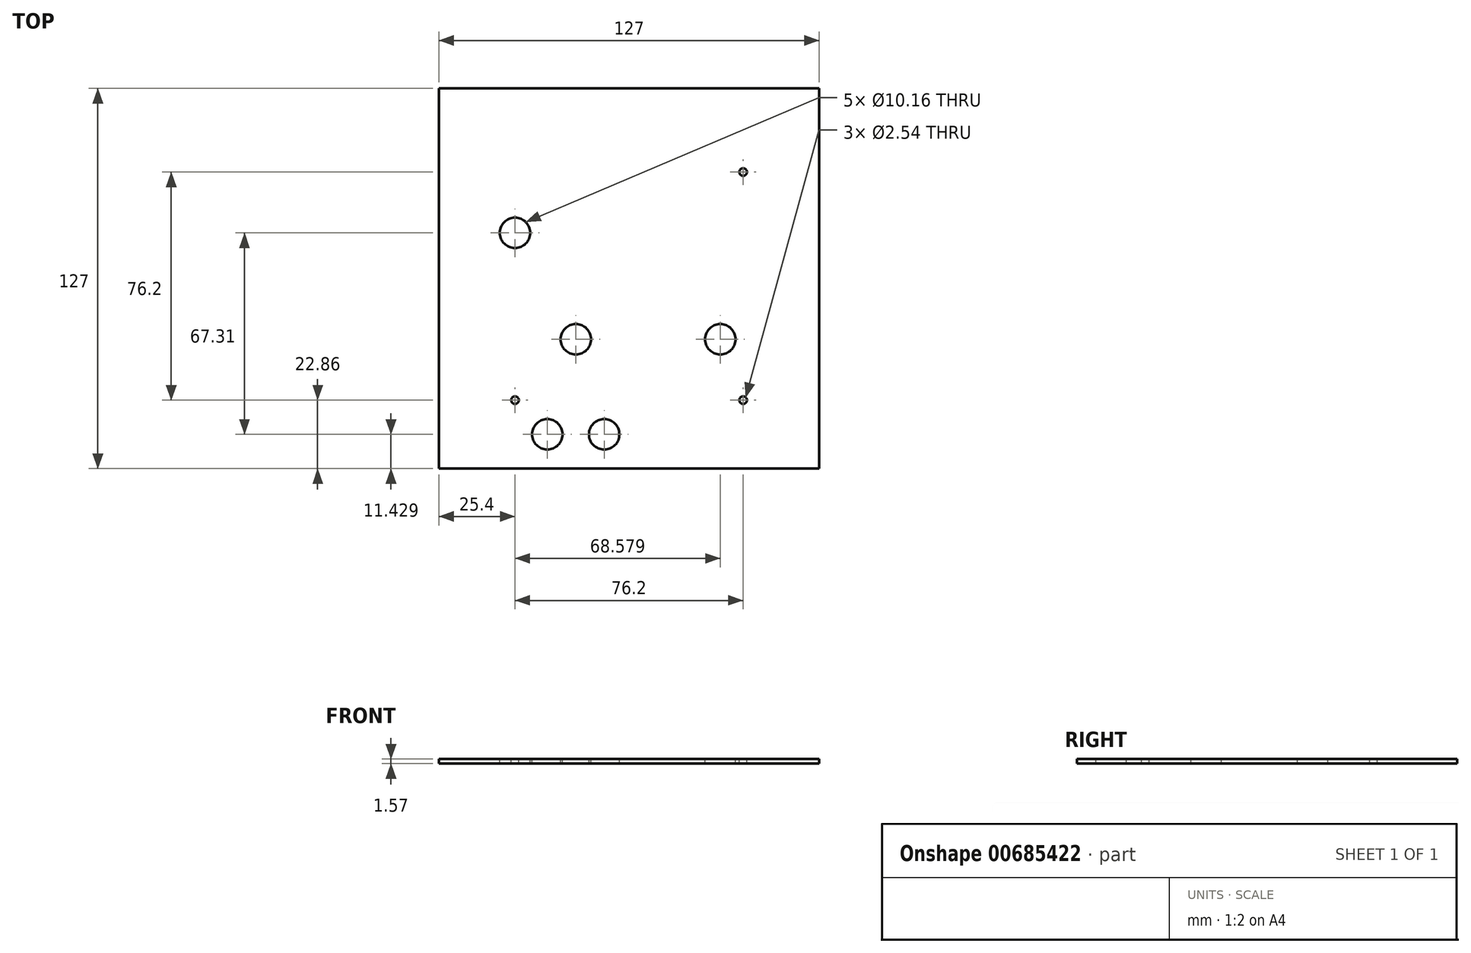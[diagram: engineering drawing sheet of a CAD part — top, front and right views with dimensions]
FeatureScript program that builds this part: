
annotation { "Feature Type Name" : "Feature", "Feature Type Description" : "" }
export const myFeature = defineFeature(function(context is Context, id is Id, definition is map)
    precondition{}
    {
        {
            var Q0;
            Q0=qCreatedBy(makeId("Top.planeOp"),FACE);
            var sketch = newSketch(context, id + "F0", { "sketchPlane" : qUnion([Q0])});
            skLineSegment(sketch, "E0", {"start": v(-9.04, 13.82) * mm, "end": v(-9.04, 13.7) * mm});
            skLineSegment(sketch, "E1", {"start": v(-9.04, 13.7) * mm, "end": v(-9.28, 13.35) * mm});
            skLineSegment(sketch, "E2", {"start": v(-9.28, 13.35) * mm, "end": v(-9.32, 13.32) * mm});
            skLineSegment(sketch, "E3", {"start": v(-9.32, 13.32) * mm, "end": v(-9.37, 13.3) * mm});
            skLineSegment(sketch, "E4", {"start": v(-9.37, 13.3) * mm, "end": v(-9.85, 13.3) * mm});
            skLineSegment(sketch, "E5", {"start": v(-9.85, 13.3) * mm, "end": v(-9.9, 13.32) * mm});
            skLineSegment(sketch, "E6", {"start": v(-9.9, 13.32) * mm, "end": v(-9.94, 13.35) * mm});
            skLineSegment(sketch, "E7", {"start": v(-9.94, 13.35) * mm, "end": v(-10.18, 13.7) * mm});
            skLineSegment(sketch, "E8", {"start": v(-10.18, 13.7) * mm, "end": v(-10.18, 13.82) * mm});
            skLineSegment(sketch, "E9", {"start": v(-10.18, 13.82) * mm, "end": v(-10.18, 13.94) * mm});
            skLineSegment(sketch, "E10", {"start": v(-10.18, 13.94) * mm, "end": v(-9.94, 14.3) * mm});
            skLineSegment(sketch, "E11", {"start": v(-9.94, 14.3) * mm, "end": v(-9.9, 14.31) * mm});
            skLineSegment(sketch, "E12", {"start": v(-9.9, 14.31) * mm, "end": v(-9.85, 14.34) * mm});
            skLineSegment(sketch, "E13", {"start": v(-9.85, 14.34) * mm, "end": v(-9.37, 14.34) * mm});
            skLineSegment(sketch, "E14", {"start": v(-9.37, 14.34) * mm, "end": v(-9.32, 14.31) * mm});
            skLineSegment(sketch, "E15", {"start": v(-9.32, 14.31) * mm, "end": v(-9.28, 14.3) * mm});
            skLineSegment(sketch, "E16", {"start": v(-9.28, 14.3) * mm, "end": v(-9.04, 13.94) * mm});
            skLineSegment(sketch, "E17", {"start": v(-9.04, 13.94) * mm, "end": v(-9.04, 13.82) * mm});
            skLineSegment(sketch, "E18", {"start": v(-52.06, -1.27) * mm, "end": v(-52.06, -1.46) * mm});
            skLineSegment(sketch, "E19", {"start": v(-52.06, -1.46) * mm, "end": v(-52.26, -2.02) * mm});
            skLineSegment(sketch, "E20", {"start": v(-52.26, -2.02) * mm, "end": v(-52.7, -2.5) * mm});
            skLineSegment(sketch, "E21", {"start": v(-52.7, -2.5) * mm, "end": v(-52.8, -2.57) * mm});
            skLineSegment(sketch, "E22", {"start": v(-52.8, -2.57) * mm, "end": v(-52.93, -2.63) * mm});
            skLineSegment(sketch, "E23", {"start": v(-52.93, -2.63) * mm, "end": v(-53.56, -2.77) * mm});
            skLineSegment(sketch, "E24", {"start": v(-53.56, -2.77) * mm, "end": v(-54.2, -2.63) * mm});
            skLineSegment(sketch, "E25", {"start": v(-54.2, -2.63) * mm, "end": v(-54.3, -2.57) * mm});
            skLineSegment(sketch, "E26", {"start": v(-54.3, -2.57) * mm, "end": v(-54.43, -2.5) * mm});
            skLineSegment(sketch, "E27", {"start": v(-54.43, -2.5) * mm, "end": v(-54.86, -2.02) * mm});
            skLineSegment(sketch, "E28", {"start": v(-54.86, -2.02) * mm, "end": v(-55.06, -1.46) * mm});
            skLineSegment(sketch, "E29", {"start": v(-55.06, -1.46) * mm, "end": v(-55.06, -1.27) * mm});
            skLineSegment(sketch, "E30", {"start": v(-55.06, -1.27) * mm, "end": v(-55.06, -1.08) * mm});
            skLineSegment(sketch, "E31", {"start": v(-55.06, -1.08) * mm, "end": v(-54.86, -0.52) * mm});
            skLineSegment(sketch, "E32", {"start": v(-54.86, -0.52) * mm, "end": v(-54.43, -0.04) * mm});
            skLineSegment(sketch, "E33", {"start": v(-54.43, -0.04) * mm, "end": v(-54.3, 0.03) * mm});
            skLineSegment(sketch, "E34", {"start": v(-54.3, 0.03) * mm, "end": v(-54.2, 0.1) * mm});
            skLineSegment(sketch, "E35", {"start": v(-54.2, 0.1) * mm, "end": v(-53.56, 0.23) * mm});
            skLineSegment(sketch, "E36", {"start": v(-53.56, 0.23) * mm, "end": v(-52.93, 0.1) * mm});
            skLineSegment(sketch, "E37", {"start": v(-52.93, 0.1) * mm, "end": v(-52.8, 0.03) * mm});
            skLineSegment(sketch, "E38", {"start": v(-52.8, 0.03) * mm, "end": v(-52.7, -0.04) * mm});
            skLineSegment(sketch, "E39", {"start": v(-52.7, -0.04) * mm, "end": v(-52.26, -0.52) * mm});
            skLineSegment(sketch, "E40", {"start": v(-52.26, -0.52) * mm, "end": v(-52.06, -1.08) * mm});
            skLineSegment(sketch, "E41", {"start": v(-52.06, -1.08) * mm, "end": v(-52.06, -1.27) * mm});
            skLineSegment(sketch, "E42", {"start": v(-52.06, -9.17) * mm, "end": v(-52.06, -9.36) * mm});
            skLineSegment(sketch, "E43", {"start": v(-52.06, -9.36) * mm, "end": v(-52.26, -9.92) * mm});
            skLineSegment(sketch, "E44", {"start": v(-52.26, -9.92) * mm, "end": v(-52.7, -10.4) * mm});
            skLineSegment(sketch, "E45", {"start": v(-52.7, -10.4) * mm, "end": v(-52.8, -10.47) * mm});
            skLineSegment(sketch, "E46", {"start": v(-52.8, -10.47) * mm, "end": v(-52.93, -10.54) * mm});
            skLineSegment(sketch, "E47", {"start": v(-52.93, -10.54) * mm, "end": v(-53.56, -10.67) * mm});
            skLineSegment(sketch, "E48", {"start": v(-53.56, -10.67) * mm, "end": v(-54.2, -10.54) * mm});
            skLineSegment(sketch, "E49", {"start": v(-54.2, -10.54) * mm, "end": v(-54.3, -10.47) * mm});
            skLineSegment(sketch, "E50", {"start": v(-54.3, -10.47) * mm, "end": v(-54.43, -10.4) * mm});
            skLineSegment(sketch, "E51", {"start": v(-54.43, -10.4) * mm, "end": v(-54.86, -9.92) * mm});
            skLineSegment(sketch, "E52", {"start": v(-54.86, -9.92) * mm, "end": v(-55.06, -9.36) * mm});
            skLineSegment(sketch, "E53", {"start": v(-55.06, -9.36) * mm, "end": v(-55.06, -9.17) * mm});
            skLineSegment(sketch, "E54", {"start": v(-55.06, -9.17) * mm, "end": v(-55.06, -8.98) * mm});
            skLineSegment(sketch, "E55", {"start": v(-55.06, -8.98) * mm, "end": v(-54.86, -8.42) * mm});
            skLineSegment(sketch, "E56", {"start": v(-54.86, -8.42) * mm, "end": v(-54.43, -7.94) * mm});
            skLineSegment(sketch, "E57", {"start": v(-54.43, -7.94) * mm, "end": v(-54.3, -7.87) * mm});
            skLineSegment(sketch, "E58", {"start": v(-54.3, -7.87) * mm, "end": v(-54.2, -7.8) * mm});
            skLineSegment(sketch, "E59", {"start": v(-54.2, -7.8) * mm, "end": v(-53.56, -7.67) * mm});
            skLineSegment(sketch, "E60", {"start": v(-53.56, -7.67) * mm, "end": v(-52.93, -7.8) * mm});
            skLineSegment(sketch, "E61", {"start": v(-52.93, -7.8) * mm, "end": v(-52.8, -7.87) * mm});
            skLineSegment(sketch, "E62", {"start": v(-52.8, -7.87) * mm, "end": v(-52.7, -7.94) * mm});
            skLineSegment(sketch, "E63", {"start": v(-52.7, -7.94) * mm, "end": v(-52.26, -8.42) * mm});
            skLineSegment(sketch, "E64", {"start": v(-52.26, -8.42) * mm, "end": v(-52.06, -8.98) * mm});
            skLineSegment(sketch, "E65", {"start": v(-52.06, -8.98) * mm, "end": v(-52.06, -9.17) * mm});
            skLineSegment(sketch, "E66", {"start": v(-38.7, 57.1) * mm, "end": v(-38.7, 56.77) * mm});
            skLineSegment(sketch, "E67", {"start": v(-38.7, 56.77) * mm, "end": v(-38.87, 55.78) * mm});
            skLineSegment(sketch, "E68", {"start": v(-38.87, 55.78) * mm, "end": v(-39.38, 54.56) * mm});
            skLineSegment(sketch, "E69", {"start": v(-39.38, 54.56) * mm, "end": v(-40.18, 53.52) * mm});
            skLineSegment(sketch, "E70", {"start": v(-40.18, 53.52) * mm, "end": v(-40.95, 52.87) * mm});
            skLineSegment(sketch, "E71", {"start": v(-40.95, 52.87) * mm, "end": v(-41.24, 52.7) * mm});
            skLineSegment(sketch, "E72", {"start": v(-41.24, 52.7) * mm, "end": v(-41.52, 52.53) * mm});
            skLineSegment(sketch, "E73", {"start": v(-41.52, 52.53) * mm, "end": v(-42.47, 52.2) * mm});
            skLineSegment(sketch, "E74", {"start": v(-42.47, 52.2) * mm, "end": v(-43.78, 52.02) * mm});
            skLineSegment(sketch, "E75", {"start": v(-43.78, 52.02) * mm, "end": v(-45.08, 52.2) * mm});
            skLineSegment(sketch, "E76", {"start": v(-45.08, 52.2) * mm, "end": v(-46.03, 52.53) * mm});
            skLineSegment(sketch, "E77", {"start": v(-46.03, 52.53) * mm, "end": v(-46.32, 52.7) * mm});
            skLineSegment(sketch, "E78", {"start": v(-46.32, 52.7) * mm, "end": v(-46.6, 52.87) * mm});
            skLineSegment(sketch, "E79", {"start": v(-46.6, 52.87) * mm, "end": v(-47.38, 53.52) * mm});
            skLineSegment(sketch, "E80", {"start": v(-47.38, 53.52) * mm, "end": v(-48.18, 54.56) * mm});
            skLineSegment(sketch, "E81", {"start": v(-48.18, 54.56) * mm, "end": v(-48.68, 55.78) * mm});
            skLineSegment(sketch, "E82", {"start": v(-48.68, 55.78) * mm, "end": v(-48.86, 56.77) * mm});
            skLineSegment(sketch, "E83", {"start": v(-48.86, 56.77) * mm, "end": v(-48.86, 57.1) * mm});
            skLineSegment(sketch, "E84", {"start": v(-48.86, 57.1) * mm, "end": v(-48.86, 57.43) * mm});
            skLineSegment(sketch, "E85", {"start": v(-48.86, 57.43) * mm, "end": v(-48.68, 58.43) * mm});
            skLineSegment(sketch, "E86", {"start": v(-48.68, 58.43) * mm, "end": v(-48.18, 59.64) * mm});
            skLineSegment(sketch, "E87", {"start": v(-48.18, 59.64) * mm, "end": v(-47.38, 60.68) * mm});
            skLineSegment(sketch, "E88", {"start": v(-47.38, 60.68) * mm, "end": v(-46.6, 61.33) * mm});
            skLineSegment(sketch, "E89", {"start": v(-46.6, 61.33) * mm, "end": v(-46.32, 61.5) * mm});
            skLineSegment(sketch, "E90", {"start": v(-46.32, 61.5) * mm, "end": v(-46.03, 61.67) * mm});
            skLineSegment(sketch, "E91", {"start": v(-46.03, 61.67) * mm, "end": v(-45.08, 62.01) * mm});
            skLineSegment(sketch, "E92", {"start": v(-45.08, 62.01) * mm, "end": v(-43.78, 62.18) * mm});
            skLineSegment(sketch, "E93", {"start": v(-43.78, 62.18) * mm, "end": v(-42.47, 62.01) * mm});
            skLineSegment(sketch, "E94", {"start": v(-42.47, 62.01) * mm, "end": v(-41.52, 61.67) * mm});
            skLineSegment(sketch, "E95", {"start": v(-41.52, 61.67) * mm, "end": v(-41.24, 61.5) * mm});
            skLineSegment(sketch, "E96", {"start": v(-41.24, 61.5) * mm, "end": v(-40.95, 61.33) * mm});
            skLineSegment(sketch, "E97", {"start": v(-40.95, 61.33) * mm, "end": v(-40.18, 60.68) * mm});
            skLineSegment(sketch, "E98", {"start": v(-40.18, 60.68) * mm, "end": v(-39.38, 59.64) * mm});
            skLineSegment(sketch, "E99", {"start": v(-39.38, 59.64) * mm, "end": v(-38.87, 58.43) * mm});
            skLineSegment(sketch, "E100", {"start": v(-38.87, 58.43) * mm, "end": v(-38.7, 57.43) * mm});
            skLineSegment(sketch, "E101", {"start": v(-38.7, 57.43) * mm, "end": v(-38.7, 57.1) * mm});
            skLineSegment(sketch, "E102", {"start": v(-38.78, 38.1) * mm, "end": v(-38.78, 37.77) * mm});
            skLineSegment(sketch, "E103", {"start": v(-38.78, 37.77) * mm, "end": v(-38.95, 36.8) * mm});
            skLineSegment(sketch, "E104", {"start": v(-38.95, 36.8) * mm, "end": v(-39.45, 35.6) * mm});
            skLineSegment(sketch, "E105", {"start": v(-39.45, 35.6) * mm, "end": v(-40.23, 34.57) * mm});
            skLineSegment(sketch, "E106", {"start": v(-40.23, 34.57) * mm, "end": v(-41, 33.93) * mm});
            skLineSegment(sketch, "E107", {"start": v(-41, 33.93) * mm, "end": v(-41.28, 33.77) * mm});
            skLineSegment(sketch, "E108", {"start": v(-41.28, 33.77) * mm, "end": v(-41.56, 33.6) * mm});
            skLineSegment(sketch, "E109", {"start": v(-41.56, 33.6) * mm, "end": v(-42.5, 33.27) * mm});
            skLineSegment(sketch, "E110", {"start": v(-42.5, 33.27) * mm, "end": v(-43.78, 33.1) * mm});
            skLineSegment(sketch, "E111", {"start": v(-43.78, 33.1) * mm, "end": v(-45.06, 33.27) * mm});
            skLineSegment(sketch, "E112", {"start": v(-45.06, 33.27) * mm, "end": v(-46, 33.6) * mm});
            skLineSegment(sketch, "E113", {"start": v(-46, 33.6) * mm, "end": v(-46.28, 33.77) * mm});
            skLineSegment(sketch, "E114", {"start": v(-46.28, 33.77) * mm, "end": v(-46.56, 33.93) * mm});
            skLineSegment(sketch, "E115", {"start": v(-46.56, 33.93) * mm, "end": v(-47.32, 34.57) * mm});
            skLineSegment(sketch, "E116", {"start": v(-47.32, 34.57) * mm, "end": v(-48.1, 35.6) * mm});
            skLineSegment(sketch, "E117", {"start": v(-48.1, 35.6) * mm, "end": v(-48.6, 36.8) * mm});
            skLineSegment(sketch, "E118", {"start": v(-48.6, 36.8) * mm, "end": v(-48.78, 37.77) * mm});
            skLineSegment(sketch, "E119", {"start": v(-48.78, 37.77) * mm, "end": v(-48.78, 38.1) * mm});
            skLineSegment(sketch, "E120", {"start": v(-48.78, 38.1) * mm, "end": v(-48.78, 38.43) * mm});
            skLineSegment(sketch, "E121", {"start": v(-48.78, 38.43) * mm, "end": v(-48.6, 39.4) * mm});
            skLineSegment(sketch, "E122", {"start": v(-48.6, 39.4) * mm, "end": v(-48.1, 40.6) * mm});
            skLineSegment(sketch, "E123", {"start": v(-48.1, 40.6) * mm, "end": v(-47.32, 41.63) * mm});
            skLineSegment(sketch, "E124", {"start": v(-47.32, 41.63) * mm, "end": v(-46.56, 42.27) * mm});
            skLineSegment(sketch, "E125", {"start": v(-46.56, 42.27) * mm, "end": v(-46.28, 42.43) * mm});
            skLineSegment(sketch, "E126", {"start": v(-46.28, 42.43) * mm, "end": v(-46, 42.6) * mm});
            skLineSegment(sketch, "E127", {"start": v(-46, 42.6) * mm, "end": v(-45.06, 42.93) * mm});
            skLineSegment(sketch, "E128", {"start": v(-45.06, 42.93) * mm, "end": v(-43.78, 43.1) * mm});
            skLineSegment(sketch, "E129", {"start": v(-43.78, 43.1) * mm, "end": v(-42.5, 42.93) * mm});
            skLineSegment(sketch, "E130", {"start": v(-42.5, 42.93) * mm, "end": v(-41.56, 42.6) * mm});
            skLineSegment(sketch, "E131", {"start": v(-41.56, 42.6) * mm, "end": v(-41.28, 42.43) * mm});
            skLineSegment(sketch, "E132", {"start": v(-41.28, 42.43) * mm, "end": v(-41, 42.27) * mm});
            skLineSegment(sketch, "E133", {"start": v(-41, 42.27) * mm, "end": v(-40.23, 41.63) * mm});
            skLineSegment(sketch, "E134", {"start": v(-40.23, 41.63) * mm, "end": v(-39.45, 40.6) * mm});
            skLineSegment(sketch, "E135", {"start": v(-39.45, 40.6) * mm, "end": v(-38.95, 39.4) * mm});
            skLineSegment(sketch, "E136", {"start": v(-38.95, 39.4) * mm, "end": v(-38.78, 38.43) * mm});
            skLineSegment(sketch, "E137", {"start": v(-38.78, 38.43) * mm, "end": v(-38.78, 38.1) * mm});
            skLineSegment(sketch, "E138", {"start": v(50.96, 58.44) * mm, "end": v(49.45, 58.44) * mm});
            skLineSegment(sketch, "E139", {"start": v(46.74, 53.34) * mm, "end": v(46.74, 53.24) * mm});
            skLineSegment(sketch, "E140", {"start": v(46.74, 53.24) * mm, "end": v(46.63, 52.94) * mm});
            skLineSegment(sketch, "E141", {"start": v(46.63, 52.94) * mm, "end": v(46.4, 52.68) * mm});
            skLineSegment(sketch, "E142", {"start": v(46.4, 52.68) * mm, "end": v(46.34, 52.65) * mm});
            skLineSegment(sketch, "E143", {"start": v(46.34, 52.65) * mm, "end": v(46.28, 52.61) * mm});
            skLineSegment(sketch, "E144", {"start": v(46.28, 52.61) * mm, "end": v(45.6, 52.61) * mm});
            skLineSegment(sketch, "E145", {"start": v(45.6, 52.61) * mm, "end": v(45.54, 52.65) * mm});
            skLineSegment(sketch, "E146", {"start": v(45.54, 52.65) * mm, "end": v(45.48, 52.68) * mm});
            skLineSegment(sketch, "E147", {"start": v(45.48, 52.68) * mm, "end": v(45.25, 52.94) * mm});
            skLineSegment(sketch, "E148", {"start": v(45.25, 52.94) * mm, "end": v(45.14, 53.24) * mm});
            skLineSegment(sketch, "E149", {"start": v(45.14, 53.24) * mm, "end": v(45.14, 53.34) * mm});
            skLineSegment(sketch, "E150", {"start": v(45.14, 53.34) * mm, "end": v(45.14, 53.44) * mm});
            skLineSegment(sketch, "E151", {"start": v(45.14, 53.44) * mm, "end": v(45.25, 53.74) * mm});
            skLineSegment(sketch, "E152", {"start": v(45.25, 53.74) * mm, "end": v(45.48, 54) * mm});
            skLineSegment(sketch, "E153", {"start": v(45.48, 54) * mm, "end": v(45.54, 54.03) * mm});
            skLineSegment(sketch, "E154", {"start": v(45.54, 54.03) * mm, "end": v(45.6, 54.07) * mm});
            skLineSegment(sketch, "E155", {"start": v(45.6, 54.07) * mm, "end": v(46.28, 54.07) * mm});
            skLineSegment(sketch, "E156", {"start": v(46.28, 54.07) * mm, "end": v(46.34, 54.03) * mm});
            skLineSegment(sketch, "E157", {"start": v(46.34, 54.03) * mm, "end": v(46.4, 54) * mm});
            skLineSegment(sketch, "E158", {"start": v(46.4, 54) * mm, "end": v(46.63, 53.74) * mm});
            skLineSegment(sketch, "E159", {"start": v(46.63, 53.74) * mm, "end": v(46.74, 53.44) * mm});
            skLineSegment(sketch, "E160", {"start": v(46.74, 53.44) * mm, "end": v(46.74, 53.34) * mm});
            skLineSegment(sketch, "E161", {"start": v(50.96, 48.24) * mm, "end": v(49.45, 48.24) * mm});
            skLineSegment(sketch, "E162", {"start": v(46.74, 55.84) * mm, "end": v(46.74, 55.74) * mm});
            skLineSegment(sketch, "E163", {"start": v(46.74, 55.74) * mm, "end": v(46.63, 55.44) * mm});
            skLineSegment(sketch, "E164", {"start": v(46.63, 55.44) * mm, "end": v(46.4, 55.18) * mm});
            skLineSegment(sketch, "E165", {"start": v(46.4, 55.18) * mm, "end": v(46.34, 55.15) * mm});
            skLineSegment(sketch, "E166", {"start": v(46.34, 55.15) * mm, "end": v(46.28, 55.11) * mm});
            skLineSegment(sketch, "E167", {"start": v(46.28, 55.11) * mm, "end": v(45.6, 55.11) * mm});
            skLineSegment(sketch, "E168", {"start": v(45.6, 55.11) * mm, "end": v(45.54, 55.15) * mm});
            skLineSegment(sketch, "E169", {"start": v(45.54, 55.15) * mm, "end": v(45.48, 55.18) * mm});
            skLineSegment(sketch, "E170", {"start": v(45.48, 55.18) * mm, "end": v(45.25, 55.44) * mm});
            skLineSegment(sketch, "E171", {"start": v(45.25, 55.44) * mm, "end": v(45.14, 55.74) * mm});
            skLineSegment(sketch, "E172", {"start": v(45.14, 55.74) * mm, "end": v(45.14, 55.84) * mm});
            skLineSegment(sketch, "E173", {"start": v(45.14, 55.84) * mm, "end": v(45.14, 55.94) * mm});
            skLineSegment(sketch, "E174", {"start": v(45.14, 55.94) * mm, "end": v(45.25, 56.24) * mm});
            skLineSegment(sketch, "E175", {"start": v(45.25, 56.24) * mm, "end": v(45.48, 56.5) * mm});
            skLineSegment(sketch, "E176", {"start": v(45.48, 56.5) * mm, "end": v(45.54, 56.53) * mm});
            skLineSegment(sketch, "E177", {"start": v(45.54, 56.53) * mm, "end": v(45.6, 56.57) * mm});
            skLineSegment(sketch, "E178", {"start": v(45.6, 56.57) * mm, "end": v(46.28, 56.57) * mm});
            skLineSegment(sketch, "E179", {"start": v(46.28, 56.57) * mm, "end": v(46.34, 56.53) * mm});
            skLineSegment(sketch, "E180", {"start": v(46.34, 56.53) * mm, "end": v(46.4, 56.5) * mm});
            skLineSegment(sketch, "E181", {"start": v(46.4, 56.5) * mm, "end": v(46.63, 56.24) * mm});
            skLineSegment(sketch, "E182", {"start": v(46.63, 56.24) * mm, "end": v(46.74, 55.94) * mm});
            skLineSegment(sketch, "E183", {"start": v(46.74, 55.94) * mm, "end": v(46.74, 55.84) * mm});
            skLineSegment(sketch, "E184", {"start": v(49.7, -59.2) * mm, "end": v(49.7, -59.51) * mm});
            skLineSegment(sketch, "E185", {"start": v(52.24, -59.2) * mm, "end": v(52.24, -59.51) * mm});
            skLineSegment(sketch, "E186", {"start": v(54.77, -59.2) * mm, "end": v(54.77, -59.51) * mm});
            skLineSegment(sketch, "E187", {"start": v(57.31, -59.2) * mm, "end": v(57.31, -59.51) * mm});
            skLineSegment(sketch, "E188", {"start": v(59.85, -59.2) * mm, "end": v(59.85, -59.51) * mm});
            skLineSegment(sketch, "E189", {"start": v(50.96, 40.66) * mm, "end": v(49.45, 40.66) * mm});
            skLineSegment(sketch, "E190", {"start": v(46.74, 35.56) * mm, "end": v(46.74, 35.46) * mm});
            skLineSegment(sketch, "E191", {"start": v(46.74, 35.46) * mm, "end": v(46.63, 35.16) * mm});
            skLineSegment(sketch, "E192", {"start": v(46.63, 35.16) * mm, "end": v(46.4, 34.9) * mm});
            skLineSegment(sketch, "E193", {"start": v(46.4, 34.9) * mm, "end": v(46.34, 34.87) * mm});
            skLineSegment(sketch, "E194", {"start": v(46.34, 34.87) * mm, "end": v(46.28, 34.83) * mm});
            skLineSegment(sketch, "E195", {"start": v(46.28, 34.83) * mm, "end": v(45.6, 34.83) * mm});
            skLineSegment(sketch, "E196", {"start": v(45.6, 34.83) * mm, "end": v(45.54, 34.87) * mm});
            skLineSegment(sketch, "E197", {"start": v(45.54, 34.87) * mm, "end": v(45.48, 34.9) * mm});
            skLineSegment(sketch, "E198", {"start": v(45.48, 34.9) * mm, "end": v(45.25, 35.16) * mm});
            skLineSegment(sketch, "E199", {"start": v(45.25, 35.16) * mm, "end": v(45.14, 35.46) * mm});
            skLineSegment(sketch, "E200", {"start": v(45.14, 35.46) * mm, "end": v(45.14, 35.56) * mm});
            skLineSegment(sketch, "E201", {"start": v(45.14, 35.56) * mm, "end": v(45.14, 35.66) * mm});
            skLineSegment(sketch, "E202", {"start": v(45.14, 35.66) * mm, "end": v(45.25, 35.96) * mm});
            skLineSegment(sketch, "E203", {"start": v(45.25, 35.96) * mm, "end": v(45.48, 36.22) * mm});
            skLineSegment(sketch, "E204", {"start": v(45.48, 36.22) * mm, "end": v(45.54, 36.25) * mm});
            skLineSegment(sketch, "E205", {"start": v(45.54, 36.25) * mm, "end": v(45.6, 36.29) * mm});
            skLineSegment(sketch, "E206", {"start": v(45.6, 36.29) * mm, "end": v(46.28, 36.29) * mm});
            skLineSegment(sketch, "E207", {"start": v(46.28, 36.29) * mm, "end": v(46.34, 36.25) * mm});
            skLineSegment(sketch, "E208", {"start": v(46.34, 36.25) * mm, "end": v(46.4, 36.22) * mm});
            skLineSegment(sketch, "E209", {"start": v(46.4, 36.22) * mm, "end": v(46.63, 35.96) * mm});
            skLineSegment(sketch, "E210", {"start": v(46.63, 35.96) * mm, "end": v(46.74, 35.66) * mm});
            skLineSegment(sketch, "E211", {"start": v(46.74, 35.66) * mm, "end": v(46.74, 35.56) * mm});
            skLineSegment(sketch, "E212", {"start": v(50.96, 30.46) * mm, "end": v(49.45, 30.46) * mm});
            skLineSegment(sketch, "E213", {"start": v(46.74, 38.06) * mm, "end": v(46.74, 37.96) * mm});
            skLineSegment(sketch, "E214", {"start": v(46.74, 37.96) * mm, "end": v(46.63, 37.66) * mm});
            skLineSegment(sketch, "E215", {"start": v(46.63, 37.66) * mm, "end": v(46.4, 37.4) * mm});
            skLineSegment(sketch, "E216", {"start": v(46.4, 37.4) * mm, "end": v(46.34, 37.37) * mm});
            skLineSegment(sketch, "E217", {"start": v(46.34, 37.37) * mm, "end": v(46.28, 37.33) * mm});
            skLineSegment(sketch, "E218", {"start": v(46.28, 37.33) * mm, "end": v(45.6, 37.33) * mm});
            skLineSegment(sketch, "E219", {"start": v(45.6, 37.33) * mm, "end": v(45.54, 37.37) * mm});
            skLineSegment(sketch, "E220", {"start": v(45.54, 37.37) * mm, "end": v(45.48, 37.4) * mm});
            skLineSegment(sketch, "E221", {"start": v(45.48, 37.4) * mm, "end": v(45.25, 37.66) * mm});
            skLineSegment(sketch, "E222", {"start": v(45.25, 37.66) * mm, "end": v(45.14, 37.96) * mm});
            skLineSegment(sketch, "E223", {"start": v(45.14, 37.96) * mm, "end": v(45.14, 38.06) * mm});
            skLineSegment(sketch, "E224", {"start": v(45.14, 38.06) * mm, "end": v(45.14, 38.16) * mm});
            skLineSegment(sketch, "E225", {"start": v(45.14, 38.16) * mm, "end": v(45.25, 38.46) * mm});
            skLineSegment(sketch, "E226", {"start": v(45.25, 38.46) * mm, "end": v(45.48, 38.72) * mm});
            skLineSegment(sketch, "E227", {"start": v(45.48, 38.72) * mm, "end": v(45.54, 38.75) * mm});
            skLineSegment(sketch, "E228", {"start": v(45.54, 38.75) * mm, "end": v(45.6, 38.79) * mm});
            skLineSegment(sketch, "E229", {"start": v(45.6, 38.79) * mm, "end": v(46.28, 38.79) * mm});
            skLineSegment(sketch, "E230", {"start": v(46.28, 38.79) * mm, "end": v(46.34, 38.75) * mm});
            skLineSegment(sketch, "E231", {"start": v(46.34, 38.75) * mm, "end": v(46.4, 38.72) * mm});
            skLineSegment(sketch, "E232", {"start": v(46.4, 38.72) * mm, "end": v(46.63, 38.46) * mm});
            skLineSegment(sketch, "E233", {"start": v(46.63, 38.46) * mm, "end": v(46.74, 38.16) * mm});
            skLineSegment(sketch, "E234", {"start": v(46.74, 38.16) * mm, "end": v(46.74, 38.06) * mm});
            skLineSegment(sketch, "E235", {"start": v(-60.14, 41.76) * mm, "end": v(-60.14, 41.62) * mm});
            skLineSegment(sketch, "E236", {"start": v(-60.14, 41.62) * mm, "end": v(-60.43, 41.21) * mm});
            skLineSegment(sketch, "E237", {"start": v(-60.43, 41.21) * mm, "end": v(-60.48, 41.18) * mm});
            skLineSegment(sketch, "E238", {"start": v(-60.48, 41.18) * mm, "end": v(-60.53, 41.15) * mm});
            skLineSegment(sketch, "E239", {"start": v(-60.53, 41.15) * mm, "end": v(-61.1, 41.15) * mm});
            skLineSegment(sketch, "E240", {"start": v(-61.1, 41.15) * mm, "end": v(-61.16, 41.18) * mm});
            skLineSegment(sketch, "E241", {"start": v(-61.16, 41.18) * mm, "end": v(-61.2, 41.21) * mm});
            skLineSegment(sketch, "E242", {"start": v(-61.2, 41.21) * mm, "end": v(-61.5, 41.63) * mm});
            skLineSegment(sketch, "E243", {"start": v(-61.5, 41.63) * mm, "end": v(-61.5, 41.76) * mm});
            skLineSegment(sketch, "E244", {"start": v(-61.5, 41.76) * mm, "end": v(-61.5, 41.91) * mm});
            skLineSegment(sketch, "E245", {"start": v(-61.5, 41.91) * mm, "end": v(-61.2, 42.32) * mm});
            skLineSegment(sketch, "E246", {"start": v(-61.2, 42.32) * mm, "end": v(-61.16, 42.35) * mm});
            skLineSegment(sketch, "E247", {"start": v(-61.16, 42.35) * mm, "end": v(-61.1, 42.38) * mm});
            skLineSegment(sketch, "E248", {"start": v(-61.1, 42.38) * mm, "end": v(-60.53, 42.38) * mm});
            skLineSegment(sketch, "E249", {"start": v(-60.53, 42.38) * mm, "end": v(-60.48, 42.35) * mm});
            skLineSegment(sketch, "E250", {"start": v(-60.48, 42.35) * mm, "end": v(-60.43, 42.32) * mm});
            skLineSegment(sketch, "E251", {"start": v(-60.43, 42.32) * mm, "end": v(-60.14, 41.9) * mm});
            skLineSegment(sketch, "E252", {"start": v(-60.14, 41.9) * mm, "end": v(-60.14, 41.76) * mm});
            skLineSegment(sketch, "E253", {"start": v(-60.14, 52.8) * mm, "end": v(-60.14, 52.65) * mm});
            skLineSegment(sketch, "E254", {"start": v(-60.14, 52.65) * mm, "end": v(-60.43, 52.25) * mm});
            skLineSegment(sketch, "E255", {"start": v(-60.43, 52.25) * mm, "end": v(-60.48, 52.22) * mm});
            skLineSegment(sketch, "E256", {"start": v(-60.48, 52.22) * mm, "end": v(-60.53, 52.19) * mm});
            skLineSegment(sketch, "E257", {"start": v(-60.53, 52.19) * mm, "end": v(-61.1, 52.19) * mm});
            skLineSegment(sketch, "E258", {"start": v(-61.1, 52.19) * mm, "end": v(-61.16, 52.22) * mm});
            skLineSegment(sketch, "E259", {"start": v(-61.16, 52.22) * mm, "end": v(-61.2, 52.25) * mm});
            skLineSegment(sketch, "E260", {"start": v(-61.2, 52.25) * mm, "end": v(-61.5, 52.66) * mm});
            skLineSegment(sketch, "E261", {"start": v(-61.5, 52.66) * mm, "end": v(-61.5, 52.8) * mm});
            skLineSegment(sketch, "E262", {"start": v(-61.5, 52.8) * mm, "end": v(-61.5, 52.95) * mm});
            skLineSegment(sketch, "E263", {"start": v(-61.5, 52.95) * mm, "end": v(-61.2, 53.35) * mm});
            skLineSegment(sketch, "E264", {"start": v(-61.2, 53.35) * mm, "end": v(-61.16, 53.39) * mm});
            skLineSegment(sketch, "E265", {"start": v(-61.16, 53.39) * mm, "end": v(-61.1, 53.42) * mm});
            skLineSegment(sketch, "E266", {"start": v(-61.1, 53.42) * mm, "end": v(-60.53, 53.42) * mm});
            skLineSegment(sketch, "E267", {"start": v(-60.53, 53.42) * mm, "end": v(-60.48, 53.39) * mm});
            skLineSegment(sketch, "E268", {"start": v(-60.48, 53.39) * mm, "end": v(-60.43, 53.35) * mm});
            skLineSegment(sketch, "E269", {"start": v(-60.43, 53.35) * mm, "end": v(-60.14, 52.94) * mm});
            skLineSegment(sketch, "E270", {"start": v(-60.14, 52.94) * mm, "end": v(-60.14, 52.8) * mm});
            skLineSegment(sketch, "E271", {"start": v(-3.08, -52.07) * mm, "end": v(-3.08, -52.4) * mm});
            skLineSegment(sketch, "E272", {"start": v(-3.08, -52.4) * mm, "end": v(-3.26, -53.4) * mm});
            skLineSegment(sketch, "E273", {"start": v(-3.26, -53.4) * mm, "end": v(-3.77, -54.61) * mm});
            skLineSegment(sketch, "E274", {"start": v(-3.77, -54.61) * mm, "end": v(-4.56, -55.65) * mm});
            skLineSegment(sketch, "E275", {"start": v(-4.56, -55.65) * mm, "end": v(-5.34, -56.3) * mm});
            skLineSegment(sketch, "E276", {"start": v(-5.34, -56.3) * mm, "end": v(-5.62, -56.47) * mm});
            skLineSegment(sketch, "E277", {"start": v(-5.62, -56.47) * mm, "end": v(-5.91, -56.63) * mm});
            skLineSegment(sketch, "E278", {"start": v(-5.91, -56.63) * mm, "end": v(-6.86, -56.98) * mm});
            skLineSegment(sketch, "E279", {"start": v(-6.86, -56.98) * mm, "end": v(-8.16, -57.15) * mm});
            skLineSegment(sketch, "E280", {"start": v(-8.16, -57.15) * mm, "end": v(-9.47, -56.98) * mm});
            skLineSegment(sketch, "E281", {"start": v(-9.47, -56.98) * mm, "end": v(-10.42, -56.63) * mm});
            skLineSegment(sketch, "E282", {"start": v(-10.42, -56.63) * mm, "end": v(-10.7, -56.47) * mm});
            skLineSegment(sketch, "E283", {"start": v(-10.7, -56.47) * mm, "end": v(-11, -56.3) * mm});
            skLineSegment(sketch, "E284", {"start": v(-11, -56.3) * mm, "end": v(-11.76, -55.65) * mm});
            skLineSegment(sketch, "E285", {"start": v(-11.76, -55.65) * mm, "end": v(-12.56, -54.61) * mm});
            skLineSegment(sketch, "E286", {"start": v(-12.56, -54.61) * mm, "end": v(-13.07, -53.4) * mm});
            skLineSegment(sketch, "E287", {"start": v(-13.07, -53.4) * mm, "end": v(-13.24, -52.4) * mm});
            skLineSegment(sketch, "E288", {"start": v(-13.24, -52.4) * mm, "end": v(-13.24, -52.07) * mm});
            skLineSegment(sketch, "E289", {"start": v(-13.24, -52.07) * mm, "end": v(-13.24, -51.74) * mm});
            skLineSegment(sketch, "E290", {"start": v(-13.24, -51.74) * mm, "end": v(-13.07, -50.74) * mm});
            skLineSegment(sketch, "E291", {"start": v(-13.07, -50.74) * mm, "end": v(-12.56, -49.53) * mm});
            skLineSegment(sketch, "E292", {"start": v(-12.56, -49.53) * mm, "end": v(-11.76, -48.48) * mm});
            skLineSegment(sketch, "E293", {"start": v(-11.76, -48.48) * mm, "end": v(-11, -47.84) * mm});
            skLineSegment(sketch, "E294", {"start": v(-11, -47.84) * mm, "end": v(-10.7, -47.67) * mm});
            skLineSegment(sketch, "E295", {"start": v(-10.7, -47.67) * mm, "end": v(-10.42, -47.5) * mm});
            skLineSegment(sketch, "E296", {"start": v(-10.42, -47.5) * mm, "end": v(-9.47, -47.16) * mm});
            skLineSegment(sketch, "E297", {"start": v(-9.47, -47.16) * mm, "end": v(-8.16, -46.99) * mm});
            skLineSegment(sketch, "E298", {"start": v(-8.16, -46.99) * mm, "end": v(-6.86, -47.16) * mm});
            skLineSegment(sketch, "E299", {"start": v(-6.86, -47.16) * mm, "end": v(-5.91, -47.5) * mm});
            skLineSegment(sketch, "E300", {"start": v(-5.91, -47.5) * mm, "end": v(-5.62, -47.67) * mm});
            skLineSegment(sketch, "E301", {"start": v(-5.62, -47.67) * mm, "end": v(-5.34, -47.84) * mm});
            skLineSegment(sketch, "E302", {"start": v(-5.34, -47.84) * mm, "end": v(-4.56, -48.48) * mm});
            skLineSegment(sketch, "E303", {"start": v(-4.56, -48.48) * mm, "end": v(-3.77, -49.53) * mm});
            skLineSegment(sketch, "E304", {"start": v(-3.77, -49.53) * mm, "end": v(-3.26, -50.74) * mm});
            skLineSegment(sketch, "E305", {"start": v(-3.26, -50.74) * mm, "end": v(-3.08, -51.74) * mm});
            skLineSegment(sketch, "E306", {"start": v(-3.08, -51.74) * mm, "end": v(-3.08, -52.07) * mm});
            skLineSegment(sketch, "E307", {"start": v(-22.16, -52.07) * mm, "end": v(-22.16, -52.4) * mm});
            skLineSegment(sketch, "E308", {"start": v(-22.16, -52.4) * mm, "end": v(-22.34, -53.37) * mm});
            skLineSegment(sketch, "E309", {"start": v(-22.34, -53.37) * mm, "end": v(-22.83, -54.57) * mm});
            skLineSegment(sketch, "E310", {"start": v(-22.83, -54.57) * mm, "end": v(-23.62, -55.6) * mm});
            skLineSegment(sketch, "E311", {"start": v(-23.62, -55.6) * mm, "end": v(-24.38, -56.24) * mm});
            skLineSegment(sketch, "E312", {"start": v(-24.38, -56.24) * mm, "end": v(-24.67, -56.4) * mm});
            skLineSegment(sketch, "E313", {"start": v(-24.67, -56.4) * mm, "end": v(-24.95, -56.56) * mm});
            skLineSegment(sketch, "E314", {"start": v(-24.95, -56.56) * mm, "end": v(-25.88, -56.9) * mm});
            skLineSegment(sketch, "E315", {"start": v(-25.88, -56.9) * mm, "end": v(-27.16, -57.07) * mm});
            skLineSegment(sketch, "E316", {"start": v(-27.16, -57.07) * mm, "end": v(-28.45, -56.9) * mm});
            skLineSegment(sketch, "E317", {"start": v(-28.45, -56.9) * mm, "end": v(-29.38, -56.56) * mm});
            skLineSegment(sketch, "E318", {"start": v(-29.38, -56.56) * mm, "end": v(-29.66, -56.4) * mm});
            skLineSegment(sketch, "E319", {"start": v(-29.66, -56.4) * mm, "end": v(-29.95, -56.24) * mm});
            skLineSegment(sketch, "E320", {"start": v(-29.95, -56.24) * mm, "end": v(-30.7, -55.6) * mm});
            skLineSegment(sketch, "E321", {"start": v(-30.7, -55.6) * mm, "end": v(-31.5, -54.57) * mm});
            skLineSegment(sketch, "E322", {"start": v(-31.5, -54.57) * mm, "end": v(-32, -53.37) * mm});
            skLineSegment(sketch, "E323", {"start": v(-32, -53.37) * mm, "end": v(-32.16, -52.4) * mm});
            skLineSegment(sketch, "E324", {"start": v(-32.16, -52.4) * mm, "end": v(-32.16, -52.07) * mm});
            skLineSegment(sketch, "E325", {"start": v(-32.16, -52.07) * mm, "end": v(-32.16, -51.74) * mm});
            skLineSegment(sketch, "E326", {"start": v(-32.16, -51.74) * mm, "end": v(-32, -50.77) * mm});
            skLineSegment(sketch, "E327", {"start": v(-32, -50.77) * mm, "end": v(-31.5, -49.57) * mm});
            skLineSegment(sketch, "E328", {"start": v(-31.5, -49.57) * mm, "end": v(-30.7, -48.54) * mm});
            skLineSegment(sketch, "E329", {"start": v(-30.7, -48.54) * mm, "end": v(-29.95, -47.9) * mm});
            skLineSegment(sketch, "E330", {"start": v(-29.95, -47.9) * mm, "end": v(-29.66, -47.74) * mm});
            skLineSegment(sketch, "E331", {"start": v(-29.66, -47.74) * mm, "end": v(-29.38, -47.58) * mm});
            skLineSegment(sketch, "E332", {"start": v(-29.38, -47.58) * mm, "end": v(-28.45, -47.24) * mm});
            skLineSegment(sketch, "E333", {"start": v(-28.45, -47.24) * mm, "end": v(-27.16, -47.07) * mm});
            skLineSegment(sketch, "E334", {"start": v(-27.16, -47.07) * mm, "end": v(-25.88, -47.24) * mm});
            skLineSegment(sketch, "E335", {"start": v(-25.88, -47.24) * mm, "end": v(-24.95, -47.58) * mm});
            skLineSegment(sketch, "E336", {"start": v(-24.95, -47.58) * mm, "end": v(-24.67, -47.74) * mm});
            skLineSegment(sketch, "E337", {"start": v(-24.67, -47.74) * mm, "end": v(-24.38, -47.9) * mm});
            skLineSegment(sketch, "E338", {"start": v(-24.38, -47.9) * mm, "end": v(-23.62, -48.54) * mm});
            skLineSegment(sketch, "E339", {"start": v(-23.62, -48.54) * mm, "end": v(-22.83, -49.57) * mm});
            skLineSegment(sketch, "E340", {"start": v(-22.83, -49.57) * mm, "end": v(-22.34, -50.77) * mm});
            skLineSegment(sketch, "E341", {"start": v(-22.34, -50.77) * mm, "end": v(-22.16, -51.74) * mm});
            skLineSegment(sketch, "E342", {"start": v(-22.16, -51.74) * mm, "end": v(-22.16, -52.07) * mm});
            skLineSegment(sketch, "E343", {"start": v(50.96, 5.1) * mm, "end": v(49.45, 5.1) * mm});
            skLineSegment(sketch, "E344", {"start": v(46.74, 0) * mm, "end": v(46.74, -0.1) * mm});
            skLineSegment(sketch, "E345", {"start": v(46.74, -0.1) * mm, "end": v(46.63, -0.4) * mm});
            skLineSegment(sketch, "E346", {"start": v(46.63, -0.4) * mm, "end": v(46.4, -0.66) * mm});
            skLineSegment(sketch, "E347", {"start": v(46.4, -0.66) * mm, "end": v(46.34, -0.7) * mm});
            skLineSegment(sketch, "E348", {"start": v(46.34, -0.7) * mm, "end": v(46.28, -0.73) * mm});
            skLineSegment(sketch, "E349", {"start": v(46.28, -0.73) * mm, "end": v(45.6, -0.73) * mm});
            skLineSegment(sketch, "E350", {"start": v(45.6, -0.73) * mm, "end": v(45.54, -0.7) * mm});
            skLineSegment(sketch, "E351", {"start": v(45.54, -0.7) * mm, "end": v(45.48, -0.66) * mm});
            skLineSegment(sketch, "E352", {"start": v(45.48, -0.66) * mm, "end": v(45.25, -0.4) * mm});
            skLineSegment(sketch, "E353", {"start": v(45.25, -0.4) * mm, "end": v(45.14, -0.1) * mm});
            skLineSegment(sketch, "E354", {"start": v(45.14, -0.1) * mm, "end": v(45.14, 0) * mm});
            skLineSegment(sketch, "E355", {"start": v(45.14, 0) * mm, "end": v(45.14, 0.1) * mm});
            skLineSegment(sketch, "E356", {"start": v(45.14, 0.1) * mm, "end": v(45.25, 0.4) * mm});
            skLineSegment(sketch, "E357", {"start": v(45.25, 0.4) * mm, "end": v(45.48, 0.66) * mm});
            skLineSegment(sketch, "E358", {"start": v(45.48, 0.66) * mm, "end": v(45.54, 0.7) * mm});
            skLineSegment(sketch, "E359", {"start": v(45.54, 0.7) * mm, "end": v(45.6, 0.73) * mm});
            skLineSegment(sketch, "E360", {"start": v(45.6, 0.73) * mm, "end": v(46.28, 0.73) * mm});
            skLineSegment(sketch, "E361", {"start": v(46.28, 0.73) * mm, "end": v(46.34, 0.7) * mm});
            skLineSegment(sketch, "E362", {"start": v(46.34, 0.7) * mm, "end": v(46.4, 0.66) * mm});
            skLineSegment(sketch, "E363", {"start": v(46.4, 0.66) * mm, "end": v(46.63, 0.4) * mm});
            skLineSegment(sketch, "E364", {"start": v(46.63, 0.4) * mm, "end": v(46.74, 0.1) * mm});
            skLineSegment(sketch, "E365", {"start": v(46.74, 0.1) * mm, "end": v(46.74, 0) * mm});
            skLineSegment(sketch, "E366", {"start": v(50.96, -5.1) * mm, "end": v(49.45, -5.1) * mm});
            skLineSegment(sketch, "E367", {"start": v(46.74, 2.5) * mm, "end": v(46.74, 2.4) * mm});
            skLineSegment(sketch, "E368", {"start": v(46.74, 2.4) * mm, "end": v(46.63, 2.1) * mm});
            skLineSegment(sketch, "E369", {"start": v(46.63, 2.1) * mm, "end": v(46.4, 1.84) * mm});
            skLineSegment(sketch, "E370", {"start": v(46.4, 1.84) * mm, "end": v(46.34, 1.8) * mm});
            skLineSegment(sketch, "E371", {"start": v(46.34, 1.8) * mm, "end": v(46.28, 1.77) * mm});
            skLineSegment(sketch, "E372", {"start": v(46.28, 1.77) * mm, "end": v(45.6, 1.77) * mm});
            skLineSegment(sketch, "E373", {"start": v(45.6, 1.77) * mm, "end": v(45.54, 1.8) * mm});
            skLineSegment(sketch, "E374", {"start": v(45.54, 1.8) * mm, "end": v(45.48, 1.84) * mm});
            skLineSegment(sketch, "E375", {"start": v(45.48, 1.84) * mm, "end": v(45.25, 2.1) * mm});
            skLineSegment(sketch, "E376", {"start": v(45.25, 2.1) * mm, "end": v(45.14, 2.4) * mm});
            skLineSegment(sketch, "E377", {"start": v(45.14, 2.4) * mm, "end": v(45.14, 2.5) * mm});
            skLineSegment(sketch, "E378", {"start": v(45.14, 2.5) * mm, "end": v(45.14, 2.6) * mm});
            skLineSegment(sketch, "E379", {"start": v(45.14, 2.6) * mm, "end": v(45.25, 2.9) * mm});
            skLineSegment(sketch, "E380", {"start": v(45.25, 2.9) * mm, "end": v(45.48, 3.16) * mm});
            skLineSegment(sketch, "E381", {"start": v(45.48, 3.16) * mm, "end": v(45.54, 3.2) * mm});
            skLineSegment(sketch, "E382", {"start": v(45.54, 3.2) * mm, "end": v(45.6, 3.23) * mm});
            skLineSegment(sketch, "E383", {"start": v(45.6, 3.23) * mm, "end": v(46.28, 3.23) * mm});
            skLineSegment(sketch, "E384", {"start": v(46.28, 3.23) * mm, "end": v(46.34, 3.2) * mm});
            skLineSegment(sketch, "E385", {"start": v(46.34, 3.2) * mm, "end": v(46.4, 3.16) * mm});
            skLineSegment(sketch, "E386", {"start": v(46.4, 3.16) * mm, "end": v(46.63, 2.9) * mm});
            skLineSegment(sketch, "E387", {"start": v(46.63, 2.9) * mm, "end": v(46.74, 2.6) * mm});
            skLineSegment(sketch, "E388", {"start": v(46.74, 2.6) * mm, "end": v(46.74, 2.5) * mm});
            skLineSegment(sketch, "E389", {"start": v(-22.42, 13.9) * mm, "end": v(-22.42, 13.77) * mm});
            skLineSegment(sketch, "E390", {"start": v(-22.42, 13.77) * mm, "end": v(-22.66, 13.43) * mm});
            skLineSegment(sketch, "E391", {"start": v(-22.66, 13.43) * mm, "end": v(-22.7, 13.4) * mm});
            skLineSegment(sketch, "E392", {"start": v(-22.7, 13.4) * mm, "end": v(-22.75, 13.38) * mm});
            skLineSegment(sketch, "E393", {"start": v(-22.75, 13.38) * mm, "end": v(-23.24, 13.38) * mm});
            skLineSegment(sketch, "E394", {"start": v(-23.24, 13.38) * mm, "end": v(-23.28, 13.4) * mm});
            skLineSegment(sketch, "E395", {"start": v(-23.28, 13.4) * mm, "end": v(-23.32, 13.43) * mm});
            skLineSegment(sketch, "E396", {"start": v(-23.32, 13.43) * mm, "end": v(-23.56, 13.78) * mm});
            skLineSegment(sketch, "E397", {"start": v(-23.56, 13.78) * mm, "end": v(-23.56, 13.9) * mm});
            skLineSegment(sketch, "E398", {"start": v(-23.56, 13.9) * mm, "end": v(-23.56, 14.02) * mm});
            skLineSegment(sketch, "E399", {"start": v(-23.56, 14.02) * mm, "end": v(-23.32, 14.37) * mm});
            skLineSegment(sketch, "E400", {"start": v(-23.32, 14.37) * mm, "end": v(-23.28, 14.4) * mm});
            skLineSegment(sketch, "E401", {"start": v(-23.28, 14.4) * mm, "end": v(-23.24, 14.42) * mm});
            skLineSegment(sketch, "E402", {"start": v(-23.24, 14.42) * mm, "end": v(-22.75, 14.42) * mm});
            skLineSegment(sketch, "E403", {"start": v(-22.75, 14.42) * mm, "end": v(-22.7, 14.4) * mm});
            skLineSegment(sketch, "E404", {"start": v(-22.7, 14.4) * mm, "end": v(-22.66, 14.37) * mm});
            skLineSegment(sketch, "E405", {"start": v(-22.66, 14.37) * mm, "end": v(-22.42, 14.01) * mm});
            skLineSegment(sketch, "E406", {"start": v(-22.42, 14.01) * mm, "end": v(-22.42, 13.9) * mm});
            skLineSegment(sketch, "E407", {"start": v(-22.04, 12.44) * mm, "end": v(-22.04, 12.31) * mm});
            skLineSegment(sketch, "E408", {"start": v(-22.04, 12.31) * mm, "end": v(-22.28, 11.97) * mm});
            skLineSegment(sketch, "E409", {"start": v(-22.28, 11.97) * mm, "end": v(-22.33, 11.94) * mm});
            skLineSegment(sketch, "E410", {"start": v(-22.33, 11.94) * mm, "end": v(-22.37, 11.92) * mm});
            skLineSegment(sketch, "E411", {"start": v(-22.37, 11.92) * mm, "end": v(-22.86, 11.92) * mm});
            skLineSegment(sketch, "E412", {"start": v(-22.86, 11.92) * mm, "end": v(-22.9, 11.94) * mm});
            skLineSegment(sketch, "E413", {"start": v(-22.9, 11.94) * mm, "end": v(-22.94, 11.97) * mm});
            skLineSegment(sketch, "E414", {"start": v(-22.94, 11.97) * mm, "end": v(-23.18, 12.32) * mm});
            skLineSegment(sketch, "E415", {"start": v(-23.18, 12.32) * mm, "end": v(-23.18, 12.44) * mm});
            skLineSegment(sketch, "E416", {"start": v(-23.18, 12.44) * mm, "end": v(-23.18, 12.56) * mm});
            skLineSegment(sketch, "E417", {"start": v(-23.18, 12.56) * mm, "end": v(-22.94, 12.9) * mm});
            skLineSegment(sketch, "E418", {"start": v(-22.94, 12.9) * mm, "end": v(-22.9, 12.93) * mm});
            skLineSegment(sketch, "E419", {"start": v(-22.9, 12.93) * mm, "end": v(-22.86, 12.96) * mm});
            skLineSegment(sketch, "E420", {"start": v(-22.86, 12.96) * mm, "end": v(-22.37, 12.96) * mm});
            skLineSegment(sketch, "E421", {"start": v(-22.37, 12.96) * mm, "end": v(-22.33, 12.93) * mm});
            skLineSegment(sketch, "E422", {"start": v(-22.33, 12.93) * mm, "end": v(-22.28, 12.9) * mm});
            skLineSegment(sketch, "E423", {"start": v(-22.28, 12.9) * mm, "end": v(-22.04, 12.55) * mm});
            skLineSegment(sketch, "E424", {"start": v(-22.04, 12.55) * mm, "end": v(-22.04, 12.44) * mm});
            skLineSegment(sketch, "E425", {"start": v(5.26, 12.63) * mm, "end": v(5.26, 12.5) * mm});
            skLineSegment(sketch, "E426", {"start": v(5.26, 12.5) * mm, "end": v(5.02, 12.16) * mm});
            skLineSegment(sketch, "E427", {"start": v(5.02, 12.16) * mm, "end": v(4.98, 12.13) * mm});
            skLineSegment(sketch, "E428", {"start": v(4.98, 12.13) * mm, "end": v(4.93, 12.1) * mm});
            skLineSegment(sketch, "E429", {"start": v(4.93, 12.1) * mm, "end": v(4.45, 12.1) * mm});
            skLineSegment(sketch, "E430", {"start": v(4.45, 12.1) * mm, "end": v(4.4, 12.13) * mm});
            skLineSegment(sketch, "E431", {"start": v(4.4, 12.13) * mm, "end": v(4.36, 12.16) * mm});
            skLineSegment(sketch, "E432", {"start": v(4.36, 12.16) * mm, "end": v(4.12, 12.5) * mm});
            skLineSegment(sketch, "E433", {"start": v(4.12, 12.5) * mm, "end": v(4.12, 12.63) * mm});
            skLineSegment(sketch, "E434", {"start": v(4.12, 12.63) * mm, "end": v(4.12, 12.75) * mm});
            skLineSegment(sketch, "E435", {"start": v(4.12, 12.75) * mm, "end": v(4.36, 13.1) * mm});
            skLineSegment(sketch, "E436", {"start": v(4.36, 13.1) * mm, "end": v(4.4, 13.12) * mm});
            skLineSegment(sketch, "E437", {"start": v(4.4, 13.12) * mm, "end": v(4.45, 13.15) * mm});
            skLineSegment(sketch, "E438", {"start": v(4.45, 13.15) * mm, "end": v(4.93, 13.15) * mm});
            skLineSegment(sketch, "E439", {"start": v(4.93, 13.15) * mm, "end": v(4.98, 13.12) * mm});
            skLineSegment(sketch, "E440", {"start": v(4.98, 13.12) * mm, "end": v(5.02, 13.1) * mm});
            skLineSegment(sketch, "E441", {"start": v(5.02, 13.1) * mm, "end": v(5.26, 12.74) * mm});
            skLineSegment(sketch, "E442", {"start": v(5.26, 12.74) * mm, "end": v(5.26, 12.63) * mm});
            skLineSegment(sketch, "E443", {"start": v(0.87, 17.98) * mm, "end": v(0.87, 17.86) * mm});
            skLineSegment(sketch, "E444", {"start": v(0.87, 17.86) * mm, "end": v(0.63, 17.52) * mm});
            skLineSegment(sketch, "E445", {"start": v(0.63, 17.52) * mm, "end": v(0.58, 17.49) * mm});
            skLineSegment(sketch, "E446", {"start": v(0.58, 17.49) * mm, "end": v(0.54, 17.47) * mm});
            skLineSegment(sketch, "E447", {"start": v(0.54, 17.47) * mm, "end": v(0.06, 17.47) * mm});
            skLineSegment(sketch, "E448", {"start": v(0.06, 17.47) * mm, "end": v(0.01, 17.49) * mm});
            skLineSegment(sketch, "E449", {"start": v(0.01, 17.49) * mm, "end": v(-0.03, 17.52) * mm});
            skLineSegment(sketch, "E450", {"start": v(-0.03, 17.52) * mm, "end": v(-0.27, 17.87) * mm});
            skLineSegment(sketch, "E451", {"start": v(-0.27, 17.87) * mm, "end": v(-0.27, 17.98) * mm});
            skLineSegment(sketch, "E452", {"start": v(-0.27, 17.98) * mm, "end": v(-0.27, 18.1) * mm});
            skLineSegment(sketch, "E453", {"start": v(-0.27, 18.1) * mm, "end": v(-0.03, 18.45) * mm});
            skLineSegment(sketch, "E454", {"start": v(-0.03, 18.45) * mm, "end": v(0.01, 18.48) * mm});
            skLineSegment(sketch, "E455", {"start": v(0.01, 18.48) * mm, "end": v(0.06, 18.5) * mm});
            skLineSegment(sketch, "E456", {"start": v(0.06, 18.5) * mm, "end": v(0.54, 18.5) * mm});
            skLineSegment(sketch, "E457", {"start": v(0.54, 18.5) * mm, "end": v(0.58, 18.48) * mm});
            skLineSegment(sketch, "E458", {"start": v(0.58, 18.48) * mm, "end": v(0.63, 18.45) * mm});
            skLineSegment(sketch, "E459", {"start": v(0.63, 18.45) * mm, "end": v(0.87, 18.1) * mm});
            skLineSegment(sketch, "E460", {"start": v(0.87, 18.1) * mm, "end": v(0.87, 17.98) * mm});
            skLineSegment(sketch, "E461", {"start": v(-1.21, 19.93) * mm, "end": v(-1.21, 19.8) * mm});
            skLineSegment(sketch, "E462", {"start": v(-1.21, 19.8) * mm, "end": v(-1.46, 19.46) * mm});
            skLineSegment(sketch, "E463", {"start": v(-1.46, 19.46) * mm, "end": v(-1.5, 19.43) * mm});
            skLineSegment(sketch, "E464", {"start": v(-1.5, 19.43) * mm, "end": v(-1.54, 19.4) * mm});
            skLineSegment(sketch, "E465", {"start": v(-1.54, 19.4) * mm, "end": v(-2.03, 19.4) * mm});
            skLineSegment(sketch, "E466", {"start": v(-2.03, 19.4) * mm, "end": v(-2.07, 19.43) * mm});
            skLineSegment(sketch, "E467", {"start": v(-2.07, 19.43) * mm, "end": v(-2.12, 19.46) * mm});
            skLineSegment(sketch, "E468", {"start": v(-2.12, 19.46) * mm, "end": v(-2.36, 19.81) * mm});
            skLineSegment(sketch, "E469", {"start": v(-2.36, 19.81) * mm, "end": v(-2.36, 19.93) * mm});
            skLineSegment(sketch, "E470", {"start": v(-2.36, 19.93) * mm, "end": v(-2.36, 20.05) * mm});
            skLineSegment(sketch, "E471", {"start": v(-2.36, 20.05) * mm, "end": v(-2.12, 20.4) * mm});
            skLineSegment(sketch, "E472", {"start": v(-2.12, 20.4) * mm, "end": v(-2.07, 20.42) * mm});
            skLineSegment(sketch, "E473", {"start": v(-2.07, 20.42) * mm, "end": v(-2.03, 20.45) * mm});
            skLineSegment(sketch, "E474", {"start": v(-2.03, 20.45) * mm, "end": v(-1.54, 20.45) * mm});
            skLineSegment(sketch, "E475", {"start": v(-1.54, 20.45) * mm, "end": v(-1.5, 20.42) * mm});
            skLineSegment(sketch, "E476", {"start": v(-1.5, 20.42) * mm, "end": v(-1.46, 20.4) * mm});
            skLineSegment(sketch, "E477", {"start": v(-1.46, 20.4) * mm, "end": v(-1.21, 20.05) * mm});
            skLineSegment(sketch, "E478", {"start": v(-1.21, 20.05) * mm, "end": v(-1.21, 19.93) * mm});
            skLineSegment(sketch, "E479", {"start": v(2.79, 21.77) * mm, "end": v(2.79, 21.65) * mm});
            skLineSegment(sketch, "E480", {"start": v(2.79, 21.65) * mm, "end": v(2.54, 21.3) * mm});
            skLineSegment(sketch, "E481", {"start": v(2.54, 21.3) * mm, "end": v(2.5, 21.28) * mm});
            skLineSegment(sketch, "E482", {"start": v(2.5, 21.28) * mm, "end": v(2.46, 21.25) * mm});
            skLineSegment(sketch, "E483", {"start": v(2.46, 21.25) * mm, "end": v(1.97, 21.25) * mm});
            skLineSegment(sketch, "E484", {"start": v(1.97, 21.25) * mm, "end": v(1.93, 21.28) * mm});
            skLineSegment(sketch, "E485", {"start": v(1.93, 21.28) * mm, "end": v(1.88, 21.3) * mm});
            skLineSegment(sketch, "E486", {"start": v(1.88, 21.3) * mm, "end": v(1.64, 21.65) * mm});
            skLineSegment(sketch, "E487", {"start": v(1.64, 21.65) * mm, "end": v(1.64, 21.77) * mm});
            skLineSegment(sketch, "E488", {"start": v(1.64, 21.77) * mm, "end": v(1.64, 21.9) * mm});
            skLineSegment(sketch, "E489", {"start": v(1.64, 21.9) * mm, "end": v(1.88, 22.24) * mm});
            skLineSegment(sketch, "E490", {"start": v(1.88, 22.24) * mm, "end": v(1.93, 22.26) * mm});
            skLineSegment(sketch, "E491", {"start": v(1.93, 22.26) * mm, "end": v(1.97, 22.3) * mm});
            skLineSegment(sketch, "E492", {"start": v(1.97, 22.3) * mm, "end": v(2.46, 22.3) * mm});
            skLineSegment(sketch, "E493", {"start": v(2.46, 22.3) * mm, "end": v(2.5, 22.26) * mm});
            skLineSegment(sketch, "E494", {"start": v(2.5, 22.26) * mm, "end": v(2.54, 22.24) * mm});
            skLineSegment(sketch, "E495", {"start": v(2.54, 22.24) * mm, "end": v(2.79, 21.89) * mm});
            skLineSegment(sketch, "E496", {"start": v(2.79, 21.89) * mm, "end": v(2.79, 21.77) * mm});
            skLineSegment(sketch, "E497", {"start": v(12.63, 12.88) * mm, "end": v(12.63, 12.76) * mm});
            skLineSegment(sketch, "E498", {"start": v(12.63, 12.76) * mm, "end": v(12.39, 12.41) * mm});
            skLineSegment(sketch, "E499", {"start": v(12.39, 12.41) * mm, "end": v(12.34, 12.38) * mm});
            skLineSegment(sketch, "E500", {"start": v(12.34, 12.38) * mm, "end": v(12.3, 12.36) * mm});
            skLineSegment(sketch, "E501", {"start": v(12.3, 12.36) * mm, "end": v(11.82, 12.36) * mm});
            skLineSegment(sketch, "E502", {"start": v(11.82, 12.36) * mm, "end": v(11.77, 12.38) * mm});
            skLineSegment(sketch, "E503", {"start": v(11.77, 12.38) * mm, "end": v(11.73, 12.41) * mm});
            skLineSegment(sketch, "E504", {"start": v(11.73, 12.41) * mm, "end": v(11.49, 12.76) * mm});
            skLineSegment(sketch, "E505", {"start": v(11.49, 12.76) * mm, "end": v(11.49, 12.88) * mm});
            skLineSegment(sketch, "E506", {"start": v(11.49, 12.88) * mm, "end": v(11.49, 13) * mm});
            skLineSegment(sketch, "E507", {"start": v(11.49, 13) * mm, "end": v(11.73, 13.35) * mm});
            skLineSegment(sketch, "E508", {"start": v(11.73, 13.35) * mm, "end": v(11.77, 13.38) * mm});
            skLineSegment(sketch, "E509", {"start": v(11.77, 13.38) * mm, "end": v(11.82, 13.4) * mm});
            skLineSegment(sketch, "E510", {"start": v(11.82, 13.4) * mm, "end": v(12.3, 13.4) * mm});
            skLineSegment(sketch, "E511", {"start": v(12.3, 13.4) * mm, "end": v(12.34, 13.38) * mm});
            skLineSegment(sketch, "E512", {"start": v(12.34, 13.38) * mm, "end": v(12.39, 13.35) * mm});
            skLineSegment(sketch, "E513", {"start": v(12.39, 13.35) * mm, "end": v(12.63, 13) * mm});
            skLineSegment(sketch, "E514", {"start": v(12.63, 13) * mm, "end": v(12.63, 12.88) * mm});
            skLineSegment(sketch, "E515", {"start": v(8.44, 22.79) * mm, "end": v(8.44, 22.66) * mm});
            skLineSegment(sketch, "E516", {"start": v(8.44, 22.66) * mm, "end": v(8.2, 22.32) * mm});
            skLineSegment(sketch, "E517", {"start": v(8.2, 22.32) * mm, "end": v(8.15, 22.3) * mm});
            skLineSegment(sketch, "E518", {"start": v(8.15, 22.3) * mm, "end": v(8.1, 22.27) * mm});
            skLineSegment(sketch, "E519", {"start": v(8.1, 22.27) * mm, "end": v(7.63, 22.27) * mm});
            skLineSegment(sketch, "E520", {"start": v(7.63, 22.27) * mm, "end": v(7.58, 22.3) * mm});
            skLineSegment(sketch, "E521", {"start": v(7.58, 22.3) * mm, "end": v(7.54, 22.32) * mm});
            skLineSegment(sketch, "E522", {"start": v(7.54, 22.32) * mm, "end": v(7.3, 22.67) * mm});
            skLineSegment(sketch, "E523", {"start": v(7.3, 22.67) * mm, "end": v(7.3, 22.79) * mm});
            skLineSegment(sketch, "E524", {"start": v(7.3, 22.79) * mm, "end": v(7.3, 22.9) * mm});
            skLineSegment(sketch, "E525", {"start": v(7.3, 22.9) * mm, "end": v(7.54, 23.26) * mm});
            skLineSegment(sketch, "E526", {"start": v(7.54, 23.26) * mm, "end": v(7.58, 23.28) * mm});
            skLineSegment(sketch, "E527", {"start": v(7.58, 23.28) * mm, "end": v(7.63, 23.3) * mm});
            skLineSegment(sketch, "E528", {"start": v(7.63, 23.3) * mm, "end": v(8.1, 23.3) * mm});
            skLineSegment(sketch, "E529", {"start": v(8.1, 23.3) * mm, "end": v(8.15, 23.28) * mm});
            skLineSegment(sketch, "E530", {"start": v(8.15, 23.28) * mm, "end": v(8.2, 23.26) * mm});
            skLineSegment(sketch, "E531", {"start": v(8.2, 23.26) * mm, "end": v(8.44, 22.9) * mm});
            skLineSegment(sketch, "E532", {"start": v(8.44, 22.9) * mm, "end": v(8.44, 22.79) * mm});
            skLineSegment(sketch, "E533", {"start": v(1, 23.3) * mm, "end": v(1, 23.17) * mm});
            skLineSegment(sketch, "E534", {"start": v(1, 23.17) * mm, "end": v(0.77, 22.82) * mm});
            skLineSegment(sketch, "E535", {"start": v(0.77, 22.82) * mm, "end": v(0.72, 22.8) * mm});
            skLineSegment(sketch, "E536", {"start": v(0.72, 22.8) * mm, "end": v(0.68, 22.77) * mm});
            skLineSegment(sketch, "E537", {"start": v(0.68, 22.77) * mm, "end": v(0.2, 22.77) * mm});
            skLineSegment(sketch, "E538", {"start": v(0.2, 22.77) * mm, "end": v(0.15, 22.8) * mm});
            skLineSegment(sketch, "E539", {"start": v(0.15, 22.8) * mm, "end": v(0.1, 22.82) * mm});
            skLineSegment(sketch, "E540", {"start": v(0.1, 22.82) * mm, "end": v(-0.13, 23.18) * mm});
            skLineSegment(sketch, "E541", {"start": v(-0.13, 23.18) * mm, "end": v(-0.13, 23.3) * mm});
            skLineSegment(sketch, "E542", {"start": v(-0.13, 23.3) * mm, "end": v(-0.13, 23.42) * mm});
            skLineSegment(sketch, "E543", {"start": v(-0.13, 23.42) * mm, "end": v(0.1, 23.76) * mm});
            skLineSegment(sketch, "E544", {"start": v(0.1, 23.76) * mm, "end": v(0.15, 23.79) * mm});
            skLineSegment(sketch, "E545", {"start": v(0.15, 23.79) * mm, "end": v(0.2, 23.82) * mm});
            skLineSegment(sketch, "E546", {"start": v(0.2, 23.82) * mm, "end": v(0.68, 23.82) * mm});
            skLineSegment(sketch, "E547", {"start": v(0.68, 23.82) * mm, "end": v(0.72, 23.79) * mm});
            skLineSegment(sketch, "E548", {"start": v(0.72, 23.79) * mm, "end": v(0.77, 23.76) * mm});
            skLineSegment(sketch, "E549", {"start": v(0.77, 23.76) * mm, "end": v(1, 23.41) * mm});
            skLineSegment(sketch, "E550", {"start": v(1, 23.41) * mm, "end": v(1, 23.3) * mm});
            skLineSegment(sketch, "E551", {"start": v(-3.06, 17.83) * mm, "end": v(-3.06, 17.71) * mm});
            skLineSegment(sketch, "E552", {"start": v(-3.06, 17.71) * mm, "end": v(-3.3, 17.36) * mm});
            skLineSegment(sketch, "E553", {"start": v(-3.3, 17.36) * mm, "end": v(-3.34, 17.34) * mm});
            skLineSegment(sketch, "E554", {"start": v(-3.34, 17.34) * mm, "end": v(-3.39, 17.31) * mm});
            skLineSegment(sketch, "E555", {"start": v(-3.39, 17.31) * mm, "end": v(-3.87, 17.31) * mm});
            skLineSegment(sketch, "E556", {"start": v(-3.87, 17.31) * mm, "end": v(-3.91, 17.34) * mm});
            skLineSegment(sketch, "E557", {"start": v(-3.91, 17.34) * mm, "end": v(-3.96, 17.36) * mm});
            skLineSegment(sketch, "E558", {"start": v(-3.96, 17.36) * mm, "end": v(-4.2, 17.72) * mm});
            skLineSegment(sketch, "E559", {"start": v(-4.2, 17.72) * mm, "end": v(-4.2, 17.83) * mm});
            skLineSegment(sketch, "E560", {"start": v(-4.2, 17.83) * mm, "end": v(-4.2, 17.96) * mm});
            skLineSegment(sketch, "E561", {"start": v(-4.2, 17.96) * mm, "end": v(-3.96, 18.3) * mm});
            skLineSegment(sketch, "E562", {"start": v(-3.96, 18.3) * mm, "end": v(-3.91, 18.33) * mm});
            skLineSegment(sketch, "E563", {"start": v(-3.91, 18.33) * mm, "end": v(-3.87, 18.35) * mm});
            skLineSegment(sketch, "E564", {"start": v(-3.87, 18.35) * mm, "end": v(-3.39, 18.35) * mm});
            skLineSegment(sketch, "E565", {"start": v(-3.39, 18.35) * mm, "end": v(-3.34, 18.33) * mm});
            skLineSegment(sketch, "E566", {"start": v(-3.34, 18.33) * mm, "end": v(-3.3, 18.3) * mm});
            skLineSegment(sketch, "E567", {"start": v(-3.3, 18.3) * mm, "end": v(-3.06, 17.95) * mm});
            skLineSegment(sketch, "E568", {"start": v(-3.06, 17.95) * mm, "end": v(-3.06, 17.83) * mm});
            skLineSegment(sketch, "E569", {"start": v(-20.52, 16.18) * mm, "end": v(-20.52, 16.06) * mm});
            skLineSegment(sketch, "E570", {"start": v(-20.52, 16.06) * mm, "end": v(-20.76, 15.71) * mm});
            skLineSegment(sketch, "E571", {"start": v(-20.76, 15.71) * mm, "end": v(-20.8, 15.69) * mm});
            skLineSegment(sketch, "E572", {"start": v(-20.8, 15.69) * mm, "end": v(-20.85, 15.66) * mm});
            skLineSegment(sketch, "E573", {"start": v(-20.85, 15.66) * mm, "end": v(-21.33, 15.66) * mm});
            skLineSegment(sketch, "E574", {"start": v(-21.33, 15.66) * mm, "end": v(-21.38, 15.69) * mm});
            skLineSegment(sketch, "E575", {"start": v(-21.38, 15.69) * mm, "end": v(-21.42, 15.71) * mm});
            skLineSegment(sketch, "E576", {"start": v(-21.42, 15.71) * mm, "end": v(-21.66, 16.07) * mm});
            skLineSegment(sketch, "E577", {"start": v(-21.66, 16.07) * mm, "end": v(-21.66, 16.18) * mm});
            skLineSegment(sketch, "E578", {"start": v(-21.66, 16.18) * mm, "end": v(-21.66, 16.3) * mm});
            skLineSegment(sketch, "E579", {"start": v(-21.66, 16.3) * mm, "end": v(-21.42, 16.65) * mm});
            skLineSegment(sketch, "E580", {"start": v(-21.42, 16.65) * mm, "end": v(-21.38, 16.68) * mm});
            skLineSegment(sketch, "E581", {"start": v(-21.38, 16.68) * mm, "end": v(-21.33, 16.7) * mm});
            skLineSegment(sketch, "E582", {"start": v(-21.33, 16.7) * mm, "end": v(-20.85, 16.7) * mm});
            skLineSegment(sketch, "E583", {"start": v(-20.85, 16.7) * mm, "end": v(-20.8, 16.68) * mm});
            skLineSegment(sketch, "E584", {"start": v(-20.8, 16.68) * mm, "end": v(-20.76, 16.65) * mm});
            skLineSegment(sketch, "E585", {"start": v(-20.76, 16.65) * mm, "end": v(-20.52, 16.3) * mm});
            skLineSegment(sketch, "E586", {"start": v(-20.52, 16.3) * mm, "end": v(-20.52, 16.18) * mm});
            skLineSegment(sketch, "E587", {"start": v(-11.88, 14.66) * mm, "end": v(-11.88, 14.54) * mm});
            skLineSegment(sketch, "E588", {"start": v(-11.88, 14.54) * mm, "end": v(-12.12, 14.19) * mm});
            skLineSegment(sketch, "E589", {"start": v(-12.12, 14.19) * mm, "end": v(-12.17, 14.16) * mm});
            skLineSegment(sketch, "E590", {"start": v(-12.17, 14.16) * mm, "end": v(-12.21, 14.14) * mm});
            skLineSegment(sketch, "E591", {"start": v(-12.21, 14.14) * mm, "end": v(-12.7, 14.14) * mm});
            skLineSegment(sketch, "E592", {"start": v(-12.7, 14.14) * mm, "end": v(-12.74, 14.16) * mm});
            skLineSegment(sketch, "E593", {"start": v(-12.74, 14.16) * mm, "end": v(-12.78, 14.19) * mm});
            skLineSegment(sketch, "E594", {"start": v(-12.78, 14.19) * mm, "end": v(-13.02, 14.54) * mm});
            skLineSegment(sketch, "E595", {"start": v(-13.02, 14.54) * mm, "end": v(-13.02, 14.66) * mm});
            skLineSegment(sketch, "E596", {"start": v(-13.02, 14.66) * mm, "end": v(-13.02, 14.78) * mm});
            skLineSegment(sketch, "E597", {"start": v(-13.02, 14.78) * mm, "end": v(-12.78, 15.13) * mm});
            skLineSegment(sketch, "E598", {"start": v(-12.78, 15.13) * mm, "end": v(-12.74, 15.15) * mm});
            skLineSegment(sketch, "E599", {"start": v(-12.74, 15.15) * mm, "end": v(-12.7, 15.18) * mm});
            skLineSegment(sketch, "E600", {"start": v(-12.7, 15.18) * mm, "end": v(-12.21, 15.18) * mm});
            skLineSegment(sketch, "E601", {"start": v(-12.21, 15.18) * mm, "end": v(-12.17, 15.15) * mm});
            skLineSegment(sketch, "E602", {"start": v(-12.17, 15.15) * mm, "end": v(-12.12, 15.13) * mm});
            skLineSegment(sketch, "E603", {"start": v(-12.12, 15.13) * mm, "end": v(-11.88, 14.78) * mm});
            skLineSegment(sketch, "E604", {"start": v(-11.88, 14.78) * mm, "end": v(-11.88, 14.66) * mm});
            skLineSegment(sketch, "E605", {"start": v(-7.3, 17.13) * mm, "end": v(-7.3, 17.01) * mm});
            skLineSegment(sketch, "E606", {"start": v(-7.3, 17.01) * mm, "end": v(-7.55, 16.67) * mm});
            skLineSegment(sketch, "E607", {"start": v(-7.55, 16.67) * mm, "end": v(-7.6, 16.64) * mm});
            skLineSegment(sketch, "E608", {"start": v(-7.6, 16.64) * mm, "end": v(-7.64, 16.62) * mm});
            skLineSegment(sketch, "E609", {"start": v(-7.64, 16.62) * mm, "end": v(-8.12, 16.62) * mm});
            skLineSegment(sketch, "E610", {"start": v(-8.12, 16.62) * mm, "end": v(-8.17, 16.64) * mm});
            skLineSegment(sketch, "E611", {"start": v(-8.17, 16.64) * mm, "end": v(-8.21, 16.67) * mm});
            skLineSegment(sketch, "E612", {"start": v(-8.21, 16.67) * mm, "end": v(-8.45, 17.02) * mm});
            skLineSegment(sketch, "E613", {"start": v(-8.45, 17.02) * mm, "end": v(-8.45, 17.13) * mm});
            skLineSegment(sketch, "E614", {"start": v(-8.45, 17.13) * mm, "end": v(-8.45, 17.26) * mm});
            skLineSegment(sketch, "E615", {"start": v(-8.45, 17.26) * mm, "end": v(-8.21, 17.6) * mm});
            skLineSegment(sketch, "E616", {"start": v(-8.21, 17.6) * mm, "end": v(-8.17, 17.63) * mm});
            skLineSegment(sketch, "E617", {"start": v(-8.17, 17.63) * mm, "end": v(-8.12, 17.66) * mm});
            skLineSegment(sketch, "E618", {"start": v(-8.12, 17.66) * mm, "end": v(-7.64, 17.66) * mm});
            skLineSegment(sketch, "E619", {"start": v(-7.64, 17.66) * mm, "end": v(-7.6, 17.63) * mm});
            skLineSegment(sketch, "E620", {"start": v(-7.6, 17.63) * mm, "end": v(-7.55, 17.6) * mm});
            skLineSegment(sketch, "E621", {"start": v(-7.55, 17.6) * mm, "end": v(-7.3, 17.25) * mm});
            skLineSegment(sketch, "E622", {"start": v(-7.3, 17.25) * mm, "end": v(-7.3, 17.13) * mm});
            skLineSegment(sketch, "E623", {"start": v(-10.86, 18.98) * mm, "end": v(-10.86, 18.85) * mm});
            skLineSegment(sketch, "E624", {"start": v(-10.86, 18.85) * mm, "end": v(-11.1, 18.5) * mm});
            skLineSegment(sketch, "E625", {"start": v(-11.1, 18.5) * mm, "end": v(-11.15, 18.48) * mm});
            skLineSegment(sketch, "E626", {"start": v(-11.15, 18.48) * mm, "end": v(-11.2, 18.46) * mm});
            skLineSegment(sketch, "E627", {"start": v(-11.2, 18.46) * mm, "end": v(-11.68, 18.46) * mm});
            skLineSegment(sketch, "E628", {"start": v(-11.68, 18.46) * mm, "end": v(-11.72, 18.48) * mm});
            skLineSegment(sketch, "E629", {"start": v(-11.72, 18.48) * mm, "end": v(-11.77, 18.5) * mm});
            skLineSegment(sketch, "E630", {"start": v(-11.77, 18.5) * mm, "end": v(-12, 18.86) * mm});
            skLineSegment(sketch, "E631", {"start": v(-12, 18.86) * mm, "end": v(-12, 18.98) * mm});
            skLineSegment(sketch, "E632", {"start": v(-12, 18.98) * mm, "end": v(-12, 19.1) * mm});
            skLineSegment(sketch, "E633", {"start": v(-12, 19.1) * mm, "end": v(-11.77, 19.45) * mm});
            skLineSegment(sketch, "E634", {"start": v(-11.77, 19.45) * mm, "end": v(-11.72, 19.47) * mm});
            skLineSegment(sketch, "E635", {"start": v(-11.72, 19.47) * mm, "end": v(-11.68, 19.5) * mm});
            skLineSegment(sketch, "E636", {"start": v(-11.68, 19.5) * mm, "end": v(-11.2, 19.5) * mm});
            skLineSegment(sketch, "E637", {"start": v(-11.2, 19.5) * mm, "end": v(-11.15, 19.47) * mm});
            skLineSegment(sketch, "E638", {"start": v(-11.15, 19.47) * mm, "end": v(-11.1, 19.45) * mm});
            skLineSegment(sketch, "E639", {"start": v(-11.1, 19.45) * mm, "end": v(-10.86, 19.1) * mm});
            skLineSegment(sketch, "E640", {"start": v(-10.86, 19.1) * mm, "end": v(-10.86, 18.98) * mm});
            skLineSegment(sketch, "E641", {"start": v(-6.1, 18.91) * mm, "end": v(-6.1, 18.79) * mm});
            skLineSegment(sketch, "E642", {"start": v(-6.1, 18.79) * mm, "end": v(-6.35, 18.44) * mm});
            skLineSegment(sketch, "E643", {"start": v(-6.35, 18.44) * mm, "end": v(-6.39, 18.42) * mm});
            skLineSegment(sketch, "E644", {"start": v(-6.39, 18.42) * mm, "end": v(-6.43, 18.4) * mm});
            skLineSegment(sketch, "E645", {"start": v(-6.43, 18.4) * mm, "end": v(-6.92, 18.4) * mm});
            skLineSegment(sketch, "E646", {"start": v(-6.92, 18.4) * mm, "end": v(-6.96, 18.42) * mm});
            skLineSegment(sketch, "E647", {"start": v(-6.96, 18.42) * mm, "end": v(-7, 18.44) * mm});
            skLineSegment(sketch, "E648", {"start": v(-7, 18.44) * mm, "end": v(-7.25, 18.8) * mm});
            skLineSegment(sketch, "E649", {"start": v(-7.25, 18.8) * mm, "end": v(-7.25, 18.91) * mm});
            skLineSegment(sketch, "E650", {"start": v(-7.25, 18.91) * mm, "end": v(-7.25, 19.04) * mm});
            skLineSegment(sketch, "E651", {"start": v(-7.25, 19.04) * mm, "end": v(-7, 19.38) * mm});
            skLineSegment(sketch, "E652", {"start": v(-7, 19.38) * mm, "end": v(-6.96, 19.4) * mm});
            skLineSegment(sketch, "E653", {"start": v(-6.96, 19.4) * mm, "end": v(-6.92, 19.43) * mm});
            skLineSegment(sketch, "E654", {"start": v(-6.92, 19.43) * mm, "end": v(-6.43, 19.43) * mm});
            skLineSegment(sketch, "E655", {"start": v(-6.43, 19.43) * mm, "end": v(-6.39, 19.4) * mm});
            skLineSegment(sketch, "E656", {"start": v(-6.39, 19.4) * mm, "end": v(-6.35, 19.38) * mm});
            skLineSegment(sketch, "E657", {"start": v(-6.35, 19.38) * mm, "end": v(-6.1, 19.03) * mm});
            skLineSegment(sketch, "E658", {"start": v(-6.1, 19.03) * mm, "end": v(-6.1, 18.91) * mm});
            skLineSegment(sketch, "E659", {"start": v(13.14, 22.66) * mm, "end": v(13.14, 22.54) * mm});
            skLineSegment(sketch, "E660", {"start": v(13.14, 22.54) * mm, "end": v(12.9, 22.2) * mm});
            skLineSegment(sketch, "E661", {"start": v(12.9, 22.2) * mm, "end": v(12.85, 22.16) * mm});
            skLineSegment(sketch, "E662", {"start": v(12.85, 22.16) * mm, "end": v(12.8, 22.14) * mm});
            skLineSegment(sketch, "E663", {"start": v(12.8, 22.14) * mm, "end": v(12.32, 22.14) * mm});
            skLineSegment(sketch, "E664", {"start": v(12.32, 22.14) * mm, "end": v(12.28, 22.16) * mm});
            skLineSegment(sketch, "E665", {"start": v(12.28, 22.16) * mm, "end": v(12.23, 22.2) * mm});
            skLineSegment(sketch, "E666", {"start": v(12.23, 22.2) * mm, "end": v(12, 22.54) * mm});
            skLineSegment(sketch, "E667", {"start": v(12, 22.54) * mm, "end": v(12, 22.66) * mm});
            skLineSegment(sketch, "E668", {"start": v(12, 22.66) * mm, "end": v(12, 22.78) * mm});
            skLineSegment(sketch, "E669", {"start": v(12, 22.78) * mm, "end": v(12.23, 23.13) * mm});
            skLineSegment(sketch, "E670", {"start": v(12.23, 23.13) * mm, "end": v(12.28, 23.15) * mm});
            skLineSegment(sketch, "E671", {"start": v(12.28, 23.15) * mm, "end": v(12.32, 23.18) * mm});
            skLineSegment(sketch, "E672", {"start": v(12.32, 23.18) * mm, "end": v(12.8, 23.18) * mm});
            skLineSegment(sketch, "E673", {"start": v(12.8, 23.18) * mm, "end": v(12.85, 23.15) * mm});
            skLineSegment(sketch, "E674", {"start": v(12.85, 23.15) * mm, "end": v(12.9, 23.13) * mm});
            skLineSegment(sketch, "E675", {"start": v(12.9, 23.13) * mm, "end": v(13.14, 22.78) * mm});
            skLineSegment(sketch, "E676", {"start": v(13.14, 22.78) * mm, "end": v(13.14, 22.66) * mm});
            skLineSegment(sketch, "E677", {"start": v(-8.64, 22.21) * mm, "end": v(-8.64, 22.1) * mm});
            skLineSegment(sketch, "E678", {"start": v(-8.64, 22.1) * mm, "end": v(-8.88, 21.75) * mm});
            skLineSegment(sketch, "E679", {"start": v(-8.88, 21.75) * mm, "end": v(-8.93, 21.72) * mm});
            skLineSegment(sketch, "E680", {"start": v(-8.93, 21.72) * mm, "end": v(-8.97, 21.7) * mm});
            skLineSegment(sketch, "E681", {"start": v(-8.97, 21.7) * mm, "end": v(-9.46, 21.7) * mm});
            skLineSegment(sketch, "E682", {"start": v(-9.46, 21.7) * mm, "end": v(-9.5, 21.72) * mm});
            skLineSegment(sketch, "E683", {"start": v(-9.5, 21.72) * mm, "end": v(-9.54, 21.75) * mm});
            skLineSegment(sketch, "E684", {"start": v(-9.54, 21.75) * mm, "end": v(-9.79, 22.1) * mm});
            skLineSegment(sketch, "E685", {"start": v(-9.79, 22.1) * mm, "end": v(-9.79, 22.21) * mm});
            skLineSegment(sketch, "E686", {"start": v(-9.79, 22.21) * mm, "end": v(-9.79, 22.34) * mm});
            skLineSegment(sketch, "E687", {"start": v(-9.79, 22.34) * mm, "end": v(-9.54, 22.68) * mm});
            skLineSegment(sketch, "E688", {"start": v(-9.54, 22.68) * mm, "end": v(-9.5, 22.7) * mm});
            skLineSegment(sketch, "E689", {"start": v(-9.5, 22.7) * mm, "end": v(-9.46, 22.73) * mm});
            skLineSegment(sketch, "E690", {"start": v(-9.46, 22.73) * mm, "end": v(-8.97, 22.73) * mm});
            skLineSegment(sketch, "E691", {"start": v(-8.97, 22.73) * mm, "end": v(-8.93, 22.7) * mm});
            skLineSegment(sketch, "E692", {"start": v(-8.93, 22.7) * mm, "end": v(-8.88, 22.68) * mm});
            skLineSegment(sketch, "E693", {"start": v(-8.88, 22.68) * mm, "end": v(-8.64, 22.33) * mm});
            skLineSegment(sketch, "E694", {"start": v(-8.64, 22.33) * mm, "end": v(-8.64, 22.21) * mm});
            skLineSegment(sketch, "E695", {"start": v(-12.2, 21.7) * mm, "end": v(-12.2, 21.58) * mm});
            skLineSegment(sketch, "E696", {"start": v(-12.2, 21.58) * mm, "end": v(-12.44, 21.24) * mm});
            skLineSegment(sketch, "E697", {"start": v(-12.44, 21.24) * mm, "end": v(-12.49, 21.21) * mm});
            skLineSegment(sketch, "E698", {"start": v(-12.49, 21.21) * mm, "end": v(-12.53, 21.19) * mm});
            skLineSegment(sketch, "E699", {"start": v(-12.53, 21.19) * mm, "end": v(-13.01, 21.19) * mm});
            skLineSegment(sketch, "E700", {"start": v(-13.01, 21.19) * mm, "end": v(-13.06, 21.21) * mm});
            skLineSegment(sketch, "E701", {"start": v(-13.06, 21.21) * mm, "end": v(-13.1, 21.24) * mm});
            skLineSegment(sketch, "E702", {"start": v(-13.1, 21.24) * mm, "end": v(-13.34, 21.59) * mm});
            skLineSegment(sketch, "E703", {"start": v(-13.34, 21.59) * mm, "end": v(-13.34, 21.7) * mm});
            skLineSegment(sketch, "E704", {"start": v(-13.34, 21.7) * mm, "end": v(-13.34, 21.83) * mm});
            skLineSegment(sketch, "E705", {"start": v(-13.34, 21.83) * mm, "end": v(-13.1, 22.18) * mm});
            skLineSegment(sketch, "E706", {"start": v(-13.1, 22.18) * mm, "end": v(-13.06, 22.2) * mm});
            skLineSegment(sketch, "E707", {"start": v(-13.06, 22.2) * mm, "end": v(-13.01, 22.23) * mm});
            skLineSegment(sketch, "E708", {"start": v(-13.01, 22.23) * mm, "end": v(-12.53, 22.23) * mm});
            skLineSegment(sketch, "E709", {"start": v(-12.53, 22.23) * mm, "end": v(-12.49, 22.2) * mm});
            skLineSegment(sketch, "E710", {"start": v(-12.49, 22.2) * mm, "end": v(-12.44, 22.18) * mm});
            skLineSegment(sketch, "E711", {"start": v(-12.44, 22.18) * mm, "end": v(-12.2, 21.83) * mm});
            skLineSegment(sketch, "E712", {"start": v(-12.2, 21.83) * mm, "end": v(-12.2, 21.7) * mm});
            skLineSegment(sketch, "E713", {"start": v(-22.17, 21.7) * mm, "end": v(-22.17, 21.58) * mm});
            skLineSegment(sketch, "E714", {"start": v(-22.17, 21.58) * mm, "end": v(-22.41, 21.24) * mm});
            skLineSegment(sketch, "E715", {"start": v(-22.41, 21.24) * mm, "end": v(-22.45, 21.21) * mm});
            skLineSegment(sketch, "E716", {"start": v(-22.45, 21.21) * mm, "end": v(-22.5, 21.19) * mm});
            skLineSegment(sketch, "E717", {"start": v(-22.5, 21.19) * mm, "end": v(-22.98, 21.19) * mm});
            skLineSegment(sketch, "E718", {"start": v(-22.98, 21.19) * mm, "end": v(-23.03, 21.21) * mm});
            skLineSegment(sketch, "E719", {"start": v(-23.03, 21.21) * mm, "end": v(-23.07, 21.24) * mm});
            skLineSegment(sketch, "E720", {"start": v(-23.07, 21.24) * mm, "end": v(-23.31, 21.59) * mm});
            skLineSegment(sketch, "E721", {"start": v(-23.31, 21.59) * mm, "end": v(-23.31, 21.7) * mm});
            skLineSegment(sketch, "E722", {"start": v(-23.31, 21.7) * mm, "end": v(-23.31, 21.83) * mm});
            skLineSegment(sketch, "E723", {"start": v(-23.31, 21.83) * mm, "end": v(-23.07, 22.18) * mm});
            skLineSegment(sketch, "E724", {"start": v(-23.07, 22.18) * mm, "end": v(-23.03, 22.2) * mm});
            skLineSegment(sketch, "E725", {"start": v(-23.03, 22.2) * mm, "end": v(-22.98, 22.23) * mm});
            skLineSegment(sketch, "E726", {"start": v(-22.98, 22.23) * mm, "end": v(-22.5, 22.23) * mm});
            skLineSegment(sketch, "E727", {"start": v(-22.5, 22.23) * mm, "end": v(-22.45, 22.2) * mm});
            skLineSegment(sketch, "E728", {"start": v(-22.45, 22.2) * mm, "end": v(-22.41, 22.18) * mm});
            skLineSegment(sketch, "E729", {"start": v(-22.41, 22.18) * mm, "end": v(-22.17, 21.83) * mm});
            skLineSegment(sketch, "E730", {"start": v(-22.17, 21.83) * mm, "end": v(-22.17, 21.7) * mm});
            skLineSegment(sketch, "E731", {"start": v(-22.04, 19.67) * mm, "end": v(-22.04, 19.55) * mm});
            skLineSegment(sketch, "E732", {"start": v(-22.04, 19.55) * mm, "end": v(-22.28, 19.2) * mm});
            skLineSegment(sketch, "E733", {"start": v(-22.28, 19.2) * mm, "end": v(-22.33, 19.18) * mm});
            skLineSegment(sketch, "E734", {"start": v(-22.33, 19.18) * mm, "end": v(-22.37, 19.15) * mm});
            skLineSegment(sketch, "E735", {"start": v(-22.37, 19.15) * mm, "end": v(-22.86, 19.15) * mm});
            skLineSegment(sketch, "E736", {"start": v(-22.86, 19.15) * mm, "end": v(-22.9, 19.18) * mm});
            skLineSegment(sketch, "E737", {"start": v(-22.9, 19.18) * mm, "end": v(-22.94, 19.2) * mm});
            skLineSegment(sketch, "E738", {"start": v(-22.94, 19.2) * mm, "end": v(-23.18, 19.56) * mm});
            skLineSegment(sketch, "E739", {"start": v(-23.18, 19.56) * mm, "end": v(-23.18, 19.67) * mm});
            skLineSegment(sketch, "E740", {"start": v(-23.18, 19.67) * mm, "end": v(-23.18, 19.8) * mm});
            skLineSegment(sketch, "E741", {"start": v(-23.18, 19.8) * mm, "end": v(-22.94, 20.14) * mm});
            skLineSegment(sketch, "E742", {"start": v(-22.94, 20.14) * mm, "end": v(-22.9, 20.17) * mm});
            skLineSegment(sketch, "E743", {"start": v(-22.9, 20.17) * mm, "end": v(-22.86, 20.2) * mm});
            skLineSegment(sketch, "E744", {"start": v(-22.86, 20.2) * mm, "end": v(-22.37, 20.2) * mm});
            skLineSegment(sketch, "E745", {"start": v(-22.37, 20.2) * mm, "end": v(-22.33, 20.17) * mm});
            skLineSegment(sketch, "E746", {"start": v(-22.33, 20.17) * mm, "end": v(-22.28, 20.14) * mm});
            skLineSegment(sketch, "E747", {"start": v(-22.28, 20.14) * mm, "end": v(-22.04, 19.8) * mm});
            skLineSegment(sketch, "E748", {"start": v(-22.04, 19.8) * mm, "end": v(-22.04, 19.67) * mm});
            skLineSegment(sketch, "E749", {"start": v(-22.3, 23.42) * mm, "end": v(-22.3, 23.3) * mm});
            skLineSegment(sketch, "E750", {"start": v(-22.3, 23.3) * mm, "end": v(-22.54, 22.95) * mm});
            skLineSegment(sketch, "E751", {"start": v(-22.54, 22.95) * mm, "end": v(-22.58, 22.93) * mm});
            skLineSegment(sketch, "E752", {"start": v(-22.58, 22.93) * mm, "end": v(-22.63, 22.9) * mm});
            skLineSegment(sketch, "E753", {"start": v(-22.63, 22.9) * mm, "end": v(-23.1, 22.9) * mm});
            skLineSegment(sketch, "E754", {"start": v(-23.1, 22.9) * mm, "end": v(-23.15, 22.93) * mm});
            skLineSegment(sketch, "E755", {"start": v(-23.15, 22.93) * mm, "end": v(-23.2, 22.95) * mm});
            skLineSegment(sketch, "E756", {"start": v(-23.2, 22.95) * mm, "end": v(-23.44, 23.3) * mm});
            skLineSegment(sketch, "E757", {"start": v(-23.44, 23.3) * mm, "end": v(-23.44, 23.42) * mm});
            skLineSegment(sketch, "E758", {"start": v(-23.44, 23.42) * mm, "end": v(-23.44, 23.55) * mm});
            skLineSegment(sketch, "E759", {"start": v(-23.44, 23.55) * mm, "end": v(-23.2, 23.9) * mm});
            skLineSegment(sketch, "E760", {"start": v(-23.2, 23.9) * mm, "end": v(-23.15, 23.92) * mm});
            skLineSegment(sketch, "E761", {"start": v(-23.15, 23.92) * mm, "end": v(-23.1, 23.94) * mm});
            skLineSegment(sketch, "E762", {"start": v(-23.1, 23.94) * mm, "end": v(-22.63, 23.94) * mm});
            skLineSegment(sketch, "E763", {"start": v(-22.63, 23.94) * mm, "end": v(-22.58, 23.92) * mm});
            skLineSegment(sketch, "E764", {"start": v(-22.58, 23.92) * mm, "end": v(-22.54, 23.9) * mm});
            skLineSegment(sketch, "E765", {"start": v(-22.54, 23.9) * mm, "end": v(-22.3, 23.54) * mm});
            skLineSegment(sketch, "E766", {"start": v(-22.3, 23.54) * mm, "end": v(-22.3, 23.42) * mm});
            skLineSegment(sketch, "E767", {"start": v(-52.06, 15.24) * mm, "end": v(-52.06, 15.05) * mm});
            skLineSegment(sketch, "E768", {"start": v(-52.06, 15.05) * mm, "end": v(-52.26, 14.49) * mm});
            skLineSegment(sketch, "E769", {"start": v(-52.26, 14.49) * mm, "end": v(-52.7, 14) * mm});
            skLineSegment(sketch, "E770", {"start": v(-52.7, 14) * mm, "end": v(-52.8, 13.94) * mm});
            skLineSegment(sketch, "E771", {"start": v(-52.8, 13.94) * mm, "end": v(-52.93, 13.88) * mm});
            skLineSegment(sketch, "E772", {"start": v(-52.93, 13.88) * mm, "end": v(-53.56, 13.74) * mm});
            skLineSegment(sketch, "E773", {"start": v(-53.56, 13.74) * mm, "end": v(-54.2, 13.88) * mm});
            skLineSegment(sketch, "E774", {"start": v(-54.2, 13.88) * mm, "end": v(-54.3, 13.94) * mm});
            skLineSegment(sketch, "E775", {"start": v(-54.3, 13.94) * mm, "end": v(-54.43, 14) * mm});
            skLineSegment(sketch, "E776", {"start": v(-54.43, 14) * mm, "end": v(-54.86, 14.49) * mm});
            skLineSegment(sketch, "E777", {"start": v(-54.86, 14.49) * mm, "end": v(-55.06, 15.05) * mm});
            skLineSegment(sketch, "E778", {"start": v(-55.06, 15.05) * mm, "end": v(-55.06, 15.24) * mm});
            skLineSegment(sketch, "E779", {"start": v(-55.06, 15.24) * mm, "end": v(-55.06, 15.43) * mm});
            skLineSegment(sketch, "E780", {"start": v(-55.06, 15.43) * mm, "end": v(-54.86, 16) * mm});
            skLineSegment(sketch, "E781", {"start": v(-54.86, 16) * mm, "end": v(-54.43, 16.47) * mm});
            skLineSegment(sketch, "E782", {"start": v(-54.43, 16.47) * mm, "end": v(-54.3, 16.54) * mm});
            skLineSegment(sketch, "E783", {"start": v(-54.3, 16.54) * mm, "end": v(-54.2, 16.6) * mm});
            skLineSegment(sketch, "E784", {"start": v(-54.2, 16.6) * mm, "end": v(-53.56, 16.74) * mm});
            skLineSegment(sketch, "E785", {"start": v(-53.56, 16.74) * mm, "end": v(-52.93, 16.6) * mm});
            skLineSegment(sketch, "E786", {"start": v(-52.93, 16.6) * mm, "end": v(-52.8, 16.54) * mm});
            skLineSegment(sketch, "E787", {"start": v(-52.8, 16.54) * mm, "end": v(-52.7, 16.47) * mm});
            skLineSegment(sketch, "E788", {"start": v(-52.7, 16.47) * mm, "end": v(-52.26, 16) * mm});
            skLineSegment(sketch, "E789", {"start": v(-52.26, 16) * mm, "end": v(-52.06, 15.43) * mm});
            skLineSegment(sketch, "E790", {"start": v(-52.06, 15.43) * mm, "end": v(-52.06, 15.24) * mm});
            skLineSegment(sketch, "E791", {"start": v(-52.06, 7.34) * mm, "end": v(-52.06, 7.15) * mm});
            skLineSegment(sketch, "E792", {"start": v(-52.06, 7.15) * mm, "end": v(-52.26, 6.6) * mm});
            skLineSegment(sketch, "E793", {"start": v(-52.26, 6.6) * mm, "end": v(-52.7, 6.1) * mm});
            skLineSegment(sketch, "E794", {"start": v(-52.7, 6.1) * mm, "end": v(-52.8, 6.04) * mm});
            skLineSegment(sketch, "E795", {"start": v(-52.8, 6.04) * mm, "end": v(-52.93, 5.98) * mm});
            skLineSegment(sketch, "E796", {"start": v(-52.93, 5.98) * mm, "end": v(-53.56, 5.84) * mm});
            skLineSegment(sketch, "E797", {"start": v(-53.56, 5.84) * mm, "end": v(-54.2, 5.98) * mm});
            skLineSegment(sketch, "E798", {"start": v(-54.2, 5.98) * mm, "end": v(-54.3, 6.04) * mm});
            skLineSegment(sketch, "E799", {"start": v(-54.3, 6.04) * mm, "end": v(-54.43, 6.1) * mm});
            skLineSegment(sketch, "E800", {"start": v(-54.43, 6.1) * mm, "end": v(-54.86, 6.6) * mm});
            skLineSegment(sketch, "E801", {"start": v(-54.86, 6.6) * mm, "end": v(-55.06, 7.15) * mm});
            skLineSegment(sketch, "E802", {"start": v(-55.06, 7.15) * mm, "end": v(-55.06, 7.34) * mm});
            skLineSegment(sketch, "E803", {"start": v(-55.06, 7.34) * mm, "end": v(-55.06, 7.53) * mm});
            skLineSegment(sketch, "E804", {"start": v(-55.06, 7.53) * mm, "end": v(-54.86, 8.1) * mm});
            skLineSegment(sketch, "E805", {"start": v(-54.86, 8.1) * mm, "end": v(-54.43, 8.57) * mm});
            skLineSegment(sketch, "E806", {"start": v(-54.43, 8.57) * mm, "end": v(-54.3, 8.64) * mm});
            skLineSegment(sketch, "E807", {"start": v(-54.3, 8.64) * mm, "end": v(-54.2, 8.7) * mm});
            skLineSegment(sketch, "E808", {"start": v(-54.2, 8.7) * mm, "end": v(-53.56, 8.84) * mm});
            skLineSegment(sketch, "E809", {"start": v(-53.56, 8.84) * mm, "end": v(-52.93, 8.7) * mm});
            skLineSegment(sketch, "E810", {"start": v(-52.93, 8.7) * mm, "end": v(-52.8, 8.64) * mm});
            skLineSegment(sketch, "E811", {"start": v(-52.8, 8.64) * mm, "end": v(-52.7, 8.57) * mm});
            skLineSegment(sketch, "E812", {"start": v(-52.7, 8.57) * mm, "end": v(-52.26, 8.1) * mm});
            skLineSegment(sketch, "E813", {"start": v(-52.26, 8.1) * mm, "end": v(-52.06, 7.53) * mm});
            skLineSegment(sketch, "E814", {"start": v(-52.06, 7.53) * mm, "end": v(-52.06, 7.34) * mm});
            skLineSegment(sketch, "E815", {"start": v(50.96, 23.26) * mm, "end": v(49.45, 23.26) * mm});
            skLineSegment(sketch, "E816", {"start": v(46.74, 18.16) * mm, "end": v(46.74, 18.06) * mm});
            skLineSegment(sketch, "E817", {"start": v(46.74, 18.06) * mm, "end": v(46.63, 17.76) * mm});
            skLineSegment(sketch, "E818", {"start": v(46.63, 17.76) * mm, "end": v(46.4, 17.5) * mm});
            skLineSegment(sketch, "E819", {"start": v(46.4, 17.5) * mm, "end": v(46.34, 17.47) * mm});
            skLineSegment(sketch, "E820", {"start": v(46.34, 17.47) * mm, "end": v(46.28, 17.43) * mm});
            skLineSegment(sketch, "E821", {"start": v(46.28, 17.43) * mm, "end": v(45.6, 17.43) * mm});
            skLineSegment(sketch, "E822", {"start": v(45.6, 17.43) * mm, "end": v(45.54, 17.47) * mm});
            skLineSegment(sketch, "E823", {"start": v(45.54, 17.47) * mm, "end": v(45.48, 17.5) * mm});
            skLineSegment(sketch, "E824", {"start": v(45.48, 17.5) * mm, "end": v(45.25, 17.76) * mm});
            skLineSegment(sketch, "E825", {"start": v(45.25, 17.76) * mm, "end": v(45.14, 18.06) * mm});
            skLineSegment(sketch, "E826", {"start": v(45.14, 18.06) * mm, "end": v(45.14, 18.16) * mm});
            skLineSegment(sketch, "E827", {"start": v(45.14, 18.16) * mm, "end": v(45.14, 18.26) * mm});
            skLineSegment(sketch, "E828", {"start": v(45.14, 18.26) * mm, "end": v(45.25, 18.56) * mm});
            skLineSegment(sketch, "E829", {"start": v(45.25, 18.56) * mm, "end": v(45.48, 18.82) * mm});
            skLineSegment(sketch, "E830", {"start": v(45.48, 18.82) * mm, "end": v(45.54, 18.85) * mm});
            skLineSegment(sketch, "E831", {"start": v(45.54, 18.85) * mm, "end": v(45.6, 18.9) * mm});
            skLineSegment(sketch, "E832", {"start": v(45.6, 18.9) * mm, "end": v(46.28, 18.9) * mm});
            skLineSegment(sketch, "E833", {"start": v(46.28, 18.9) * mm, "end": v(46.34, 18.85) * mm});
            skLineSegment(sketch, "E834", {"start": v(46.34, 18.85) * mm, "end": v(46.4, 18.82) * mm});
            skLineSegment(sketch, "E835", {"start": v(46.4, 18.82) * mm, "end": v(46.63, 18.56) * mm});
            skLineSegment(sketch, "E836", {"start": v(46.63, 18.56) * mm, "end": v(46.74, 18.26) * mm});
            skLineSegment(sketch, "E837", {"start": v(46.74, 18.26) * mm, "end": v(46.74, 18.16) * mm});
            skLineSegment(sketch, "E838", {"start": v(50.96, 13.06) * mm, "end": v(49.45, 13.06) * mm});
            skLineSegment(sketch, "E839", {"start": v(46.74, 20.66) * mm, "end": v(46.74, 20.56) * mm});
            skLineSegment(sketch, "E840", {"start": v(46.74, 20.56) * mm, "end": v(46.63, 20.26) * mm});
            skLineSegment(sketch, "E841", {"start": v(46.63, 20.26) * mm, "end": v(46.4, 20) * mm});
            skLineSegment(sketch, "E842", {"start": v(46.4, 20) * mm, "end": v(46.34, 19.97) * mm});
            skLineSegment(sketch, "E843", {"start": v(46.34, 19.97) * mm, "end": v(46.28, 19.93) * mm});
            skLineSegment(sketch, "E844", {"start": v(46.28, 19.93) * mm, "end": v(45.6, 19.93) * mm});
            skLineSegment(sketch, "E845", {"start": v(45.6, 19.93) * mm, "end": v(45.54, 19.97) * mm});
            skLineSegment(sketch, "E846", {"start": v(45.54, 19.97) * mm, "end": v(45.48, 20) * mm});
            skLineSegment(sketch, "E847", {"start": v(45.48, 20) * mm, "end": v(45.25, 20.26) * mm});
            skLineSegment(sketch, "E848", {"start": v(45.25, 20.26) * mm, "end": v(45.14, 20.56) * mm});
            skLineSegment(sketch, "E849", {"start": v(45.14, 20.56) * mm, "end": v(45.14, 20.66) * mm});
            skLineSegment(sketch, "E850", {"start": v(45.14, 20.66) * mm, "end": v(45.14, 20.76) * mm});
            skLineSegment(sketch, "E851", {"start": v(45.14, 20.76) * mm, "end": v(45.25, 21.06) * mm});
            skLineSegment(sketch, "E852", {"start": v(45.25, 21.06) * mm, "end": v(45.48, 21.32) * mm});
            skLineSegment(sketch, "E853", {"start": v(45.48, 21.32) * mm, "end": v(45.54, 21.35) * mm});
            skLineSegment(sketch, "E854", {"start": v(45.54, 21.35) * mm, "end": v(45.6, 21.39) * mm});
            skLineSegment(sketch, "E855", {"start": v(45.6, 21.39) * mm, "end": v(46.28, 21.39) * mm});
            skLineSegment(sketch, "E856", {"start": v(46.28, 21.39) * mm, "end": v(46.34, 21.35) * mm});
            skLineSegment(sketch, "E857", {"start": v(46.34, 21.35) * mm, "end": v(46.4, 21.32) * mm});
            skLineSegment(sketch, "E858", {"start": v(46.4, 21.32) * mm, "end": v(46.63, 21.06) * mm});
            skLineSegment(sketch, "E859", {"start": v(46.63, 21.06) * mm, "end": v(46.74, 20.76) * mm});
            skLineSegment(sketch, "E860", {"start": v(46.74, 20.76) * mm, "end": v(46.74, 20.66) * mm});
            skLineSegment(sketch, "E861", {"start": v(21.42, -2.25) * mm, "end": v(21.42, -2.4) * mm});
            skLineSegment(sketch, "E862", {"start": v(21.42, -2.4) * mm, "end": v(21.14, -2.8) * mm});
            skLineSegment(sketch, "E863", {"start": v(21.14, -2.8) * mm, "end": v(21.08, -2.84) * mm});
            skLineSegment(sketch, "E864", {"start": v(21.08, -2.84) * mm, "end": v(21.03, -2.87) * mm});
            skLineSegment(sketch, "E865", {"start": v(21.03, -2.87) * mm, "end": v(20.46, -2.87) * mm});
            skLineSegment(sketch, "E866", {"start": v(20.46, -2.87) * mm, "end": v(20.4, -2.84) * mm});
            skLineSegment(sketch, "E867", {"start": v(20.4, -2.84) * mm, "end": v(20.36, -2.8) * mm});
            skLineSegment(sketch, "E868", {"start": v(20.36, -2.8) * mm, "end": v(20.07, -2.4) * mm});
            skLineSegment(sketch, "E869", {"start": v(20.07, -2.4) * mm, "end": v(20.07, -2.25) * mm});
            skLineSegment(sketch, "E870", {"start": v(20.07, -2.25) * mm, "end": v(20.07, -2.1) * mm});
            skLineSegment(sketch, "E871", {"start": v(20.07, -2.1) * mm, "end": v(20.36, -1.7) * mm});
            skLineSegment(sketch, "E872", {"start": v(20.36, -1.7) * mm, "end": v(20.4, -1.67) * mm});
            skLineSegment(sketch, "E873", {"start": v(20.4, -1.67) * mm, "end": v(20.46, -1.64) * mm});
            skLineSegment(sketch, "E874", {"start": v(20.46, -1.64) * mm, "end": v(21.03, -1.64) * mm});
            skLineSegment(sketch, "E875", {"start": v(21.03, -1.64) * mm, "end": v(21.08, -1.67) * mm});
            skLineSegment(sketch, "E876", {"start": v(21.08, -1.67) * mm, "end": v(21.14, -1.7) * mm});
            skLineSegment(sketch, "E877", {"start": v(21.14, -1.7) * mm, "end": v(21.42, -2.12) * mm});
            skLineSegment(sketch, "E878", {"start": v(21.42, -2.12) * mm, "end": v(21.42, -2.25) * mm});
            skLineSegment(sketch, "E879", {"start": v(-59.45, 13.97) * mm, "end": v(-59.45, 13.95) * mm});
            skLineSegment(sketch, "E880", {"start": v(-59.45, 13.95) * mm, "end": v(-59.5, 13.89) * mm});
            skLineSegment(sketch, "E881", {"start": v(-59.5, 13.89) * mm, "end": v(-59.5, 13.88) * mm});
            skLineSegment(sketch, "E882", {"start": v(-59.5, 13.88) * mm, "end": v(-59.5, 13.88) * mm});
            skLineSegment(sketch, "E883", {"start": v(-59.5, 13.88) * mm, "end": v(-59.6, 13.88) * mm});
            skLineSegment(sketch, "E884", {"start": v(-59.6, 13.88) * mm, "end": v(-59.6, 13.88) * mm});
            skLineSegment(sketch, "E885", {"start": v(-59.6, 13.88) * mm, "end": v(-59.6, 13.89) * mm});
            skLineSegment(sketch, "E886", {"start": v(-59.6, 13.89) * mm, "end": v(-59.65, 13.95) * mm});
            skLineSegment(sketch, "E887", {"start": v(-59.65, 13.95) * mm, "end": v(-59.65, 13.97) * mm});
            skLineSegment(sketch, "E888", {"start": v(-59.65, 13.97) * mm, "end": v(-59.65, 14) * mm});
            skLineSegment(sketch, "E889", {"start": v(-59.65, 14) * mm, "end": v(-59.58, 14.07) * mm});
            skLineSegment(sketch, "E890", {"start": v(-59.58, 14.07) * mm, "end": v(-59.55, 14.07) * mm});
            skLineSegment(sketch, "E891", {"start": v(-59.55, 14.07) * mm, "end": v(-59.53, 14.07) * mm});
            skLineSegment(sketch, "E892", {"start": v(-59.53, 14.07) * mm, "end": v(-59.45, 14) * mm});
            skLineSegment(sketch, "E893", {"start": v(-59.45, 14) * mm, "end": v(-59.45, 13.97) * mm});
            skLineSegment(sketch, "E894", {"start": v(-52.59, 30.02) * mm, "end": v(-52.59, 30) * mm});
            skLineSegment(sketch, "E895", {"start": v(-52.59, 30) * mm, "end": v(-52.63, 29.94) * mm});
            skLineSegment(sketch, "E896", {"start": v(-52.63, 29.94) * mm, "end": v(-52.64, 29.93) * mm});
            skLineSegment(sketch, "E897", {"start": v(-52.64, 29.93) * mm, "end": v(-52.65, 29.93) * mm});
            skLineSegment(sketch, "E898", {"start": v(-52.65, 29.93) * mm, "end": v(-52.74, 29.93) * mm});
            skLineSegment(sketch, "E899", {"start": v(-52.74, 29.93) * mm, "end": v(-52.74, 29.93) * mm});
            skLineSegment(sketch, "E900", {"start": v(-52.74, 29.93) * mm, "end": v(-52.75, 29.94) * mm});
            skLineSegment(sketch, "E901", {"start": v(-52.75, 29.94) * mm, "end": v(-52.8, 30) * mm});
            skLineSegment(sketch, "E902", {"start": v(-52.8, 30) * mm, "end": v(-52.8, 30.02) * mm});
            skLineSegment(sketch, "E903", {"start": v(-52.8, 30.02) * mm, "end": v(-52.8, 30.05) * mm});
            skLineSegment(sketch, "E904", {"start": v(-52.8, 30.05) * mm, "end": v(-52.75, 30.1) * mm});
            skLineSegment(sketch, "E905", {"start": v(-52.75, 30.1) * mm, "end": v(-52.74, 30.11) * mm});
            skLineSegment(sketch, "E906", {"start": v(-52.74, 30.11) * mm, "end": v(-52.74, 30.12) * mm});
            skLineSegment(sketch, "E907", {"start": v(-52.74, 30.12) * mm, "end": v(-52.65, 30.12) * mm});
            skLineSegment(sketch, "E908", {"start": v(-52.65, 30.12) * mm, "end": v(-52.64, 30.11) * mm});
            skLineSegment(sketch, "E909", {"start": v(-52.64, 30.11) * mm, "end": v(-52.63, 30.1) * mm});
            skLineSegment(sketch, "E910", {"start": v(-52.63, 30.1) * mm, "end": v(-52.59, 30.04) * mm});
            skLineSegment(sketch, "E911", {"start": v(-52.59, 30.04) * mm, "end": v(-52.59, 30.02) * mm});
            skLineSegment(sketch, "E912", {"start": v(-31.2, 49.2) * mm, "end": v(-31.2, 49.2) * mm});
            skLineSegment(sketch, "E913", {"start": v(-31.2, 49.2) * mm, "end": v(-31.21, 49.18) * mm});
            skLineSegment(sketch, "E914", {"start": v(-31.21, 49.18) * mm, "end": v(-31.22, 49.18) * mm});
            skLineSegment(sketch, "E915", {"start": v(-31.22, 49.18) * mm, "end": v(-31.22, 49.18) * mm});
            skLineSegment(sketch, "E916", {"start": v(-31.22, 49.18) * mm, "end": v(-31.24, 49.18) * mm});
            skLineSegment(sketch, "E917", {"start": v(-31.24, 49.18) * mm, "end": v(-31.24, 49.18) * mm});
            skLineSegment(sketch, "E918", {"start": v(-31.24, 49.18) * mm, "end": v(-31.25, 49.2) * mm});
            skLineSegment(sketch, "E919", {"start": v(-31.25, 49.2) * mm, "end": v(-31.25, 49.2) * mm});
            skLineSegment(sketch, "E920", {"start": v(-31.25, 49.2) * mm, "end": v(-31.24, 49.22) * mm});
            skLineSegment(sketch, "E921", {"start": v(-31.24, 49.22) * mm, "end": v(-31.24, 49.22) * mm});
            skLineSegment(sketch, "E922", {"start": v(-31.24, 49.22) * mm, "end": v(-31.22, 49.22) * mm});
            skLineSegment(sketch, "E923", {"start": v(-31.22, 49.22) * mm, "end": v(-31.22, 49.22) * mm});
            skLineSegment(sketch, "E924", {"start": v(-31.22, 49.22) * mm, "end": v(-31.21, 49.22) * mm});
            skLineSegment(sketch, "E925", {"start": v(-31.21, 49.22) * mm, "end": v(-31.2, 49.2) * mm});
            skLineSegment(sketch, "E926", {"start": v(-42.18, -49.66) * mm, "end": v(-42.18, -49.67) * mm});
            skLineSegment(sketch, "E927", {"start": v(-42.18, -49.67) * mm, "end": v(-42.19, -49.68) * mm});
            skLineSegment(sketch, "E928", {"start": v(-42.19, -49.68) * mm, "end": v(-42.19, -49.68) * mm});
            skLineSegment(sketch, "E929", {"start": v(-42.19, -49.68) * mm, "end": v(-42.2, -49.68) * mm});
            skLineSegment(sketch, "E930", {"start": v(-42.2, -49.68) * mm, "end": v(-42.21, -49.68) * mm});
            skLineSegment(sketch, "E931", {"start": v(-42.21, -49.68) * mm, "end": v(-42.21, -49.68) * mm});
            skLineSegment(sketch, "E932", {"start": v(-42.21, -49.68) * mm, "end": v(-42.22, -49.68) * mm});
            skLineSegment(sketch, "E933", {"start": v(-42.22, -49.68) * mm, "end": v(-42.23, -49.66) * mm});
            skLineSegment(sketch, "E934", {"start": v(-42.23, -49.66) * mm, "end": v(-42.23, -49.66) * mm});
            skLineSegment(sketch, "E935", {"start": v(-42.23, -49.66) * mm, "end": v(-42.23, -49.65) * mm});
            skLineSegment(sketch, "E936", {"start": v(-42.23, -49.65) * mm, "end": v(-42.22, -49.64) * mm});
            skLineSegment(sketch, "E937", {"start": v(-42.22, -49.64) * mm, "end": v(-42.21, -49.64) * mm});
            skLineSegment(sketch, "E938", {"start": v(-42.21, -49.64) * mm, "end": v(-42.21, -49.64) * mm});
            skLineSegment(sketch, "E939", {"start": v(-42.21, -49.64) * mm, "end": v(-42.2, -49.64) * mm});
            skLineSegment(sketch, "E940", {"start": v(-42.2, -49.64) * mm, "end": v(-42.19, -49.64) * mm});
            skLineSegment(sketch, "E941", {"start": v(-42.19, -49.64) * mm, "end": v(-42.19, -49.64) * mm});
            skLineSegment(sketch, "E942", {"start": v(-42.19, -49.64) * mm, "end": v(-42.18, -49.65) * mm});
            skLineSegment(sketch, "E943", {"start": v(-42.18, -49.65) * mm, "end": v(-42.18, -49.66) * mm});
            skLineSegment(sketch, "E944", {"start": v(-46.24, -45.72) * mm, "end": v(-46.24, -45.74) * mm});
            skLineSegment(sketch, "E945", {"start": v(-46.24, -45.74) * mm, "end": v(-46.29, -45.8) * mm});
            skLineSegment(sketch, "E946", {"start": v(-46.29, -45.8) * mm, "end": v(-46.3, -45.8) * mm});
            skLineSegment(sketch, "E947", {"start": v(-46.3, -45.8) * mm, "end": v(-46.3, -45.8) * mm});
            skLineSegment(sketch, "E948", {"start": v(-46.3, -45.8) * mm, "end": v(-46.39, -45.8) * mm});
            skLineSegment(sketch, "E949", {"start": v(-46.39, -45.8) * mm, "end": v(-46.4, -45.8) * mm});
            skLineSegment(sketch, "E950", {"start": v(-46.4, -45.8) * mm, "end": v(-46.4, -45.8) * mm});
            skLineSegment(sketch, "E951", {"start": v(-46.4, -45.8) * mm, "end": v(-46.45, -45.74) * mm});
            skLineSegment(sketch, "E952", {"start": v(-46.45, -45.74) * mm, "end": v(-46.45, -45.72) * mm});
            skLineSegment(sketch, "E953", {"start": v(-46.45, -45.72) * mm, "end": v(-46.45, -45.7) * mm});
            skLineSegment(sketch, "E954", {"start": v(-46.45, -45.7) * mm, "end": v(-46.4, -45.63) * mm});
            skLineSegment(sketch, "E955", {"start": v(-46.4, -45.63) * mm, "end": v(-46.4, -45.63) * mm});
            skLineSegment(sketch, "E956", {"start": v(-46.4, -45.63) * mm, "end": v(-46.39, -45.62) * mm});
            skLineSegment(sketch, "E957", {"start": v(-46.39, -45.62) * mm, "end": v(-46.3, -45.62) * mm});
            skLineSegment(sketch, "E958", {"start": v(-46.3, -45.62) * mm, "end": v(-46.3, -45.63) * mm});
            skLineSegment(sketch, "E959", {"start": v(-46.3, -45.63) * mm, "end": v(-46.29, -45.63) * mm});
            skLineSegment(sketch, "E960", {"start": v(-46.29, -45.63) * mm, "end": v(-46.24, -45.7) * mm});
            skLineSegment(sketch, "E961", {"start": v(-46.24, -45.7) * mm, "end": v(-46.24, -45.72) * mm});
            skLineSegment(sketch, "E962", {"start": v(16.5, 17.3) * mm, "end": v(16.5, 17.3) * mm});
            skLineSegment(sketch, "E963", {"start": v(16.5, 17.3) * mm, "end": v(16.49, 17.28) * mm});
            skLineSegment(sketch, "E964", {"start": v(16.49, 17.28) * mm, "end": v(16.49, 17.28) * mm});
            skLineSegment(sketch, "E965", {"start": v(16.49, 17.28) * mm, "end": v(16.48, 17.28) * mm});
            skLineSegment(sketch, "E966", {"start": v(16.48, 17.28) * mm, "end": v(16.46, 17.28) * mm});
            skLineSegment(sketch, "E967", {"start": v(16.46, 17.28) * mm, "end": v(16.46, 17.28) * mm});
            skLineSegment(sketch, "E968", {"start": v(16.46, 17.28) * mm, "end": v(16.45, 17.3) * mm});
            skLineSegment(sketch, "E969", {"start": v(16.45, 17.3) * mm, "end": v(16.45, 17.3) * mm});
            skLineSegment(sketch, "E970", {"start": v(16.45, 17.3) * mm, "end": v(16.46, 17.32) * mm});
            skLineSegment(sketch, "E971", {"start": v(16.46, 17.32) * mm, "end": v(16.46, 17.32) * mm});
            skLineSegment(sketch, "E972", {"start": v(16.46, 17.32) * mm, "end": v(16.48, 17.32) * mm});
            skLineSegment(sketch, "E973", {"start": v(16.48, 17.32) * mm, "end": v(16.49, 17.32) * mm});
            skLineSegment(sketch, "E974", {"start": v(16.49, 17.32) * mm, "end": v(16.49, 17.32) * mm});
            skLineSegment(sketch, "E975", {"start": v(16.49, 17.32) * mm, "end": v(16.5, 17.3) * mm});
            skLineSegment(sketch, "E976", {"start": v(15.26, -56.34) * mm, "end": v(15.26, -56.34) * mm});
            skLineSegment(sketch, "E977", {"start": v(15.26, -56.34) * mm, "end": v(15.25, -56.36) * mm});
            skLineSegment(sketch, "E978", {"start": v(15.25, -56.36) * mm, "end": v(15.25, -56.36) * mm});
            skLineSegment(sketch, "E979", {"start": v(15.25, -56.36) * mm, "end": v(15.23, -56.36) * mm});
            skLineSegment(sketch, "E980", {"start": v(15.23, -56.36) * mm, "end": v(15.22, -56.36) * mm});
            skLineSegment(sketch, "E981", {"start": v(15.22, -56.36) * mm, "end": v(15.22, -56.36) * mm});
            skLineSegment(sketch, "E982", {"start": v(15.22, -56.36) * mm, "end": v(15.21, -56.34) * mm});
            skLineSegment(sketch, "E983", {"start": v(15.21, -56.34) * mm, "end": v(15.21, -56.34) * mm});
            skLineSegment(sketch, "E984", {"start": v(15.21, -56.34) * mm, "end": v(15.21, -56.33) * mm});
            skLineSegment(sketch, "E985", {"start": v(15.21, -56.33) * mm, "end": v(15.22, -56.32) * mm});
            skLineSegment(sketch, "E986", {"start": v(15.22, -56.32) * mm, "end": v(15.22, -56.31) * mm});
            skLineSegment(sketch, "E987", {"start": v(15.22, -56.31) * mm, "end": v(15.23, -56.31) * mm});
            skLineSegment(sketch, "E988", {"start": v(15.23, -56.31) * mm, "end": v(15.25, -56.31) * mm});
            skLineSegment(sketch, "E989", {"start": v(15.25, -56.31) * mm, "end": v(15.25, -56.31) * mm});
            skLineSegment(sketch, "E990", {"start": v(15.25, -56.31) * mm, "end": v(15.26, -56.33) * mm});
            skLineSegment(sketch, "E991", {"start": v(15.26, -56.33) * mm, "end": v(15.26, -56.34) * mm});
            skLineSegment(sketch, "E992", {"start": v(53.5, -34.29) * mm, "end": v(53.5, -34.3) * mm});
            skLineSegment(sketch, "E993", {"start": v(53.5, -34.3) * mm, "end": v(53.5, -34.31) * mm});
            skLineSegment(sketch, "E994", {"start": v(53.5, -34.31) * mm, "end": v(53.5, -34.31) * mm});
            skLineSegment(sketch, "E995", {"start": v(53.5, -34.31) * mm, "end": v(53.47, -34.31) * mm});
            skLineSegment(sketch, "E996", {"start": v(53.47, -34.31) * mm, "end": v(53.47, -34.31) * mm});
            skLineSegment(sketch, "E997", {"start": v(53.47, -34.31) * mm, "end": v(53.45, -34.3) * mm});
            skLineSegment(sketch, "E998", {"start": v(53.45, -34.3) * mm, "end": v(53.45, -34.29) * mm});
            skLineSegment(sketch, "E999", {"start": v(53.45, -34.29) * mm, "end": v(53.45, -34.28) * mm});
            skLineSegment(sketch, "E1000", {"start": v(53.45, -34.28) * mm, "end": v(53.47, -34.27) * mm});
            skLineSegment(sketch, "E1001", {"start": v(53.47, -34.27) * mm, "end": v(53.47, -34.27) * mm});
            skLineSegment(sketch, "E1002", {"start": v(53.47, -34.27) * mm, "end": v(53.5, -34.27) * mm});
            skLineSegment(sketch, "E1003", {"start": v(53.5, -34.27) * mm, "end": v(53.5, -34.27) * mm});
            skLineSegment(sketch, "E1004", {"start": v(53.5, -34.27) * mm, "end": v(53.5, -34.28) * mm});
            skLineSegment(sketch, "E1005", {"start": v(53.5, -34.28) * mm, "end": v(53.5, -34.29) * mm});
            skLineSegment(sketch, "E1006", {"start": v(13.63, -40.39) * mm, "end": v(13.63, -40.4) * mm});
            skLineSegment(sketch, "E1007", {"start": v(13.63, -40.4) * mm, "end": v(13.62, -40.4) * mm});
            skLineSegment(sketch, "E1008", {"start": v(13.62, -40.4) * mm, "end": v(13.62, -40.4) * mm});
            skLineSegment(sketch, "E1009", {"start": v(13.62, -40.4) * mm, "end": v(13.61, -40.4) * mm});
            skLineSegment(sketch, "E1010", {"start": v(13.61, -40.4) * mm, "end": v(13.6, -40.4) * mm});
            skLineSegment(sketch, "E1011", {"start": v(13.6, -40.4) * mm, "end": v(13.59, -40.4) * mm});
            skLineSegment(sketch, "E1012", {"start": v(13.59, -40.4) * mm, "end": v(13.59, -40.4) * mm});
            skLineSegment(sketch, "E1013", {"start": v(13.59, -40.4) * mm, "end": v(13.58, -40.4) * mm});
            skLineSegment(sketch, "E1014", {"start": v(13.58, -40.4) * mm, "end": v(13.58, -40.39) * mm});
            skLineSegment(sketch, "E1015", {"start": v(13.58, -40.39) * mm, "end": v(13.58, -40.38) * mm});
            skLineSegment(sketch, "E1016", {"start": v(13.58, -40.38) * mm, "end": v(13.59, -40.36) * mm});
            skLineSegment(sketch, "E1017", {"start": v(13.59, -40.36) * mm, "end": v(13.59, -40.36) * mm});
            skLineSegment(sketch, "E1018", {"start": v(13.59, -40.36) * mm, "end": v(13.6, -40.36) * mm});
            skLineSegment(sketch, "E1019", {"start": v(13.6, -40.36) * mm, "end": v(13.61, -40.36) * mm});
            skLineSegment(sketch, "E1020", {"start": v(13.61, -40.36) * mm, "end": v(13.62, -40.36) * mm});
            skLineSegment(sketch, "E1021", {"start": v(13.62, -40.36) * mm, "end": v(13.62, -40.36) * mm});
            skLineSegment(sketch, "E1022", {"start": v(13.62, -40.36) * mm, "end": v(13.63, -40.38) * mm});
            skLineSegment(sketch, "E1023", {"start": v(13.63, -40.38) * mm, "end": v(13.63, -40.39) * mm});
            skLineSegment(sketch, "E1024", {"start": v(-17.38, 35.33) * mm, "end": v(-17.38, 35.33) * mm});
            skLineSegment(sketch, "E1025", {"start": v(-17.38, 35.33) * mm, "end": v(-17.4, 35.31) * mm});
            skLineSegment(sketch, "E1026", {"start": v(-17.4, 35.31) * mm, "end": v(-17.4, 35.3) * mm});
            skLineSegment(sketch, "E1027", {"start": v(-17.4, 35.3) * mm, "end": v(-17.4, 35.3) * mm});
            skLineSegment(sketch, "E1028", {"start": v(-17.4, 35.3) * mm, "end": v(-17.42, 35.3) * mm});
            skLineSegment(sketch, "E1029", {"start": v(-17.42, 35.3) * mm, "end": v(-17.42, 35.3) * mm});
            skLineSegment(sketch, "E1030", {"start": v(-17.42, 35.3) * mm, "end": v(-17.43, 35.31) * mm});
            skLineSegment(sketch, "E1031", {"start": v(-17.43, 35.31) * mm, "end": v(-17.44, 35.33) * mm});
            skLineSegment(sketch, "E1032", {"start": v(-17.44, 35.33) * mm, "end": v(-17.44, 35.33) * mm});
            skLineSegment(sketch, "E1033", {"start": v(-17.44, 35.33) * mm, "end": v(-17.44, 35.34) * mm});
            skLineSegment(sketch, "E1034", {"start": v(-17.44, 35.34) * mm, "end": v(-17.43, 35.35) * mm});
            skLineSegment(sketch, "E1035", {"start": v(-17.43, 35.35) * mm, "end": v(-17.42, 35.35) * mm});
            skLineSegment(sketch, "E1036", {"start": v(-17.42, 35.35) * mm, "end": v(-17.42, 35.36) * mm});
            skLineSegment(sketch, "E1037", {"start": v(-17.42, 35.36) * mm, "end": v(-17.4, 35.36) * mm});
            skLineSegment(sketch, "E1038", {"start": v(-17.4, 35.36) * mm, "end": v(-17.4, 35.35) * mm});
            skLineSegment(sketch, "E1039", {"start": v(-17.4, 35.35) * mm, "end": v(-17.4, 35.35) * mm});
            skLineSegment(sketch, "E1040", {"start": v(-17.4, 35.35) * mm, "end": v(-17.38, 35.34) * mm});
            skLineSegment(sketch, "E1041", {"start": v(-17.38, 35.34) * mm, "end": v(-17.38, 35.33) * mm});
            skLineSegment(sketch, "E1042", {"start": v(-53.94, -17.27) * mm, "end": v(-53.94, -17.28) * mm});
            skLineSegment(sketch, "E1043", {"start": v(-53.94, -17.28) * mm, "end": v(-53.95, -17.3) * mm});
            skLineSegment(sketch, "E1044", {"start": v(-53.95, -17.3) * mm, "end": v(-53.95, -17.3) * mm});
            skLineSegment(sketch, "E1045", {"start": v(-53.95, -17.3) * mm, "end": v(-53.97, -17.3) * mm});
            skLineSegment(sketch, "E1046", {"start": v(-53.97, -17.3) * mm, "end": v(-53.97, -17.3) * mm});
            skLineSegment(sketch, "E1047", {"start": v(-53.97, -17.3) * mm, "end": v(-53.98, -17.3) * mm});
            skLineSegment(sketch, "E1048", {"start": v(-53.98, -17.3) * mm, "end": v(-53.99, -17.28) * mm});
            skLineSegment(sketch, "E1049", {"start": v(-53.99, -17.28) * mm, "end": v(-53.99, -17.27) * mm});
            skLineSegment(sketch, "E1050", {"start": v(-53.99, -17.27) * mm, "end": v(-53.99, -17.27) * mm});
            skLineSegment(sketch, "E1051", {"start": v(-53.99, -17.27) * mm, "end": v(-53.98, -17.25) * mm});
            skLineSegment(sketch, "E1052", {"start": v(-53.98, -17.25) * mm, "end": v(-53.97, -17.25) * mm});
            skLineSegment(sketch, "E1053", {"start": v(-53.97, -17.25) * mm, "end": v(-53.97, -17.25) * mm});
            skLineSegment(sketch, "E1054", {"start": v(-53.97, -17.25) * mm, "end": v(-53.95, -17.25) * mm});
            skLineSegment(sketch, "E1055", {"start": v(-53.95, -17.25) * mm, "end": v(-53.95, -17.25) * mm});
            skLineSegment(sketch, "E1056", {"start": v(-53.95, -17.25) * mm, "end": v(-53.94, -17.27) * mm});
            skLineSegment(sketch, "E1057", {"start": v(-53.94, -17.27) * mm, "end": v(-53.94, -17.27) * mm});
            skLineSegment(sketch, "E1058", {"start": v(12.82, 20.7) * mm, "end": v(12.82, 20.7) * mm});
            skLineSegment(sketch, "E1059", {"start": v(12.82, 20.7) * mm, "end": v(12.8, 20.68) * mm});
            skLineSegment(sketch, "E1060", {"start": v(12.8, 20.68) * mm, "end": v(12.8, 20.68) * mm});
            skLineSegment(sketch, "E1061", {"start": v(12.8, 20.68) * mm, "end": v(12.78, 20.68) * mm});
            skLineSegment(sketch, "E1062", {"start": v(12.78, 20.68) * mm, "end": v(12.78, 20.68) * mm});
            skLineSegment(sketch, "E1063", {"start": v(12.78, 20.68) * mm, "end": v(12.76, 20.7) * mm});
            skLineSegment(sketch, "E1064", {"start": v(12.76, 20.7) * mm, "end": v(12.76, 20.7) * mm});
            skLineSegment(sketch, "E1065", {"start": v(12.76, 20.7) * mm, "end": v(12.78, 20.72) * mm});
            skLineSegment(sketch, "E1066", {"start": v(12.78, 20.72) * mm, "end": v(12.78, 20.72) * mm});
            skLineSegment(sketch, "E1067", {"start": v(12.78, 20.72) * mm, "end": v(12.8, 20.72) * mm});
            skLineSegment(sketch, "E1068", {"start": v(12.8, 20.72) * mm, "end": v(12.8, 20.72) * mm});
            skLineSegment(sketch, "E1069", {"start": v(12.8, 20.72) * mm, "end": v(12.82, 20.7) * mm});
            skLineSegment(sketch, "E1070", {"start": v(-51.9, -23.62) * mm, "end": v(-51.9, -23.63) * mm});
            skLineSegment(sketch, "E1071", {"start": v(-51.9, -23.63) * mm, "end": v(-51.92, -23.64) * mm});
            skLineSegment(sketch, "E1072", {"start": v(-51.92, -23.64) * mm, "end": v(-51.92, -23.64) * mm});
            skLineSegment(sketch, "E1073", {"start": v(-51.92, -23.64) * mm, "end": v(-51.94, -23.64) * mm});
            skLineSegment(sketch, "E1074", {"start": v(-51.94, -23.64) * mm, "end": v(-51.94, -23.64) * mm});
            skLineSegment(sketch, "E1075", {"start": v(-51.94, -23.64) * mm, "end": v(-51.95, -23.63) * mm});
            skLineSegment(sketch, "E1076", {"start": v(-51.95, -23.63) * mm, "end": v(-51.95, -23.62) * mm});
            skLineSegment(sketch, "E1077", {"start": v(-51.95, -23.62) * mm, "end": v(-51.95, -23.62) * mm});
            skLineSegment(sketch, "E1078", {"start": v(-51.95, -23.62) * mm, "end": v(-51.94, -23.6) * mm});
            skLineSegment(sketch, "E1079", {"start": v(-51.94, -23.6) * mm, "end": v(-51.94, -23.6) * mm});
            skLineSegment(sketch, "E1080", {"start": v(-51.94, -23.6) * mm, "end": v(-51.92, -23.6) * mm});
            skLineSegment(sketch, "E1081", {"start": v(-51.92, -23.6) * mm, "end": v(-51.92, -23.6) * mm});
            skLineSegment(sketch, "E1082", {"start": v(-51.92, -23.6) * mm, "end": v(-51.9, -23.62) * mm});
            skLineSegment(sketch, "E1083", {"start": v(-51.9, -23.62) * mm, "end": v(-51.9, -23.62) * mm});
            skLineSegment(sketch, "E1084", {"start": v(-16.2, 33.14) * mm, "end": v(-16.2, 33.13) * mm});
            skLineSegment(sketch, "E1085", {"start": v(-16.2, 33.13) * mm, "end": v(-16.2, 33.12) * mm});
            skLineSegment(sketch, "E1086", {"start": v(-16.2, 33.12) * mm, "end": v(-16.2, 33.12) * mm});
            skLineSegment(sketch, "E1087", {"start": v(-16.2, 33.12) * mm, "end": v(-16.23, 33.12) * mm});
            skLineSegment(sketch, "E1088", {"start": v(-16.23, 33.12) * mm, "end": v(-16.23, 33.12) * mm});
            skLineSegment(sketch, "E1089", {"start": v(-16.23, 33.12) * mm, "end": v(-16.24, 33.13) * mm});
            skLineSegment(sketch, "E1090", {"start": v(-16.24, 33.13) * mm, "end": v(-16.24, 33.14) * mm});
            skLineSegment(sketch, "E1091", {"start": v(-16.24, 33.14) * mm, "end": v(-16.24, 33.14) * mm});
            skLineSegment(sketch, "E1092", {"start": v(-16.24, 33.14) * mm, "end": v(-16.23, 33.16) * mm});
            skLineSegment(sketch, "E1093", {"start": v(-16.23, 33.16) * mm, "end": v(-16.23, 33.16) * mm});
            skLineSegment(sketch, "E1094", {"start": v(-16.23, 33.16) * mm, "end": v(-16.2, 33.16) * mm});
            skLineSegment(sketch, "E1095", {"start": v(-16.2, 33.16) * mm, "end": v(-16.2, 33.16) * mm});
            skLineSegment(sketch, "E1096", {"start": v(-16.2, 33.16) * mm, "end": v(-16.2, 33.14) * mm});
            skLineSegment(sketch, "E1097", {"start": v(-16.2, 33.14) * mm, "end": v(-16.2, 33.14) * mm});
            skLineSegment(sketch, "E1098", {"start": v(-31.63, 32.36) * mm, "end": v(-31.63, 32.35) * mm});
            skLineSegment(sketch, "E1099", {"start": v(-31.63, 32.35) * mm, "end": v(-31.65, 32.34) * mm});
            skLineSegment(sketch, "E1100", {"start": v(-31.65, 32.34) * mm, "end": v(-31.65, 32.34) * mm});
            skLineSegment(sketch, "E1101", {"start": v(-31.65, 32.34) * mm, "end": v(-31.67, 32.34) * mm});
            skLineSegment(sketch, "E1102", {"start": v(-31.67, 32.34) * mm, "end": v(-31.67, 32.34) * mm});
            skLineSegment(sketch, "E1103", {"start": v(-31.67, 32.34) * mm, "end": v(-31.69, 32.36) * mm});
            skLineSegment(sketch, "E1104", {"start": v(-31.69, 32.36) * mm, "end": v(-31.69, 32.36) * mm});
            skLineSegment(sketch, "E1105", {"start": v(-31.69, 32.36) * mm, "end": v(-31.67, 32.38) * mm});
            skLineSegment(sketch, "E1106", {"start": v(-31.67, 32.38) * mm, "end": v(-31.67, 32.38) * mm});
            skLineSegment(sketch, "E1107", {"start": v(-31.67, 32.38) * mm, "end": v(-31.65, 32.38) * mm});
            skLineSegment(sketch, "E1108", {"start": v(-31.65, 32.38) * mm, "end": v(-31.65, 32.38) * mm});
            skLineSegment(sketch, "E1109", {"start": v(-31.65, 32.38) * mm, "end": v(-31.63, 32.36) * mm});
            skLineSegment(sketch, "E1110", {"start": v(-31.63, 32.36) * mm, "end": v(-31.63, 32.36) * mm});
            skLineSegment(sketch, "E1111", {"start": v(-1.76, 23.04) * mm, "end": v(-1.76, 23.03) * mm});
            skLineSegment(sketch, "E1112", {"start": v(-1.76, 23.03) * mm, "end": v(-1.77, 23.02) * mm});
            skLineSegment(sketch, "E1113", {"start": v(-1.77, 23.02) * mm, "end": v(-1.77, 23.02) * mm});
            skLineSegment(sketch, "E1114", {"start": v(-1.77, 23.02) * mm, "end": v(-1.78, 23.02) * mm});
            skLineSegment(sketch, "E1115", {"start": v(-1.78, 23.02) * mm, "end": v(-1.8, 23.02) * mm});
            skLineSegment(sketch, "E1116", {"start": v(-1.8, 23.02) * mm, "end": v(-1.8, 23.02) * mm});
            skLineSegment(sketch, "E1117", {"start": v(-1.8, 23.02) * mm, "end": v(-1.8, 23.03) * mm});
            skLineSegment(sketch, "E1118", {"start": v(-1.8, 23.03) * mm, "end": v(-1.8, 23.04) * mm});
            skLineSegment(sketch, "E1119", {"start": v(-1.8, 23.04) * mm, "end": v(-1.8, 23.04) * mm});
            skLineSegment(sketch, "E1120", {"start": v(-1.8, 23.04) * mm, "end": v(-1.8, 23.06) * mm});
            skLineSegment(sketch, "E1121", {"start": v(-1.8, 23.06) * mm, "end": v(-1.8, 23.06) * mm});
            skLineSegment(sketch, "E1122", {"start": v(-1.8, 23.06) * mm, "end": v(-1.78, 23.06) * mm});
            skLineSegment(sketch, "E1123", {"start": v(-1.78, 23.06) * mm, "end": v(-1.77, 23.06) * mm});
            skLineSegment(sketch, "E1124", {"start": v(-1.77, 23.06) * mm, "end": v(-1.77, 23.06) * mm});
            skLineSegment(sketch, "E1125", {"start": v(-1.77, 23.06) * mm, "end": v(-1.76, 23.04) * mm});
            skLineSegment(sketch, "E1126", {"start": v(-1.76, 23.04) * mm, "end": v(-1.76, 23.04) * mm});
            skLineSegment(sketch, "E1127", {"start": v(-31.74, 34.57) * mm, "end": v(-31.74, 34.56) * mm});
            skLineSegment(sketch, "E1128", {"start": v(-31.74, 34.56) * mm, "end": v(-31.75, 34.55) * mm});
            skLineSegment(sketch, "E1129", {"start": v(-31.75, 34.55) * mm, "end": v(-31.75, 34.55) * mm});
            skLineSegment(sketch, "E1130", {"start": v(-31.75, 34.55) * mm, "end": v(-31.77, 34.55) * mm});
            skLineSegment(sketch, "E1131", {"start": v(-31.77, 34.55) * mm, "end": v(-31.77, 34.55) * mm});
            skLineSegment(sketch, "E1132", {"start": v(-31.77, 34.55) * mm, "end": v(-31.78, 34.55) * mm});
            skLineSegment(sketch, "E1133", {"start": v(-31.78, 34.55) * mm, "end": v(-31.79, 34.57) * mm});
            skLineSegment(sketch, "E1134", {"start": v(-31.79, 34.57) * mm, "end": v(-31.79, 34.57) * mm});
            skLineSegment(sketch, "E1135", {"start": v(-31.79, 34.57) * mm, "end": v(-31.79, 34.58) * mm});
            skLineSegment(sketch, "E1136", {"start": v(-31.79, 34.58) * mm, "end": v(-31.78, 34.6) * mm});
            skLineSegment(sketch, "E1137", {"start": v(-31.78, 34.6) * mm, "end": v(-31.77, 34.6) * mm});
            skLineSegment(sketch, "E1138", {"start": v(-31.77, 34.6) * mm, "end": v(-31.77, 34.6) * mm});
            skLineSegment(sketch, "E1139", {"start": v(-31.77, 34.6) * mm, "end": v(-31.75, 34.6) * mm});
            skLineSegment(sketch, "E1140", {"start": v(-31.75, 34.6) * mm, "end": v(-31.75, 34.6) * mm});
            skLineSegment(sketch, "E1141", {"start": v(-31.75, 34.6) * mm, "end": v(-31.74, 34.58) * mm});
            skLineSegment(sketch, "E1142", {"start": v(-31.74, 34.58) * mm, "end": v(-31.74, 34.57) * mm});
            skLineSegment(sketch, "E1143", {"start": v(55.28, -32) * mm, "end": v(55.28, -32) * mm});
            skLineSegment(sketch, "E1144", {"start": v(55.28, -32) * mm, "end": v(55.27, -32.02) * mm});
            skLineSegment(sketch, "E1145", {"start": v(55.27, -32.02) * mm, "end": v(55.27, -32.03) * mm});
            skLineSegment(sketch, "E1146", {"start": v(55.27, -32.03) * mm, "end": v(55.27, -32.03) * mm});
            skLineSegment(sketch, "E1147", {"start": v(55.27, -32.03) * mm, "end": v(55.25, -32.03) * mm});
            skLineSegment(sketch, "E1148", {"start": v(55.25, -32.03) * mm, "end": v(55.25, -32.03) * mm});
            skLineSegment(sketch, "E1149", {"start": v(55.25, -32.03) * mm, "end": v(55.24, -32.02) * mm});
            skLineSegment(sketch, "E1150", {"start": v(55.24, -32.02) * mm, "end": v(55.23, -32) * mm});
            skLineSegment(sketch, "E1151", {"start": v(55.23, -32) * mm, "end": v(55.23, -32) * mm});
            skLineSegment(sketch, "E1152", {"start": v(55.23, -32) * mm, "end": v(55.24, -31.98) * mm});
            skLineSegment(sketch, "E1153", {"start": v(55.24, -31.98) * mm, "end": v(55.25, -31.98) * mm});
            skLineSegment(sketch, "E1154", {"start": v(55.25, -31.98) * mm, "end": v(55.25, -31.98) * mm});
            skLineSegment(sketch, "E1155", {"start": v(55.25, -31.98) * mm, "end": v(55.27, -31.98) * mm});
            skLineSegment(sketch, "E1156", {"start": v(55.27, -31.98) * mm, "end": v(55.27, -31.98) * mm});
            skLineSegment(sketch, "E1157", {"start": v(55.27, -31.98) * mm, "end": v(55.28, -32) * mm});
            skLineSegment(sketch, "E1158", {"start": v(13.88, -41.91) * mm, "end": v(13.88, -41.92) * mm});
            skLineSegment(sketch, "E1159", {"start": v(13.88, -41.92) * mm, "end": v(13.87, -41.93) * mm});
            skLineSegment(sketch, "E1160", {"start": v(13.87, -41.93) * mm, "end": v(13.87, -41.93) * mm});
            skLineSegment(sketch, "E1161", {"start": v(13.87, -41.93) * mm, "end": v(13.85, -41.93) * mm});
            skLineSegment(sketch, "E1162", {"start": v(13.85, -41.93) * mm, "end": v(13.84, -41.93) * mm});
            skLineSegment(sketch, "E1163", {"start": v(13.84, -41.93) * mm, "end": v(13.84, -41.93) * mm});
            skLineSegment(sketch, "E1164", {"start": v(13.84, -41.93) * mm, "end": v(13.83, -41.91) * mm});
            skLineSegment(sketch, "E1165", {"start": v(13.83, -41.91) * mm, "end": v(13.83, -41.91) * mm});
            skLineSegment(sketch, "E1166", {"start": v(13.83, -41.91) * mm, "end": v(13.83, -41.9) * mm});
            skLineSegment(sketch, "E1167", {"start": v(13.83, -41.9) * mm, "end": v(13.84, -41.89) * mm});
            skLineSegment(sketch, "E1168", {"start": v(13.84, -41.89) * mm, "end": v(13.84, -41.89) * mm});
            skLineSegment(sketch, "E1169", {"start": v(13.84, -41.89) * mm, "end": v(13.85, -41.89) * mm});
            skLineSegment(sketch, "E1170", {"start": v(13.85, -41.89) * mm, "end": v(13.87, -41.89) * mm});
            skLineSegment(sketch, "E1171", {"start": v(13.87, -41.89) * mm, "end": v(13.87, -41.89) * mm});
            skLineSegment(sketch, "E1172", {"start": v(13.87, -41.89) * mm, "end": v(13.88, -41.9) * mm});
            skLineSegment(sketch, "E1173", {"start": v(13.88, -41.9) * mm, "end": v(13.88, -41.91) * mm});
            skLineSegment(sketch, "E1174", {"start": v(-41.95, -49.66) * mm, "end": v(-34.97, -56.64) * mm});
            skLineSegment(sketch, "E1175", {"start": v(49.7, -59.36) * mm, "end": v(49.7, -59.2) * mm});
            skLineSegment(sketch, "E1176", {"start": v(49.7, -59.2) * mm, "end": v(47.9, -57.4) * mm});
            skLineSegment(sketch, "E1177", {"start": v(47.9, -57.4) * mm, "end": v(-34.2, -57.4) * mm});
            skLineSegment(sketch, "E1178", {"start": v(-34.2, -57.4) * mm, "end": v(-34.97, -56.64) * mm});
            skLineSegment(sketch, "E1179", {"start": v(-52.7, 30.02) * mm, "end": v(-52.7, 20.83) * mm});
            skLineSegment(sketch, "E1180", {"start": v(-52.7, 20.83) * mm, "end": v(-59.55, 13.97) * mm});
            skLineSegment(sketch, "E1181", {"start": v(-59.55, -13.97) * mm, "end": v(-59.55, -16.51) * mm});
            skLineSegment(sketch, "E1182", {"start": v(-43.04, -44.45) * mm, "end": v(-43.04, -30.48) * mm});
            skLineSegment(sketch, "E1183", {"start": v(-43.04, -30.48) * mm, "end": v(-59.55, -13.97) * mm});
            skLineSegment(sketch, "E1184", {"start": v(-42.2, -49.66) * mm, "end": v(-41.95, -49.66) * mm});
            skLineSegment(sketch, "E1185", {"start": v(-22.72, 58.42) * mm, "end": v(-31.23, 49.91) * mm});
            skLineSegment(sketch, "E1186", {"start": v(-31.23, 49.91) * mm, "end": v(-31.23, 49.2) * mm});
            skLineSegment(sketch, "E1187", {"start": v(-60.6, -32.26) * mm, "end": v(-60.06, -32.8) * mm});
            skLineSegment(sketch, "E1188", {"start": v(-60.6, -25.62) * mm, "end": v(-60.6, -32.26) * mm});
            skLineSegment(sketch, "E1189", {"start": v(-60.06, -32.8) * mm, "end": v(-59.26, -32.8) * mm});
            skLineSegment(sketch, "E1190", {"start": v(-62.1, -24.13) * mm, "end": v(-60.6, -25.62) * mm});
            skLineSegment(sketch, "E1191", {"start": v(-59.26, -32.8) * mm, "end": v(-46.45, -45.61) * mm});
            skLineSegment(sketch, "E1192", {"start": v(-46.45, -45.61) * mm, "end": v(-46.35, -45.71) * mm});
            skLineSegment(sketch, "E1193", {"start": v(-4.94, 60.96) * mm, "end": v(-6.36, 59.54) * mm});
            skLineSegment(sketch, "E1194", {"start": v(-6.36, 59.54) * mm, "end": v(-10.56, 59.54) * mm});
            skLineSegment(sketch, "E1195", {"start": v(-10.56, 59.54) * mm, "end": v(-11.44, 58.65) * mm});
            skLineSegment(sketch, "E1196", {"start": v(-11.44, 58.65) * mm, "end": v(-11.44, 57.88) * mm});
            skLineSegment(sketch, "E1197", {"start": v(-20.5, 48.82) * mm, "end": v(-31.39, 48.82) * mm});
            skLineSegment(sketch, "E1198", {"start": v(-11.44, 57.88) * mm, "end": v(-20.5, 48.82) * mm});
            skLineSegment(sketch, "E1199", {"start": v(-31.39, 48.82) * mm, "end": v(-31.61, 49.04) * mm});
            skLineSegment(sketch, "E1200", {"start": v(-31.61, 49.04) * mm, "end": v(-31.61, 53.5) * mm});
            skLineSegment(sketch, "E1201", {"start": v(-31.61, 53.5) * mm, "end": v(-27.8, 57.3) * mm});
            skLineSegment(sketch, "E1202", {"start": v(-27.8, 57.3) * mm, "end": v(-27.8, 58.42) * mm});
            skLineSegment(sketch, "E1203", {"start": v(-4.94, 60.96) * mm, "end": v(16.47, 39.55) * mm});
            skLineSegment(sketch, "E1204", {"start": v(16.47, 39.55) * mm, "end": v(16.47, 17.3) * mm});
            skLineSegment(sketch, "E1205", {"start": v(50.2, 5.1) * mm, "end": v(50.2, -5.1) * mm});
            skLineSegment(sketch, "E1206", {"start": v(45.94, 2.5) * mm, "end": v(45.94, 5.48) * mm});
            skLineSegment(sketch, "E1207", {"start": v(45.94, 2.5) * mm, "end": v(48.54, 5.1) * mm});
            skLineSegment(sketch, "E1208", {"start": v(48.54, 5.1) * mm, "end": v(50.2, 5.1) * mm});
            skLineSegment(sketch, "E1209", {"start": v(13.6, -40.39) * mm, "end": v(19.19, -34.8) * mm});
            skLineSegment(sketch, "E1210", {"start": v(19.19, -34.8) * mm, "end": v(52.97, -34.8) * mm});
            skLineSegment(sketch, "E1211", {"start": v(52.97, -34.8) * mm, "end": v(53.48, -34.29) * mm});
            skLineSegment(sketch, "E1212", {"start": v(-17.41, 35.33) * mm, "end": v(-11.67, 29.59) * mm});
            skLineSegment(sketch, "E1213", {"start": v(-11.67, 29.59) * mm, "end": v(-11.67, 21.59) * mm});
            skLineSegment(sketch, "E1214", {"start": v(-11.67, 21.59) * mm, "end": v(-12.64, 20.61) * mm});
            skLineSegment(sketch, "E1215", {"start": v(-12.64, 20.61) * mm, "end": v(-12.64, 18.42) * mm});
            skLineSegment(sketch, "E1216", {"start": v(-12.64, 18.42) * mm, "end": v(-10.53, 16.3) * mm});
            skLineSegment(sketch, "E1217", {"start": v(-10.53, 16.3) * mm, "end": v(1, 16.3) * mm});
            skLineSegment(sketch, "E1218", {"start": v(1, 16.3) * mm, "end": v(4.7, 12.63) * mm});
            skLineSegment(sketch, "E1219", {"start": v(-25.1, 23.72) * mm, "end": v(-23.17, 23.72) * mm});
            skLineSegment(sketch, "E1220", {"start": v(-23.17, 23.72) * mm, "end": v(-22.87, 23.42) * mm});
            skLineSegment(sketch, "E1221", {"start": v(-25.18, 20.57) * mm, "end": v(-23.87, 20.57) * mm});
            skLineSegment(sketch, "E1222", {"start": v(-23.87, 20.57) * mm, "end": v(-22.74, 21.7) * mm});
            skLineSegment(sketch, "E1223", {"start": v(-43.78, 39.06) * mm, "end": v(-55.51, 50.8) * mm});
            skLineSegment(sketch, "E1224", {"start": v(-55.51, 50.8) * mm, "end": v(-60.82, 50.8) * mm});
            skLineSegment(sketch, "E1225", {"start": v(7.87, 22.79) * mm, "end": v(-8.41, 39.06) * mm});
            skLineSegment(sketch, "E1226", {"start": v(-8.41, 39.06) * mm, "end": v(-43.78, 39.06) * mm});
            skLineSegment(sketch, "E1227", {"start": v(-43.78, 58.07) * mm, "end": v(-55.55, 58.07) * mm});
            skLineSegment(sketch, "E1228", {"start": v(-55.55, 58.07) * mm, "end": v(-60.82, 52.8) * mm});
            skLineSegment(sketch, "E1229", {"start": v(12.57, 22.66) * mm, "end": v(-5.24, 40.46) * mm});
            skLineSegment(sketch, "E1230", {"start": v(-5.24, 40.46) * mm, "end": v(-26.18, 40.46) * mm});
            skLineSegment(sketch, "E1231", {"start": v(-26.18, 40.46) * mm, "end": v(-38.7, 52.98) * mm});
            skLineSegment(sketch, "E1232", {"start": v(-38.7, 52.98) * mm, "end": v(-43.78, 58.07) * mm});
            skLineSegment(sketch, "E1233", {"start": v(49.31, -61.67) * mm, "end": v(47.15, -59.51) * mm});
            skLineSegment(sketch, "E1234", {"start": v(60.72, -61.67) * mm, "end": v(49.31, -61.67) * mm});
            skLineSegment(sketch, "E1235", {"start": v(61.35, -61.04) * mm, "end": v(60.72, -61.67) * mm});
            skLineSegment(sketch, "E1236", {"start": v(61.35, -29.88) * mm, "end": v(61.35, -61.04) * mm});
            skLineSegment(sketch, "E1237", {"start": v(47.15, -59.51) * mm, "end": v(47.15, -59.36) * mm});
            skLineSegment(sketch, "E1238", {"start": v(60.56, -29.08) * mm, "end": v(61.35, -29.88) * mm});
            skLineSegment(sketch, "E1239", {"start": v(60.56, -29.08) * mm, "end": v(10.1, 21.37) * mm});
            skLineSegment(sketch, "E1240", {"start": v(60.67, -29.2) * mm, "end": v(60.56, -29.08) * mm});
            skLineSegment(sketch, "E1241", {"start": v(-10.5, 21.13) * mm, "end": v(-12.26, 19.37) * mm});
            skLineSegment(sketch, "E1242", {"start": v(-10.82, 17.13) * mm, "end": v(-8.69, 17.13) * mm});
            skLineSegment(sketch, "E1243", {"start": v(3.83, 21.37) * mm, "end": v(2.61, 22.6) * mm});
            skLineSegment(sketch, "E1244", {"start": v(-12.26, 19.37) * mm, "end": v(-12.26, 18.58) * mm});
            skLineSegment(sketch, "E1245", {"start": v(10.1, 21.37) * mm, "end": v(3.83, 21.37) * mm});
            skLineSegment(sketch, "E1246", {"start": v(2.61, 22.6) * mm, "end": v(0.96, 22.6) * mm});
            skLineSegment(sketch, "E1247", {"start": v(0.96, 22.6) * mm, "end": v(-0.5, 21.13) * mm});
            skLineSegment(sketch, "E1248", {"start": v(-8.69, 17.13) * mm, "end": v(-7.88, 17.13) * mm});
            skLineSegment(sketch, "E1249", {"start": v(-0.5, 21.13) * mm, "end": v(-10.5, 21.13) * mm});
            skLineSegment(sketch, "E1250", {"start": v(-12.26, 18.58) * mm, "end": v(-10.82, 17.13) * mm});
            skLineSegment(sketch, "E1251", {"start": v(60.95, -30) * mm, "end": v(60.7, -29.77) * mm});
            skLineSegment(sketch, "E1252", {"start": v(60.7, -29.77) * mm, "end": v(10.18, 20.75) * mm});
            skLineSegment(sketch, "E1253", {"start": v(54.77, -59.36) * mm, "end": v(54.77, -59.51) * mm});
            skLineSegment(sketch, "E1254", {"start": v(55.9, -60.63) * mm, "end": v(60.32, -60.63) * mm});
            skLineSegment(sketch, "E1255", {"start": v(54.77, -59.51) * mm, "end": v(55.9, -60.63) * mm});
            skLineSegment(sketch, "E1256", {"start": v(60.32, -60.63) * mm, "end": v(60.97, -59.97) * mm});
            skLineSegment(sketch, "E1257", {"start": v(60.97, -59.97) * mm, "end": v(60.97, -30.04) * mm});
            skLineSegment(sketch, "E1258", {"start": v(60.97, -30.04) * mm, "end": v(60.7, -29.77) * mm});
            skLineSegment(sketch, "E1259", {"start": v(10.18, 20.75) * mm, "end": v(-9.66, 20.75) * mm});
            skLineSegment(sketch, "E1260", {"start": v(-9.66, 20.75) * mm, "end": v(-10.87, 19.55) * mm});
            skLineSegment(sketch, "E1261", {"start": v(-10.87, 19.55) * mm, "end": v(-11.44, 18.98) * mm});
            skLineSegment(sketch, "E1262", {"start": v(59.9, -29.5) * mm, "end": v(59.84, -29.44) * mm});
            skLineSegment(sketch, "E1263", {"start": v(60.6, -30.2) * mm, "end": v(59.84, -29.44) * mm});
            skLineSegment(sketch, "E1264", {"start": v(59.84, -29.44) * mm, "end": v(11.48, 18.91) * mm});
            skLineSegment(sketch, "E1265", {"start": v(60.6, -55.93) * mm, "end": v(60.6, -30.2) * mm});
            skLineSegment(sketch, "E1266", {"start": v(57.31, -59.2) * mm, "end": v(60.6, -55.93) * mm});
            skLineSegment(sketch, "E1267", {"start": v(11.48, 18.91) * mm, "end": v(-6.68, 18.91) * mm});
            skLineSegment(sketch, "E1268", {"start": v(57.31, -59.36) * mm, "end": v(57.31, -59.2) * mm});
            skLineSegment(sketch, "E1269", {"start": v(-24.22, 9.7) * mm, "end": v(-26.99, 9.7) * mm});
            skLineSegment(sketch, "E1270", {"start": v(-26.99, 9.7) * mm, "end": v(-53.96, -17.27) * mm});
            skLineSegment(sketch, "E1271", {"start": v(-21.1, 16.18) * mm, "end": v(-21.1, 12.83) * mm});
            skLineSegment(sketch, "E1272", {"start": v(-21.1, 12.83) * mm, "end": v(-24.22, 9.7) * mm});
            skLineSegment(sketch, "E1273", {"start": v(-7.48, 58.42) * mm, "end": v(13.45, 37.49) * mm});
            skLineSegment(sketch, "E1274", {"start": v(13.45, 37.49) * mm, "end": v(13.45, 21.37) * mm});
            skLineSegment(sketch, "E1275", {"start": v(13.45, 21.37) * mm, "end": v(12.79, 20.7) * mm});
            skLineSegment(sketch, "E1276", {"start": v(-9.6, 13.82) * mm, "end": v(6.46, -2.25) * mm});
            skLineSegment(sketch, "E1277", {"start": v(6.46, -2.25) * mm, "end": v(20.75, -2.25) * mm});
            skLineSegment(sketch, "E1278", {"start": v(-10.02, 60.96) * mm, "end": v(-11.14, 59.84) * mm});
            skLineSegment(sketch, "E1279", {"start": v(-11.14, 59.84) * mm, "end": v(-28.34, 59.84) * mm});
            skLineSegment(sketch, "E1280", {"start": v(-28.34, 59.84) * mm, "end": v(-30.93, 62.44) * mm});
            skLineSegment(sketch, "E1281", {"start": v(-30.93, 62.44) * mm, "end": v(-58.1, 62.44) * mm});
            skLineSegment(sketch, "E1282", {"start": v(-58.1, 62.44) * mm, "end": v(-61.75, 58.8) * mm});
            skLineSegment(sketch, "E1283", {"start": v(-61.75, 58.8) * mm, "end": v(-61.75, -7.28) * mm});
            skLineSegment(sketch, "E1284", {"start": v(-61.75, -7.28) * mm, "end": v(-62.1, -7.62) * mm});
            skLineSegment(sketch, "E1285", {"start": v(-62.1, -19.05) * mm, "end": v(-60.97, -20.17) * mm});
            skLineSegment(sketch, "E1286", {"start": v(-60.97, -20.17) * mm, "end": v(-55.39, -20.17) * mm});
            skLineSegment(sketch, "E1287", {"start": v(-55.39, -20.17) * mm, "end": v(-51.93, -23.62) * mm});
            skLineSegment(sketch, "E1288", {"start": v(-31.66, 32.36) * mm, "end": v(-30.88, 33.14) * mm});
            skLineSegment(sketch, "E1289", {"start": v(-30.88, 33.14) * mm, "end": v(-16.22, 33.14) * mm});
            skLineSegment(sketch, "E1290", {"start": v(-31.76, 34.57) * mm, "end": v(-30.62, 35.71) * mm});
            skLineSegment(sketch, "E1291", {"start": v(-30.62, 35.71) * mm, "end": v(-14.46, 35.71) * mm});
            skLineSegment(sketch, "E1292", {"start": v(-14.46, 35.71) * mm, "end": v(-1.79, 23.04) * mm});
            skLineSegment(sketch, "E1293", {"start": v(-3.63, 17.83) * mm, "end": v(-2.42, 16.63) * mm});
            skLineSegment(sketch, "E1294", {"start": v(-2.42, 16.63) * mm, "end": v(1.82, 16.63) * mm});
            skLineSegment(sketch, "E1295", {"start": v(1.82, 16.63) * mm, "end": v(5.45, 13) * mm});
            skLineSegment(sketch, "E1296", {"start": v(5.45, 13) * mm, "end": v(5.45, 12.26) * mm});
            skLineSegment(sketch, "E1297", {"start": v(5.45, 12.26) * mm, "end": v(5.06, 11.86) * mm});
            skLineSegment(sketch, "E1298", {"start": v(-42.09, -17.53) * mm, "end": v(-42.09, -44.9) * mm});
            skLineSegment(sketch, "E1299", {"start": v(-42.09, -44.9) * mm, "end": v(-55.82, -58.64) * mm});
            skLineSegment(sketch, "E1300", {"start": v(-61.04, -58.64) * mm, "end": v(-61.23, -58.83) * mm});
            skLineSegment(sketch, "E1301", {"start": v(5.06, 11.86) * mm, "end": v(-6.53, 11.86) * mm});
            skLineSegment(sketch, "E1302", {"start": v(-6.53, 11.86) * mm, "end": v(-9.24, 14.58) * mm});
            skLineSegment(sketch, "E1303", {"start": v(-9.24, 14.58) * mm, "end": v(-9.97, 14.58) * mm});
            skLineSegment(sketch, "E1304", {"start": v(-9.97, 14.58) * mm, "end": v(-42.09, -17.53) * mm});
            skLineSegment(sketch, "E1305", {"start": v(-61.23, -58.83) * mm, "end": v(-62.1, -59.69) * mm});
            skLineSegment(sketch, "E1306", {"start": v(-55.82, -58.64) * mm, "end": v(-61.04, -58.64) * mm});
            skLineSegment(sketch, "E1307", {"start": v(45.94, 53.34) * mm, "end": v(44.8, 53.34) * mm});
            skLineSegment(sketch, "E1308", {"start": v(44.8, 53.34) * mm, "end": v(36.07, 62.08) * mm});
            skLineSegment(sketch, "E1309", {"start": v(36.07, 62.08) * mm, "end": v(-16.52, 62.08) * mm});
            skLineSegment(sketch, "E1310", {"start": v(-16.52, 62.08) * mm, "end": v(-16.78, 61.82) * mm});
            skLineSegment(sketch, "E1311", {"start": v(-16.78, 61.82) * mm, "end": v(-17.64, 60.96) * mm});
            skLineSegment(sketch, "E1312", {"start": v(20.59, -35.18) * mm, "end": v(53.13, -35.18) * mm});
            skLineSegment(sketch, "E1313", {"start": v(53.13, -35.18) * mm, "end": v(55.26, -33.05) * mm});
            skLineSegment(sketch, "E1314", {"start": v(55.26, -33.05) * mm, "end": v(55.26, -32) * mm});
            skLineSegment(sketch, "E1315", {"start": v(-59.49, 13.97) * mm, "end": v(-59.49, 13.96) * mm});
            skLineSegment(sketch, "E1316", {"start": v(-59.49, 13.96) * mm, "end": v(-59.51, 13.92) * mm});
            skLineSegment(sketch, "E1317", {"start": v(-59.51, 13.92) * mm, "end": v(-59.52, 13.92) * mm});
            skLineSegment(sketch, "E1318", {"start": v(-59.52, 13.92) * mm, "end": v(-59.52, 13.91) * mm});
            skLineSegment(sketch, "E1319", {"start": v(-59.52, 13.91) * mm, "end": v(-59.58, 13.91) * mm});
            skLineSegment(sketch, "E1320", {"start": v(-59.58, 13.91) * mm, "end": v(-59.58, 13.92) * mm});
            skLineSegment(sketch, "E1321", {"start": v(-59.58, 13.92) * mm, "end": v(-59.59, 13.92) * mm});
            skLineSegment(sketch, "E1322", {"start": v(-59.59, 13.92) * mm, "end": v(-59.61, 13.96) * mm});
            skLineSegment(sketch, "E1323", {"start": v(-59.61, 13.96) * mm, "end": v(-59.61, 13.97) * mm});
            skLineSegment(sketch, "E1324", {"start": v(-59.61, 13.97) * mm, "end": v(-59.61, 13.98) * mm});
            skLineSegment(sketch, "E1325", {"start": v(-59.61, 13.98) * mm, "end": v(-59.59, 14.02) * mm});
            skLineSegment(sketch, "E1326", {"start": v(-59.59, 14.02) * mm, "end": v(-59.58, 14.02) * mm});
            skLineSegment(sketch, "E1327", {"start": v(-59.58, 14.02) * mm, "end": v(-59.58, 14.03) * mm});
            skLineSegment(sketch, "E1328", {"start": v(-59.58, 14.03) * mm, "end": v(-59.52, 14.03) * mm});
            skLineSegment(sketch, "E1329", {"start": v(-59.52, 14.03) * mm, "end": v(-59.52, 14.02) * mm});
            skLineSegment(sketch, "E1330", {"start": v(-59.52, 14.02) * mm, "end": v(-59.51, 14.02) * mm});
            skLineSegment(sketch, "E1331", {"start": v(-59.51, 14.02) * mm, "end": v(-59.49, 13.98) * mm});
            skLineSegment(sketch, "E1332", {"start": v(-59.49, 13.98) * mm, "end": v(-59.49, 13.97) * mm});
            skLineSegment(sketch, "E1333", {"start": v(13.86, -41.91) * mm, "end": v(20.59, -35.18) * mm});
            skLineSegment(sketch, "E1334", {"start": v(-52.63, 30.02) * mm, "end": v(-52.63, 30) * mm});
            skLineSegment(sketch, "E1335", {"start": v(-52.63, 30) * mm, "end": v(-52.66, 29.97) * mm});
            skLineSegment(sketch, "E1336", {"start": v(-52.66, 29.97) * mm, "end": v(-52.66, 29.97) * mm});
            skLineSegment(sketch, "E1337", {"start": v(-52.66, 29.97) * mm, "end": v(-52.67, 29.97) * mm});
            skLineSegment(sketch, "E1338", {"start": v(-52.67, 29.97) * mm, "end": v(-52.72, 29.97) * mm});
            skLineSegment(sketch, "E1339", {"start": v(-52.72, 29.97) * mm, "end": v(-52.72, 29.97) * mm});
            skLineSegment(sketch, "E1340", {"start": v(-52.72, 29.97) * mm, "end": v(-52.73, 29.97) * mm});
            skLineSegment(sketch, "E1341", {"start": v(-52.73, 29.97) * mm, "end": v(-52.75, 30.01) * mm});
            skLineSegment(sketch, "E1342", {"start": v(-52.75, 30.01) * mm, "end": v(-52.75, 30.02) * mm});
            skLineSegment(sketch, "E1343", {"start": v(-52.75, 30.02) * mm, "end": v(-52.75, 30.04) * mm});
            skLineSegment(sketch, "E1344", {"start": v(-52.75, 30.04) * mm, "end": v(-52.73, 30.08) * mm});
            skLineSegment(sketch, "E1345", {"start": v(-52.73, 30.08) * mm, "end": v(-52.72, 30.08) * mm});
            skLineSegment(sketch, "E1346", {"start": v(-52.72, 30.08) * mm, "end": v(-52.72, 30.08) * mm});
            skLineSegment(sketch, "E1347", {"start": v(-52.72, 30.08) * mm, "end": v(-52.67, 30.08) * mm});
            skLineSegment(sketch, "E1348", {"start": v(-52.67, 30.08) * mm, "end": v(-52.66, 30.08) * mm});
            skLineSegment(sketch, "E1349", {"start": v(-52.66, 30.08) * mm, "end": v(-52.66, 30.08) * mm});
            skLineSegment(sketch, "E1350", {"start": v(-52.66, 30.08) * mm, "end": v(-52.63, 30.04) * mm});
            skLineSegment(sketch, "E1351", {"start": v(-52.63, 30.04) * mm, "end": v(-52.63, 30.02) * mm});
            skLineSegment(sketch, "E1352", {"start": v(-31.22, 49.2) * mm, "end": v(-31.22, 49.2) * mm});
            skLineSegment(sketch, "E1353", {"start": v(-31.22, 49.2) * mm, "end": v(-31.22, 49.19) * mm});
            skLineSegment(sketch, "E1354", {"start": v(-31.22, 49.19) * mm, "end": v(-31.22, 49.19) * mm});
            skLineSegment(sketch, "E1355", {"start": v(-31.22, 49.19) * mm, "end": v(-31.23, 49.19) * mm});
            skLineSegment(sketch, "E1356", {"start": v(-31.23, 49.19) * mm, "end": v(-31.24, 49.2) * mm});
            skLineSegment(sketch, "E1357", {"start": v(-31.24, 49.2) * mm, "end": v(-31.24, 49.2) * mm});
            skLineSegment(sketch, "E1358", {"start": v(-31.24, 49.2) * mm, "end": v(-31.24, 49.21) * mm});
            skLineSegment(sketch, "E1359", {"start": v(-31.24, 49.21) * mm, "end": v(-31.23, 49.21) * mm});
            skLineSegment(sketch, "E1360", {"start": v(-31.23, 49.21) * mm, "end": v(-31.23, 49.21) * mm});
            skLineSegment(sketch, "E1361", {"start": v(-31.23, 49.21) * mm, "end": v(-31.22, 49.21) * mm});
            skLineSegment(sketch, "E1362", {"start": v(-31.22, 49.21) * mm, "end": v(-31.22, 49.21) * mm});
            skLineSegment(sketch, "E1363", {"start": v(-31.22, 49.21) * mm, "end": v(-31.22, 49.2) * mm});
            skLineSegment(sketch, "E1364", {"start": v(-42.19, -49.66) * mm, "end": v(-42.19, -49.66) * mm});
            skLineSegment(sketch, "E1365", {"start": v(-42.19, -49.66) * mm, "end": v(-42.2, -49.67) * mm});
            skLineSegment(sketch, "E1366", {"start": v(-42.2, -49.67) * mm, "end": v(-42.2, -49.67) * mm});
            skLineSegment(sketch, "E1367", {"start": v(-42.2, -49.67) * mm, "end": v(-42.21, -49.66) * mm});
            skLineSegment(sketch, "E1368", {"start": v(-42.21, -49.66) * mm, "end": v(-42.21, -49.66) * mm});
            skLineSegment(sketch, "E1369", {"start": v(-42.21, -49.66) * mm, "end": v(-42.2, -49.65) * mm});
            skLineSegment(sketch, "E1370", {"start": v(-42.2, -49.65) * mm, "end": v(-42.2, -49.65) * mm});
            skLineSegment(sketch, "E1371", {"start": v(-42.2, -49.65) * mm, "end": v(-42.19, -49.66) * mm});
            skLineSegment(sketch, "E1372", {"start": v(-46.28, -45.72) * mm, "end": v(-46.28, -45.73) * mm});
            skLineSegment(sketch, "E1373", {"start": v(-46.28, -45.73) * mm, "end": v(-46.31, -45.77) * mm});
            skLineSegment(sketch, "E1374", {"start": v(-46.31, -45.77) * mm, "end": v(-46.32, -45.77) * mm});
            skLineSegment(sketch, "E1375", {"start": v(-46.32, -45.77) * mm, "end": v(-46.32, -45.77) * mm});
            skLineSegment(sketch, "E1376", {"start": v(-46.32, -45.77) * mm, "end": v(-46.37, -45.77) * mm});
            skLineSegment(sketch, "E1377", {"start": v(-46.37, -45.77) * mm, "end": v(-46.38, -45.77) * mm});
            skLineSegment(sketch, "E1378", {"start": v(-46.38, -45.77) * mm, "end": v(-46.38, -45.77) * mm});
            skLineSegment(sketch, "E1379", {"start": v(-46.38, -45.77) * mm, "end": v(-46.41, -45.73) * mm});
            skLineSegment(sketch, "E1380", {"start": v(-46.41, -45.73) * mm, "end": v(-46.41, -45.72) * mm});
            skLineSegment(sketch, "E1381", {"start": v(-46.41, -45.72) * mm, "end": v(-46.41, -45.7) * mm});
            skLineSegment(sketch, "E1382", {"start": v(-46.41, -45.7) * mm, "end": v(-46.38, -45.66) * mm});
            skLineSegment(sketch, "E1383", {"start": v(-46.38, -45.66) * mm, "end": v(-46.38, -45.66) * mm});
            skLineSegment(sketch, "E1384", {"start": v(-46.38, -45.66) * mm, "end": v(-46.37, -45.66) * mm});
            skLineSegment(sketch, "E1385", {"start": v(-46.37, -45.66) * mm, "end": v(-46.32, -45.66) * mm});
            skLineSegment(sketch, "E1386", {"start": v(-46.32, -45.66) * mm, "end": v(-46.32, -45.66) * mm});
            skLineSegment(sketch, "E1387", {"start": v(-46.32, -45.66) * mm, "end": v(-46.31, -45.66) * mm});
            skLineSegment(sketch, "E1388", {"start": v(-46.31, -45.66) * mm, "end": v(-46.28, -45.7) * mm});
            skLineSegment(sketch, "E1389", {"start": v(-46.28, -45.7) * mm, "end": v(-46.28, -45.72) * mm});
            skLineSegment(sketch, "E1390", {"start": v(16.49, 17.3) * mm, "end": v(16.49, 17.3) * mm});
            skLineSegment(sketch, "E1391", {"start": v(16.49, 17.3) * mm, "end": v(16.48, 17.29) * mm});
            skLineSegment(sketch, "E1392", {"start": v(16.48, 17.29) * mm, "end": v(16.48, 17.29) * mm});
            skLineSegment(sketch, "E1393", {"start": v(16.48, 17.29) * mm, "end": v(16.47, 17.29) * mm});
            skLineSegment(sketch, "E1394", {"start": v(16.47, 17.29) * mm, "end": v(16.47, 17.29) * mm});
            skLineSegment(sketch, "E1395", {"start": v(16.47, 17.29) * mm, "end": v(16.46, 17.3) * mm});
            skLineSegment(sketch, "E1396", {"start": v(16.46, 17.3) * mm, "end": v(16.46, 17.3) * mm});
            skLineSegment(sketch, "E1397", {"start": v(16.46, 17.3) * mm, "end": v(16.47, 17.3) * mm});
            skLineSegment(sketch, "E1398", {"start": v(16.47, 17.3) * mm, "end": v(16.47, 17.3) * mm});
            skLineSegment(sketch, "E1399", {"start": v(16.47, 17.3) * mm, "end": v(16.48, 17.3) * mm});
            skLineSegment(sketch, "E1400", {"start": v(16.48, 17.3) * mm, "end": v(16.48, 17.3) * mm});
            skLineSegment(sketch, "E1401", {"start": v(16.48, 17.3) * mm, "end": v(16.49, 17.3) * mm});
            skLineSegment(sketch, "E1402", {"start": v(15.25, -56.34) * mm, "end": v(15.25, -56.34) * mm});
            skLineSegment(sketch, "E1403", {"start": v(15.25, -56.34) * mm, "end": v(15.24, -56.35) * mm});
            skLineSegment(sketch, "E1404", {"start": v(15.24, -56.35) * mm, "end": v(15.24, -56.35) * mm});
            skLineSegment(sketch, "E1405", {"start": v(15.24, -56.35) * mm, "end": v(15.23, -56.35) * mm});
            skLineSegment(sketch, "E1406", {"start": v(15.23, -56.35) * mm, "end": v(15.23, -56.35) * mm});
            skLineSegment(sketch, "E1407", {"start": v(15.23, -56.35) * mm, "end": v(15.22, -56.34) * mm});
            skLineSegment(sketch, "E1408", {"start": v(15.22, -56.34) * mm, "end": v(15.22, -56.34) * mm});
            skLineSegment(sketch, "E1409", {"start": v(15.22, -56.34) * mm, "end": v(15.22, -56.33) * mm});
            skLineSegment(sketch, "E1410", {"start": v(15.22, -56.33) * mm, "end": v(15.23, -56.33) * mm});
            skLineSegment(sketch, "E1411", {"start": v(15.23, -56.33) * mm, "end": v(15.23, -56.33) * mm});
            skLineSegment(sketch, "E1412", {"start": v(15.23, -56.33) * mm, "end": v(15.23, -56.32) * mm});
            skLineSegment(sketch, "E1413", {"start": v(15.23, -56.32) * mm, "end": v(15.24, -56.32) * mm});
            skLineSegment(sketch, "E1414", {"start": v(15.24, -56.32) * mm, "end": v(15.24, -56.33) * mm});
            skLineSegment(sketch, "E1415", {"start": v(15.24, -56.33) * mm, "end": v(15.25, -56.33) * mm});
            skLineSegment(sketch, "E1416", {"start": v(15.25, -56.33) * mm, "end": v(15.25, -56.34) * mm});
            skLineSegment(sketch, "E1417", {"start": v(53.5, -34.3) * mm, "end": v(53.49, -34.3) * mm});
            skLineSegment(sketch, "E1418", {"start": v(53.49, -34.3) * mm, "end": v(53.49, -34.3) * mm});
            skLineSegment(sketch, "E1419", {"start": v(53.49, -34.3) * mm, "end": v(53.47, -34.3) * mm});
            skLineSegment(sketch, "E1420", {"start": v(53.47, -34.3) * mm, "end": v(53.47, -34.3) * mm});
            skLineSegment(sketch, "E1421", {"start": v(53.47, -34.3) * mm, "end": v(53.47, -34.29) * mm});
            skLineSegment(sketch, "E1422", {"start": v(53.47, -34.29) * mm, "end": v(53.47, -34.29) * mm});
            skLineSegment(sketch, "E1423", {"start": v(53.47, -34.29) * mm, "end": v(53.47, -34.28) * mm});
            skLineSegment(sketch, "E1424", {"start": v(53.47, -34.28) * mm, "end": v(53.47, -34.28) * mm});
            skLineSegment(sketch, "E1425", {"start": v(53.47, -34.28) * mm, "end": v(53.49, -34.28) * mm});
            skLineSegment(sketch, "E1426", {"start": v(53.49, -34.28) * mm, "end": v(53.49, -34.28) * mm});
            skLineSegment(sketch, "E1427", {"start": v(53.49, -34.28) * mm, "end": v(53.5, -34.29) * mm});
            skLineSegment(sketch, "E1428", {"start": v(53.5, -34.29) * mm, "end": v(53.5, -34.29) * mm});
            skLineSegment(sketch, "E1429", {"start": v(13.62, -40.39) * mm, "end": v(13.62, -40.39) * mm});
            skLineSegment(sketch, "E1430", {"start": v(13.62, -40.39) * mm, "end": v(13.6, -40.4) * mm});
            skLineSegment(sketch, "E1431", {"start": v(13.6, -40.4) * mm, "end": v(13.6, -40.4) * mm});
            skLineSegment(sketch, "E1432", {"start": v(13.6, -40.4) * mm, "end": v(13.59, -40.39) * mm});
            skLineSegment(sketch, "E1433", {"start": v(13.59, -40.39) * mm, "end": v(13.59, -40.39) * mm});
            skLineSegment(sketch, "E1434", {"start": v(13.59, -40.39) * mm, "end": v(13.59, -40.38) * mm});
            skLineSegment(sketch, "E1435", {"start": v(13.59, -40.38) * mm, "end": v(13.6, -40.38) * mm});
            skLineSegment(sketch, "E1436", {"start": v(13.6, -40.38) * mm, "end": v(13.6, -40.38) * mm});
            skLineSegment(sketch, "E1437", {"start": v(13.6, -40.38) * mm, "end": v(13.6, -40.37) * mm});
            skLineSegment(sketch, "E1438", {"start": v(13.6, -40.37) * mm, "end": v(13.6, -40.37) * mm});
            skLineSegment(sketch, "E1439", {"start": v(13.6, -40.37) * mm, "end": v(13.6, -40.38) * mm});
            skLineSegment(sketch, "E1440", {"start": v(13.6, -40.38) * mm, "end": v(13.62, -40.38) * mm});
            skLineSegment(sketch, "E1441", {"start": v(13.62, -40.38) * mm, "end": v(13.62, -40.39) * mm});
            skLineSegment(sketch, "E1442", {"start": v(-17.4, 35.33) * mm, "end": v(-17.4, 35.33) * mm});
            skLineSegment(sketch, "E1443", {"start": v(-17.4, 35.33) * mm, "end": v(-17.4, 35.32) * mm});
            skLineSegment(sketch, "E1444", {"start": v(-17.4, 35.32) * mm, "end": v(-17.4, 35.32) * mm});
            skLineSegment(sketch, "E1445", {"start": v(-17.4, 35.32) * mm, "end": v(-17.42, 35.32) * mm});
            skLineSegment(sketch, "E1446", {"start": v(-17.42, 35.32) * mm, "end": v(-17.42, 35.32) * mm});
            skLineSegment(sketch, "E1447", {"start": v(-17.42, 35.32) * mm, "end": v(-17.42, 35.33) * mm});
            skLineSegment(sketch, "E1448", {"start": v(-17.42, 35.33) * mm, "end": v(-17.42, 35.33) * mm});
            skLineSegment(sketch, "E1449", {"start": v(-17.42, 35.33) * mm, "end": v(-17.42, 35.34) * mm});
            skLineSegment(sketch, "E1450", {"start": v(-17.42, 35.34) * mm, "end": v(-17.42, 35.34) * mm});
            skLineSegment(sketch, "E1451", {"start": v(-17.42, 35.34) * mm, "end": v(-17.4, 35.34) * mm});
            skLineSegment(sketch, "E1452", {"start": v(-17.4, 35.34) * mm, "end": v(-17.4, 35.34) * mm});
            skLineSegment(sketch, "E1453", {"start": v(-17.4, 35.34) * mm, "end": v(-17.4, 35.33) * mm});
            skLineSegment(sketch, "E1454", {"start": v(-53.95, -17.27) * mm, "end": v(-53.95, -17.28) * mm});
            skLineSegment(sketch, "E1455", {"start": v(-53.95, -17.28) * mm, "end": v(-53.96, -17.28) * mm});
            skLineSegment(sketch, "E1456", {"start": v(-53.96, -17.28) * mm, "end": v(-53.96, -17.28) * mm});
            skLineSegment(sketch, "E1457", {"start": v(-53.96, -17.28) * mm, "end": v(-53.97, -17.28) * mm});
            skLineSegment(sketch, "E1458", {"start": v(-53.97, -17.28) * mm, "end": v(-53.97, -17.28) * mm});
            skLineSegment(sketch, "E1459", {"start": v(-53.97, -17.28) * mm, "end": v(-53.97, -17.27) * mm});
            skLineSegment(sketch, "E1460", {"start": v(-53.97, -17.27) * mm, "end": v(-53.97, -17.27) * mm});
            skLineSegment(sketch, "E1461", {"start": v(-53.97, -17.27) * mm, "end": v(-53.97, -17.26) * mm});
            skLineSegment(sketch, "E1462", {"start": v(-53.97, -17.26) * mm, "end": v(-53.97, -17.26) * mm});
            skLineSegment(sketch, "E1463", {"start": v(-53.97, -17.26) * mm, "end": v(-53.96, -17.26) * mm});
            skLineSegment(sketch, "E1464", {"start": v(-53.96, -17.26) * mm, "end": v(-53.96, -17.26) * mm});
            skLineSegment(sketch, "E1465", {"start": v(-53.96, -17.26) * mm, "end": v(-53.95, -17.27) * mm});
            skLineSegment(sketch, "E1466", {"start": v(-53.95, -17.27) * mm, "end": v(-53.95, -17.27) * mm});
            skLineSegment(sketch, "E1467", {"start": v(12.8, 20.7) * mm, "end": v(12.8, 20.7) * mm});
            skLineSegment(sketch, "E1468", {"start": v(12.8, 20.7) * mm, "end": v(12.8, 20.69) * mm});
            skLineSegment(sketch, "E1469", {"start": v(12.8, 20.69) * mm, "end": v(12.8, 20.69) * mm});
            skLineSegment(sketch, "E1470", {"start": v(12.8, 20.69) * mm, "end": v(12.78, 20.69) * mm});
            skLineSegment(sketch, "E1471", {"start": v(12.78, 20.69) * mm, "end": v(12.78, 20.7) * mm});
            skLineSegment(sketch, "E1472", {"start": v(12.78, 20.7) * mm, "end": v(12.78, 20.7) * mm});
            skLineSegment(sketch, "E1473", {"start": v(12.78, 20.7) * mm, "end": v(12.78, 20.71) * mm});
            skLineSegment(sketch, "E1474", {"start": v(12.78, 20.71) * mm, "end": v(12.78, 20.71) * mm});
            skLineSegment(sketch, "E1475", {"start": v(12.78, 20.71) * mm, "end": v(12.8, 20.71) * mm});
            skLineSegment(sketch, "E1476", {"start": v(12.8, 20.71) * mm, "end": v(12.8, 20.71) * mm});
            skLineSegment(sketch, "E1477", {"start": v(12.8, 20.71) * mm, "end": v(12.8, 20.7) * mm});
            skLineSegment(sketch, "E1478", {"start": v(-51.92, -23.62) * mm, "end": v(-51.92, -23.63) * mm});
            skLineSegment(sketch, "E1479", {"start": v(-51.92, -23.63) * mm, "end": v(-51.92, -23.63) * mm});
            skLineSegment(sketch, "E1480", {"start": v(-51.92, -23.63) * mm, "end": v(-51.94, -23.63) * mm});
            skLineSegment(sketch, "E1481", {"start": v(-51.94, -23.63) * mm, "end": v(-51.94, -23.63) * mm});
            skLineSegment(sketch, "E1482", {"start": v(-51.94, -23.63) * mm, "end": v(-51.94, -23.62) * mm});
            skLineSegment(sketch, "E1483", {"start": v(-51.94, -23.62) * mm, "end": v(-51.94, -23.62) * mm});
            skLineSegment(sketch, "E1484", {"start": v(-51.94, -23.62) * mm, "end": v(-51.94, -23.61) * mm});
            skLineSegment(sketch, "E1485", {"start": v(-51.94, -23.61) * mm, "end": v(-51.94, -23.61) * mm});
            skLineSegment(sketch, "E1486", {"start": v(-51.94, -23.61) * mm, "end": v(-51.92, -23.61) * mm});
            skLineSegment(sketch, "E1487", {"start": v(-51.92, -23.61) * mm, "end": v(-51.92, -23.61) * mm});
            skLineSegment(sketch, "E1488", {"start": v(-51.92, -23.61) * mm, "end": v(-51.92, -23.62) * mm});
            skLineSegment(sketch, "E1489", {"start": v(-51.92, -23.62) * mm, "end": v(-51.92, -23.62) * mm});
            skLineSegment(sketch, "E1490", {"start": v(-16.2, 33.14) * mm, "end": v(-16.21, 33.13) * mm});
            skLineSegment(sketch, "E1491", {"start": v(-16.21, 33.13) * mm, "end": v(-16.21, 33.13) * mm});
            skLineSegment(sketch, "E1492", {"start": v(-16.21, 33.13) * mm, "end": v(-16.22, 33.13) * mm});
            skLineSegment(sketch, "E1493", {"start": v(-16.22, 33.13) * mm, "end": v(-16.22, 33.13) * mm});
            skLineSegment(sketch, "E1494", {"start": v(-16.22, 33.13) * mm, "end": v(-16.23, 33.14) * mm});
            skLineSegment(sketch, "E1495", {"start": v(-16.23, 33.14) * mm, "end": v(-16.23, 33.14) * mm});
            skLineSegment(sketch, "E1496", {"start": v(-16.23, 33.14) * mm, "end": v(-16.22, 33.15) * mm});
            skLineSegment(sketch, "E1497", {"start": v(-16.22, 33.15) * mm, "end": v(-16.22, 33.15) * mm});
            skLineSegment(sketch, "E1498", {"start": v(-16.22, 33.15) * mm, "end": v(-16.21, 33.15) * mm});
            skLineSegment(sketch, "E1499", {"start": v(-16.21, 33.15) * mm, "end": v(-16.21, 33.15) * mm});
            skLineSegment(sketch, "E1500", {"start": v(-16.21, 33.15) * mm, "end": v(-16.2, 33.14) * mm});
            skLineSegment(sketch, "E1501", {"start": v(-31.65, 32.36) * mm, "end": v(-31.65, 32.36) * mm});
            skLineSegment(sketch, "E1502", {"start": v(-31.65, 32.36) * mm, "end": v(-31.65, 32.35) * mm});
            skLineSegment(sketch, "E1503", {"start": v(-31.65, 32.35) * mm, "end": v(-31.65, 32.35) * mm});
            skLineSegment(sketch, "E1504", {"start": v(-31.65, 32.35) * mm, "end": v(-31.66, 32.35) * mm});
            skLineSegment(sketch, "E1505", {"start": v(-31.66, 32.35) * mm, "end": v(-31.67, 32.35) * mm});
            skLineSegment(sketch, "E1506", {"start": v(-31.67, 32.35) * mm, "end": v(-31.67, 32.35) * mm});
            skLineSegment(sketch, "E1507", {"start": v(-31.67, 32.35) * mm, "end": v(-31.67, 32.36) * mm});
            skLineSegment(sketch, "E1508", {"start": v(-31.67, 32.36) * mm, "end": v(-31.67, 32.36) * mm});
            skLineSegment(sketch, "E1509", {"start": v(-31.67, 32.36) * mm, "end": v(-31.67, 32.37) * mm});
            skLineSegment(sketch, "E1510", {"start": v(-31.67, 32.37) * mm, "end": v(-31.67, 32.37) * mm});
            skLineSegment(sketch, "E1511", {"start": v(-31.67, 32.37) * mm, "end": v(-31.66, 32.37) * mm});
            skLineSegment(sketch, "E1512", {"start": v(-31.66, 32.37) * mm, "end": v(-31.65, 32.37) * mm});
            skLineSegment(sketch, "E1513", {"start": v(-31.65, 32.37) * mm, "end": v(-31.65, 32.36) * mm});
            skLineSegment(sketch, "E1514", {"start": v(-1.77, 23.04) * mm, "end": v(-1.77, 23.04) * mm});
            skLineSegment(sketch, "E1515", {"start": v(-1.77, 23.04) * mm, "end": v(-1.78, 23.03) * mm});
            skLineSegment(sketch, "E1516", {"start": v(-1.78, 23.03) * mm, "end": v(-1.78, 23.03) * mm});
            skLineSegment(sketch, "E1517", {"start": v(-1.78, 23.03) * mm, "end": v(-1.8, 23.03) * mm});
            skLineSegment(sketch, "E1518", {"start": v(-1.8, 23.03) * mm, "end": v(-1.8, 23.03) * mm});
            skLineSegment(sketch, "E1519", {"start": v(-1.8, 23.04) * mm, "end": v(-1.8, 23.05) * mm});
            skLineSegment(sketch, "E1520", {"start": v(-1.8, 23.05) * mm, "end": v(-1.8, 23.05) * mm});
            skLineSegment(sketch, "E1521", {"start": v(-1.8, 23.05) * mm, "end": v(-1.78, 23.05) * mm});
            skLineSegment(sketch, "E1522", {"start": v(-1.78, 23.05) * mm, "end": v(-1.78, 23.05) * mm});
            skLineSegment(sketch, "E1523", {"start": v(-1.78, 23.05) * mm, "end": v(-1.77, 23.04) * mm});
            skLineSegment(sketch, "E1524", {"start": v(-31.75, 34.57) * mm, "end": v(-31.75, 34.57) * mm});
            skLineSegment(sketch, "E1525", {"start": v(-31.75, 34.57) * mm, "end": v(-31.75, 34.56) * mm});
            skLineSegment(sketch, "E1526", {"start": v(-31.75, 34.56) * mm, "end": v(-31.75, 34.56) * mm});
            skLineSegment(sketch, "E1527", {"start": v(-31.75, 34.56) * mm, "end": v(-31.76, 34.56) * mm});
            skLineSegment(sketch, "E1528", {"start": v(-31.76, 34.56) * mm, "end": v(-31.77, 34.56) * mm});
            skLineSegment(sketch, "E1529", {"start": v(-31.77, 34.56) * mm, "end": v(-31.77, 34.56) * mm});
            skLineSegment(sketch, "E1530", {"start": v(-31.77, 34.56) * mm, "end": v(-31.77, 34.57) * mm});
            skLineSegment(sketch, "E1531", {"start": v(-31.77, 34.57) * mm, "end": v(-31.77, 34.57) * mm});
            skLineSegment(sketch, "E1532", {"start": v(-31.77, 34.57) * mm, "end": v(-31.77, 34.58) * mm});
            skLineSegment(sketch, "E1533", {"start": v(-31.77, 34.58) * mm, "end": v(-31.77, 34.58) * mm});
            skLineSegment(sketch, "E1534", {"start": v(-31.77, 34.58) * mm, "end": v(-31.76, 34.58) * mm});
            skLineSegment(sketch, "E1535", {"start": v(-31.76, 34.58) * mm, "end": v(-31.75, 34.58) * mm});
            skLineSegment(sketch, "E1536", {"start": v(-31.75, 34.58) * mm, "end": v(-31.75, 34.57) * mm});
            skLineSegment(sketch, "E1537", {"start": v(55.27, -32) * mm, "end": v(55.27, -32) * mm});
            skLineSegment(sketch, "E1538", {"start": v(55.27, -32) * mm, "end": v(55.27, -32.01) * mm});
            skLineSegment(sketch, "E1539", {"start": v(55.27, -32.01) * mm, "end": v(55.27, -32.01) * mm});
            skLineSegment(sketch, "E1540", {"start": v(55.27, -32.01) * mm, "end": v(55.26, -32.01) * mm});
            skLineSegment(sketch, "E1541", {"start": v(55.26, -32.01) * mm, "end": v(55.25, -32.01) * mm});
            skLineSegment(sketch, "E1542", {"start": v(55.25, -32.01) * mm, "end": v(55.25, -32.01) * mm});
            skLineSegment(sketch, "E1543", {"start": v(55.25, -32.01) * mm, "end": v(55.25, -32) * mm});
            skLineSegment(sketch, "E1544", {"start": v(55.25, -32) * mm, "end": v(55.25, -32) * mm});
            skLineSegment(sketch, "E1545", {"start": v(55.25, -32) * mm, "end": v(55.26, -32) * mm});
            skLineSegment(sketch, "E1546", {"start": v(55.26, -32) * mm, "end": v(55.27, -32) * mm});
            skLineSegment(sketch, "E1547", {"start": v(13.87, -41.91) * mm, "end": v(13.87, -41.91) * mm});
            skLineSegment(sketch, "E1548", {"start": v(13.87, -41.91) * mm, "end": v(13.86, -41.92) * mm});
            skLineSegment(sketch, "E1549", {"start": v(13.86, -41.92) * mm, "end": v(13.86, -41.92) * mm});
            skLineSegment(sketch, "E1550", {"start": v(13.86, -41.92) * mm, "end": v(13.85, -41.92) * mm});
            skLineSegment(sketch, "E1551", {"start": v(13.85, -41.92) * mm, "end": v(13.85, -41.92) * mm});
            skLineSegment(sketch, "E1552", {"start": v(13.85, -41.92) * mm, "end": v(13.84, -41.91) * mm});
            skLineSegment(sketch, "E1553", {"start": v(13.84, -41.91) * mm, "end": v(13.84, -41.91) * mm});
            skLineSegment(sketch, "E1554", {"start": v(13.84, -41.91) * mm, "end": v(13.84, -41.9) * mm});
            skLineSegment(sketch, "E1555", {"start": v(13.84, -41.9) * mm, "end": v(13.85, -41.9) * mm});
            skLineSegment(sketch, "E1556", {"start": v(13.85, -41.9) * mm, "end": v(13.85, -41.9) * mm});
            skLineSegment(sketch, "E1557", {"start": v(13.85, -41.9) * mm, "end": v(13.86, -41.9) * mm});
            skLineSegment(sketch, "E1558", {"start": v(13.86, -41.9) * mm, "end": v(13.86, -41.9) * mm});
            skLineSegment(sketch, "E1559", {"start": v(13.86, -41.9) * mm, "end": v(13.87, -41.9) * mm});
            skLineSegment(sketch, "E1560", {"start": v(13.87, -41.9) * mm, "end": v(13.87, -41.91) * mm});
            skLineSegment(sketch, "E1561", {"start": v(-24.67, 20.57) * mm, "end": v(-24.67, 20.47) * mm});
            skLineSegment(sketch, "E1562", {"start": v(-24.67, 20.47) * mm, "end": v(-24.9, 20.16) * mm});
            skLineSegment(sketch, "E1563", {"start": v(-24.9, 20.16) * mm, "end": v(-24.93, 20.13) * mm});
            skLineSegment(sketch, "E1564", {"start": v(-24.93, 20.13) * mm, "end": v(-24.97, 20.11) * mm});
            skLineSegment(sketch, "E1565", {"start": v(-24.97, 20.11) * mm, "end": v(-25.4, 20.11) * mm});
            skLineSegment(sketch, "E1566", {"start": v(-25.4, 20.11) * mm, "end": v(-25.44, 20.13) * mm});
            skLineSegment(sketch, "E1567", {"start": v(-25.44, 20.13) * mm, "end": v(-25.48, 20.16) * mm});
            skLineSegment(sketch, "E1568", {"start": v(-25.48, 20.16) * mm, "end": v(-25.7, 20.47) * mm});
            skLineSegment(sketch, "E1569", {"start": v(-25.7, 20.47) * mm, "end": v(-25.7, 20.57) * mm});
            skLineSegment(sketch, "E1570", {"start": v(-25.7, 20.57) * mm, "end": v(-25.7, 20.68) * mm});
            skLineSegment(sketch, "E1571", {"start": v(-25.7, 20.68) * mm, "end": v(-25.48, 21) * mm});
            skLineSegment(sketch, "E1572", {"start": v(-25.48, 21) * mm, "end": v(-25.44, 21.01) * mm});
            skLineSegment(sketch, "E1573", {"start": v(-25.44, 21.01) * mm, "end": v(-25.4, 21.04) * mm});
            skLineSegment(sketch, "E1574", {"start": v(-25.4, 21.04) * mm, "end": v(-24.97, 21.04) * mm});
            skLineSegment(sketch, "E1575", {"start": v(-24.97, 21.04) * mm, "end": v(-24.93, 21.01) * mm});
            skLineSegment(sketch, "E1576", {"start": v(-24.93, 21.01) * mm, "end": v(-24.9, 21) * mm});
            skLineSegment(sketch, "E1577", {"start": v(-24.9, 21) * mm, "end": v(-24.67, 20.68) * mm});
            skLineSegment(sketch, "E1578", {"start": v(-24.67, 20.68) * mm, "end": v(-24.67, 20.57) * mm});
            skLineSegment(sketch, "E1579", {"start": v(-9.23, 13.82) * mm, "end": v(-9.23, 13.74) * mm});
            skLineSegment(sketch, "E1580", {"start": v(-9.23, 13.74) * mm, "end": v(-9.39, 13.5) * mm});
            skLineSegment(sketch, "E1581", {"start": v(-9.39, 13.5) * mm, "end": v(-9.42, 13.49) * mm});
            skLineSegment(sketch, "E1582", {"start": v(-9.42, 13.49) * mm, "end": v(-9.45, 13.47) * mm});
            skLineSegment(sketch, "E1583", {"start": v(-9.45, 13.47) * mm, "end": v(-9.77, 13.47) * mm});
            skLineSegment(sketch, "E1584", {"start": v(-9.77, 13.47) * mm, "end": v(-9.8, 13.49) * mm});
            skLineSegment(sketch, "E1585", {"start": v(-9.8, 13.49) * mm, "end": v(-9.83, 13.5) * mm});
            skLineSegment(sketch, "E1586", {"start": v(-9.83, 13.5) * mm, "end": v(-10, 13.74) * mm});
            skLineSegment(sketch, "E1587", {"start": v(-10, 13.74) * mm, "end": v(-10, 13.82) * mm});
            skLineSegment(sketch, "E1588", {"start": v(-10, 13.82) * mm, "end": v(-10, 13.9) * mm});
            skLineSegment(sketch, "E1589", {"start": v(-10, 13.9) * mm, "end": v(-9.83, 14.13) * mm});
            skLineSegment(sketch, "E1590", {"start": v(-9.83, 14.13) * mm, "end": v(-9.8, 14.15) * mm});
            skLineSegment(sketch, "E1591", {"start": v(-9.8, 14.15) * mm, "end": v(-9.77, 14.17) * mm});
            skLineSegment(sketch, "E1592", {"start": v(-9.77, 14.17) * mm, "end": v(-9.45, 14.17) * mm});
            skLineSegment(sketch, "E1593", {"start": v(-9.45, 14.17) * mm, "end": v(-9.42, 14.15) * mm});
            skLineSegment(sketch, "E1594", {"start": v(-9.42, 14.15) * mm, "end": v(-9.39, 14.13) * mm});
            skLineSegment(sketch, "E1595", {"start": v(-9.39, 14.13) * mm, "end": v(-9.23, 13.9) * mm});
            skLineSegment(sketch, "E1596", {"start": v(-9.23, 13.9) * mm, "end": v(-9.23, 13.82) * mm});
            skLineSegment(sketch, "E1597", {"start": v(-52.56, -1.27) * mm, "end": v(-52.56, -1.4) * mm});
            skLineSegment(sketch, "E1598", {"start": v(-52.56, -1.4) * mm, "end": v(-52.7, -1.77) * mm});
            skLineSegment(sketch, "E1599", {"start": v(-52.7, -1.77) * mm, "end": v(-52.98, -2.1) * mm});
            skLineSegment(sketch, "E1600", {"start": v(-52.98, -2.1) * mm, "end": v(-53.06, -2.14) * mm});
            skLineSegment(sketch, "E1601", {"start": v(-53.06, -2.14) * mm, "end": v(-53.14, -2.18) * mm});
            skLineSegment(sketch, "E1602", {"start": v(-53.14, -2.18) * mm, "end": v(-53.56, -2.27) * mm});
            skLineSegment(sketch, "E1603", {"start": v(-53.56, -2.27) * mm, "end": v(-53.98, -2.18) * mm});
            skLineSegment(sketch, "E1604", {"start": v(-53.98, -2.18) * mm, "end": v(-54.06, -2.14) * mm});
            skLineSegment(sketch, "E1605", {"start": v(-54.06, -2.14) * mm, "end": v(-54.14, -2.1) * mm});
            skLineSegment(sketch, "E1606", {"start": v(-54.14, -2.1) * mm, "end": v(-54.42, -1.77) * mm});
            skLineSegment(sketch, "E1607", {"start": v(-54.42, -1.77) * mm, "end": v(-54.56, -1.4) * mm});
            skLineSegment(sketch, "E1608", {"start": v(-54.56, -1.4) * mm, "end": v(-54.56, -1.27) * mm});
            skLineSegment(sketch, "E1609", {"start": v(-54.56, -1.27) * mm, "end": v(-54.56, -1.15) * mm});
            skLineSegment(sketch, "E1610", {"start": v(-54.56, -1.15) * mm, "end": v(-54.42, -0.77) * mm});
            skLineSegment(sketch, "E1611", {"start": v(-54.42, -0.77) * mm, "end": v(-54.14, -0.45) * mm});
            skLineSegment(sketch, "E1612", {"start": v(-54.14, -0.45) * mm, "end": v(-54.06, -0.4) * mm});
            skLineSegment(sketch, "E1613", {"start": v(-54.06, -0.4) * mm, "end": v(-53.98, -0.36) * mm});
            skLineSegment(sketch, "E1614", {"start": v(-53.98, -0.36) * mm, "end": v(-53.56, -0.27) * mm});
            skLineSegment(sketch, "E1615", {"start": v(-53.56, -0.27) * mm, "end": v(-53.14, -0.36) * mm});
            skLineSegment(sketch, "E1616", {"start": v(-53.14, -0.36) * mm, "end": v(-53.06, -0.4) * mm});
            skLineSegment(sketch, "E1617", {"start": v(-53.06, -0.4) * mm, "end": v(-52.98, -0.45) * mm});
            skLineSegment(sketch, "E1618", {"start": v(-52.98, -0.45) * mm, "end": v(-52.7, -0.77) * mm});
            skLineSegment(sketch, "E1619", {"start": v(-52.7, -0.77) * mm, "end": v(-52.56, -1.15) * mm});
            skLineSegment(sketch, "E1620", {"start": v(-52.56, -1.15) * mm, "end": v(-52.56, -1.27) * mm});
            skLineSegment(sketch, "E1621", {"start": v(-52.56, -9.17) * mm, "end": v(-52.56, -9.3) * mm});
            skLineSegment(sketch, "E1622", {"start": v(-52.56, -9.3) * mm, "end": v(-52.7, -9.67) * mm});
            skLineSegment(sketch, "E1623", {"start": v(-52.7, -9.67) * mm, "end": v(-52.98, -10) * mm});
            skLineSegment(sketch, "E1624", {"start": v(-52.98, -10) * mm, "end": v(-53.06, -10.04) * mm});
            skLineSegment(sketch, "E1625", {"start": v(-53.06, -10.04) * mm, "end": v(-53.14, -10.08) * mm});
            skLineSegment(sketch, "E1626", {"start": v(-53.14, -10.08) * mm, "end": v(-53.56, -10.17) * mm});
            skLineSegment(sketch, "E1627", {"start": v(-53.56, -10.17) * mm, "end": v(-53.98, -10.08) * mm});
            skLineSegment(sketch, "E1628", {"start": v(-53.98, -10.08) * mm, "end": v(-54.06, -10.04) * mm});
            skLineSegment(sketch, "E1629", {"start": v(-54.06, -10.04) * mm, "end": v(-54.14, -10) * mm});
            skLineSegment(sketch, "E1630", {"start": v(-54.14, -10) * mm, "end": v(-54.42, -9.67) * mm});
            skLineSegment(sketch, "E1631", {"start": v(-54.42, -9.67) * mm, "end": v(-54.56, -9.3) * mm});
            skLineSegment(sketch, "E1632", {"start": v(-54.56, -9.3) * mm, "end": v(-54.56, -9.17) * mm});
            skLineSegment(sketch, "E1633", {"start": v(-54.56, -9.17) * mm, "end": v(-54.56, -9.04) * mm});
            skLineSegment(sketch, "E1634", {"start": v(-54.56, -9.04) * mm, "end": v(-54.42, -8.67) * mm});
            skLineSegment(sketch, "E1635", {"start": v(-54.42, -8.67) * mm, "end": v(-54.14, -8.35) * mm});
            skLineSegment(sketch, "E1636", {"start": v(-54.14, -8.35) * mm, "end": v(-54.06, -8.3) * mm});
            skLineSegment(sketch, "E1637", {"start": v(-54.06, -8.3) * mm, "end": v(-53.98, -8.26) * mm});
            skLineSegment(sketch, "E1638", {"start": v(-53.98, -8.26) * mm, "end": v(-53.56, -8.17) * mm});
            skLineSegment(sketch, "E1639", {"start": v(-53.56, -8.17) * mm, "end": v(-53.14, -8.26) * mm});
            skLineSegment(sketch, "E1640", {"start": v(-53.14, -8.26) * mm, "end": v(-53.06, -8.3) * mm});
            skLineSegment(sketch, "E1641", {"start": v(-53.06, -8.3) * mm, "end": v(-52.98, -8.35) * mm});
            skLineSegment(sketch, "E1642", {"start": v(-52.98, -8.35) * mm, "end": v(-52.7, -8.67) * mm});
            skLineSegment(sketch, "E1643", {"start": v(-52.7, -8.67) * mm, "end": v(-52.56, -9.04) * mm});
            skLineSegment(sketch, "E1644", {"start": v(-52.56, -9.04) * mm, "end": v(-52.56, -9.17) * mm});
            skLineSegment(sketch, "E1645", {"start": v(-41.28, 57.1) * mm, "end": v(-41.28, 56.79) * mm});
            skLineSegment(sketch, "E1646", {"start": v(-41.28, 56.79) * mm, "end": v(-41.61, 55.85) * mm});
            skLineSegment(sketch, "E1647", {"start": v(-41.61, 55.85) * mm, "end": v(-42.33, 55.05) * mm});
            skLineSegment(sketch, "E1648", {"start": v(-42.33, 55.05) * mm, "end": v(-42.53, 54.94) * mm});
            skLineSegment(sketch, "E1649", {"start": v(-42.53, 54.94) * mm, "end": v(-42.72, 54.82) * mm});
            skLineSegment(sketch, "E1650", {"start": v(-42.72, 54.82) * mm, "end": v(-43.78, 54.6) * mm});
            skLineSegment(sketch, "E1651", {"start": v(-43.78, 54.6) * mm, "end": v(-44.83, 54.82) * mm});
            skLineSegment(sketch, "E1652", {"start": v(-44.83, 54.82) * mm, "end": v(-45.03, 54.94) * mm});
            skLineSegment(sketch, "E1653", {"start": v(-45.03, 54.94) * mm, "end": v(-45.22, 55.05) * mm});
            skLineSegment(sketch, "E1654", {"start": v(-45.22, 55.05) * mm, "end": v(-45.94, 55.85) * mm});
            skLineSegment(sketch, "E1655", {"start": v(-45.94, 55.85) * mm, "end": v(-46.28, 56.79) * mm});
            skLineSegment(sketch, "E1656", {"start": v(-46.28, 56.79) * mm, "end": v(-46.28, 57.1) * mm});
            skLineSegment(sketch, "E1657", {"start": v(-46.28, 57.1) * mm, "end": v(-46.28, 57.41) * mm});
            skLineSegment(sketch, "E1658", {"start": v(-46.28, 57.41) * mm, "end": v(-45.94, 58.35) * mm});
            skLineSegment(sketch, "E1659", {"start": v(-45.94, 58.35) * mm, "end": v(-45.22, 59.15) * mm});
            skLineSegment(sketch, "E1660", {"start": v(-45.22, 59.15) * mm, "end": v(-45.03, 59.27) * mm});
            skLineSegment(sketch, "E1661", {"start": v(-45.03, 59.27) * mm, "end": v(-44.83, 59.38) * mm});
            skLineSegment(sketch, "E1662", {"start": v(-44.83, 59.38) * mm, "end": v(-43.78, 59.6) * mm});
            skLineSegment(sketch, "E1663", {"start": v(-43.78, 59.6) * mm, "end": v(-42.72, 59.38) * mm});
            skLineSegment(sketch, "E1664", {"start": v(-42.72, 59.38) * mm, "end": v(-42.53, 59.27) * mm});
            skLineSegment(sketch, "E1665", {"start": v(-42.53, 59.27) * mm, "end": v(-42.33, 59.15) * mm});
            skLineSegment(sketch, "E1666", {"start": v(-42.33, 59.15) * mm, "end": v(-41.61, 58.35) * mm});
            skLineSegment(sketch, "E1667", {"start": v(-41.61, 58.35) * mm, "end": v(-41.28, 57.41) * mm});
            skLineSegment(sketch, "E1668", {"start": v(-41.28, 57.41) * mm, "end": v(-41.28, 57.1) * mm});
            skLineSegment(sketch, "E1669", {"start": v(-41.28, 38.1) * mm, "end": v(-41.28, 37.79) * mm});
            skLineSegment(sketch, "E1670", {"start": v(-41.28, 37.79) * mm, "end": v(-41.61, 36.85) * mm});
            skLineSegment(sketch, "E1671", {"start": v(-41.61, 36.85) * mm, "end": v(-42.33, 36.05) * mm});
            skLineSegment(sketch, "E1672", {"start": v(-42.33, 36.05) * mm, "end": v(-42.53, 35.93) * mm});
            skLineSegment(sketch, "E1673", {"start": v(-42.53, 35.93) * mm, "end": v(-42.72, 35.82) * mm});
            skLineSegment(sketch, "E1674", {"start": v(-42.72, 35.82) * mm, "end": v(-43.78, 35.6) * mm});
            skLineSegment(sketch, "E1675", {"start": v(-43.78, 35.6) * mm, "end": v(-44.83, 35.82) * mm});
            skLineSegment(sketch, "E1676", {"start": v(-44.83, 35.82) * mm, "end": v(-45.03, 35.93) * mm});
            skLineSegment(sketch, "E1677", {"start": v(-45.03, 35.93) * mm, "end": v(-45.22, 36.05) * mm});
            skLineSegment(sketch, "E1678", {"start": v(-45.22, 36.05) * mm, "end": v(-45.94, 36.85) * mm});
            skLineSegment(sketch, "E1679", {"start": v(-45.94, 36.85) * mm, "end": v(-46.28, 37.79) * mm});
            skLineSegment(sketch, "E1680", {"start": v(-46.28, 37.79) * mm, "end": v(-46.28, 38.1) * mm});
            skLineSegment(sketch, "E1681", {"start": v(-46.28, 38.1) * mm, "end": v(-46.28, 38.41) * mm});
            skLineSegment(sketch, "E1682", {"start": v(-46.28, 38.41) * mm, "end": v(-45.94, 39.35) * mm});
            skLineSegment(sketch, "E1683", {"start": v(-45.94, 39.35) * mm, "end": v(-45.22, 40.15) * mm});
            skLineSegment(sketch, "E1684", {"start": v(-45.22, 40.15) * mm, "end": v(-45.03, 40.26) * mm});
            skLineSegment(sketch, "E1685", {"start": v(-45.03, 40.26) * mm, "end": v(-44.83, 40.38) * mm});
            skLineSegment(sketch, "E1686", {"start": v(-44.83, 40.38) * mm, "end": v(-43.78, 40.6) * mm});
            skLineSegment(sketch, "E1687", {"start": v(-43.78, 40.6) * mm, "end": v(-42.72, 40.38) * mm});
            skLineSegment(sketch, "E1688", {"start": v(-42.72, 40.38) * mm, "end": v(-42.53, 40.26) * mm});
            skLineSegment(sketch, "E1689", {"start": v(-42.53, 40.26) * mm, "end": v(-42.33, 40.15) * mm});
            skLineSegment(sketch, "E1690", {"start": v(-42.33, 40.15) * mm, "end": v(-41.61, 39.35) * mm});
            skLineSegment(sketch, "E1691", {"start": v(-41.61, 39.35) * mm, "end": v(-41.28, 38.41) * mm});
            skLineSegment(sketch, "E1692", {"start": v(-41.28, 38.41) * mm, "end": v(-41.28, 38.1) * mm});
            skLineSegment(sketch, "E1693", {"start": v(-27.3, 58.42) * mm, "end": v(-27.3, 58.31) * mm});
            skLineSegment(sketch, "E1694", {"start": v(-27.3, 58.31) * mm, "end": v(-27.5, 58) * mm});
            skLineSegment(sketch, "E1695", {"start": v(-27.5, 58) * mm, "end": v(-27.55, 57.98) * mm});
            skLineSegment(sketch, "E1696", {"start": v(-27.55, 57.98) * mm, "end": v(-27.59, 57.96) * mm});
            skLineSegment(sketch, "E1697", {"start": v(-27.59, 57.96) * mm, "end": v(-28.02, 57.96) * mm});
            skLineSegment(sketch, "E1698", {"start": v(-28.02, 57.96) * mm, "end": v(-28.05, 57.98) * mm});
            skLineSegment(sketch, "E1699", {"start": v(-28.05, 57.98) * mm, "end": v(-28.1, 58) * mm});
            skLineSegment(sketch, "E1700", {"start": v(-28.1, 58) * mm, "end": v(-28.3, 58.32) * mm});
            skLineSegment(sketch, "E1701", {"start": v(-28.3, 58.32) * mm, "end": v(-28.3, 58.42) * mm});
            skLineSegment(sketch, "E1702", {"start": v(-28.3, 58.42) * mm, "end": v(-28.3, 58.53) * mm});
            skLineSegment(sketch, "E1703", {"start": v(-28.3, 58.53) * mm, "end": v(-28.1, 58.84) * mm});
            skLineSegment(sketch, "E1704", {"start": v(-28.1, 58.84) * mm, "end": v(-28.05, 58.86) * mm});
            skLineSegment(sketch, "E1705", {"start": v(-28.05, 58.86) * mm, "end": v(-28.02, 58.88) * mm});
            skLineSegment(sketch, "E1706", {"start": v(-28.02, 58.88) * mm, "end": v(-27.59, 58.88) * mm});
            skLineSegment(sketch, "E1707", {"start": v(-27.59, 58.88) * mm, "end": v(-27.55, 58.86) * mm});
            skLineSegment(sketch, "E1708", {"start": v(-27.55, 58.86) * mm, "end": v(-27.5, 58.84) * mm});
            skLineSegment(sketch, "E1709", {"start": v(-27.5, 58.84) * mm, "end": v(-27.3, 58.53) * mm});
            skLineSegment(sketch, "E1710", {"start": v(-27.3, 58.53) * mm, "end": v(-27.3, 58.42) * mm});
            skLineSegment(sketch, "E1711", {"start": v(-27.3, 60.96) * mm, "end": v(-27.3, 60.85) * mm});
            skLineSegment(sketch, "E1712", {"start": v(-27.3, 60.85) * mm, "end": v(-27.5, 60.54) * mm});
            skLineSegment(sketch, "E1713", {"start": v(-27.5, 60.54) * mm, "end": v(-27.55, 60.52) * mm});
            skLineSegment(sketch, "E1714", {"start": v(-27.55, 60.52) * mm, "end": v(-27.59, 60.5) * mm});
            skLineSegment(sketch, "E1715", {"start": v(-27.59, 60.5) * mm, "end": v(-28.02, 60.5) * mm});
            skLineSegment(sketch, "E1716", {"start": v(-28.02, 60.5) * mm, "end": v(-28.05, 60.52) * mm});
            skLineSegment(sketch, "E1717", {"start": v(-28.05, 60.52) * mm, "end": v(-28.1, 60.54) * mm});
            skLineSegment(sketch, "E1718", {"start": v(-28.1, 60.54) * mm, "end": v(-28.3, 60.86) * mm});
            skLineSegment(sketch, "E1719", {"start": v(-28.3, 60.86) * mm, "end": v(-28.3, 60.96) * mm});
            skLineSegment(sketch, "E1720", {"start": v(-28.3, 60.96) * mm, "end": v(-28.3, 61.07) * mm});
            skLineSegment(sketch, "E1721", {"start": v(-28.3, 61.07) * mm, "end": v(-28.1, 61.38) * mm});
            skLineSegment(sketch, "E1722", {"start": v(-28.1, 61.38) * mm, "end": v(-28.05, 61.4) * mm});
            skLineSegment(sketch, "E1723", {"start": v(-28.05, 61.4) * mm, "end": v(-28.02, 61.42) * mm});
            skLineSegment(sketch, "E1724", {"start": v(-28.02, 61.42) * mm, "end": v(-27.59, 61.42) * mm});
            skLineSegment(sketch, "E1725", {"start": v(-27.59, 61.42) * mm, "end": v(-27.55, 61.4) * mm});
            skLineSegment(sketch, "E1726", {"start": v(-27.55, 61.4) * mm, "end": v(-27.5, 61.38) * mm});
            skLineSegment(sketch, "E1727", {"start": v(-27.5, 61.38) * mm, "end": v(-27.3, 61.07) * mm});
            skLineSegment(sketch, "E1728", {"start": v(-27.3, 61.07) * mm, "end": v(-27.3, 60.96) * mm});
            skLineSegment(sketch, "E1729", {"start": v(-24.75, 58.42) * mm, "end": v(-24.75, 58.31) * mm});
            skLineSegment(sketch, "E1730", {"start": v(-24.75, 58.31) * mm, "end": v(-24.97, 58) * mm});
            skLineSegment(sketch, "E1731", {"start": v(-24.97, 58) * mm, "end": v(-25, 57.98) * mm});
            skLineSegment(sketch, "E1732", {"start": v(-25, 57.98) * mm, "end": v(-25.05, 57.96) * mm});
            skLineSegment(sketch, "E1733", {"start": v(-25.05, 57.96) * mm, "end": v(-25.48, 57.96) * mm});
            skLineSegment(sketch, "E1734", {"start": v(-25.48, 57.96) * mm, "end": v(-25.51, 57.98) * mm});
            skLineSegment(sketch, "E1735", {"start": v(-25.51, 57.98) * mm, "end": v(-25.55, 58) * mm});
            skLineSegment(sketch, "E1736", {"start": v(-25.55, 58) * mm, "end": v(-25.77, 58.32) * mm});
            skLineSegment(sketch, "E1737", {"start": v(-25.77, 58.32) * mm, "end": v(-25.77, 58.42) * mm});
            skLineSegment(sketch, "E1738", {"start": v(-25.77, 58.42) * mm, "end": v(-25.77, 58.53) * mm});
            skLineSegment(sketch, "E1739", {"start": v(-25.77, 58.53) * mm, "end": v(-25.55, 58.84) * mm});
            skLineSegment(sketch, "E1740", {"start": v(-25.55, 58.84) * mm, "end": v(-25.51, 58.86) * mm});
            skLineSegment(sketch, "E1741", {"start": v(-25.51, 58.86) * mm, "end": v(-25.48, 58.88) * mm});
            skLineSegment(sketch, "E1742", {"start": v(-25.48, 58.88) * mm, "end": v(-25.05, 58.88) * mm});
            skLineSegment(sketch, "E1743", {"start": v(-25.05, 58.88) * mm, "end": v(-25, 58.86) * mm});
            skLineSegment(sketch, "E1744", {"start": v(-25, 58.86) * mm, "end": v(-24.97, 58.84) * mm});
            skLineSegment(sketch, "E1745", {"start": v(-24.97, 58.84) * mm, "end": v(-24.75, 58.53) * mm});
            skLineSegment(sketch, "E1746", {"start": v(-24.75, 58.53) * mm, "end": v(-24.75, 58.42) * mm});
            skLineSegment(sketch, "E1747", {"start": v(-24.75, 60.96) * mm, "end": v(-24.75, 60.85) * mm});
            skLineSegment(sketch, "E1748", {"start": v(-24.75, 60.85) * mm, "end": v(-24.97, 60.54) * mm});
            skLineSegment(sketch, "E1749", {"start": v(-24.97, 60.54) * mm, "end": v(-25, 60.52) * mm});
            skLineSegment(sketch, "E1750", {"start": v(-25, 60.52) * mm, "end": v(-25.05, 60.5) * mm});
            skLineSegment(sketch, "E1751", {"start": v(-25.05, 60.5) * mm, "end": v(-25.48, 60.5) * mm});
            skLineSegment(sketch, "E1752", {"start": v(-25.48, 60.5) * mm, "end": v(-25.51, 60.52) * mm});
            skLineSegment(sketch, "E1753", {"start": v(-25.51, 60.52) * mm, "end": v(-25.55, 60.54) * mm});
            skLineSegment(sketch, "E1754", {"start": v(-25.55, 60.54) * mm, "end": v(-25.77, 60.86) * mm});
            skLineSegment(sketch, "E1755", {"start": v(-25.77, 60.86) * mm, "end": v(-25.77, 60.96) * mm});
            skLineSegment(sketch, "E1756", {"start": v(-25.77, 60.96) * mm, "end": v(-25.77, 61.07) * mm});
            skLineSegment(sketch, "E1757", {"start": v(-25.77, 61.07) * mm, "end": v(-25.55, 61.38) * mm});
            skLineSegment(sketch, "E1758", {"start": v(-25.55, 61.38) * mm, "end": v(-25.51, 61.4) * mm});
            skLineSegment(sketch, "E1759", {"start": v(-25.51, 61.4) * mm, "end": v(-25.48, 61.42) * mm});
            skLineSegment(sketch, "E1760", {"start": v(-25.48, 61.42) * mm, "end": v(-25.05, 61.42) * mm});
            skLineSegment(sketch, "E1761", {"start": v(-25.05, 61.42) * mm, "end": v(-25, 61.4) * mm});
            skLineSegment(sketch, "E1762", {"start": v(-25, 61.4) * mm, "end": v(-24.97, 61.38) * mm});
            skLineSegment(sketch, "E1763", {"start": v(-24.97, 61.38) * mm, "end": v(-24.75, 61.07) * mm});
            skLineSegment(sketch, "E1764", {"start": v(-24.75, 61.07) * mm, "end": v(-24.75, 60.96) * mm});
            skLineSegment(sketch, "E1765", {"start": v(-22.21, 58.42) * mm, "end": v(-22.21, 58.31) * mm});
            skLineSegment(sketch, "E1766", {"start": v(-22.21, 58.31) * mm, "end": v(-22.43, 58) * mm});
            skLineSegment(sketch, "E1767", {"start": v(-22.43, 58) * mm, "end": v(-22.47, 57.98) * mm});
            skLineSegment(sketch, "E1768", {"start": v(-22.47, 57.98) * mm, "end": v(-22.5, 57.96) * mm});
            skLineSegment(sketch, "E1769", {"start": v(-22.5, 57.96) * mm, "end": v(-22.93, 57.96) * mm});
            skLineSegment(sketch, "E1770", {"start": v(-22.93, 57.96) * mm, "end": v(-22.97, 57.98) * mm});
            skLineSegment(sketch, "E1771", {"start": v(-22.97, 57.98) * mm, "end": v(-23.01, 58) * mm});
            skLineSegment(sketch, "E1772", {"start": v(-23.01, 58) * mm, "end": v(-23.23, 58.32) * mm});
            skLineSegment(sketch, "E1773", {"start": v(-23.23, 58.32) * mm, "end": v(-23.23, 58.42) * mm});
            skLineSegment(sketch, "E1774", {"start": v(-23.23, 58.42) * mm, "end": v(-23.23, 58.53) * mm});
            skLineSegment(sketch, "E1775", {"start": v(-23.23, 58.53) * mm, "end": v(-23.01, 58.84) * mm});
            skLineSegment(sketch, "E1776", {"start": v(-23.01, 58.84) * mm, "end": v(-22.97, 58.86) * mm});
            skLineSegment(sketch, "E1777", {"start": v(-22.97, 58.86) * mm, "end": v(-22.93, 58.88) * mm});
            skLineSegment(sketch, "E1778", {"start": v(-22.93, 58.88) * mm, "end": v(-22.5, 58.88) * mm});
            skLineSegment(sketch, "E1779", {"start": v(-22.5, 58.88) * mm, "end": v(-22.47, 58.86) * mm});
            skLineSegment(sketch, "E1780", {"start": v(-22.47, 58.86) * mm, "end": v(-22.43, 58.84) * mm});
            skLineSegment(sketch, "E1781", {"start": v(-22.43, 58.84) * mm, "end": v(-22.21, 58.53) * mm});
            skLineSegment(sketch, "E1782", {"start": v(-22.21, 58.53) * mm, "end": v(-22.21, 58.42) * mm});
            skLineSegment(sketch, "E1783", {"start": v(-22.21, 60.96) * mm, "end": v(-22.21, 60.85) * mm});
            skLineSegment(sketch, "E1784", {"start": v(-22.21, 60.85) * mm, "end": v(-22.43, 60.54) * mm});
            skLineSegment(sketch, "E1785", {"start": v(-22.43, 60.54) * mm, "end": v(-22.47, 60.52) * mm});
            skLineSegment(sketch, "E1786", {"start": v(-22.47, 60.52) * mm, "end": v(-22.5, 60.5) * mm});
            skLineSegment(sketch, "E1787", {"start": v(-22.5, 60.5) * mm, "end": v(-22.93, 60.5) * mm});
            skLineSegment(sketch, "E1788", {"start": v(-22.93, 60.5) * mm, "end": v(-22.97, 60.52) * mm});
            skLineSegment(sketch, "E1789", {"start": v(-22.97, 60.52) * mm, "end": v(-23.01, 60.54) * mm});
            skLineSegment(sketch, "E1790", {"start": v(-23.01, 60.54) * mm, "end": v(-23.23, 60.86) * mm});
            skLineSegment(sketch, "E1791", {"start": v(-23.23, 60.86) * mm, "end": v(-23.23, 60.96) * mm});
            skLineSegment(sketch, "E1792", {"start": v(-23.23, 60.96) * mm, "end": v(-23.23, 61.07) * mm});
            skLineSegment(sketch, "E1793", {"start": v(-23.23, 61.07) * mm, "end": v(-23.01, 61.38) * mm});
            skLineSegment(sketch, "E1794", {"start": v(-23.01, 61.38) * mm, "end": v(-22.97, 61.4) * mm});
            skLineSegment(sketch, "E1795", {"start": v(-22.97, 61.4) * mm, "end": v(-22.93, 61.42) * mm});
            skLineSegment(sketch, "E1796", {"start": v(-22.93, 61.42) * mm, "end": v(-22.5, 61.42) * mm});
            skLineSegment(sketch, "E1797", {"start": v(-22.5, 61.42) * mm, "end": v(-22.47, 61.4) * mm});
            skLineSegment(sketch, "E1798", {"start": v(-22.47, 61.4) * mm, "end": v(-22.43, 61.38) * mm});
            skLineSegment(sketch, "E1799", {"start": v(-22.43, 61.38) * mm, "end": v(-22.21, 61.07) * mm});
            skLineSegment(sketch, "E1800", {"start": v(-22.21, 61.07) * mm, "end": v(-22.21, 60.96) * mm});
            skLineSegment(sketch, "E1801", {"start": v(-19.67, 58.42) * mm, "end": v(-19.67, 58.31) * mm});
            skLineSegment(sketch, "E1802", {"start": v(-19.67, 58.31) * mm, "end": v(-19.89, 58) * mm});
            skLineSegment(sketch, "E1803", {"start": v(-19.89, 58) * mm, "end": v(-19.93, 57.98) * mm});
            skLineSegment(sketch, "E1804", {"start": v(-19.93, 57.98) * mm, "end": v(-19.97, 57.96) * mm});
            skLineSegment(sketch, "E1805", {"start": v(-19.97, 57.96) * mm, "end": v(-20.4, 57.96) * mm});
            skLineSegment(sketch, "E1806", {"start": v(-20.4, 57.96) * mm, "end": v(-20.43, 57.98) * mm});
            skLineSegment(sketch, "E1807", {"start": v(-20.43, 57.98) * mm, "end": v(-20.47, 58) * mm});
            skLineSegment(sketch, "E1808", {"start": v(-20.47, 58) * mm, "end": v(-20.69, 58.32) * mm});
            skLineSegment(sketch, "E1809", {"start": v(-20.69, 58.32) * mm, "end": v(-20.69, 58.42) * mm});
            skLineSegment(sketch, "E1810", {"start": v(-20.69, 58.42) * mm, "end": v(-20.69, 58.53) * mm});
            skLineSegment(sketch, "E1811", {"start": v(-20.69, 58.53) * mm, "end": v(-20.47, 58.84) * mm});
            skLineSegment(sketch, "E1812", {"start": v(-20.47, 58.84) * mm, "end": v(-20.43, 58.86) * mm});
            skLineSegment(sketch, "E1813", {"start": v(-20.43, 58.86) * mm, "end": v(-20.4, 58.88) * mm});
            skLineSegment(sketch, "E1814", {"start": v(-20.4, 58.88) * mm, "end": v(-19.97, 58.88) * mm});
            skLineSegment(sketch, "E1815", {"start": v(-19.97, 58.88) * mm, "end": v(-19.93, 58.86) * mm});
            skLineSegment(sketch, "E1816", {"start": v(-19.93, 58.86) * mm, "end": v(-19.89, 58.84) * mm});
            skLineSegment(sketch, "E1817", {"start": v(-19.89, 58.84) * mm, "end": v(-19.67, 58.53) * mm});
            skLineSegment(sketch, "E1818", {"start": v(-19.67, 58.53) * mm, "end": v(-19.67, 58.42) * mm});
            skLineSegment(sketch, "E1819", {"start": v(-19.67, 60.96) * mm, "end": v(-19.67, 60.85) * mm});
            skLineSegment(sketch, "E1820", {"start": v(-19.67, 60.85) * mm, "end": v(-19.89, 60.54) * mm});
            skLineSegment(sketch, "E1821", {"start": v(-19.89, 60.54) * mm, "end": v(-19.93, 60.52) * mm});
            skLineSegment(sketch, "E1822", {"start": v(-19.93, 60.52) * mm, "end": v(-19.97, 60.5) * mm});
            skLineSegment(sketch, "E1823", {"start": v(-19.97, 60.5) * mm, "end": v(-20.4, 60.5) * mm});
            skLineSegment(sketch, "E1824", {"start": v(-20.4, 60.5) * mm, "end": v(-20.43, 60.52) * mm});
            skLineSegment(sketch, "E1825", {"start": v(-20.43, 60.52) * mm, "end": v(-20.47, 60.54) * mm});
            skLineSegment(sketch, "E1826", {"start": v(-20.47, 60.54) * mm, "end": v(-20.69, 60.86) * mm});
            skLineSegment(sketch, "E1827", {"start": v(-20.69, 60.86) * mm, "end": v(-20.69, 60.96) * mm});
            skLineSegment(sketch, "E1828", {"start": v(-20.69, 60.96) * mm, "end": v(-20.69, 61.07) * mm});
            skLineSegment(sketch, "E1829", {"start": v(-20.69, 61.07) * mm, "end": v(-20.47, 61.38) * mm});
            skLineSegment(sketch, "E1830", {"start": v(-20.47, 61.38) * mm, "end": v(-20.43, 61.4) * mm});
            skLineSegment(sketch, "E1831", {"start": v(-20.43, 61.4) * mm, "end": v(-20.4, 61.42) * mm});
            skLineSegment(sketch, "E1832", {"start": v(-20.4, 61.42) * mm, "end": v(-19.97, 61.42) * mm});
            skLineSegment(sketch, "E1833", {"start": v(-19.97, 61.42) * mm, "end": v(-19.93, 61.4) * mm});
            skLineSegment(sketch, "E1834", {"start": v(-19.93, 61.4) * mm, "end": v(-19.89, 61.38) * mm});
            skLineSegment(sketch, "E1835", {"start": v(-19.89, 61.38) * mm, "end": v(-19.67, 61.07) * mm});
            skLineSegment(sketch, "E1836", {"start": v(-19.67, 61.07) * mm, "end": v(-19.67, 60.96) * mm});
            skLineSegment(sketch, "E1837", {"start": v(-17.13, 58.42) * mm, "end": v(-17.13, 58.31) * mm});
            skLineSegment(sketch, "E1838", {"start": v(-17.13, 58.31) * mm, "end": v(-17.35, 58) * mm});
            skLineSegment(sketch, "E1839", {"start": v(-17.35, 58) * mm, "end": v(-17.38, 57.98) * mm});
            skLineSegment(sketch, "E1840", {"start": v(-17.38, 57.98) * mm, "end": v(-17.42, 57.96) * mm});
            skLineSegment(sketch, "E1841", {"start": v(-17.42, 57.96) * mm, "end": v(-17.85, 57.96) * mm});
            skLineSegment(sketch, "E1842", {"start": v(-17.85, 57.96) * mm, "end": v(-17.9, 57.98) * mm});
            skLineSegment(sketch, "E1843", {"start": v(-17.9, 57.98) * mm, "end": v(-17.93, 58) * mm});
            skLineSegment(sketch, "E1844", {"start": v(-17.93, 58) * mm, "end": v(-18.15, 58.32) * mm});
            skLineSegment(sketch, "E1845", {"start": v(-18.15, 58.32) * mm, "end": v(-18.15, 58.42) * mm});
            skLineSegment(sketch, "E1846", {"start": v(-18.15, 58.42) * mm, "end": v(-18.15, 58.53) * mm});
            skLineSegment(sketch, "E1847", {"start": v(-18.15, 58.53) * mm, "end": v(-17.93, 58.84) * mm});
            skLineSegment(sketch, "E1848", {"start": v(-17.93, 58.84) * mm, "end": v(-17.9, 58.86) * mm});
            skLineSegment(sketch, "E1849", {"start": v(-17.9, 58.86) * mm, "end": v(-17.85, 58.88) * mm});
            skLineSegment(sketch, "E1850", {"start": v(-17.85, 58.88) * mm, "end": v(-17.42, 58.88) * mm});
            skLineSegment(sketch, "E1851", {"start": v(-17.42, 58.88) * mm, "end": v(-17.38, 58.86) * mm});
            skLineSegment(sketch, "E1852", {"start": v(-17.38, 58.86) * mm, "end": v(-17.35, 58.84) * mm});
            skLineSegment(sketch, "E1853", {"start": v(-17.35, 58.84) * mm, "end": v(-17.13, 58.53) * mm});
            skLineSegment(sketch, "E1854", {"start": v(-17.13, 58.53) * mm, "end": v(-17.13, 58.42) * mm});
            skLineSegment(sketch, "E1855", {"start": v(-17.13, 60.96) * mm, "end": v(-17.13, 60.85) * mm});
            skLineSegment(sketch, "E1856", {"start": v(-17.13, 60.85) * mm, "end": v(-17.35, 60.54) * mm});
            skLineSegment(sketch, "E1857", {"start": v(-17.35, 60.54) * mm, "end": v(-17.38, 60.52) * mm});
            skLineSegment(sketch, "E1858", {"start": v(-17.38, 60.52) * mm, "end": v(-17.42, 60.5) * mm});
            skLineSegment(sketch, "E1859", {"start": v(-17.42, 60.5) * mm, "end": v(-17.85, 60.5) * mm});
            skLineSegment(sketch, "E1860", {"start": v(-17.85, 60.5) * mm, "end": v(-17.9, 60.52) * mm});
            skLineSegment(sketch, "E1861", {"start": v(-17.9, 60.52) * mm, "end": v(-17.93, 60.54) * mm});
            skLineSegment(sketch, "E1862", {"start": v(-17.93, 60.54) * mm, "end": v(-18.15, 60.86) * mm});
            skLineSegment(sketch, "E1863", {"start": v(-18.15, 60.86) * mm, "end": v(-18.15, 60.96) * mm});
            skLineSegment(sketch, "E1864", {"start": v(-18.15, 60.96) * mm, "end": v(-18.15, 61.07) * mm});
            skLineSegment(sketch, "E1865", {"start": v(-18.15, 61.07) * mm, "end": v(-17.93, 61.38) * mm});
            skLineSegment(sketch, "E1866", {"start": v(-17.93, 61.38) * mm, "end": v(-17.9, 61.4) * mm});
            skLineSegment(sketch, "E1867", {"start": v(-17.9, 61.4) * mm, "end": v(-17.85, 61.42) * mm});
            skLineSegment(sketch, "E1868", {"start": v(-17.85, 61.42) * mm, "end": v(-17.42, 61.42) * mm});
            skLineSegment(sketch, "E1869", {"start": v(-17.42, 61.42) * mm, "end": v(-17.38, 61.4) * mm});
            skLineSegment(sketch, "E1870", {"start": v(-17.38, 61.4) * mm, "end": v(-17.35, 61.38) * mm});
            skLineSegment(sketch, "E1871", {"start": v(-17.35, 61.38) * mm, "end": v(-17.13, 61.07) * mm});
            skLineSegment(sketch, "E1872", {"start": v(-17.13, 61.07) * mm, "end": v(-17.13, 60.96) * mm});
            skLineSegment(sketch, "E1873", {"start": v(-14.6, 58.42) * mm, "end": v(-14.6, 58.31) * mm});
            skLineSegment(sketch, "E1874", {"start": v(-14.6, 58.31) * mm, "end": v(-14.8, 58) * mm});
            skLineSegment(sketch, "E1875", {"start": v(-14.8, 58) * mm, "end": v(-14.85, 57.98) * mm});
            skLineSegment(sketch, "E1876", {"start": v(-14.85, 57.98) * mm, "end": v(-14.89, 57.96) * mm});
            skLineSegment(sketch, "E1877", {"start": v(-14.89, 57.96) * mm, "end": v(-15.32, 57.96) * mm});
            skLineSegment(sketch, "E1878", {"start": v(-15.32, 57.96) * mm, "end": v(-15.35, 57.98) * mm});
            skLineSegment(sketch, "E1879", {"start": v(-15.35, 57.98) * mm, "end": v(-15.4, 58) * mm});
            skLineSegment(sketch, "E1880", {"start": v(-15.4, 58) * mm, "end": v(-15.6, 58.32) * mm});
            skLineSegment(sketch, "E1881", {"start": v(-15.6, 58.32) * mm, "end": v(-15.6, 58.42) * mm});
            skLineSegment(sketch, "E1882", {"start": v(-15.6, 58.42) * mm, "end": v(-15.6, 58.53) * mm});
            skLineSegment(sketch, "E1883", {"start": v(-15.6, 58.53) * mm, "end": v(-15.4, 58.84) * mm});
            skLineSegment(sketch, "E1884", {"start": v(-15.4, 58.84) * mm, "end": v(-15.35, 58.86) * mm});
            skLineSegment(sketch, "E1885", {"start": v(-15.35, 58.86) * mm, "end": v(-15.32, 58.88) * mm});
            skLineSegment(sketch, "E1886", {"start": v(-15.32, 58.88) * mm, "end": v(-14.89, 58.88) * mm});
            skLineSegment(sketch, "E1887", {"start": v(-14.89, 58.88) * mm, "end": v(-14.85, 58.86) * mm});
            skLineSegment(sketch, "E1888", {"start": v(-14.85, 58.86) * mm, "end": v(-14.8, 58.84) * mm});
            skLineSegment(sketch, "E1889", {"start": v(-14.8, 58.84) * mm, "end": v(-14.6, 58.53) * mm});
            skLineSegment(sketch, "E1890", {"start": v(-14.6, 58.53) * mm, "end": v(-14.6, 58.42) * mm});
            skLineSegment(sketch, "E1891", {"start": v(-14.6, 60.96) * mm, "end": v(-14.6, 60.85) * mm});
            skLineSegment(sketch, "E1892", {"start": v(-14.6, 60.85) * mm, "end": v(-14.8, 60.54) * mm});
            skLineSegment(sketch, "E1893", {"start": v(-14.8, 60.54) * mm, "end": v(-14.85, 60.52) * mm});
            skLineSegment(sketch, "E1894", {"start": v(-14.85, 60.52) * mm, "end": v(-14.89, 60.5) * mm});
            skLineSegment(sketch, "E1895", {"start": v(-14.89, 60.5) * mm, "end": v(-15.32, 60.5) * mm});
            skLineSegment(sketch, "E1896", {"start": v(-15.32, 60.5) * mm, "end": v(-15.35, 60.52) * mm});
            skLineSegment(sketch, "E1897", {"start": v(-15.35, 60.52) * mm, "end": v(-15.4, 60.54) * mm});
            skLineSegment(sketch, "E1898", {"start": v(-15.4, 60.54) * mm, "end": v(-15.6, 60.86) * mm});
            skLineSegment(sketch, "E1899", {"start": v(-15.6, 60.86) * mm, "end": v(-15.6, 60.96) * mm});
            skLineSegment(sketch, "E1900", {"start": v(-15.6, 60.96) * mm, "end": v(-15.6, 61.07) * mm});
            skLineSegment(sketch, "E1901", {"start": v(-15.6, 61.07) * mm, "end": v(-15.4, 61.38) * mm});
            skLineSegment(sketch, "E1902", {"start": v(-15.4, 61.38) * mm, "end": v(-15.35, 61.4) * mm});
            skLineSegment(sketch, "E1903", {"start": v(-15.35, 61.4) * mm, "end": v(-15.32, 61.42) * mm});
            skLineSegment(sketch, "E1904", {"start": v(-15.32, 61.42) * mm, "end": v(-14.89, 61.42) * mm});
            skLineSegment(sketch, "E1905", {"start": v(-14.89, 61.42) * mm, "end": v(-14.85, 61.4) * mm});
            skLineSegment(sketch, "E1906", {"start": v(-14.85, 61.4) * mm, "end": v(-14.8, 61.38) * mm});
            skLineSegment(sketch, "E1907", {"start": v(-14.8, 61.38) * mm, "end": v(-14.6, 61.07) * mm});
            skLineSegment(sketch, "E1908", {"start": v(-14.6, 61.07) * mm, "end": v(-14.6, 60.96) * mm});
            skLineSegment(sketch, "E1909", {"start": v(-12.05, 58.42) * mm, "end": v(-12.05, 58.31) * mm});
            skLineSegment(sketch, "E1910", {"start": v(-12.05, 58.31) * mm, "end": v(-12.27, 58) * mm});
            skLineSegment(sketch, "E1911", {"start": v(-12.27, 58) * mm, "end": v(-12.3, 57.98) * mm});
            skLineSegment(sketch, "E1912", {"start": v(-12.3, 57.98) * mm, "end": v(-12.35, 57.96) * mm});
            skLineSegment(sketch, "E1913", {"start": v(-12.35, 57.96) * mm, "end": v(-12.78, 57.96) * mm});
            skLineSegment(sketch, "E1914", {"start": v(-12.78, 57.96) * mm, "end": v(-12.81, 57.98) * mm});
            skLineSegment(sketch, "E1915", {"start": v(-12.81, 57.98) * mm, "end": v(-12.85, 58) * mm});
            skLineSegment(sketch, "E1916", {"start": v(-12.85, 58) * mm, "end": v(-13.07, 58.32) * mm});
            skLineSegment(sketch, "E1917", {"start": v(-13.07, 58.32) * mm, "end": v(-13.07, 58.42) * mm});
            skLineSegment(sketch, "E1918", {"start": v(-13.07, 58.42) * mm, "end": v(-13.07, 58.53) * mm});
            skLineSegment(sketch, "E1919", {"start": v(-13.07, 58.53) * mm, "end": v(-12.85, 58.84) * mm});
            skLineSegment(sketch, "E1920", {"start": v(-12.85, 58.84) * mm, "end": v(-12.81, 58.86) * mm});
            skLineSegment(sketch, "E1921", {"start": v(-12.81, 58.86) * mm, "end": v(-12.78, 58.88) * mm});
            skLineSegment(sketch, "E1922", {"start": v(-12.78, 58.88) * mm, "end": v(-12.35, 58.88) * mm});
            skLineSegment(sketch, "E1923", {"start": v(-12.35, 58.88) * mm, "end": v(-12.3, 58.86) * mm});
            skLineSegment(sketch, "E1924", {"start": v(-12.3, 58.86) * mm, "end": v(-12.27, 58.84) * mm});
            skLineSegment(sketch, "E1925", {"start": v(-12.27, 58.84) * mm, "end": v(-12.05, 58.53) * mm});
            skLineSegment(sketch, "E1926", {"start": v(-12.05, 58.53) * mm, "end": v(-12.05, 58.42) * mm});
            skLineSegment(sketch, "E1927", {"start": v(-12.05, 60.96) * mm, "end": v(-12.05, 60.85) * mm});
            skLineSegment(sketch, "E1928", {"start": v(-12.05, 60.85) * mm, "end": v(-12.27, 60.54) * mm});
            skLineSegment(sketch, "E1929", {"start": v(-12.27, 60.54) * mm, "end": v(-12.3, 60.52) * mm});
            skLineSegment(sketch, "E1930", {"start": v(-12.3, 60.52) * mm, "end": v(-12.35, 60.5) * mm});
            skLineSegment(sketch, "E1931", {"start": v(-12.35, 60.5) * mm, "end": v(-12.78, 60.5) * mm});
            skLineSegment(sketch, "E1932", {"start": v(-12.78, 60.5) * mm, "end": v(-12.81, 60.52) * mm});
            skLineSegment(sketch, "E1933", {"start": v(-12.81, 60.52) * mm, "end": v(-12.85, 60.54) * mm});
            skLineSegment(sketch, "E1934", {"start": v(-12.85, 60.54) * mm, "end": v(-13.07, 60.86) * mm});
            skLineSegment(sketch, "E1935", {"start": v(-13.07, 60.86) * mm, "end": v(-13.07, 60.96) * mm});
            skLineSegment(sketch, "E1936", {"start": v(-13.07, 60.96) * mm, "end": v(-13.07, 61.07) * mm});
            skLineSegment(sketch, "E1937", {"start": v(-13.07, 61.07) * mm, "end": v(-12.85, 61.38) * mm});
            skLineSegment(sketch, "E1938", {"start": v(-12.85, 61.38) * mm, "end": v(-12.81, 61.4) * mm});
            skLineSegment(sketch, "E1939", {"start": v(-12.81, 61.4) * mm, "end": v(-12.78, 61.42) * mm});
            skLineSegment(sketch, "E1940", {"start": v(-12.78, 61.42) * mm, "end": v(-12.35, 61.42) * mm});
            skLineSegment(sketch, "E1941", {"start": v(-12.35, 61.42) * mm, "end": v(-12.3, 61.4) * mm});
            skLineSegment(sketch, "E1942", {"start": v(-12.3, 61.4) * mm, "end": v(-12.27, 61.38) * mm});
            skLineSegment(sketch, "E1943", {"start": v(-12.27, 61.38) * mm, "end": v(-12.05, 61.07) * mm});
            skLineSegment(sketch, "E1944", {"start": v(-12.05, 61.07) * mm, "end": v(-12.05, 60.96) * mm});
            skLineSegment(sketch, "E1945", {"start": v(-9.51, 58.42) * mm, "end": v(-9.51, 58.33) * mm});
            skLineSegment(sketch, "E1946", {"start": v(-9.51, 58.33) * mm, "end": v(-9.66, 58.06) * mm});
            skLineSegment(sketch, "E1947", {"start": v(-9.66, 58.06) * mm, "end": v(-9.93, 57.91) * mm});
            skLineSegment(sketch, "E1948", {"start": v(-9.93, 57.91) * mm, "end": v(-10.02, 57.91) * mm});
            skLineSegment(sketch, "E1949", {"start": v(-10.02, 57.91) * mm, "end": v(-10.11, 57.91) * mm});
            skLineSegment(sketch, "E1950", {"start": v(-10.11, 57.91) * mm, "end": v(-10.38, 58.06) * mm});
            skLineSegment(sketch, "E1951", {"start": v(-10.38, 58.06) * mm, "end": v(-10.53, 58.33) * mm});
            skLineSegment(sketch, "E1952", {"start": v(-10.53, 58.33) * mm, "end": v(-10.53, 58.42) * mm});
            skLineSegment(sketch, "E1953", {"start": v(-10.53, 58.42) * mm, "end": v(-10.53, 58.53) * mm});
            skLineSegment(sketch, "E1954", {"start": v(-10.53, 58.53) * mm, "end": v(-10.31, 58.84) * mm});
            skLineSegment(sketch, "E1955", {"start": v(-10.31, 58.84) * mm, "end": v(-10.27, 58.86) * mm});
            skLineSegment(sketch, "E1956", {"start": v(-10.27, 58.86) * mm, "end": v(-10.23, 58.88) * mm});
            skLineSegment(sketch, "E1957", {"start": v(-10.23, 58.88) * mm, "end": v(-9.8, 58.88) * mm});
            skLineSegment(sketch, "E1958", {"start": v(-9.8, 58.88) * mm, "end": v(-9.77, 58.86) * mm});
            skLineSegment(sketch, "E1959", {"start": v(-9.77, 58.86) * mm, "end": v(-9.73, 58.84) * mm});
            skLineSegment(sketch, "E1960", {"start": v(-9.73, 58.84) * mm, "end": v(-9.51, 58.53) * mm});
            skLineSegment(sketch, "E1961", {"start": v(-9.51, 58.53) * mm, "end": v(-9.51, 58.42) * mm});
            skLineSegment(sketch, "E1962", {"start": v(-9.51, 60.96) * mm, "end": v(-9.51, 60.87) * mm});
            skLineSegment(sketch, "E1963", {"start": v(-9.51, 60.87) * mm, "end": v(-9.66, 60.6) * mm});
            skLineSegment(sketch, "E1964", {"start": v(-9.66, 60.6) * mm, "end": v(-9.93, 60.45) * mm});
            skLineSegment(sketch, "E1965", {"start": v(-9.93, 60.45) * mm, "end": v(-10.02, 60.45) * mm});
            skLineSegment(sketch, "E1966", {"start": v(-10.02, 60.45) * mm, "end": v(-10.11, 60.45) * mm});
            skLineSegment(sketch, "E1967", {"start": v(-10.11, 60.45) * mm, "end": v(-10.38, 60.6) * mm});
            skLineSegment(sketch, "E1968", {"start": v(-10.38, 60.6) * mm, "end": v(-10.53, 60.87) * mm});
            skLineSegment(sketch, "E1969", {"start": v(-10.53, 60.87) * mm, "end": v(-10.53, 60.96) * mm});
            skLineSegment(sketch, "E1970", {"start": v(-10.53, 60.96) * mm, "end": v(-10.53, 61.07) * mm});
            skLineSegment(sketch, "E1971", {"start": v(-10.53, 61.07) * mm, "end": v(-10.31, 61.38) * mm});
            skLineSegment(sketch, "E1972", {"start": v(-10.31, 61.38) * mm, "end": v(-10.27, 61.4) * mm});
            skLineSegment(sketch, "E1973", {"start": v(-10.27, 61.4) * mm, "end": v(-10.23, 61.42) * mm});
            skLineSegment(sketch, "E1974", {"start": v(-10.23, 61.42) * mm, "end": v(-9.8, 61.42) * mm});
            skLineSegment(sketch, "E1975", {"start": v(-9.8, 61.42) * mm, "end": v(-9.77, 61.4) * mm});
            skLineSegment(sketch, "E1976", {"start": v(-9.77, 61.4) * mm, "end": v(-9.73, 61.38) * mm});
            skLineSegment(sketch, "E1977", {"start": v(-9.73, 61.38) * mm, "end": v(-9.51, 61.07) * mm});
            skLineSegment(sketch, "E1978", {"start": v(-9.51, 61.07) * mm, "end": v(-9.51, 60.96) * mm});
            skLineSegment(sketch, "E1979", {"start": v(-6.97, 58.42) * mm, "end": v(-6.97, 58.31) * mm});
            skLineSegment(sketch, "E1980", {"start": v(-6.97, 58.31) * mm, "end": v(-7.19, 58) * mm});
            skLineSegment(sketch, "E1981", {"start": v(-7.19, 58) * mm, "end": v(-7.23, 57.98) * mm});
            skLineSegment(sketch, "E1982", {"start": v(-7.23, 57.98) * mm, "end": v(-7.27, 57.96) * mm});
            skLineSegment(sketch, "E1983", {"start": v(-7.27, 57.96) * mm, "end": v(-7.7, 57.96) * mm});
            skLineSegment(sketch, "E1984", {"start": v(-7.7, 57.96) * mm, "end": v(-7.73, 57.98) * mm});
            skLineSegment(sketch, "E1985", {"start": v(-7.73, 57.98) * mm, "end": v(-7.77, 58) * mm});
            skLineSegment(sketch, "E1986", {"start": v(-7.77, 58) * mm, "end": v(-7.99, 58.32) * mm});
            skLineSegment(sketch, "E1987", {"start": v(-7.99, 58.32) * mm, "end": v(-7.99, 58.42) * mm});
            skLineSegment(sketch, "E1988", {"start": v(-7.99, 58.42) * mm, "end": v(-7.99, 58.53) * mm});
            skLineSegment(sketch, "E1989", {"start": v(-7.99, 58.53) * mm, "end": v(-7.77, 58.84) * mm});
            skLineSegment(sketch, "E1990", {"start": v(-7.77, 58.84) * mm, "end": v(-7.73, 58.86) * mm});
            skLineSegment(sketch, "E1991", {"start": v(-7.73, 58.86) * mm, "end": v(-7.7, 58.88) * mm});
            skLineSegment(sketch, "E1992", {"start": v(-7.7, 58.88) * mm, "end": v(-7.27, 58.88) * mm});
            skLineSegment(sketch, "E1993", {"start": v(-7.27, 58.88) * mm, "end": v(-7.23, 58.86) * mm});
            skLineSegment(sketch, "E1994", {"start": v(-7.23, 58.86) * mm, "end": v(-7.19, 58.84) * mm});
            skLineSegment(sketch, "E1995", {"start": v(-7.19, 58.84) * mm, "end": v(-6.97, 58.53) * mm});
            skLineSegment(sketch, "E1996", {"start": v(-6.97, 58.53) * mm, "end": v(-6.97, 58.42) * mm});
            skLineSegment(sketch, "E1997", {"start": v(-6.97, 60.96) * mm, "end": v(-6.97, 60.85) * mm});
            skLineSegment(sketch, "E1998", {"start": v(-6.97, 60.85) * mm, "end": v(-7.19, 60.54) * mm});
            skLineSegment(sketch, "E1999", {"start": v(-7.19, 60.54) * mm, "end": v(-7.23, 60.52) * mm});
            skLineSegment(sketch, "E2000", {"start": v(-7.23, 60.52) * mm, "end": v(-7.27, 60.5) * mm});
            skLineSegment(sketch, "E2001", {"start": v(-7.27, 60.5) * mm, "end": v(-7.7, 60.5) * mm});
            skLineSegment(sketch, "E2002", {"start": v(-7.7, 60.5) * mm, "end": v(-7.73, 60.52) * mm});
            skLineSegment(sketch, "E2003", {"start": v(-7.73, 60.52) * mm, "end": v(-7.77, 60.54) * mm});
            skLineSegment(sketch, "E2004", {"start": v(-7.77, 60.54) * mm, "end": v(-7.99, 60.86) * mm});
            skLineSegment(sketch, "E2005", {"start": v(-7.99, 60.86) * mm, "end": v(-7.99, 60.96) * mm});
            skLineSegment(sketch, "E2006", {"start": v(-7.99, 60.96) * mm, "end": v(-7.99, 61.07) * mm});
            skLineSegment(sketch, "E2007", {"start": v(-7.99, 61.07) * mm, "end": v(-7.77, 61.38) * mm});
            skLineSegment(sketch, "E2008", {"start": v(-7.77, 61.38) * mm, "end": v(-7.73, 61.4) * mm});
            skLineSegment(sketch, "E2009", {"start": v(-7.73, 61.4) * mm, "end": v(-7.7, 61.42) * mm});
            skLineSegment(sketch, "E2010", {"start": v(-7.7, 61.42) * mm, "end": v(-7.27, 61.42) * mm});
            skLineSegment(sketch, "E2011", {"start": v(-7.27, 61.42) * mm, "end": v(-7.23, 61.4) * mm});
            skLineSegment(sketch, "E2012", {"start": v(-7.23, 61.4) * mm, "end": v(-7.19, 61.38) * mm});
            skLineSegment(sketch, "E2013", {"start": v(-7.19, 61.38) * mm, "end": v(-6.97, 61.07) * mm});
            skLineSegment(sketch, "E2014", {"start": v(-6.97, 61.07) * mm, "end": v(-6.97, 60.96) * mm});
            skLineSegment(sketch, "E2015", {"start": v(-4.43, 58.42) * mm, "end": v(-4.43, 58.31) * mm});
            skLineSegment(sketch, "E2016", {"start": v(-4.43, 58.31) * mm, "end": v(-4.65, 58) * mm});
            skLineSegment(sketch, "E2017", {"start": v(-4.65, 58) * mm, "end": v(-4.68, 57.98) * mm});
            skLineSegment(sketch, "E2018", {"start": v(-4.68, 57.98) * mm, "end": v(-4.72, 57.96) * mm});
            skLineSegment(sketch, "E2019", {"start": v(-4.72, 57.96) * mm, "end": v(-5.15, 57.96) * mm});
            skLineSegment(sketch, "E2020", {"start": v(-5.15, 57.96) * mm, "end": v(-5.2, 57.98) * mm});
            skLineSegment(sketch, "E2021", {"start": v(-5.2, 57.98) * mm, "end": v(-5.23, 58) * mm});
            skLineSegment(sketch, "E2022", {"start": v(-5.23, 58) * mm, "end": v(-5.45, 58.32) * mm});
            skLineSegment(sketch, "E2023", {"start": v(-5.45, 58.32) * mm, "end": v(-5.45, 58.42) * mm});
            skLineSegment(sketch, "E2024", {"start": v(-5.45, 58.42) * mm, "end": v(-5.45, 58.53) * mm});
            skLineSegment(sketch, "E2025", {"start": v(-5.45, 58.53) * mm, "end": v(-5.23, 58.84) * mm});
            skLineSegment(sketch, "E2026", {"start": v(-5.23, 58.84) * mm, "end": v(-5.2, 58.86) * mm});
            skLineSegment(sketch, "E2027", {"start": v(-5.2, 58.86) * mm, "end": v(-5.15, 58.88) * mm});
            skLineSegment(sketch, "E2028", {"start": v(-5.15, 58.88) * mm, "end": v(-4.72, 58.88) * mm});
            skLineSegment(sketch, "E2029", {"start": v(-4.72, 58.88) * mm, "end": v(-4.68, 58.86) * mm});
            skLineSegment(sketch, "E2030", {"start": v(-4.68, 58.86) * mm, "end": v(-4.65, 58.84) * mm});
            skLineSegment(sketch, "E2031", {"start": v(-4.65, 58.84) * mm, "end": v(-4.43, 58.53) * mm});
            skLineSegment(sketch, "E2032", {"start": v(-4.43, 58.53) * mm, "end": v(-4.43, 58.42) * mm});
            skLineSegment(sketch, "E2033", {"start": v(-4.43, 60.96) * mm, "end": v(-4.43, 60.85) * mm});
            skLineSegment(sketch, "E2034", {"start": v(-4.43, 60.85) * mm, "end": v(-4.65, 60.54) * mm});
            skLineSegment(sketch, "E2035", {"start": v(-4.65, 60.54) * mm, "end": v(-4.68, 60.52) * mm});
            skLineSegment(sketch, "E2036", {"start": v(-4.68, 60.52) * mm, "end": v(-4.72, 60.5) * mm});
            skLineSegment(sketch, "E2037", {"start": v(-4.72, 60.5) * mm, "end": v(-5.15, 60.5) * mm});
            skLineSegment(sketch, "E2038", {"start": v(-5.15, 60.5) * mm, "end": v(-5.2, 60.52) * mm});
            skLineSegment(sketch, "E2039", {"start": v(-5.2, 60.52) * mm, "end": v(-5.23, 60.54) * mm});
            skLineSegment(sketch, "E2040", {"start": v(-5.23, 60.54) * mm, "end": v(-5.45, 60.86) * mm});
            skLineSegment(sketch, "E2041", {"start": v(-5.45, 60.86) * mm, "end": v(-5.45, 60.96) * mm});
            skLineSegment(sketch, "E2042", {"start": v(-5.45, 60.96) * mm, "end": v(-5.45, 61.07) * mm});
            skLineSegment(sketch, "E2043", {"start": v(-5.45, 61.07) * mm, "end": v(-5.23, 61.38) * mm});
            skLineSegment(sketch, "E2044", {"start": v(-5.23, 61.38) * mm, "end": v(-5.2, 61.4) * mm});
            skLineSegment(sketch, "E2045", {"start": v(-5.2, 61.4) * mm, "end": v(-5.15, 61.42) * mm});
            skLineSegment(sketch, "E2046", {"start": v(-5.15, 61.42) * mm, "end": v(-4.72, 61.42) * mm});
            skLineSegment(sketch, "E2047", {"start": v(-4.72, 61.42) * mm, "end": v(-4.68, 61.4) * mm});
            skLineSegment(sketch, "E2048", {"start": v(-4.68, 61.4) * mm, "end": v(-4.65, 61.38) * mm});
            skLineSegment(sketch, "E2049", {"start": v(-4.65, 61.38) * mm, "end": v(-4.43, 61.07) * mm});
            skLineSegment(sketch, "E2050", {"start": v(-4.43, 61.07) * mm, "end": v(-4.43, 60.96) * mm});
            skLineSegment(sketch, "E2051", {"start": v(51.3, 58.44) * mm, "end": v(51.3, 58.3) * mm});
            skLineSegment(sketch, "E2052", {"start": v(51.3, 58.3) * mm, "end": v(51.16, 57.89) * mm});
            skLineSegment(sketch, "E2053", {"start": v(51.16, 57.89) * mm, "end": v(50.84, 57.53) * mm});
            skLineSegment(sketch, "E2054", {"start": v(50.84, 57.53) * mm, "end": v(50.75, 57.48) * mm});
            skLineSegment(sketch, "E2055", {"start": v(50.75, 57.48) * mm, "end": v(50.67, 57.44) * mm});
            skLineSegment(sketch, "E2056", {"start": v(50.67, 57.44) * mm, "end": v(50.2, 57.34) * mm});
            skLineSegment(sketch, "E2057", {"start": v(50.2, 57.34) * mm, "end": v(49.74, 57.44) * mm});
            skLineSegment(sketch, "E2058", {"start": v(49.74, 57.44) * mm, "end": v(49.65, 57.48) * mm});
            skLineSegment(sketch, "E2059", {"start": v(49.65, 57.48) * mm, "end": v(49.57, 57.53) * mm});
            skLineSegment(sketch, "E2060", {"start": v(49.57, 57.53) * mm, "end": v(49.25, 57.89) * mm});
            skLineSegment(sketch, "E2061", {"start": v(49.25, 57.89) * mm, "end": v(49.1, 58.3) * mm});
            skLineSegment(sketch, "E2062", {"start": v(49.1, 58.3) * mm, "end": v(49.1, 58.44) * mm});
            skLineSegment(sketch, "E2063", {"start": v(49.1, 58.44) * mm, "end": v(49.1, 58.58) * mm});
            skLineSegment(sketch, "E2064", {"start": v(49.1, 58.58) * mm, "end": v(49.25, 58.99) * mm});
            skLineSegment(sketch, "E2065", {"start": v(49.25, 58.99) * mm, "end": v(49.57, 59.34) * mm});
            skLineSegment(sketch, "E2066", {"start": v(49.57, 59.34) * mm, "end": v(49.65, 59.4) * mm});
            skLineSegment(sketch, "E2067", {"start": v(49.65, 59.4) * mm, "end": v(49.74, 59.44) * mm});
            skLineSegment(sketch, "E2068", {"start": v(49.74, 59.44) * mm, "end": v(50.2, 59.54) * mm});
            skLineSegment(sketch, "E2069", {"start": v(50.2, 59.54) * mm, "end": v(50.67, 59.44) * mm});
            skLineSegment(sketch, "E2070", {"start": v(50.67, 59.44) * mm, "end": v(50.75, 59.4) * mm});
            skLineSegment(sketch, "E2071", {"start": v(50.75, 59.4) * mm, "end": v(50.84, 59.34) * mm});
            skLineSegment(sketch, "E2072", {"start": v(50.84, 59.34) * mm, "end": v(51.16, 58.99) * mm});
            skLineSegment(sketch, "E2073", {"start": v(51.16, 58.99) * mm, "end": v(51.3, 58.58) * mm});
            skLineSegment(sketch, "E2074", {"start": v(51.3, 58.58) * mm, "end": v(51.3, 58.44) * mm});
            skLineSegment(sketch, "E2075", {"start": v(51.3, 48.24) * mm, "end": v(51.3, 48.1) * mm});
            skLineSegment(sketch, "E2076", {"start": v(51.3, 48.1) * mm, "end": v(51.16, 47.69) * mm});
            skLineSegment(sketch, "E2077", {"start": v(51.16, 47.69) * mm, "end": v(50.84, 47.34) * mm});
            skLineSegment(sketch, "E2078", {"start": v(50.84, 47.34) * mm, "end": v(50.75, 47.29) * mm});
            skLineSegment(sketch, "E2079", {"start": v(50.75, 47.29) * mm, "end": v(50.67, 47.24) * mm});
            skLineSegment(sketch, "E2080", {"start": v(50.67, 47.24) * mm, "end": v(50.2, 47.14) * mm});
            skLineSegment(sketch, "E2081", {"start": v(50.2, 47.14) * mm, "end": v(49.74, 47.24) * mm});
            skLineSegment(sketch, "E2082", {"start": v(49.74, 47.24) * mm, "end": v(49.65, 47.29) * mm});
            skLineSegment(sketch, "E2083", {"start": v(49.65, 47.29) * mm, "end": v(49.57, 47.34) * mm});
            skLineSegment(sketch, "E2084", {"start": v(49.57, 47.34) * mm, "end": v(49.25, 47.69) * mm});
            skLineSegment(sketch, "E2085", {"start": v(49.25, 47.69) * mm, "end": v(49.1, 48.1) * mm});
            skLineSegment(sketch, "E2086", {"start": v(49.1, 48.1) * mm, "end": v(49.1, 48.24) * mm});
            skLineSegment(sketch, "E2087", {"start": v(49.1, 48.24) * mm, "end": v(49.1, 48.38) * mm});
            skLineSegment(sketch, "E2088", {"start": v(49.1, 48.38) * mm, "end": v(49.25, 48.8) * mm});
            skLineSegment(sketch, "E2089", {"start": v(49.25, 48.8) * mm, "end": v(49.57, 49.14) * mm});
            skLineSegment(sketch, "E2090", {"start": v(49.57, 49.14) * mm, "end": v(49.65, 49.2) * mm});
            skLineSegment(sketch, "E2091", {"start": v(49.65, 49.2) * mm, "end": v(49.74, 49.24) * mm});
            skLineSegment(sketch, "E2092", {"start": v(49.74, 49.24) * mm, "end": v(50.2, 49.34) * mm});
            skLineSegment(sketch, "E2093", {"start": v(50.2, 49.34) * mm, "end": v(50.67, 49.24) * mm});
            skLineSegment(sketch, "E2094", {"start": v(50.67, 49.24) * mm, "end": v(50.75, 49.2) * mm});
            skLineSegment(sketch, "E2095", {"start": v(50.75, 49.2) * mm, "end": v(50.84, 49.14) * mm});
            skLineSegment(sketch, "E2096", {"start": v(50.84, 49.14) * mm, "end": v(51.16, 48.8) * mm});
            skLineSegment(sketch, "E2097", {"start": v(51.16, 48.8) * mm, "end": v(51.3, 48.38) * mm});
            skLineSegment(sketch, "E2098", {"start": v(51.3, 48.38) * mm, "end": v(51.3, 48.24) * mm});
            skLineSegment(sketch, "E2099", {"start": v(46.44, 53.34) * mm, "end": v(46.44, 53.23) * mm});
            skLineSegment(sketch, "E2100", {"start": v(46.44, 53.23) * mm, "end": v(46.23, 52.93) * mm});
            skLineSegment(sketch, "E2101", {"start": v(46.23, 52.93) * mm, "end": v(46.19, 52.9) * mm});
            skLineSegment(sketch, "E2102", {"start": v(46.19, 52.9) * mm, "end": v(46.15, 52.88) * mm});
            skLineSegment(sketch, "E2103", {"start": v(46.15, 52.88) * mm, "end": v(45.73, 52.88) * mm});
            skLineSegment(sketch, "E2104", {"start": v(45.73, 52.88) * mm, "end": v(45.69, 52.9) * mm});
            skLineSegment(sketch, "E2105", {"start": v(45.69, 52.9) * mm, "end": v(45.65, 52.93) * mm});
            skLineSegment(sketch, "E2106", {"start": v(45.65, 52.93) * mm, "end": v(45.44, 53.24) * mm});
            skLineSegment(sketch, "E2107", {"start": v(45.44, 53.24) * mm, "end": v(45.44, 53.34) * mm});
            skLineSegment(sketch, "E2108", {"start": v(45.44, 53.34) * mm, "end": v(45.44, 53.45) * mm});
            skLineSegment(sketch, "E2109", {"start": v(45.44, 53.45) * mm, "end": v(45.65, 53.75) * mm});
            skLineSegment(sketch, "E2110", {"start": v(45.65, 53.75) * mm, "end": v(45.69, 53.77) * mm});
            skLineSegment(sketch, "E2111", {"start": v(45.69, 53.77) * mm, "end": v(45.73, 53.8) * mm});
            skLineSegment(sketch, "E2112", {"start": v(45.73, 53.8) * mm, "end": v(46.15, 53.8) * mm});
            skLineSegment(sketch, "E2113", {"start": v(46.15, 53.8) * mm, "end": v(46.19, 53.77) * mm});
            skLineSegment(sketch, "E2114", {"start": v(46.19, 53.77) * mm, "end": v(46.23, 53.75) * mm});
            skLineSegment(sketch, "E2115", {"start": v(46.23, 53.75) * mm, "end": v(46.44, 53.44) * mm});
            skLineSegment(sketch, "E2116", {"start": v(46.44, 53.44) * mm, "end": v(46.44, 53.34) * mm});
            skLineSegment(sketch, "E2117", {"start": v(46.44, 55.84) * mm, "end": v(46.44, 55.73) * mm});
            skLineSegment(sketch, "E2118", {"start": v(46.44, 55.73) * mm, "end": v(46.23, 55.43) * mm});
            skLineSegment(sketch, "E2119", {"start": v(46.23, 55.43) * mm, "end": v(46.19, 55.4) * mm});
            skLineSegment(sketch, "E2120", {"start": v(46.19, 55.4) * mm, "end": v(46.15, 55.38) * mm});
            skLineSegment(sketch, "E2121", {"start": v(46.15, 55.38) * mm, "end": v(45.73, 55.38) * mm});
            skLineSegment(sketch, "E2122", {"start": v(45.73, 55.38) * mm, "end": v(45.69, 55.4) * mm});
            skLineSegment(sketch, "E2123", {"start": v(45.69, 55.4) * mm, "end": v(45.65, 55.43) * mm});
            skLineSegment(sketch, "E2124", {"start": v(45.65, 55.43) * mm, "end": v(45.44, 55.74) * mm});
            skLineSegment(sketch, "E2125", {"start": v(45.44, 55.74) * mm, "end": v(45.44, 55.84) * mm});
            skLineSegment(sketch, "E2126", {"start": v(45.44, 55.84) * mm, "end": v(45.44, 55.95) * mm});
            skLineSegment(sketch, "E2127", {"start": v(45.44, 55.95) * mm, "end": v(45.65, 56.25) * mm});
            skLineSegment(sketch, "E2128", {"start": v(45.65, 56.25) * mm, "end": v(45.69, 56.27) * mm});
            skLineSegment(sketch, "E2129", {"start": v(45.69, 56.27) * mm, "end": v(45.73, 56.3) * mm});
            skLineSegment(sketch, "E2130", {"start": v(45.73, 56.3) * mm, "end": v(46.15, 56.3) * mm});
            skLineSegment(sketch, "E2131", {"start": v(46.15, 56.3) * mm, "end": v(46.19, 56.27) * mm});
            skLineSegment(sketch, "E2132", {"start": v(46.19, 56.27) * mm, "end": v(46.23, 56.25) * mm});
            skLineSegment(sketch, "E2133", {"start": v(46.23, 56.25) * mm, "end": v(46.44, 55.94) * mm});
            skLineSegment(sketch, "E2134", {"start": v(46.44, 55.94) * mm, "end": v(46.44, 55.84) * mm});
            skLineSegment(sketch, "E2135", {"start": v(47.66, -59.36) * mm, "end": v(47.66, -59.47) * mm});
            skLineSegment(sketch, "E2136", {"start": v(47.66, -59.47) * mm, "end": v(47.45, -59.78) * mm});
            skLineSegment(sketch, "E2137", {"start": v(47.45, -59.78) * mm, "end": v(47.41, -59.8) * mm});
            skLineSegment(sketch, "E2138", {"start": v(47.41, -59.8) * mm, "end": v(47.37, -59.82) * mm});
            skLineSegment(sketch, "E2139", {"start": v(47.37, -59.82) * mm, "end": v(46.94, -59.82) * mm});
            skLineSegment(sketch, "E2140", {"start": v(46.94, -59.82) * mm, "end": v(46.9, -59.8) * mm});
            skLineSegment(sketch, "E2141", {"start": v(46.9, -59.8) * mm, "end": v(46.86, -59.78) * mm});
            skLineSegment(sketch, "E2142", {"start": v(46.86, -59.78) * mm, "end": v(46.65, -59.46) * mm});
            skLineSegment(sketch, "E2143", {"start": v(46.65, -59.46) * mm, "end": v(46.65, -59.36) * mm});
            skLineSegment(sketch, "E2144", {"start": v(46.65, -59.36) * mm, "end": v(46.65, -59.25) * mm});
            skLineSegment(sketch, "E2145", {"start": v(46.65, -59.25) * mm, "end": v(46.86, -58.94) * mm});
            skLineSegment(sketch, "E2146", {"start": v(46.86, -58.94) * mm, "end": v(46.9, -58.92) * mm});
            skLineSegment(sketch, "E2147", {"start": v(46.9, -58.92) * mm, "end": v(46.94, -58.9) * mm});
            skLineSegment(sketch, "E2148", {"start": v(46.94, -58.9) * mm, "end": v(47.37, -58.9) * mm});
            skLineSegment(sketch, "E2149", {"start": v(47.37, -58.9) * mm, "end": v(47.41, -58.92) * mm});
            skLineSegment(sketch, "E2150", {"start": v(47.41, -58.92) * mm, "end": v(47.45, -58.94) * mm});
            skLineSegment(sketch, "E2151", {"start": v(47.45, -58.94) * mm, "end": v(47.66, -59.26) * mm});
            skLineSegment(sketch, "E2152", {"start": v(47.66, -59.26) * mm, "end": v(47.66, -59.36) * mm});
            skLineSegment(sketch, "E2153", {"start": v(50.2, -59.36) * mm, "end": v(50.2, -59.47) * mm});
            skLineSegment(sketch, "E2154", {"start": v(50.2, -59.47) * mm, "end": v(49.99, -59.78) * mm});
            skLineSegment(sketch, "E2155", {"start": v(49.99, -59.78) * mm, "end": v(49.95, -59.8) * mm});
            skLineSegment(sketch, "E2156", {"start": v(49.95, -59.8) * mm, "end": v(49.91, -59.82) * mm});
            skLineSegment(sketch, "E2157", {"start": v(49.91, -59.82) * mm, "end": v(49.48, -59.82) * mm});
            skLineSegment(sketch, "E2158", {"start": v(49.48, -59.82) * mm, "end": v(49.44, -59.8) * mm});
            skLineSegment(sketch, "E2159", {"start": v(49.44, -59.8) * mm, "end": v(49.4, -59.78) * mm});
            skLineSegment(sketch, "E2160", {"start": v(49.4, -59.78) * mm, "end": v(49.19, -59.46) * mm});
            skLineSegment(sketch, "E2161", {"start": v(49.19, -59.46) * mm, "end": v(49.19, -59.36) * mm});
            skLineSegment(sketch, "E2162", {"start": v(49.19, -59.36) * mm, "end": v(49.19, -59.25) * mm});
            skLineSegment(sketch, "E2163", {"start": v(49.19, -59.25) * mm, "end": v(49.4, -58.94) * mm});
            skLineSegment(sketch, "E2164", {"start": v(49.4, -58.94) * mm, "end": v(49.44, -58.92) * mm});
            skLineSegment(sketch, "E2165", {"start": v(49.44, -58.92) * mm, "end": v(49.48, -58.9) * mm});
            skLineSegment(sketch, "E2166", {"start": v(49.48, -58.9) * mm, "end": v(49.91, -58.9) * mm});
            skLineSegment(sketch, "E2167", {"start": v(49.91, -58.9) * mm, "end": v(49.95, -58.92) * mm});
            skLineSegment(sketch, "E2168", {"start": v(49.95, -58.92) * mm, "end": v(49.99, -58.94) * mm});
            skLineSegment(sketch, "E2169", {"start": v(49.99, -58.94) * mm, "end": v(50.2, -59.26) * mm});
            skLineSegment(sketch, "E2170", {"start": v(50.2, -59.26) * mm, "end": v(50.2, -59.36) * mm});
            skLineSegment(sketch, "E2171", {"start": v(52.74, -59.36) * mm, "end": v(52.74, -59.47) * mm});
            skLineSegment(sketch, "E2172", {"start": v(52.74, -59.47) * mm, "end": v(52.53, -59.78) * mm});
            skLineSegment(sketch, "E2173", {"start": v(52.53, -59.78) * mm, "end": v(52.5, -59.8) * mm});
            skLineSegment(sketch, "E2174", {"start": v(52.5, -59.8) * mm, "end": v(52.45, -59.82) * mm});
            skLineSegment(sketch, "E2175", {"start": v(52.45, -59.82) * mm, "end": v(52.02, -59.82) * mm});
            skLineSegment(sketch, "E2176", {"start": v(52.02, -59.82) * mm, "end": v(51.98, -59.8) * mm});
            skLineSegment(sketch, "E2177", {"start": v(51.98, -59.8) * mm, "end": v(51.94, -59.78) * mm});
            skLineSegment(sketch, "E2178", {"start": v(51.94, -59.78) * mm, "end": v(51.73, -59.46) * mm});
            skLineSegment(sketch, "E2179", {"start": v(51.73, -59.46) * mm, "end": v(51.73, -59.36) * mm});
            skLineSegment(sketch, "E2180", {"start": v(51.73, -59.36) * mm, "end": v(51.73, -59.25) * mm});
            skLineSegment(sketch, "E2181", {"start": v(51.73, -59.25) * mm, "end": v(51.94, -58.94) * mm});
            skLineSegment(sketch, "E2182", {"start": v(51.94, -58.94) * mm, "end": v(51.98, -58.92) * mm});
            skLineSegment(sketch, "E2183", {"start": v(51.98, -58.92) * mm, "end": v(52.02, -58.9) * mm});
            skLineSegment(sketch, "E2184", {"start": v(52.02, -58.9) * mm, "end": v(52.45, -58.9) * mm});
            skLineSegment(sketch, "E2185", {"start": v(52.45, -58.9) * mm, "end": v(52.5, -58.92) * mm});
            skLineSegment(sketch, "E2186", {"start": v(52.5, -58.92) * mm, "end": v(52.53, -58.94) * mm});
            skLineSegment(sketch, "E2187", {"start": v(52.53, -58.94) * mm, "end": v(52.74, -59.26) * mm});
            skLineSegment(sketch, "E2188", {"start": v(52.74, -59.26) * mm, "end": v(52.74, -59.36) * mm});
            skLineSegment(sketch, "E2189", {"start": v(55.28, -59.36) * mm, "end": v(55.28, -59.47) * mm});
            skLineSegment(sketch, "E2190", {"start": v(55.28, -59.47) * mm, "end": v(55.07, -59.78) * mm});
            skLineSegment(sketch, "E2191", {"start": v(55.07, -59.78) * mm, "end": v(55.03, -59.8) * mm});
            skLineSegment(sketch, "E2192", {"start": v(55.03, -59.8) * mm, "end": v(54.99, -59.82) * mm});
            skLineSegment(sketch, "E2193", {"start": v(54.99, -59.82) * mm, "end": v(54.56, -59.82) * mm});
            skLineSegment(sketch, "E2194", {"start": v(54.56, -59.82) * mm, "end": v(54.52, -59.8) * mm});
            skLineSegment(sketch, "E2195", {"start": v(54.52, -59.8) * mm, "end": v(54.48, -59.78) * mm});
            skLineSegment(sketch, "E2196", {"start": v(54.48, -59.78) * mm, "end": v(54.27, -59.46) * mm});
            skLineSegment(sketch, "E2197", {"start": v(54.27, -59.46) * mm, "end": v(54.27, -59.36) * mm});
            skLineSegment(sketch, "E2198", {"start": v(54.27, -59.36) * mm, "end": v(54.27, -59.25) * mm});
            skLineSegment(sketch, "E2199", {"start": v(54.27, -59.25) * mm, "end": v(54.48, -58.94) * mm});
            skLineSegment(sketch, "E2200", {"start": v(54.48, -58.94) * mm, "end": v(54.52, -58.92) * mm});
            skLineSegment(sketch, "E2201", {"start": v(54.52, -58.92) * mm, "end": v(54.56, -58.9) * mm});
            skLineSegment(sketch, "E2202", {"start": v(54.56, -58.9) * mm, "end": v(54.99, -58.9) * mm});
            skLineSegment(sketch, "E2203", {"start": v(54.99, -58.9) * mm, "end": v(55.03, -58.92) * mm});
            skLineSegment(sketch, "E2204", {"start": v(55.03, -58.92) * mm, "end": v(55.07, -58.94) * mm});
            skLineSegment(sketch, "E2205", {"start": v(55.07, -58.94) * mm, "end": v(55.28, -59.26) * mm});
            skLineSegment(sketch, "E2206", {"start": v(55.28, -59.26) * mm, "end": v(55.28, -59.36) * mm});
            skLineSegment(sketch, "E2207", {"start": v(57.82, -59.36) * mm, "end": v(57.82, -59.47) * mm});
            skLineSegment(sketch, "E2208", {"start": v(57.82, -59.47) * mm, "end": v(57.6, -59.78) * mm});
            skLineSegment(sketch, "E2209", {"start": v(57.6, -59.78) * mm, "end": v(57.57, -59.8) * mm});
            skLineSegment(sketch, "E2210", {"start": v(57.57, -59.8) * mm, "end": v(57.53, -59.82) * mm});
            skLineSegment(sketch, "E2211", {"start": v(57.53, -59.82) * mm, "end": v(57.1, -59.82) * mm});
            skLineSegment(sketch, "E2212", {"start": v(57.1, -59.82) * mm, "end": v(57.06, -59.8) * mm});
            skLineSegment(sketch, "E2213", {"start": v(57.06, -59.8) * mm, "end": v(57.02, -59.78) * mm});
            skLineSegment(sketch, "E2214", {"start": v(57.02, -59.78) * mm, "end": v(56.8, -59.46) * mm});
            skLineSegment(sketch, "E2215", {"start": v(56.8, -59.46) * mm, "end": v(56.8, -59.36) * mm});
            skLineSegment(sketch, "E2216", {"start": v(56.8, -59.36) * mm, "end": v(56.8, -59.25) * mm});
            skLineSegment(sketch, "E2217", {"start": v(56.8, -59.25) * mm, "end": v(57.02, -58.94) * mm});
            skLineSegment(sketch, "E2218", {"start": v(57.02, -58.94) * mm, "end": v(57.06, -58.92) * mm});
            skLineSegment(sketch, "E2219", {"start": v(57.06, -58.92) * mm, "end": v(57.1, -58.9) * mm});
            skLineSegment(sketch, "E2220", {"start": v(57.1, -58.9) * mm, "end": v(57.53, -58.9) * mm});
            skLineSegment(sketch, "E2221", {"start": v(57.53, -58.9) * mm, "end": v(57.57, -58.92) * mm});
            skLineSegment(sketch, "E2222", {"start": v(57.57, -58.92) * mm, "end": v(57.6, -58.94) * mm});
            skLineSegment(sketch, "E2223", {"start": v(57.6, -58.94) * mm, "end": v(57.82, -59.26) * mm});
            skLineSegment(sketch, "E2224", {"start": v(57.82, -59.26) * mm, "end": v(57.82, -59.36) * mm});
            skLineSegment(sketch, "E2225", {"start": v(60.36, -59.36) * mm, "end": v(60.36, -59.47) * mm});
            skLineSegment(sketch, "E2226", {"start": v(60.36, -59.47) * mm, "end": v(60.15, -59.78) * mm});
            skLineSegment(sketch, "E2227", {"start": v(60.15, -59.78) * mm, "end": v(60.11, -59.8) * mm});
            skLineSegment(sketch, "E2228", {"start": v(60.11, -59.8) * mm, "end": v(60.07, -59.82) * mm});
            skLineSegment(sketch, "E2229", {"start": v(60.07, -59.82) * mm, "end": v(59.64, -59.82) * mm});
            skLineSegment(sketch, "E2230", {"start": v(59.64, -59.82) * mm, "end": v(59.6, -59.8) * mm});
            skLineSegment(sketch, "E2231", {"start": v(59.6, -59.8) * mm, "end": v(59.56, -59.78) * mm});
            skLineSegment(sketch, "E2232", {"start": v(59.56, -59.78) * mm, "end": v(59.35, -59.46) * mm});
            skLineSegment(sketch, "E2233", {"start": v(59.35, -59.46) * mm, "end": v(59.35, -59.36) * mm});
            skLineSegment(sketch, "E2234", {"start": v(59.35, -59.36) * mm, "end": v(59.35, -59.25) * mm});
            skLineSegment(sketch, "E2235", {"start": v(59.35, -59.25) * mm, "end": v(59.56, -58.94) * mm});
            skLineSegment(sketch, "E2236", {"start": v(59.56, -58.94) * mm, "end": v(59.6, -58.92) * mm});
            skLineSegment(sketch, "E2237", {"start": v(59.6, -58.92) * mm, "end": v(59.64, -58.9) * mm});
            skLineSegment(sketch, "E2238", {"start": v(59.64, -58.9) * mm, "end": v(60.07, -58.9) * mm});
            skLineSegment(sketch, "E2239", {"start": v(60.07, -58.9) * mm, "end": v(60.11, -58.92) * mm});
            skLineSegment(sketch, "E2240", {"start": v(60.11, -58.92) * mm, "end": v(60.15, -58.94) * mm});
            skLineSegment(sketch, "E2241", {"start": v(60.15, -58.94) * mm, "end": v(60.36, -59.26) * mm});
            skLineSegment(sketch, "E2242", {"start": v(60.36, -59.26) * mm, "end": v(60.36, -59.36) * mm});
            skLineSegment(sketch, "E2243", {"start": v(-61.58, -13.97) * mm, "end": v(-61.58, -14.08) * mm});
            skLineSegment(sketch, "E2244", {"start": v(-61.58, -14.08) * mm, "end": v(-61.8, -14.39) * mm});
            skLineSegment(sketch, "E2245", {"start": v(-61.8, -14.39) * mm, "end": v(-61.83, -14.41) * mm});
            skLineSegment(sketch, "E2246", {"start": v(-61.83, -14.41) * mm, "end": v(-61.87, -14.43) * mm});
            skLineSegment(sketch, "E2247", {"start": v(-61.87, -14.43) * mm, "end": v(-62.3, -14.43) * mm});
            skLineSegment(sketch, "E2248", {"start": v(-62.3, -14.43) * mm, "end": v(-62.34, -14.41) * mm});
            skLineSegment(sketch, "E2249", {"start": v(-62.34, -14.41) * mm, "end": v(-62.38, -14.39) * mm});
            skLineSegment(sketch, "E2250", {"start": v(-62.38, -14.39) * mm, "end": v(-62.6, -14.07) * mm});
            skLineSegment(sketch, "E2251", {"start": v(-62.6, -14.07) * mm, "end": v(-62.6, -13.97) * mm});
            skLineSegment(sketch, "E2252", {"start": v(-62.6, -13.97) * mm, "end": v(-62.6, -13.86) * mm});
            skLineSegment(sketch, "E2253", {"start": v(-62.6, -13.86) * mm, "end": v(-62.38, -13.55) * mm});
            skLineSegment(sketch, "E2254", {"start": v(-62.38, -13.55) * mm, "end": v(-62.34, -13.53) * mm});
            skLineSegment(sketch, "E2255", {"start": v(-62.34, -13.53) * mm, "end": v(-62.3, -13.5) * mm});
            skLineSegment(sketch, "E2256", {"start": v(-62.3, -13.5) * mm, "end": v(-61.87, -13.5) * mm});
            skLineSegment(sketch, "E2257", {"start": v(-61.87, -13.5) * mm, "end": v(-61.83, -13.53) * mm});
            skLineSegment(sketch, "E2258", {"start": v(-61.83, -13.53) * mm, "end": v(-61.8, -13.55) * mm});
            skLineSegment(sketch, "E2259", {"start": v(-61.8, -13.55) * mm, "end": v(-61.58, -13.87) * mm});
            skLineSegment(sketch, "E2260", {"start": v(-61.58, -13.87) * mm, "end": v(-61.58, -13.97) * mm});
            skLineSegment(sketch, "E2261", {"start": v(-59.04, -13.97) * mm, "end": v(-59.04, -14.08) * mm});
            skLineSegment(sketch, "E2262", {"start": v(-59.04, -14.08) * mm, "end": v(-59.26, -14.39) * mm});
            skLineSegment(sketch, "E2263", {"start": v(-59.26, -14.39) * mm, "end": v(-59.3, -14.41) * mm});
            skLineSegment(sketch, "E2264", {"start": v(-59.3, -14.41) * mm, "end": v(-59.33, -14.43) * mm});
            skLineSegment(sketch, "E2265", {"start": v(-59.33, -14.43) * mm, "end": v(-59.76, -14.43) * mm});
            skLineSegment(sketch, "E2266", {"start": v(-59.76, -14.43) * mm, "end": v(-59.8, -14.41) * mm});
            skLineSegment(sketch, "E2267", {"start": v(-59.8, -14.41) * mm, "end": v(-59.84, -14.39) * mm});
            skLineSegment(sketch, "E2268", {"start": v(-59.84, -14.39) * mm, "end": v(-60.06, -14.07) * mm});
            skLineSegment(sketch, "E2269", {"start": v(-60.06, -14.07) * mm, "end": v(-60.06, -13.97) * mm});
            skLineSegment(sketch, "E2270", {"start": v(-60.06, -13.97) * mm, "end": v(-60.06, -13.86) * mm});
            skLineSegment(sketch, "E2271", {"start": v(-60.06, -13.86) * mm, "end": v(-59.84, -13.55) * mm});
            skLineSegment(sketch, "E2272", {"start": v(-59.84, -13.55) * mm, "end": v(-59.8, -13.53) * mm});
            skLineSegment(sketch, "E2273", {"start": v(-59.8, -13.53) * mm, "end": v(-59.76, -13.5) * mm});
            skLineSegment(sketch, "E2274", {"start": v(-59.76, -13.5) * mm, "end": v(-59.33, -13.5) * mm});
            skLineSegment(sketch, "E2275", {"start": v(-59.33, -13.5) * mm, "end": v(-59.3, -13.53) * mm});
            skLineSegment(sketch, "E2276", {"start": v(-59.3, -13.53) * mm, "end": v(-59.26, -13.55) * mm});
            skLineSegment(sketch, "E2277", {"start": v(-59.26, -13.55) * mm, "end": v(-59.04, -13.87) * mm});
            skLineSegment(sketch, "E2278", {"start": v(-59.04, -13.87) * mm, "end": v(-59.04, -13.97) * mm});
            skLineSegment(sketch, "E2279", {"start": v(-61.58, -16.51) * mm, "end": v(-61.58, -16.62) * mm});
            skLineSegment(sketch, "E2280", {"start": v(-61.58, -16.62) * mm, "end": v(-61.8, -16.93) * mm});
            skLineSegment(sketch, "E2281", {"start": v(-61.8, -16.93) * mm, "end": v(-61.83, -16.95) * mm});
            skLineSegment(sketch, "E2282", {"start": v(-61.83, -16.95) * mm, "end": v(-61.87, -16.97) * mm});
            skLineSegment(sketch, "E2283", {"start": v(-61.87, -16.97) * mm, "end": v(-62.3, -16.97) * mm});
            skLineSegment(sketch, "E2284", {"start": v(-62.3, -16.97) * mm, "end": v(-62.34, -16.95) * mm});
            skLineSegment(sketch, "E2285", {"start": v(-62.34, -16.95) * mm, "end": v(-62.38, -16.93) * mm});
            skLineSegment(sketch, "E2286", {"start": v(-62.38, -16.93) * mm, "end": v(-62.6, -16.61) * mm});
            skLineSegment(sketch, "E2287", {"start": v(-62.6, -16.61) * mm, "end": v(-62.6, -16.51) * mm});
            skLineSegment(sketch, "E2288", {"start": v(-62.6, -16.51) * mm, "end": v(-62.6, -16.4) * mm});
            skLineSegment(sketch, "E2289", {"start": v(-62.6, -16.4) * mm, "end": v(-62.38, -16.1) * mm});
            skLineSegment(sketch, "E2290", {"start": v(-62.38, -16.1) * mm, "end": v(-62.34, -16.07) * mm});
            skLineSegment(sketch, "E2291", {"start": v(-62.34, -16.07) * mm, "end": v(-62.3, -16.05) * mm});
            skLineSegment(sketch, "E2292", {"start": v(-62.3, -16.05) * mm, "end": v(-61.87, -16.05) * mm});
            skLineSegment(sketch, "E2293", {"start": v(-61.87, -16.05) * mm, "end": v(-61.83, -16.07) * mm});
            skLineSegment(sketch, "E2294", {"start": v(-61.83, -16.07) * mm, "end": v(-61.8, -16.1) * mm});
            skLineSegment(sketch, "E2295", {"start": v(-61.8, -16.1) * mm, "end": v(-61.58, -16.4) * mm});
            skLineSegment(sketch, "E2296", {"start": v(-61.58, -16.4) * mm, "end": v(-61.58, -16.51) * mm});
            skLineSegment(sketch, "E2297", {"start": v(-59.04, -16.51) * mm, "end": v(-59.04, -16.62) * mm});
            skLineSegment(sketch, "E2298", {"start": v(-59.04, -16.62) * mm, "end": v(-59.26, -16.93) * mm});
            skLineSegment(sketch, "E2299", {"start": v(-59.26, -16.93) * mm, "end": v(-59.3, -16.95) * mm});
            skLineSegment(sketch, "E2300", {"start": v(-59.3, -16.95) * mm, "end": v(-59.33, -16.97) * mm});
            skLineSegment(sketch, "E2301", {"start": v(-59.33, -16.97) * mm, "end": v(-59.76, -16.97) * mm});
            skLineSegment(sketch, "E2302", {"start": v(-59.76, -16.97) * mm, "end": v(-59.8, -16.95) * mm});
            skLineSegment(sketch, "E2303", {"start": v(-59.8, -16.95) * mm, "end": v(-59.84, -16.93) * mm});
            skLineSegment(sketch, "E2304", {"start": v(-59.84, -16.93) * mm, "end": v(-60.06, -16.61) * mm});
            skLineSegment(sketch, "E2305", {"start": v(-60.06, -16.61) * mm, "end": v(-60.06, -16.51) * mm});
            skLineSegment(sketch, "E2306", {"start": v(-60.06, -16.51) * mm, "end": v(-60.06, -16.4) * mm});
            skLineSegment(sketch, "E2307", {"start": v(-60.06, -16.4) * mm, "end": v(-59.84, -16.1) * mm});
            skLineSegment(sketch, "E2308", {"start": v(-59.84, -16.1) * mm, "end": v(-59.8, -16.07) * mm});
            skLineSegment(sketch, "E2309", {"start": v(-59.8, -16.07) * mm, "end": v(-59.76, -16.05) * mm});
            skLineSegment(sketch, "E2310", {"start": v(-59.76, -16.05) * mm, "end": v(-59.33, -16.05) * mm});
            skLineSegment(sketch, "E2311", {"start": v(-59.33, -16.05) * mm, "end": v(-59.3, -16.07) * mm});
            skLineSegment(sketch, "E2312", {"start": v(-59.3, -16.07) * mm, "end": v(-59.26, -16.1) * mm});
            skLineSegment(sketch, "E2313", {"start": v(-59.26, -16.1) * mm, "end": v(-59.04, -16.4) * mm});
            skLineSegment(sketch, "E2314", {"start": v(-59.04, -16.4) * mm, "end": v(-59.04, -16.51) * mm});
            skLineSegment(sketch, "E2315", {"start": v(-61.58, -19.05) * mm, "end": v(-61.58, -19.16) * mm});
            skLineSegment(sketch, "E2316", {"start": v(-61.58, -19.16) * mm, "end": v(-61.8, -19.47) * mm});
            skLineSegment(sketch, "E2317", {"start": v(-61.8, -19.47) * mm, "end": v(-61.83, -19.49) * mm});
            skLineSegment(sketch, "E2318", {"start": v(-61.83, -19.49) * mm, "end": v(-61.87, -19.51) * mm});
            skLineSegment(sketch, "E2319", {"start": v(-61.87, -19.51) * mm, "end": v(-62.3, -19.51) * mm});
            skLineSegment(sketch, "E2320", {"start": v(-62.3, -19.51) * mm, "end": v(-62.34, -19.49) * mm});
            skLineSegment(sketch, "E2321", {"start": v(-62.34, -19.49) * mm, "end": v(-62.38, -19.47) * mm});
            skLineSegment(sketch, "E2322", {"start": v(-62.38, -19.47) * mm, "end": v(-62.6, -19.15) * mm});
            skLineSegment(sketch, "E2323", {"start": v(-62.6, -19.15) * mm, "end": v(-62.6, -19.05) * mm});
            skLineSegment(sketch, "E2324", {"start": v(-62.6, -19.05) * mm, "end": v(-62.6, -18.94) * mm});
            skLineSegment(sketch, "E2325", {"start": v(-62.6, -18.94) * mm, "end": v(-62.38, -18.63) * mm});
            skLineSegment(sketch, "E2326", {"start": v(-62.38, -18.63) * mm, "end": v(-62.34, -18.61) * mm});
            skLineSegment(sketch, "E2327", {"start": v(-62.34, -18.61) * mm, "end": v(-62.3, -18.59) * mm});
            skLineSegment(sketch, "E2328", {"start": v(-62.3, -18.59) * mm, "end": v(-61.87, -18.59) * mm});
            skLineSegment(sketch, "E2329", {"start": v(-61.87, -18.59) * mm, "end": v(-61.83, -18.61) * mm});
            skLineSegment(sketch, "E2330", {"start": v(-61.83, -18.61) * mm, "end": v(-61.8, -18.63) * mm});
            skLineSegment(sketch, "E2331", {"start": v(-61.8, -18.63) * mm, "end": v(-61.58, -18.95) * mm});
            skLineSegment(sketch, "E2332", {"start": v(-61.58, -18.95) * mm, "end": v(-61.58, -19.05) * mm});
            skLineSegment(sketch, "E2333", {"start": v(-59.04, -19.05) * mm, "end": v(-59.04, -19.16) * mm});
            skLineSegment(sketch, "E2334", {"start": v(-59.04, -19.16) * mm, "end": v(-59.26, -19.47) * mm});
            skLineSegment(sketch, "E2335", {"start": v(-59.26, -19.47) * mm, "end": v(-59.3, -19.49) * mm});
            skLineSegment(sketch, "E2336", {"start": v(-59.3, -19.49) * mm, "end": v(-59.33, -19.51) * mm});
            skLineSegment(sketch, "E2337", {"start": v(-59.33, -19.51) * mm, "end": v(-59.76, -19.51) * mm});
            skLineSegment(sketch, "E2338", {"start": v(-59.76, -19.51) * mm, "end": v(-59.8, -19.49) * mm});
            skLineSegment(sketch, "E2339", {"start": v(-59.8, -19.49) * mm, "end": v(-59.84, -19.47) * mm});
            skLineSegment(sketch, "E2340", {"start": v(-59.84, -19.47) * mm, "end": v(-60.06, -19.15) * mm});
            skLineSegment(sketch, "E2341", {"start": v(-60.06, -19.15) * mm, "end": v(-60.06, -19.05) * mm});
            skLineSegment(sketch, "E2342", {"start": v(-60.06, -19.05) * mm, "end": v(-60.06, -18.94) * mm});
            skLineSegment(sketch, "E2343", {"start": v(-60.06, -18.94) * mm, "end": v(-59.84, -18.63) * mm});
            skLineSegment(sketch, "E2344", {"start": v(-59.84, -18.63) * mm, "end": v(-59.8, -18.61) * mm});
            skLineSegment(sketch, "E2345", {"start": v(-59.8, -18.61) * mm, "end": v(-59.76, -18.59) * mm});
            skLineSegment(sketch, "E2346", {"start": v(-59.76, -18.59) * mm, "end": v(-59.33, -18.59) * mm});
            skLineSegment(sketch, "E2347", {"start": v(-59.33, -18.59) * mm, "end": v(-59.3, -18.61) * mm});
            skLineSegment(sketch, "E2348", {"start": v(-59.3, -18.61) * mm, "end": v(-59.26, -18.63) * mm});
            skLineSegment(sketch, "E2349", {"start": v(-59.26, -18.63) * mm, "end": v(-59.04, -18.95) * mm});
            skLineSegment(sketch, "E2350", {"start": v(-59.04, -18.95) * mm, "end": v(-59.04, -19.05) * mm});
            skLineSegment(sketch, "E2351", {"start": v(-61.58, -21.59) * mm, "end": v(-61.58, -21.7) * mm});
            skLineSegment(sketch, "E2352", {"start": v(-61.58, -21.7) * mm, "end": v(-61.8, -22) * mm});
            skLineSegment(sketch, "E2353", {"start": v(-61.8, -22) * mm, "end": v(-61.83, -22.03) * mm});
            skLineSegment(sketch, "E2354", {"start": v(-61.83, -22.03) * mm, "end": v(-61.87, -22.05) * mm});
            skLineSegment(sketch, "E2355", {"start": v(-61.87, -22.05) * mm, "end": v(-62.3, -22.05) * mm});
            skLineSegment(sketch, "E2356", {"start": v(-62.3, -22.05) * mm, "end": v(-62.34, -22.03) * mm});
            skLineSegment(sketch, "E2357", {"start": v(-62.34, -22.03) * mm, "end": v(-62.38, -22) * mm});
            skLineSegment(sketch, "E2358", {"start": v(-62.38, -22) * mm, "end": v(-62.6, -21.7) * mm});
            skLineSegment(sketch, "E2359", {"start": v(-62.6, -21.7) * mm, "end": v(-62.6, -21.59) * mm});
            skLineSegment(sketch, "E2360", {"start": v(-62.6, -21.59) * mm, "end": v(-62.6, -21.48) * mm});
            skLineSegment(sketch, "E2361", {"start": v(-62.6, -21.48) * mm, "end": v(-62.38, -21.17) * mm});
            skLineSegment(sketch, "E2362", {"start": v(-62.38, -21.17) * mm, "end": v(-62.34, -21.15) * mm});
            skLineSegment(sketch, "E2363", {"start": v(-62.34, -21.15) * mm, "end": v(-62.3, -21.13) * mm});
            skLineSegment(sketch, "E2364", {"start": v(-62.3, -21.13) * mm, "end": v(-61.87, -21.13) * mm});
            skLineSegment(sketch, "E2365", {"start": v(-61.87, -21.13) * mm, "end": v(-61.83, -21.15) * mm});
            skLineSegment(sketch, "E2366", {"start": v(-61.83, -21.15) * mm, "end": v(-61.8, -21.17) * mm});
            skLineSegment(sketch, "E2367", {"start": v(-61.8, -21.17) * mm, "end": v(-61.58, -21.48) * mm});
            skLineSegment(sketch, "E2368", {"start": v(-61.58, -21.48) * mm, "end": v(-61.58, -21.59) * mm});
            skLineSegment(sketch, "E2369", {"start": v(-59.04, -21.59) * mm, "end": v(-59.04, -21.7) * mm});
            skLineSegment(sketch, "E2370", {"start": v(-59.04, -21.7) * mm, "end": v(-59.26, -22) * mm});
            skLineSegment(sketch, "E2371", {"start": v(-59.26, -22) * mm, "end": v(-59.3, -22.03) * mm});
            skLineSegment(sketch, "E2372", {"start": v(-59.3, -22.03) * mm, "end": v(-59.33, -22.05) * mm});
            skLineSegment(sketch, "E2373", {"start": v(-59.33, -22.05) * mm, "end": v(-59.76, -22.05) * mm});
            skLineSegment(sketch, "E2374", {"start": v(-59.76, -22.05) * mm, "end": v(-59.8, -22.03) * mm});
            skLineSegment(sketch, "E2375", {"start": v(-59.8, -22.03) * mm, "end": v(-59.84, -22) * mm});
            skLineSegment(sketch, "E2376", {"start": v(-59.84, -22) * mm, "end": v(-60.06, -21.7) * mm});
            skLineSegment(sketch, "E2377", {"start": v(-60.06, -21.7) * mm, "end": v(-60.06, -21.59) * mm});
            skLineSegment(sketch, "E2378", {"start": v(-60.06, -21.59) * mm, "end": v(-60.06, -21.48) * mm});
            skLineSegment(sketch, "E2379", {"start": v(-60.06, -21.48) * mm, "end": v(-59.84, -21.17) * mm});
            skLineSegment(sketch, "E2380", {"start": v(-59.84, -21.17) * mm, "end": v(-59.8, -21.15) * mm});
            skLineSegment(sketch, "E2381", {"start": v(-59.8, -21.15) * mm, "end": v(-59.76, -21.13) * mm});
            skLineSegment(sketch, "E2382", {"start": v(-59.76, -21.13) * mm, "end": v(-59.33, -21.13) * mm});
            skLineSegment(sketch, "E2383", {"start": v(-59.33, -21.13) * mm, "end": v(-59.3, -21.15) * mm});
            skLineSegment(sketch, "E2384", {"start": v(-59.3, -21.15) * mm, "end": v(-59.26, -21.17) * mm});
            skLineSegment(sketch, "E2385", {"start": v(-59.26, -21.17) * mm, "end": v(-59.04, -21.48) * mm});
            skLineSegment(sketch, "E2386", {"start": v(-59.04, -21.48) * mm, "end": v(-59.04, -21.59) * mm});
            skLineSegment(sketch, "E2387", {"start": v(-61.58, -24.13) * mm, "end": v(-61.58, -24.24) * mm});
            skLineSegment(sketch, "E2388", {"start": v(-61.58, -24.24) * mm, "end": v(-61.8, -24.55) * mm});
            skLineSegment(sketch, "E2389", {"start": v(-61.8, -24.55) * mm, "end": v(-61.83, -24.57) * mm});
            skLineSegment(sketch, "E2390", {"start": v(-61.83, -24.57) * mm, "end": v(-61.87, -24.6) * mm});
            skLineSegment(sketch, "E2391", {"start": v(-61.87, -24.6) * mm, "end": v(-62.3, -24.6) * mm});
            skLineSegment(sketch, "E2392", {"start": v(-62.3, -24.6) * mm, "end": v(-62.34, -24.57) * mm});
            skLineSegment(sketch, "E2393", {"start": v(-62.34, -24.57) * mm, "end": v(-62.38, -24.55) * mm});
            skLineSegment(sketch, "E2394", {"start": v(-62.38, -24.55) * mm, "end": v(-62.6, -24.23) * mm});
            skLineSegment(sketch, "E2395", {"start": v(-62.6, -24.23) * mm, "end": v(-62.6, -24.13) * mm});
            skLineSegment(sketch, "E2396", {"start": v(-62.6, -24.13) * mm, "end": v(-62.6, -24.02) * mm});
            skLineSegment(sketch, "E2397", {"start": v(-62.6, -24.02) * mm, "end": v(-62.38, -23.71) * mm});
            skLineSegment(sketch, "E2398", {"start": v(-62.38, -23.71) * mm, "end": v(-62.34, -23.69) * mm});
            skLineSegment(sketch, "E2399", {"start": v(-62.34, -23.69) * mm, "end": v(-62.3, -23.67) * mm});
            skLineSegment(sketch, "E2400", {"start": v(-62.3, -23.67) * mm, "end": v(-61.87, -23.67) * mm});
            skLineSegment(sketch, "E2401", {"start": v(-61.87, -23.67) * mm, "end": v(-61.83, -23.69) * mm});
            skLineSegment(sketch, "E2402", {"start": v(-61.83, -23.69) * mm, "end": v(-61.8, -23.71) * mm});
            skLineSegment(sketch, "E2403", {"start": v(-61.8, -23.71) * mm, "end": v(-61.58, -24.02) * mm});
            skLineSegment(sketch, "E2404", {"start": v(-61.58, -24.02) * mm, "end": v(-61.58, -24.13) * mm});
            skLineSegment(sketch, "E2405", {"start": v(-59.04, -24.13) * mm, "end": v(-59.04, -24.24) * mm});
            skLineSegment(sketch, "E2406", {"start": v(-59.04, -24.24) * mm, "end": v(-59.26, -24.55) * mm});
            skLineSegment(sketch, "E2407", {"start": v(-59.26, -24.55) * mm, "end": v(-59.3, -24.57) * mm});
            skLineSegment(sketch, "E2408", {"start": v(-59.3, -24.57) * mm, "end": v(-59.33, -24.6) * mm});
            skLineSegment(sketch, "E2409", {"start": v(-59.33, -24.6) * mm, "end": v(-59.76, -24.6) * mm});
            skLineSegment(sketch, "E2410", {"start": v(-59.76, -24.6) * mm, "end": v(-59.8, -24.57) * mm});
            skLineSegment(sketch, "E2411", {"start": v(-59.8, -24.57) * mm, "end": v(-59.84, -24.55) * mm});
            skLineSegment(sketch, "E2412", {"start": v(-59.84, -24.55) * mm, "end": v(-60.06, -24.23) * mm});
            skLineSegment(sketch, "E2413", {"start": v(-60.06, -24.23) * mm, "end": v(-60.06, -24.13) * mm});
            skLineSegment(sketch, "E2414", {"start": v(-60.06, -24.13) * mm, "end": v(-60.06, -24.02) * mm});
            skLineSegment(sketch, "E2415", {"start": v(-60.06, -24.02) * mm, "end": v(-59.84, -23.71) * mm});
            skLineSegment(sketch, "E2416", {"start": v(-59.84, -23.71) * mm, "end": v(-59.8, -23.69) * mm});
            skLineSegment(sketch, "E2417", {"start": v(-59.8, -23.69) * mm, "end": v(-59.76, -23.67) * mm});
            skLineSegment(sketch, "E2418", {"start": v(-59.76, -23.67) * mm, "end": v(-59.33, -23.67) * mm});
            skLineSegment(sketch, "E2419", {"start": v(-59.33, -23.67) * mm, "end": v(-59.3, -23.69) * mm});
            skLineSegment(sketch, "E2420", {"start": v(-59.3, -23.69) * mm, "end": v(-59.26, -23.71) * mm});
            skLineSegment(sketch, "E2421", {"start": v(-59.26, -23.71) * mm, "end": v(-59.04, -24.02) * mm});
            skLineSegment(sketch, "E2422", {"start": v(-59.04, -24.02) * mm, "end": v(-59.04, -24.13) * mm});
            skLineSegment(sketch, "E2423", {"start": v(-61.58, -26.67) * mm, "end": v(-61.58, -26.78) * mm});
            skLineSegment(sketch, "E2424", {"start": v(-61.58, -26.78) * mm, "end": v(-61.8, -27.09) * mm});
            skLineSegment(sketch, "E2425", {"start": v(-61.8, -27.09) * mm, "end": v(-61.83, -27.11) * mm});
            skLineSegment(sketch, "E2426", {"start": v(-61.83, -27.11) * mm, "end": v(-61.87, -27.13) * mm});
            skLineSegment(sketch, "E2427", {"start": v(-61.87, -27.13) * mm, "end": v(-62.3, -27.13) * mm});
            skLineSegment(sketch, "E2428", {"start": v(-62.3, -27.13) * mm, "end": v(-62.34, -27.11) * mm});
            skLineSegment(sketch, "E2429", {"start": v(-62.34, -27.11) * mm, "end": v(-62.38, -27.09) * mm});
            skLineSegment(sketch, "E2430", {"start": v(-62.38, -27.09) * mm, "end": v(-62.6, -26.77) * mm});
            skLineSegment(sketch, "E2431", {"start": v(-62.6, -26.77) * mm, "end": v(-62.6, -26.67) * mm});
            skLineSegment(sketch, "E2432", {"start": v(-62.6, -26.67) * mm, "end": v(-62.6, -26.56) * mm});
            skLineSegment(sketch, "E2433", {"start": v(-62.6, -26.56) * mm, "end": v(-62.38, -26.25) * mm});
            skLineSegment(sketch, "E2434", {"start": v(-62.38, -26.25) * mm, "end": v(-62.34, -26.23) * mm});
            skLineSegment(sketch, "E2435", {"start": v(-62.34, -26.23) * mm, "end": v(-62.3, -26.2) * mm});
            skLineSegment(sketch, "E2436", {"start": v(-62.3, -26.2) * mm, "end": v(-61.87, -26.2) * mm});
            skLineSegment(sketch, "E2437", {"start": v(-61.87, -26.2) * mm, "end": v(-61.83, -26.23) * mm});
            skLineSegment(sketch, "E2438", {"start": v(-61.83, -26.23) * mm, "end": v(-61.8, -26.25) * mm});
            skLineSegment(sketch, "E2439", {"start": v(-61.8, -26.25) * mm, "end": v(-61.58, -26.57) * mm});
            skLineSegment(sketch, "E2440", {"start": v(-61.58, -26.57) * mm, "end": v(-61.58, -26.67) * mm});
            skLineSegment(sketch, "E2441", {"start": v(-59.04, -26.67) * mm, "end": v(-59.04, -26.78) * mm});
            skLineSegment(sketch, "E2442", {"start": v(-59.04, -26.78) * mm, "end": v(-59.26, -27.09) * mm});
            skLineSegment(sketch, "E2443", {"start": v(-59.26, -27.09) * mm, "end": v(-59.3, -27.11) * mm});
            skLineSegment(sketch, "E2444", {"start": v(-59.3, -27.11) * mm, "end": v(-59.33, -27.13) * mm});
            skLineSegment(sketch, "E2445", {"start": v(-59.33, -27.13) * mm, "end": v(-59.76, -27.13) * mm});
            skLineSegment(sketch, "E2446", {"start": v(-59.76, -27.13) * mm, "end": v(-59.8, -27.11) * mm});
            skLineSegment(sketch, "E2447", {"start": v(-59.8, -27.11) * mm, "end": v(-59.84, -27.09) * mm});
            skLineSegment(sketch, "E2448", {"start": v(-59.84, -27.09) * mm, "end": v(-60.06, -26.77) * mm});
            skLineSegment(sketch, "E2449", {"start": v(-60.06, -26.77) * mm, "end": v(-60.06, -26.67) * mm});
            skLineSegment(sketch, "E2450", {"start": v(-60.06, -26.67) * mm, "end": v(-60.06, -26.56) * mm});
            skLineSegment(sketch, "E2451", {"start": v(-60.06, -26.56) * mm, "end": v(-59.84, -26.25) * mm});
            skLineSegment(sketch, "E2452", {"start": v(-59.84, -26.25) * mm, "end": v(-59.8, -26.23) * mm});
            skLineSegment(sketch, "E2453", {"start": v(-59.8, -26.23) * mm, "end": v(-59.76, -26.2) * mm});
            skLineSegment(sketch, "E2454", {"start": v(-59.76, -26.2) * mm, "end": v(-59.33, -26.2) * mm});
            skLineSegment(sketch, "E2455", {"start": v(-59.33, -26.2) * mm, "end": v(-59.3, -26.23) * mm});
            skLineSegment(sketch, "E2456", {"start": v(-59.3, -26.23) * mm, "end": v(-59.26, -26.25) * mm});
            skLineSegment(sketch, "E2457", {"start": v(-59.26, -26.25) * mm, "end": v(-59.04, -26.57) * mm});
            skLineSegment(sketch, "E2458", {"start": v(-59.04, -26.57) * mm, "end": v(-59.04, -26.67) * mm});
            skLineSegment(sketch, "E2459", {"start": v(-61.58, -29.21) * mm, "end": v(-61.58, -29.32) * mm});
            skLineSegment(sketch, "E2460", {"start": v(-61.58, -29.32) * mm, "end": v(-61.8, -29.63) * mm});
            skLineSegment(sketch, "E2461", {"start": v(-61.8, -29.63) * mm, "end": v(-61.83, -29.65) * mm});
            skLineSegment(sketch, "E2462", {"start": v(-61.83, -29.65) * mm, "end": v(-61.87, -29.67) * mm});
            skLineSegment(sketch, "E2463", {"start": v(-61.87, -29.67) * mm, "end": v(-62.3, -29.67) * mm});
            skLineSegment(sketch, "E2464", {"start": v(-62.3, -29.67) * mm, "end": v(-62.34, -29.65) * mm});
            skLineSegment(sketch, "E2465", {"start": v(-62.34, -29.65) * mm, "end": v(-62.38, -29.63) * mm});
            skLineSegment(sketch, "E2466", {"start": v(-62.38, -29.63) * mm, "end": v(-62.6, -29.31) * mm});
            skLineSegment(sketch, "E2467", {"start": v(-62.6, -29.31) * mm, "end": v(-62.6, -29.21) * mm});
            skLineSegment(sketch, "E2468", {"start": v(-62.6, -29.21) * mm, "end": v(-62.6, -29.1) * mm});
            skLineSegment(sketch, "E2469", {"start": v(-62.6, -29.1) * mm, "end": v(-62.38, -28.8) * mm});
            skLineSegment(sketch, "E2470", {"start": v(-62.38, -28.8) * mm, "end": v(-62.34, -28.77) * mm});
            skLineSegment(sketch, "E2471", {"start": v(-62.34, -28.77) * mm, "end": v(-62.3, -28.75) * mm});
            skLineSegment(sketch, "E2472", {"start": v(-62.3, -28.75) * mm, "end": v(-61.87, -28.75) * mm});
            skLineSegment(sketch, "E2473", {"start": v(-61.87, -28.75) * mm, "end": v(-61.83, -28.77) * mm});
            skLineSegment(sketch, "E2474", {"start": v(-61.83, -28.77) * mm, "end": v(-61.8, -28.8) * mm});
            skLineSegment(sketch, "E2475", {"start": v(-61.8, -28.8) * mm, "end": v(-61.58, -29.1) * mm});
            skLineSegment(sketch, "E2476", {"start": v(-61.58, -29.1) * mm, "end": v(-61.58, -29.21) * mm});
            skLineSegment(sketch, "E2477", {"start": v(-59.04, -29.21) * mm, "end": v(-59.04, -29.32) * mm});
            skLineSegment(sketch, "E2478", {"start": v(-59.04, -29.32) * mm, "end": v(-59.26, -29.63) * mm});
            skLineSegment(sketch, "E2479", {"start": v(-59.26, -29.63) * mm, "end": v(-59.3, -29.65) * mm});
            skLineSegment(sketch, "E2480", {"start": v(-59.3, -29.65) * mm, "end": v(-59.33, -29.67) * mm});
            skLineSegment(sketch, "E2481", {"start": v(-59.33, -29.67) * mm, "end": v(-59.76, -29.67) * mm});
            skLineSegment(sketch, "E2482", {"start": v(-59.76, -29.67) * mm, "end": v(-59.8, -29.65) * mm});
            skLineSegment(sketch, "E2483", {"start": v(-59.8, -29.65) * mm, "end": v(-59.84, -29.63) * mm});
            skLineSegment(sketch, "E2484", {"start": v(-59.84, -29.63) * mm, "end": v(-60.06, -29.31) * mm});
            skLineSegment(sketch, "E2485", {"start": v(-60.06, -29.31) * mm, "end": v(-60.06, -29.21) * mm});
            skLineSegment(sketch, "E2486", {"start": v(-60.06, -29.21) * mm, "end": v(-60.06, -29.1) * mm});
            skLineSegment(sketch, "E2487", {"start": v(-60.06, -29.1) * mm, "end": v(-59.84, -28.8) * mm});
            skLineSegment(sketch, "E2488", {"start": v(-59.84, -28.8) * mm, "end": v(-59.8, -28.77) * mm});
            skLineSegment(sketch, "E2489", {"start": v(-59.8, -28.77) * mm, "end": v(-59.76, -28.75) * mm});
            skLineSegment(sketch, "E2490", {"start": v(-59.76, -28.75) * mm, "end": v(-59.33, -28.75) * mm});
            skLineSegment(sketch, "E2491", {"start": v(-59.33, -28.75) * mm, "end": v(-59.3, -28.77) * mm});
            skLineSegment(sketch, "E2492", {"start": v(-59.3, -28.77) * mm, "end": v(-59.26, -28.8) * mm});
            skLineSegment(sketch, "E2493", {"start": v(-59.26, -28.8) * mm, "end": v(-59.04, -29.1) * mm});
            skLineSegment(sketch, "E2494", {"start": v(-59.04, -29.1) * mm, "end": v(-59.04, -29.21) * mm});
            skLineSegment(sketch, "E2495", {"start": v(-61.58, -31.75) * mm, "end": v(-61.58, -31.86) * mm});
            skLineSegment(sketch, "E2496", {"start": v(-61.58, -31.86) * mm, "end": v(-61.8, -32.17) * mm});
            skLineSegment(sketch, "E2497", {"start": v(-61.8, -32.17) * mm, "end": v(-61.83, -32.19) * mm});
            skLineSegment(sketch, "E2498", {"start": v(-61.83, -32.19) * mm, "end": v(-61.87, -32.21) * mm});
            skLineSegment(sketch, "E2499", {"start": v(-61.87, -32.21) * mm, "end": v(-62.3, -32.21) * mm});
            skLineSegment(sketch, "E2500", {"start": v(-62.3, -32.21) * mm, "end": v(-62.34, -32.19) * mm});
            skLineSegment(sketch, "E2501", {"start": v(-62.34, -32.19) * mm, "end": v(-62.38, -32.17) * mm});
            skLineSegment(sketch, "E2502", {"start": v(-62.38, -32.17) * mm, "end": v(-62.6, -31.85) * mm});
            skLineSegment(sketch, "E2503", {"start": v(-62.6, -31.85) * mm, "end": v(-62.6, -31.75) * mm});
            skLineSegment(sketch, "E2504", {"start": v(-62.6, -31.75) * mm, "end": v(-62.6, -31.64) * mm});
            skLineSegment(sketch, "E2505", {"start": v(-62.6, -31.64) * mm, "end": v(-62.38, -31.33) * mm});
            skLineSegment(sketch, "E2506", {"start": v(-62.38, -31.33) * mm, "end": v(-62.34, -31.31) * mm});
            skLineSegment(sketch, "E2507", {"start": v(-62.34, -31.31) * mm, "end": v(-62.3, -31.29) * mm});
            skLineSegment(sketch, "E2508", {"start": v(-62.3, -31.29) * mm, "end": v(-61.87, -31.29) * mm});
            skLineSegment(sketch, "E2509", {"start": v(-61.87, -31.29) * mm, "end": v(-61.83, -31.31) * mm});
            skLineSegment(sketch, "E2510", {"start": v(-61.83, -31.31) * mm, "end": v(-61.8, -31.33) * mm});
            skLineSegment(sketch, "E2511", {"start": v(-61.8, -31.33) * mm, "end": v(-61.58, -31.65) * mm});
            skLineSegment(sketch, "E2512", {"start": v(-61.58, -31.65) * mm, "end": v(-61.58, -31.75) * mm});
            skLineSegment(sketch, "E2513", {"start": v(-59.04, -31.75) * mm, "end": v(-59.04, -31.86) * mm});
            skLineSegment(sketch, "E2514", {"start": v(-59.04, -31.86) * mm, "end": v(-59.26, -32.17) * mm});
            skLineSegment(sketch, "E2515", {"start": v(-59.26, -32.17) * mm, "end": v(-59.3, -32.19) * mm});
            skLineSegment(sketch, "E2516", {"start": v(-59.3, -32.19) * mm, "end": v(-59.33, -32.21) * mm});
            skLineSegment(sketch, "E2517", {"start": v(-59.33, -32.21) * mm, "end": v(-59.76, -32.21) * mm});
            skLineSegment(sketch, "E2518", {"start": v(-59.76, -32.21) * mm, "end": v(-59.8, -32.19) * mm});
            skLineSegment(sketch, "E2519", {"start": v(-59.8, -32.19) * mm, "end": v(-59.84, -32.17) * mm});
            skLineSegment(sketch, "E2520", {"start": v(-59.84, -32.17) * mm, "end": v(-60.06, -31.85) * mm});
            skLineSegment(sketch, "E2521", {"start": v(-60.06, -31.85) * mm, "end": v(-60.06, -31.75) * mm});
            skLineSegment(sketch, "E2522", {"start": v(-60.06, -31.75) * mm, "end": v(-60.06, -31.64) * mm});
            skLineSegment(sketch, "E2523", {"start": v(-60.06, -31.64) * mm, "end": v(-59.84, -31.33) * mm});
            skLineSegment(sketch, "E2524", {"start": v(-59.84, -31.33) * mm, "end": v(-59.8, -31.31) * mm});
            skLineSegment(sketch, "E2525", {"start": v(-59.8, -31.31) * mm, "end": v(-59.76, -31.29) * mm});
            skLineSegment(sketch, "E2526", {"start": v(-59.76, -31.29) * mm, "end": v(-59.33, -31.29) * mm});
            skLineSegment(sketch, "E2527", {"start": v(-59.33, -31.29) * mm, "end": v(-59.3, -31.31) * mm});
            skLineSegment(sketch, "E2528", {"start": v(-59.3, -31.31) * mm, "end": v(-59.26, -31.33) * mm});
            skLineSegment(sketch, "E2529", {"start": v(-59.26, -31.33) * mm, "end": v(-59.04, -31.65) * mm});
            skLineSegment(sketch, "E2530", {"start": v(-59.04, -31.65) * mm, "end": v(-59.04, -31.75) * mm});
            skLineSegment(sketch, "E2531", {"start": v(-61.58, -34.29) * mm, "end": v(-61.58, -34.4) * mm});
            skLineSegment(sketch, "E2532", {"start": v(-61.58, -34.4) * mm, "end": v(-61.8, -34.7) * mm});
            skLineSegment(sketch, "E2533", {"start": v(-61.8, -34.7) * mm, "end": v(-61.83, -34.73) * mm});
            skLineSegment(sketch, "E2534", {"start": v(-61.83, -34.73) * mm, "end": v(-61.87, -34.75) * mm});
            skLineSegment(sketch, "E2535", {"start": v(-61.87, -34.75) * mm, "end": v(-62.3, -34.75) * mm});
            skLineSegment(sketch, "E2536", {"start": v(-62.3, -34.75) * mm, "end": v(-62.34, -34.73) * mm});
            skLineSegment(sketch, "E2537", {"start": v(-62.34, -34.73) * mm, "end": v(-62.38, -34.7) * mm});
            skLineSegment(sketch, "E2538", {"start": v(-62.38, -34.7) * mm, "end": v(-62.6, -34.4) * mm});
            skLineSegment(sketch, "E2539", {"start": v(-62.6, -34.4) * mm, "end": v(-62.6, -34.29) * mm});
            skLineSegment(sketch, "E2540", {"start": v(-62.6, -34.29) * mm, "end": v(-62.6, -34.18) * mm});
            skLineSegment(sketch, "E2541", {"start": v(-62.6, -34.18) * mm, "end": v(-62.38, -33.87) * mm});
            skLineSegment(sketch, "E2542", {"start": v(-62.38, -33.87) * mm, "end": v(-62.34, -33.85) * mm});
            skLineSegment(sketch, "E2543", {"start": v(-62.34, -33.85) * mm, "end": v(-62.3, -33.83) * mm});
            skLineSegment(sketch, "E2544", {"start": v(-62.3, -33.83) * mm, "end": v(-61.87, -33.83) * mm});
            skLineSegment(sketch, "E2545", {"start": v(-61.87, -33.83) * mm, "end": v(-61.83, -33.85) * mm});
            skLineSegment(sketch, "E2546", {"start": v(-61.83, -33.85) * mm, "end": v(-61.8, -33.87) * mm});
            skLineSegment(sketch, "E2547", {"start": v(-61.8, -33.87) * mm, "end": v(-61.58, -34.19) * mm});
            skLineSegment(sketch, "E2548", {"start": v(-61.58, -34.19) * mm, "end": v(-61.58, -34.29) * mm});
            skLineSegment(sketch, "E2549", {"start": v(-59.04, -34.29) * mm, "end": v(-59.04, -34.4) * mm});
            skLineSegment(sketch, "E2550", {"start": v(-59.04, -34.4) * mm, "end": v(-59.26, -34.7) * mm});
            skLineSegment(sketch, "E2551", {"start": v(-59.26, -34.7) * mm, "end": v(-59.3, -34.73) * mm});
            skLineSegment(sketch, "E2552", {"start": v(-59.3, -34.73) * mm, "end": v(-59.33, -34.75) * mm});
            skLineSegment(sketch, "E2553", {"start": v(-59.33, -34.75) * mm, "end": v(-59.76, -34.75) * mm});
            skLineSegment(sketch, "E2554", {"start": v(-59.76, -34.75) * mm, "end": v(-59.8, -34.73) * mm});
            skLineSegment(sketch, "E2555", {"start": v(-59.8, -34.73) * mm, "end": v(-59.84, -34.7) * mm});
            skLineSegment(sketch, "E2556", {"start": v(-59.84, -34.7) * mm, "end": v(-60.06, -34.4) * mm});
            skLineSegment(sketch, "E2557", {"start": v(-60.06, -34.4) * mm, "end": v(-60.06, -34.29) * mm});
            skLineSegment(sketch, "E2558", {"start": v(-60.06, -34.29) * mm, "end": v(-60.06, -34.18) * mm});
            skLineSegment(sketch, "E2559", {"start": v(-60.06, -34.18) * mm, "end": v(-59.84, -33.87) * mm});
            skLineSegment(sketch, "E2560", {"start": v(-59.84, -33.87) * mm, "end": v(-59.8, -33.85) * mm});
            skLineSegment(sketch, "E2561", {"start": v(-59.8, -33.85) * mm, "end": v(-59.76, -33.83) * mm});
            skLineSegment(sketch, "E2562", {"start": v(-59.76, -33.83) * mm, "end": v(-59.33, -33.83) * mm});
            skLineSegment(sketch, "E2563", {"start": v(-59.33, -33.83) * mm, "end": v(-59.3, -33.85) * mm});
            skLineSegment(sketch, "E2564", {"start": v(-59.3, -33.85) * mm, "end": v(-59.26, -33.87) * mm});
            skLineSegment(sketch, "E2565", {"start": v(-59.26, -33.87) * mm, "end": v(-59.04, -34.19) * mm});
            skLineSegment(sketch, "E2566", {"start": v(-59.04, -34.19) * mm, "end": v(-59.04, -34.29) * mm});
            skLineSegment(sketch, "E2567", {"start": v(-61.58, -36.83) * mm, "end": v(-61.58, -36.94) * mm});
            skLineSegment(sketch, "E2568", {"start": v(-61.58, -36.94) * mm, "end": v(-61.8, -37.25) * mm});
            skLineSegment(sketch, "E2569", {"start": v(-61.8, -37.25) * mm, "end": v(-61.83, -37.27) * mm});
            skLineSegment(sketch, "E2570", {"start": v(-61.83, -37.27) * mm, "end": v(-61.87, -37.3) * mm});
            skLineSegment(sketch, "E2571", {"start": v(-61.87, -37.3) * mm, "end": v(-62.3, -37.3) * mm});
            skLineSegment(sketch, "E2572", {"start": v(-62.3, -37.3) * mm, "end": v(-62.34, -37.27) * mm});
            skLineSegment(sketch, "E2573", {"start": v(-62.34, -37.27) * mm, "end": v(-62.38, -37.25) * mm});
            skLineSegment(sketch, "E2574", {"start": v(-62.38, -37.25) * mm, "end": v(-62.6, -36.93) * mm});
            skLineSegment(sketch, "E2575", {"start": v(-62.6, -36.93) * mm, "end": v(-62.6, -36.83) * mm});
            skLineSegment(sketch, "E2576", {"start": v(-62.6, -36.83) * mm, "end": v(-62.6, -36.72) * mm});
            skLineSegment(sketch, "E2577", {"start": v(-62.6, -36.72) * mm, "end": v(-62.38, -36.41) * mm});
            skLineSegment(sketch, "E2578", {"start": v(-62.38, -36.41) * mm, "end": v(-62.34, -36.39) * mm});
            skLineSegment(sketch, "E2579", {"start": v(-62.34, -36.39) * mm, "end": v(-62.3, -36.37) * mm});
            skLineSegment(sketch, "E2580", {"start": v(-62.3, -36.37) * mm, "end": v(-61.87, -36.37) * mm});
            skLineSegment(sketch, "E2581", {"start": v(-61.87, -36.37) * mm, "end": v(-61.83, -36.39) * mm});
            skLineSegment(sketch, "E2582", {"start": v(-61.83, -36.39) * mm, "end": v(-61.8, -36.41) * mm});
            skLineSegment(sketch, "E2583", {"start": v(-61.8, -36.41) * mm, "end": v(-61.58, -36.72) * mm});
            skLineSegment(sketch, "E2584", {"start": v(-61.58, -36.72) * mm, "end": v(-61.58, -36.83) * mm});
            skLineSegment(sketch, "E2585", {"start": v(-59.04, -36.83) * mm, "end": v(-59.04, -36.94) * mm});
            skLineSegment(sketch, "E2586", {"start": v(-59.04, -36.94) * mm, "end": v(-59.26, -37.25) * mm});
            skLineSegment(sketch, "E2587", {"start": v(-59.26, -37.25) * mm, "end": v(-59.3, -37.27) * mm});
            skLineSegment(sketch, "E2588", {"start": v(-59.3, -37.27) * mm, "end": v(-59.33, -37.3) * mm});
            skLineSegment(sketch, "E2589", {"start": v(-59.33, -37.3) * mm, "end": v(-59.76, -37.3) * mm});
            skLineSegment(sketch, "E2590", {"start": v(-59.76, -37.3) * mm, "end": v(-59.8, -37.27) * mm});
            skLineSegment(sketch, "E2591", {"start": v(-59.8, -37.27) * mm, "end": v(-59.84, -37.25) * mm});
            skLineSegment(sketch, "E2592", {"start": v(-59.84, -37.25) * mm, "end": v(-60.06, -36.93) * mm});
            skLineSegment(sketch, "E2593", {"start": v(-60.06, -36.93) * mm, "end": v(-60.06, -36.83) * mm});
            skLineSegment(sketch, "E2594", {"start": v(-60.06, -36.83) * mm, "end": v(-60.06, -36.72) * mm});
            skLineSegment(sketch, "E2595", {"start": v(-60.06, -36.72) * mm, "end": v(-59.84, -36.41) * mm});
            skLineSegment(sketch, "E2596", {"start": v(-59.84, -36.41) * mm, "end": v(-59.8, -36.39) * mm});
            skLineSegment(sketch, "E2597", {"start": v(-59.8, -36.39) * mm, "end": v(-59.76, -36.37) * mm});
            skLineSegment(sketch, "E2598", {"start": v(-59.76, -36.37) * mm, "end": v(-59.33, -36.37) * mm});
            skLineSegment(sketch, "E2599", {"start": v(-59.33, -36.37) * mm, "end": v(-59.3, -36.39) * mm});
            skLineSegment(sketch, "E2600", {"start": v(-59.3, -36.39) * mm, "end": v(-59.26, -36.41) * mm});
            skLineSegment(sketch, "E2601", {"start": v(-59.26, -36.41) * mm, "end": v(-59.04, -36.72) * mm});
            skLineSegment(sketch, "E2602", {"start": v(-59.04, -36.72) * mm, "end": v(-59.04, -36.83) * mm});
            skLineSegment(sketch, "E2603", {"start": v(-61.58, -39.37) * mm, "end": v(-61.58, -39.48) * mm});
            skLineSegment(sketch, "E2604", {"start": v(-61.58, -39.48) * mm, "end": v(-61.8, -39.79) * mm});
            skLineSegment(sketch, "E2605", {"start": v(-61.8, -39.79) * mm, "end": v(-61.83, -39.81) * mm});
            skLineSegment(sketch, "E2606", {"start": v(-61.83, -39.81) * mm, "end": v(-61.87, -39.83) * mm});
            skLineSegment(sketch, "E2607", {"start": v(-61.87, -39.83) * mm, "end": v(-62.3, -39.83) * mm});
            skLineSegment(sketch, "E2608", {"start": v(-62.3, -39.83) * mm, "end": v(-62.34, -39.81) * mm});
            skLineSegment(sketch, "E2609", {"start": v(-62.34, -39.81) * mm, "end": v(-62.38, -39.79) * mm});
            skLineSegment(sketch, "E2610", {"start": v(-62.38, -39.79) * mm, "end": v(-62.6, -39.47) * mm});
            skLineSegment(sketch, "E2611", {"start": v(-62.6, -39.47) * mm, "end": v(-62.6, -39.37) * mm});
            skLineSegment(sketch, "E2612", {"start": v(-62.6, -39.37) * mm, "end": v(-62.6, -39.26) * mm});
            skLineSegment(sketch, "E2613", {"start": v(-62.6, -39.26) * mm, "end": v(-62.38, -38.95) * mm});
            skLineSegment(sketch, "E2614", {"start": v(-62.38, -38.95) * mm, "end": v(-62.34, -38.93) * mm});
            skLineSegment(sketch, "E2615", {"start": v(-62.34, -38.93) * mm, "end": v(-62.3, -38.9) * mm});
            skLineSegment(sketch, "E2616", {"start": v(-62.3, -38.9) * mm, "end": v(-61.87, -38.9) * mm});
            skLineSegment(sketch, "E2617", {"start": v(-61.87, -38.9) * mm, "end": v(-61.83, -38.93) * mm});
            skLineSegment(sketch, "E2618", {"start": v(-61.83, -38.93) * mm, "end": v(-61.8, -38.95) * mm});
            skLineSegment(sketch, "E2619", {"start": v(-61.8, -38.95) * mm, "end": v(-61.58, -39.27) * mm});
            skLineSegment(sketch, "E2620", {"start": v(-61.58, -39.27) * mm, "end": v(-61.58, -39.37) * mm});
            skLineSegment(sketch, "E2621", {"start": v(-59.04, -39.37) * mm, "end": v(-59.04, -39.48) * mm});
            skLineSegment(sketch, "E2622", {"start": v(-59.04, -39.48) * mm, "end": v(-59.26, -39.79) * mm});
            skLineSegment(sketch, "E2623", {"start": v(-59.26, -39.79) * mm, "end": v(-59.3, -39.81) * mm});
            skLineSegment(sketch, "E2624", {"start": v(-59.3, -39.81) * mm, "end": v(-59.33, -39.83) * mm});
            skLineSegment(sketch, "E2625", {"start": v(-59.33, -39.83) * mm, "end": v(-59.76, -39.83) * mm});
            skLineSegment(sketch, "E2626", {"start": v(-59.76, -39.83) * mm, "end": v(-59.8, -39.81) * mm});
            skLineSegment(sketch, "E2627", {"start": v(-59.8, -39.81) * mm, "end": v(-59.84, -39.79) * mm});
            skLineSegment(sketch, "E2628", {"start": v(-59.84, -39.79) * mm, "end": v(-60.06, -39.47) * mm});
            skLineSegment(sketch, "E2629", {"start": v(-60.06, -39.47) * mm, "end": v(-60.06, -39.37) * mm});
            skLineSegment(sketch, "E2630", {"start": v(-60.06, -39.37) * mm, "end": v(-60.06, -39.26) * mm});
            skLineSegment(sketch, "E2631", {"start": v(-60.06, -39.26) * mm, "end": v(-59.84, -38.95) * mm});
            skLineSegment(sketch, "E2632", {"start": v(-59.84, -38.95) * mm, "end": v(-59.8, -38.93) * mm});
            skLineSegment(sketch, "E2633", {"start": v(-59.8, -38.93) * mm, "end": v(-59.76, -38.9) * mm});
            skLineSegment(sketch, "E2634", {"start": v(-59.76, -38.9) * mm, "end": v(-59.33, -38.9) * mm});
            skLineSegment(sketch, "E2635", {"start": v(-59.33, -38.9) * mm, "end": v(-59.3, -38.93) * mm});
            skLineSegment(sketch, "E2636", {"start": v(-59.3, -38.93) * mm, "end": v(-59.26, -38.95) * mm});
            skLineSegment(sketch, "E2637", {"start": v(-59.26, -38.95) * mm, "end": v(-59.04, -39.27) * mm});
            skLineSegment(sketch, "E2638", {"start": v(-59.04, -39.27) * mm, "end": v(-59.04, -39.37) * mm});
            skLineSegment(sketch, "E2639", {"start": v(-61.58, -41.91) * mm, "end": v(-61.58, -42.02) * mm});
            skLineSegment(sketch, "E2640", {"start": v(-61.58, -42.02) * mm, "end": v(-61.8, -42.33) * mm});
            skLineSegment(sketch, "E2641", {"start": v(-61.8, -42.33) * mm, "end": v(-61.83, -42.35) * mm});
            skLineSegment(sketch, "E2642", {"start": v(-61.83, -42.35) * mm, "end": v(-61.87, -42.37) * mm});
            skLineSegment(sketch, "E2643", {"start": v(-61.87, -42.37) * mm, "end": v(-62.3, -42.37) * mm});
            skLineSegment(sketch, "E2644", {"start": v(-62.3, -42.37) * mm, "end": v(-62.34, -42.35) * mm});
            skLineSegment(sketch, "E2645", {"start": v(-62.34, -42.35) * mm, "end": v(-62.38, -42.33) * mm});
            skLineSegment(sketch, "E2646", {"start": v(-62.38, -42.33) * mm, "end": v(-62.6, -42.01) * mm});
            skLineSegment(sketch, "E2647", {"start": v(-62.6, -42.01) * mm, "end": v(-62.6, -41.91) * mm});
            skLineSegment(sketch, "E2648", {"start": v(-62.6, -41.91) * mm, "end": v(-62.6, -41.8) * mm});
            skLineSegment(sketch, "E2649", {"start": v(-62.6, -41.8) * mm, "end": v(-62.38, -41.5) * mm});
            skLineSegment(sketch, "E2650", {"start": v(-62.38, -41.5) * mm, "end": v(-62.34, -41.47) * mm});
            skLineSegment(sketch, "E2651", {"start": v(-62.34, -41.47) * mm, "end": v(-62.3, -41.45) * mm});
            skLineSegment(sketch, "E2652", {"start": v(-62.3, -41.45) * mm, "end": v(-61.87, -41.45) * mm});
            skLineSegment(sketch, "E2653", {"start": v(-61.87, -41.45) * mm, "end": v(-61.83, -41.47) * mm});
            skLineSegment(sketch, "E2654", {"start": v(-61.83, -41.47) * mm, "end": v(-61.8, -41.5) * mm});
            skLineSegment(sketch, "E2655", {"start": v(-61.8, -41.5) * mm, "end": v(-61.58, -41.8) * mm});
            skLineSegment(sketch, "E2656", {"start": v(-61.58, -41.8) * mm, "end": v(-61.58, -41.91) * mm});
            skLineSegment(sketch, "E2657", {"start": v(-59.04, -41.91) * mm, "end": v(-59.04, -42.02) * mm});
            skLineSegment(sketch, "E2658", {"start": v(-59.04, -42.02) * mm, "end": v(-59.26, -42.33) * mm});
            skLineSegment(sketch, "E2659", {"start": v(-59.26, -42.33) * mm, "end": v(-59.3, -42.35) * mm});
            skLineSegment(sketch, "E2660", {"start": v(-59.3, -42.35) * mm, "end": v(-59.33, -42.37) * mm});
            skLineSegment(sketch, "E2661", {"start": v(-59.33, -42.37) * mm, "end": v(-59.76, -42.37) * mm});
            skLineSegment(sketch, "E2662", {"start": v(-59.76, -42.37) * mm, "end": v(-59.8, -42.35) * mm});
            skLineSegment(sketch, "E2663", {"start": v(-59.8, -42.35) * mm, "end": v(-59.84, -42.33) * mm});
            skLineSegment(sketch, "E2664", {"start": v(-59.84, -42.33) * mm, "end": v(-60.06, -42.01) * mm});
            skLineSegment(sketch, "E2665", {"start": v(-60.06, -42.01) * mm, "end": v(-60.06, -41.91) * mm});
            skLineSegment(sketch, "E2666", {"start": v(-60.06, -41.91) * mm, "end": v(-60.06, -41.8) * mm});
            skLineSegment(sketch, "E2667", {"start": v(-60.06, -41.8) * mm, "end": v(-59.84, -41.5) * mm});
            skLineSegment(sketch, "E2668", {"start": v(-59.84, -41.5) * mm, "end": v(-59.8, -41.47) * mm});
            skLineSegment(sketch, "E2669", {"start": v(-59.8, -41.47) * mm, "end": v(-59.76, -41.45) * mm});
            skLineSegment(sketch, "E2670", {"start": v(-59.76, -41.45) * mm, "end": v(-59.33, -41.45) * mm});
            skLineSegment(sketch, "E2671", {"start": v(-59.33, -41.45) * mm, "end": v(-59.3, -41.47) * mm});
            skLineSegment(sketch, "E2672", {"start": v(-59.3, -41.47) * mm, "end": v(-59.26, -41.5) * mm});
            skLineSegment(sketch, "E2673", {"start": v(-59.26, -41.5) * mm, "end": v(-59.04, -41.8) * mm});
            skLineSegment(sketch, "E2674", {"start": v(-59.04, -41.8) * mm, "end": v(-59.04, -41.91) * mm});
            skLineSegment(sketch, "E2675", {"start": v(-61.58, -44.45) * mm, "end": v(-61.58, -44.56) * mm});
            skLineSegment(sketch, "E2676", {"start": v(-61.58, -44.56) * mm, "end": v(-61.8, -44.87) * mm});
            skLineSegment(sketch, "E2677", {"start": v(-61.8, -44.87) * mm, "end": v(-61.83, -44.89) * mm});
            skLineSegment(sketch, "E2678", {"start": v(-61.83, -44.89) * mm, "end": v(-61.87, -44.91) * mm});
            skLineSegment(sketch, "E2679", {"start": v(-61.87, -44.91) * mm, "end": v(-62.3, -44.91) * mm});
            skLineSegment(sketch, "E2680", {"start": v(-62.3, -44.91) * mm, "end": v(-62.34, -44.89) * mm});
            skLineSegment(sketch, "E2681", {"start": v(-62.34, -44.89) * mm, "end": v(-62.38, -44.87) * mm});
            skLineSegment(sketch, "E2682", {"start": v(-62.38, -44.87) * mm, "end": v(-62.6, -44.55) * mm});
            skLineSegment(sketch, "E2683", {"start": v(-62.6, -44.55) * mm, "end": v(-62.6, -44.45) * mm});
            skLineSegment(sketch, "E2684", {"start": v(-62.6, -44.45) * mm, "end": v(-62.6, -44.34) * mm});
            skLineSegment(sketch, "E2685", {"start": v(-62.6, -44.34) * mm, "end": v(-62.38, -44.03) * mm});
            skLineSegment(sketch, "E2686", {"start": v(-62.38, -44.03) * mm, "end": v(-62.34, -44.01) * mm});
            skLineSegment(sketch, "E2687", {"start": v(-62.34, -44.01) * mm, "end": v(-62.3, -43.99) * mm});
            skLineSegment(sketch, "E2688", {"start": v(-62.3, -43.99) * mm, "end": v(-61.87, -43.99) * mm});
            skLineSegment(sketch, "E2689", {"start": v(-61.87, -43.99) * mm, "end": v(-61.83, -44.01) * mm});
            skLineSegment(sketch, "E2690", {"start": v(-61.83, -44.01) * mm, "end": v(-61.8, -44.03) * mm});
            skLineSegment(sketch, "E2691", {"start": v(-61.8, -44.03) * mm, "end": v(-61.58, -44.35) * mm});
            skLineSegment(sketch, "E2692", {"start": v(-61.58, -44.35) * mm, "end": v(-61.58, -44.45) * mm});
            skLineSegment(sketch, "E2693", {"start": v(-59.04, -44.45) * mm, "end": v(-59.04, -44.56) * mm});
            skLineSegment(sketch, "E2694", {"start": v(-59.04, -44.56) * mm, "end": v(-59.26, -44.87) * mm});
            skLineSegment(sketch, "E2695", {"start": v(-59.26, -44.87) * mm, "end": v(-59.3, -44.89) * mm});
            skLineSegment(sketch, "E2696", {"start": v(-59.3, -44.89) * mm, "end": v(-59.33, -44.91) * mm});
            skLineSegment(sketch, "E2697", {"start": v(-59.33, -44.91) * mm, "end": v(-59.76, -44.91) * mm});
            skLineSegment(sketch, "E2698", {"start": v(-59.76, -44.91) * mm, "end": v(-59.8, -44.89) * mm});
            skLineSegment(sketch, "E2699", {"start": v(-59.8, -44.89) * mm, "end": v(-59.84, -44.87) * mm});
            skLineSegment(sketch, "E2700", {"start": v(-59.84, -44.87) * mm, "end": v(-60.06, -44.55) * mm});
            skLineSegment(sketch, "E2701", {"start": v(-60.06, -44.55) * mm, "end": v(-60.06, -44.45) * mm});
            skLineSegment(sketch, "E2702", {"start": v(-60.06, -44.45) * mm, "end": v(-60.06, -44.34) * mm});
            skLineSegment(sketch, "E2703", {"start": v(-60.06, -44.34) * mm, "end": v(-59.84, -44.03) * mm});
            skLineSegment(sketch, "E2704", {"start": v(-59.84, -44.03) * mm, "end": v(-59.8, -44.01) * mm});
            skLineSegment(sketch, "E2705", {"start": v(-59.8, -44.01) * mm, "end": v(-59.76, -43.99) * mm});
            skLineSegment(sketch, "E2706", {"start": v(-59.76, -43.99) * mm, "end": v(-59.33, -43.99) * mm});
            skLineSegment(sketch, "E2707", {"start": v(-59.33, -43.99) * mm, "end": v(-59.3, -44.01) * mm});
            skLineSegment(sketch, "E2708", {"start": v(-59.3, -44.01) * mm, "end": v(-59.26, -44.03) * mm});
            skLineSegment(sketch, "E2709", {"start": v(-59.26, -44.03) * mm, "end": v(-59.04, -44.35) * mm});
            skLineSegment(sketch, "E2710", {"start": v(-59.04, -44.35) * mm, "end": v(-59.04, -44.45) * mm});
            skLineSegment(sketch, "E2711", {"start": v(-61.58, -46.99) * mm, "end": v(-61.58, -47.1) * mm});
            skLineSegment(sketch, "E2712", {"start": v(-61.58, -47.1) * mm, "end": v(-61.8, -47.4) * mm});
            skLineSegment(sketch, "E2713", {"start": v(-61.8, -47.4) * mm, "end": v(-61.83, -47.43) * mm});
            skLineSegment(sketch, "E2714", {"start": v(-61.83, -47.43) * mm, "end": v(-61.87, -47.45) * mm});
            skLineSegment(sketch, "E2715", {"start": v(-61.87, -47.45) * mm, "end": v(-62.3, -47.45) * mm});
            skLineSegment(sketch, "E2716", {"start": v(-62.3, -47.45) * mm, "end": v(-62.34, -47.43) * mm});
            skLineSegment(sketch, "E2717", {"start": v(-62.34, -47.43) * mm, "end": v(-62.38, -47.4) * mm});
            skLineSegment(sketch, "E2718", {"start": v(-62.38, -47.4) * mm, "end": v(-62.6, -47.1) * mm});
            skLineSegment(sketch, "E2719", {"start": v(-62.6, -47.1) * mm, "end": v(-62.6, -46.99) * mm});
            skLineSegment(sketch, "E2720", {"start": v(-62.6, -46.99) * mm, "end": v(-62.6, -46.88) * mm});
            skLineSegment(sketch, "E2721", {"start": v(-62.6, -46.88) * mm, "end": v(-62.38, -46.57) * mm});
            skLineSegment(sketch, "E2722", {"start": v(-62.38, -46.57) * mm, "end": v(-62.34, -46.55) * mm});
            skLineSegment(sketch, "E2723", {"start": v(-62.34, -46.55) * mm, "end": v(-62.3, -46.53) * mm});
            skLineSegment(sketch, "E2724", {"start": v(-62.3, -46.53) * mm, "end": v(-61.87, -46.53) * mm});
            skLineSegment(sketch, "E2725", {"start": v(-61.87, -46.53) * mm, "end": v(-61.83, -46.55) * mm});
            skLineSegment(sketch, "E2726", {"start": v(-61.83, -46.55) * mm, "end": v(-61.8, -46.57) * mm});
            skLineSegment(sketch, "E2727", {"start": v(-61.8, -46.57) * mm, "end": v(-61.58, -46.88) * mm});
            skLineSegment(sketch, "E2728", {"start": v(-61.58, -46.88) * mm, "end": v(-61.58, -46.99) * mm});
            skLineSegment(sketch, "E2729", {"start": v(-59.04, -46.99) * mm, "end": v(-59.04, -47.1) * mm});
            skLineSegment(sketch, "E2730", {"start": v(-59.04, -47.1) * mm, "end": v(-59.26, -47.4) * mm});
            skLineSegment(sketch, "E2731", {"start": v(-59.26, -47.4) * mm, "end": v(-59.3, -47.43) * mm});
            skLineSegment(sketch, "E2732", {"start": v(-59.3, -47.43) * mm, "end": v(-59.33, -47.45) * mm});
            skLineSegment(sketch, "E2733", {"start": v(-59.33, -47.45) * mm, "end": v(-59.76, -47.45) * mm});
            skLineSegment(sketch, "E2734", {"start": v(-59.76, -47.45) * mm, "end": v(-59.8, -47.43) * mm});
            skLineSegment(sketch, "E2735", {"start": v(-59.8, -47.43) * mm, "end": v(-59.84, -47.4) * mm});
            skLineSegment(sketch, "E2736", {"start": v(-59.84, -47.4) * mm, "end": v(-60.06, -47.1) * mm});
            skLineSegment(sketch, "E2737", {"start": v(-60.06, -47.1) * mm, "end": v(-60.06, -46.99) * mm});
            skLineSegment(sketch, "E2738", {"start": v(-60.06, -46.99) * mm, "end": v(-60.06, -46.88) * mm});
            skLineSegment(sketch, "E2739", {"start": v(-60.06, -46.88) * mm, "end": v(-59.84, -46.57) * mm});
            skLineSegment(sketch, "E2740", {"start": v(-59.84, -46.57) * mm, "end": v(-59.8, -46.55) * mm});
            skLineSegment(sketch, "E2741", {"start": v(-59.8, -46.55) * mm, "end": v(-59.76, -46.53) * mm});
            skLineSegment(sketch, "E2742", {"start": v(-59.76, -46.53) * mm, "end": v(-59.33, -46.53) * mm});
            skLineSegment(sketch, "E2743", {"start": v(-59.33, -46.53) * mm, "end": v(-59.3, -46.55) * mm});
            skLineSegment(sketch, "E2744", {"start": v(-59.3, -46.55) * mm, "end": v(-59.26, -46.57) * mm});
            skLineSegment(sketch, "E2745", {"start": v(-59.26, -46.57) * mm, "end": v(-59.04, -46.88) * mm});
            skLineSegment(sketch, "E2746", {"start": v(-59.04, -46.88) * mm, "end": v(-59.04, -46.99) * mm});
            skLineSegment(sketch, "E2747", {"start": v(-61.58, -49.53) * mm, "end": v(-61.58, -49.64) * mm});
            skLineSegment(sketch, "E2748", {"start": v(-61.58, -49.64) * mm, "end": v(-61.8, -49.95) * mm});
            skLineSegment(sketch, "E2749", {"start": v(-61.8, -49.95) * mm, "end": v(-61.83, -49.97) * mm});
            skLineSegment(sketch, "E2750", {"start": v(-61.83, -49.97) * mm, "end": v(-61.87, -50) * mm});
            skLineSegment(sketch, "E2751", {"start": v(-61.87, -50) * mm, "end": v(-62.3, -50) * mm});
            skLineSegment(sketch, "E2752", {"start": v(-62.3, -50) * mm, "end": v(-62.34, -49.97) * mm});
            skLineSegment(sketch, "E2753", {"start": v(-62.34, -49.97) * mm, "end": v(-62.38, -49.95) * mm});
            skLineSegment(sketch, "E2754", {"start": v(-62.38, -49.95) * mm, "end": v(-62.6, -49.63) * mm});
            skLineSegment(sketch, "E2755", {"start": v(-62.6, -49.63) * mm, "end": v(-62.6, -49.53) * mm});
            skLineSegment(sketch, "E2756", {"start": v(-62.6, -49.53) * mm, "end": v(-62.6, -49.42) * mm});
            skLineSegment(sketch, "E2757", {"start": v(-62.6, -49.42) * mm, "end": v(-62.38, -49.11) * mm});
            skLineSegment(sketch, "E2758", {"start": v(-62.38, -49.11) * mm, "end": v(-62.34, -49.09) * mm});
            skLineSegment(sketch, "E2759", {"start": v(-62.34, -49.09) * mm, "end": v(-62.3, -49.07) * mm});
            skLineSegment(sketch, "E2760", {"start": v(-62.3, -49.07) * mm, "end": v(-61.87, -49.07) * mm});
            skLineSegment(sketch, "E2761", {"start": v(-61.87, -49.07) * mm, "end": v(-61.83, -49.09) * mm});
            skLineSegment(sketch, "E2762", {"start": v(-61.83, -49.09) * mm, "end": v(-61.8, -49.11) * mm});
            skLineSegment(sketch, "E2763", {"start": v(-61.8, -49.11) * mm, "end": v(-61.58, -49.42) * mm});
            skLineSegment(sketch, "E2764", {"start": v(-61.58, -49.42) * mm, "end": v(-61.58, -49.53) * mm});
            skLineSegment(sketch, "E2765", {"start": v(-59.04, -49.53) * mm, "end": v(-59.04, -49.64) * mm});
            skLineSegment(sketch, "E2766", {"start": v(-59.04, -49.64) * mm, "end": v(-59.26, -49.95) * mm});
            skLineSegment(sketch, "E2767", {"start": v(-59.26, -49.95) * mm, "end": v(-59.3, -49.97) * mm});
            skLineSegment(sketch, "E2768", {"start": v(-59.3, -49.97) * mm, "end": v(-59.33, -50) * mm});
            skLineSegment(sketch, "E2769", {"start": v(-59.33, -50) * mm, "end": v(-59.76, -50) * mm});
            skLineSegment(sketch, "E2770", {"start": v(-59.76, -50) * mm, "end": v(-59.8, -49.97) * mm});
            skLineSegment(sketch, "E2771", {"start": v(-59.8, -49.97) * mm, "end": v(-59.84, -49.95) * mm});
            skLineSegment(sketch, "E2772", {"start": v(-59.84, -49.95) * mm, "end": v(-60.06, -49.63) * mm});
            skLineSegment(sketch, "E2773", {"start": v(-60.06, -49.63) * mm, "end": v(-60.06, -49.53) * mm});
            skLineSegment(sketch, "E2774", {"start": v(-60.06, -49.53) * mm, "end": v(-60.06, -49.42) * mm});
            skLineSegment(sketch, "E2775", {"start": v(-60.06, -49.42) * mm, "end": v(-59.84, -49.11) * mm});
            skLineSegment(sketch, "E2776", {"start": v(-59.84, -49.11) * mm, "end": v(-59.8, -49.09) * mm});
            skLineSegment(sketch, "E2777", {"start": v(-59.8, -49.09) * mm, "end": v(-59.76, -49.07) * mm});
            skLineSegment(sketch, "E2778", {"start": v(-59.76, -49.07) * mm, "end": v(-59.33, -49.07) * mm});
            skLineSegment(sketch, "E2779", {"start": v(-59.33, -49.07) * mm, "end": v(-59.3, -49.09) * mm});
            skLineSegment(sketch, "E2780", {"start": v(-59.3, -49.09) * mm, "end": v(-59.26, -49.11) * mm});
            skLineSegment(sketch, "E2781", {"start": v(-59.26, -49.11) * mm, "end": v(-59.04, -49.42) * mm});
            skLineSegment(sketch, "E2782", {"start": v(-59.04, -49.42) * mm, "end": v(-59.04, -49.53) * mm});
            skLineSegment(sketch, "E2783", {"start": v(-61.58, -52.07) * mm, "end": v(-61.58, -52.18) * mm});
            skLineSegment(sketch, "E2784", {"start": v(-61.58, -52.18) * mm, "end": v(-61.8, -52.49) * mm});
            skLineSegment(sketch, "E2785", {"start": v(-61.8, -52.49) * mm, "end": v(-61.83, -52.51) * mm});
            skLineSegment(sketch, "E2786", {"start": v(-61.83, -52.51) * mm, "end": v(-61.87, -52.53) * mm});
            skLineSegment(sketch, "E2787", {"start": v(-61.87, -52.53) * mm, "end": v(-62.3, -52.53) * mm});
            skLineSegment(sketch, "E2788", {"start": v(-62.3, -52.53) * mm, "end": v(-62.34, -52.51) * mm});
            skLineSegment(sketch, "E2789", {"start": v(-62.34, -52.51) * mm, "end": v(-62.38, -52.49) * mm});
            skLineSegment(sketch, "E2790", {"start": v(-62.38, -52.49) * mm, "end": v(-62.6, -52.17) * mm});
            skLineSegment(sketch, "E2791", {"start": v(-62.6, -52.17) * mm, "end": v(-62.6, -52.07) * mm});
            skLineSegment(sketch, "E2792", {"start": v(-62.6, -52.07) * mm, "end": v(-62.6, -51.96) * mm});
            skLineSegment(sketch, "E2793", {"start": v(-62.6, -51.96) * mm, "end": v(-62.38, -51.65) * mm});
            skLineSegment(sketch, "E2794", {"start": v(-62.38, -51.65) * mm, "end": v(-62.34, -51.63) * mm});
            skLineSegment(sketch, "E2795", {"start": v(-62.34, -51.63) * mm, "end": v(-62.3, -51.6) * mm});
            skLineSegment(sketch, "E2796", {"start": v(-62.3, -51.6) * mm, "end": v(-61.87, -51.6) * mm});
            skLineSegment(sketch, "E2797", {"start": v(-61.87, -51.6) * mm, "end": v(-61.83, -51.63) * mm});
            skLineSegment(sketch, "E2798", {"start": v(-61.83, -51.63) * mm, "end": v(-61.8, -51.65) * mm});
            skLineSegment(sketch, "E2799", {"start": v(-61.8, -51.65) * mm, "end": v(-61.58, -51.97) * mm});
            skLineSegment(sketch, "E2800", {"start": v(-61.58, -51.97) * mm, "end": v(-61.58, -52.07) * mm});
            skLineSegment(sketch, "E2801", {"start": v(-59.04, -52.07) * mm, "end": v(-59.04, -52.18) * mm});
            skLineSegment(sketch, "E2802", {"start": v(-59.04, -52.18) * mm, "end": v(-59.26, -52.49) * mm});
            skLineSegment(sketch, "E2803", {"start": v(-59.26, -52.49) * mm, "end": v(-59.3, -52.51) * mm});
            skLineSegment(sketch, "E2804", {"start": v(-59.3, -52.51) * mm, "end": v(-59.33, -52.53) * mm});
            skLineSegment(sketch, "E2805", {"start": v(-59.33, -52.53) * mm, "end": v(-59.76, -52.53) * mm});
            skLineSegment(sketch, "E2806", {"start": v(-59.76, -52.53) * mm, "end": v(-59.8, -52.51) * mm});
            skLineSegment(sketch, "E2807", {"start": v(-59.8, -52.51) * mm, "end": v(-59.84, -52.49) * mm});
            skLineSegment(sketch, "E2808", {"start": v(-59.84, -52.49) * mm, "end": v(-60.06, -52.17) * mm});
            skLineSegment(sketch, "E2809", {"start": v(-60.06, -52.17) * mm, "end": v(-60.06, -52.07) * mm});
            skLineSegment(sketch, "E2810", {"start": v(-60.06, -52.07) * mm, "end": v(-60.06, -51.96) * mm});
            skLineSegment(sketch, "E2811", {"start": v(-60.06, -51.96) * mm, "end": v(-59.84, -51.65) * mm});
            skLineSegment(sketch, "E2812", {"start": v(-59.84, -51.65) * mm, "end": v(-59.8, -51.63) * mm});
            skLineSegment(sketch, "E2813", {"start": v(-59.8, -51.63) * mm, "end": v(-59.76, -51.6) * mm});
            skLineSegment(sketch, "E2814", {"start": v(-59.76, -51.6) * mm, "end": v(-59.33, -51.6) * mm});
            skLineSegment(sketch, "E2815", {"start": v(-59.33, -51.6) * mm, "end": v(-59.3, -51.63) * mm});
            skLineSegment(sketch, "E2816", {"start": v(-59.3, -51.63) * mm, "end": v(-59.26, -51.65) * mm});
            skLineSegment(sketch, "E2817", {"start": v(-59.26, -51.65) * mm, "end": v(-59.04, -51.97) * mm});
            skLineSegment(sketch, "E2818", {"start": v(-59.04, -51.97) * mm, "end": v(-59.04, -52.07) * mm});
            skLineSegment(sketch, "E2819", {"start": v(-61.58, -54.61) * mm, "end": v(-61.58, -54.72) * mm});
            skLineSegment(sketch, "E2820", {"start": v(-61.58, -54.72) * mm, "end": v(-61.8, -55.03) * mm});
            skLineSegment(sketch, "E2821", {"start": v(-61.8, -55.03) * mm, "end": v(-61.83, -55.05) * mm});
            skLineSegment(sketch, "E2822", {"start": v(-61.83, -55.05) * mm, "end": v(-61.87, -55.07) * mm});
            skLineSegment(sketch, "E2823", {"start": v(-61.87, -55.07) * mm, "end": v(-62.3, -55.07) * mm});
            skLineSegment(sketch, "E2824", {"start": v(-62.3, -55.07) * mm, "end": v(-62.34, -55.05) * mm});
            skLineSegment(sketch, "E2825", {"start": v(-62.34, -55.05) * mm, "end": v(-62.38, -55.03) * mm});
            skLineSegment(sketch, "E2826", {"start": v(-62.38, -55.03) * mm, "end": v(-62.6, -54.71) * mm});
            skLineSegment(sketch, "E2827", {"start": v(-62.6, -54.71) * mm, "end": v(-62.6, -54.61) * mm});
            skLineSegment(sketch, "E2828", {"start": v(-62.6, -54.61) * mm, "end": v(-62.6, -54.5) * mm});
            skLineSegment(sketch, "E2829", {"start": v(-62.6, -54.5) * mm, "end": v(-62.38, -54.2) * mm});
            skLineSegment(sketch, "E2830", {"start": v(-62.38, -54.2) * mm, "end": v(-62.34, -54.17) * mm});
            skLineSegment(sketch, "E2831", {"start": v(-62.34, -54.17) * mm, "end": v(-62.3, -54.15) * mm});
            skLineSegment(sketch, "E2832", {"start": v(-62.3, -54.15) * mm, "end": v(-61.87, -54.15) * mm});
            skLineSegment(sketch, "E2833", {"start": v(-61.87, -54.15) * mm, "end": v(-61.83, -54.17) * mm});
            skLineSegment(sketch, "E2834", {"start": v(-61.83, -54.17) * mm, "end": v(-61.8, -54.2) * mm});
            skLineSegment(sketch, "E2835", {"start": v(-61.8, -54.2) * mm, "end": v(-61.58, -54.5) * mm});
            skLineSegment(sketch, "E2836", {"start": v(-61.58, -54.5) * mm, "end": v(-61.58, -54.61) * mm});
            skLineSegment(sketch, "E2837", {"start": v(-59.04, -54.61) * mm, "end": v(-59.04, -54.72) * mm});
            skLineSegment(sketch, "E2838", {"start": v(-59.04, -54.72) * mm, "end": v(-59.26, -55.03) * mm});
            skLineSegment(sketch, "E2839", {"start": v(-59.26, -55.03) * mm, "end": v(-59.3, -55.05) * mm});
            skLineSegment(sketch, "E2840", {"start": v(-59.3, -55.05) * mm, "end": v(-59.33, -55.07) * mm});
            skLineSegment(sketch, "E2841", {"start": v(-59.33, -55.07) * mm, "end": v(-59.76, -55.07) * mm});
            skLineSegment(sketch, "E2842", {"start": v(-59.76, -55.07) * mm, "end": v(-59.8, -55.05) * mm});
            skLineSegment(sketch, "E2843", {"start": v(-59.8, -55.05) * mm, "end": v(-59.84, -55.03) * mm});
            skLineSegment(sketch, "E2844", {"start": v(-59.84, -55.03) * mm, "end": v(-60.06, -54.71) * mm});
            skLineSegment(sketch, "E2845", {"start": v(-60.06, -54.71) * mm, "end": v(-60.06, -54.61) * mm});
            skLineSegment(sketch, "E2846", {"start": v(-60.06, -54.61) * mm, "end": v(-60.06, -54.5) * mm});
            skLineSegment(sketch, "E2847", {"start": v(-60.06, -54.5) * mm, "end": v(-59.84, -54.2) * mm});
            skLineSegment(sketch, "E2848", {"start": v(-59.84, -54.2) * mm, "end": v(-59.8, -54.17) * mm});
            skLineSegment(sketch, "E2849", {"start": v(-59.8, -54.17) * mm, "end": v(-59.76, -54.15) * mm});
            skLineSegment(sketch, "E2850", {"start": v(-59.76, -54.15) * mm, "end": v(-59.33, -54.15) * mm});
            skLineSegment(sketch, "E2851", {"start": v(-59.33, -54.15) * mm, "end": v(-59.3, -54.17) * mm});
            skLineSegment(sketch, "E2852", {"start": v(-59.3, -54.17) * mm, "end": v(-59.26, -54.2) * mm});
            skLineSegment(sketch, "E2853", {"start": v(-59.26, -54.2) * mm, "end": v(-59.04, -54.5) * mm});
            skLineSegment(sketch, "E2854", {"start": v(-59.04, -54.5) * mm, "end": v(-59.04, -54.61) * mm});
            skLineSegment(sketch, "E2855", {"start": v(-61.58, -57.15) * mm, "end": v(-61.58, -57.26) * mm});
            skLineSegment(sketch, "E2856", {"start": v(-61.58, -57.26) * mm, "end": v(-61.8, -57.57) * mm});
            skLineSegment(sketch, "E2857", {"start": v(-61.8, -57.57) * mm, "end": v(-61.83, -57.59) * mm});
            skLineSegment(sketch, "E2858", {"start": v(-61.83, -57.59) * mm, "end": v(-61.87, -57.61) * mm});
            skLineSegment(sketch, "E2859", {"start": v(-61.87, -57.61) * mm, "end": v(-62.3, -57.61) * mm});
            skLineSegment(sketch, "E2860", {"start": v(-62.3, -57.61) * mm, "end": v(-62.34, -57.59) * mm});
            skLineSegment(sketch, "E2861", {"start": v(-62.34, -57.59) * mm, "end": v(-62.38, -57.57) * mm});
            skLineSegment(sketch, "E2862", {"start": v(-62.38, -57.57) * mm, "end": v(-62.6, -57.25) * mm});
            skLineSegment(sketch, "E2863", {"start": v(-62.6, -57.25) * mm, "end": v(-62.6, -57.15) * mm});
            skLineSegment(sketch, "E2864", {"start": v(-62.6, -57.15) * mm, "end": v(-62.6, -57.04) * mm});
            skLineSegment(sketch, "E2865", {"start": v(-62.6, -57.04) * mm, "end": v(-62.38, -56.73) * mm});
            skLineSegment(sketch, "E2866", {"start": v(-62.38, -56.73) * mm, "end": v(-62.34, -56.71) * mm});
            skLineSegment(sketch, "E2867", {"start": v(-62.34, -56.71) * mm, "end": v(-62.3, -56.69) * mm});
            skLineSegment(sketch, "E2868", {"start": v(-62.3, -56.69) * mm, "end": v(-61.87, -56.69) * mm});
            skLineSegment(sketch, "E2869", {"start": v(-61.87, -56.69) * mm, "end": v(-61.83, -56.71) * mm});
            skLineSegment(sketch, "E2870", {"start": v(-61.83, -56.71) * mm, "end": v(-61.8, -56.73) * mm});
            skLineSegment(sketch, "E2871", {"start": v(-61.8, -56.73) * mm, "end": v(-61.58, -57.05) * mm});
            skLineSegment(sketch, "E2872", {"start": v(-61.58, -57.05) * mm, "end": v(-61.58, -57.15) * mm});
            skLineSegment(sketch, "E2873", {"start": v(-59.04, -57.15) * mm, "end": v(-59.04, -57.26) * mm});
            skLineSegment(sketch, "E2874", {"start": v(-59.04, -57.26) * mm, "end": v(-59.26, -57.57) * mm});
            skLineSegment(sketch, "E2875", {"start": v(-59.26, -57.57) * mm, "end": v(-59.3, -57.59) * mm});
            skLineSegment(sketch, "E2876", {"start": v(-59.3, -57.59) * mm, "end": v(-59.33, -57.61) * mm});
            skLineSegment(sketch, "E2877", {"start": v(-59.33, -57.61) * mm, "end": v(-59.76, -57.61) * mm});
            skLineSegment(sketch, "E2878", {"start": v(-59.76, -57.61) * mm, "end": v(-59.8, -57.59) * mm});
            skLineSegment(sketch, "E2879", {"start": v(-59.8, -57.59) * mm, "end": v(-59.84, -57.57) * mm});
            skLineSegment(sketch, "E2880", {"start": v(-59.84, -57.57) * mm, "end": v(-60.06, -57.25) * mm});
            skLineSegment(sketch, "E2881", {"start": v(-60.06, -57.25) * mm, "end": v(-60.06, -57.15) * mm});
            skLineSegment(sketch, "E2882", {"start": v(-60.06, -57.15) * mm, "end": v(-60.06, -57.04) * mm});
            skLineSegment(sketch, "E2883", {"start": v(-60.06, -57.04) * mm, "end": v(-59.84, -56.73) * mm});
            skLineSegment(sketch, "E2884", {"start": v(-59.84, -56.73) * mm, "end": v(-59.8, -56.71) * mm});
            skLineSegment(sketch, "E2885", {"start": v(-59.8, -56.71) * mm, "end": v(-59.76, -56.69) * mm});
            skLineSegment(sketch, "E2886", {"start": v(-59.76, -56.69) * mm, "end": v(-59.33, -56.69) * mm});
            skLineSegment(sketch, "E2887", {"start": v(-59.33, -56.69) * mm, "end": v(-59.3, -56.71) * mm});
            skLineSegment(sketch, "E2888", {"start": v(-59.3, -56.71) * mm, "end": v(-59.26, -56.73) * mm});
            skLineSegment(sketch, "E2889", {"start": v(-59.26, -56.73) * mm, "end": v(-59.04, -57.05) * mm});
            skLineSegment(sketch, "E2890", {"start": v(-59.04, -57.05) * mm, "end": v(-59.04, -57.15) * mm});
            skLineSegment(sketch, "E2891", {"start": v(-61.58, -59.69) * mm, "end": v(-61.58, -59.8) * mm});
            skLineSegment(sketch, "E2892", {"start": v(-61.58, -59.8) * mm, "end": v(-61.8, -60.1) * mm});
            skLineSegment(sketch, "E2893", {"start": v(-61.8, -60.1) * mm, "end": v(-61.83, -60.13) * mm});
            skLineSegment(sketch, "E2894", {"start": v(-61.83, -60.13) * mm, "end": v(-61.87, -60.15) * mm});
            skLineSegment(sketch, "E2895", {"start": v(-61.87, -60.15) * mm, "end": v(-62.3, -60.15) * mm});
            skLineSegment(sketch, "E2896", {"start": v(-62.3, -60.15) * mm, "end": v(-62.34, -60.13) * mm});
            skLineSegment(sketch, "E2897", {"start": v(-62.34, -60.13) * mm, "end": v(-62.38, -60.1) * mm});
            skLineSegment(sketch, "E2898", {"start": v(-62.38, -60.1) * mm, "end": v(-62.6, -59.8) * mm});
            skLineSegment(sketch, "E2899", {"start": v(-62.6, -59.8) * mm, "end": v(-62.6, -59.69) * mm});
            skLineSegment(sketch, "E2900", {"start": v(-62.6, -59.69) * mm, "end": v(-62.6, -59.58) * mm});
            skLineSegment(sketch, "E2901", {"start": v(-62.6, -59.58) * mm, "end": v(-62.38, -59.27) * mm});
            skLineSegment(sketch, "E2902", {"start": v(-62.38, -59.27) * mm, "end": v(-62.34, -59.25) * mm});
            skLineSegment(sketch, "E2903", {"start": v(-62.34, -59.25) * mm, "end": v(-62.3, -59.23) * mm});
            skLineSegment(sketch, "E2904", {"start": v(-62.3, -59.23) * mm, "end": v(-61.87, -59.23) * mm});
            skLineSegment(sketch, "E2905", {"start": v(-61.87, -59.23) * mm, "end": v(-61.83, -59.25) * mm});
            skLineSegment(sketch, "E2906", {"start": v(-61.83, -59.25) * mm, "end": v(-61.8, -59.27) * mm});
            skLineSegment(sketch, "E2907", {"start": v(-61.8, -59.27) * mm, "end": v(-61.58, -59.58) * mm});
            skLineSegment(sketch, "E2908", {"start": v(-61.58, -59.58) * mm, "end": v(-61.58, -59.69) * mm});
            skLineSegment(sketch, "E2909", {"start": v(-59.04, -59.69) * mm, "end": v(-59.04, -59.8) * mm});
            skLineSegment(sketch, "E2910", {"start": v(-59.04, -59.8) * mm, "end": v(-59.26, -60.1) * mm});
            skLineSegment(sketch, "E2911", {"start": v(-59.26, -60.1) * mm, "end": v(-59.3, -60.13) * mm});
            skLineSegment(sketch, "E2912", {"start": v(-59.3, -60.13) * mm, "end": v(-59.33, -60.15) * mm});
            skLineSegment(sketch, "E2913", {"start": v(-59.33, -60.15) * mm, "end": v(-59.76, -60.15) * mm});
            skLineSegment(sketch, "E2914", {"start": v(-59.76, -60.15) * mm, "end": v(-59.8, -60.13) * mm});
            skLineSegment(sketch, "E2915", {"start": v(-59.8, -60.13) * mm, "end": v(-59.84, -60.1) * mm});
            skLineSegment(sketch, "E2916", {"start": v(-59.84, -60.1) * mm, "end": v(-60.06, -59.8) * mm});
            skLineSegment(sketch, "E2917", {"start": v(-60.06, -59.8) * mm, "end": v(-60.06, -59.69) * mm});
            skLineSegment(sketch, "E2918", {"start": v(-60.06, -59.69) * mm, "end": v(-60.06, -59.58) * mm});
            skLineSegment(sketch, "E2919", {"start": v(-60.06, -59.58) * mm, "end": v(-59.84, -59.27) * mm});
            skLineSegment(sketch, "E2920", {"start": v(-59.84, -59.27) * mm, "end": v(-59.8, -59.25) * mm});
            skLineSegment(sketch, "E2921", {"start": v(-59.8, -59.25) * mm, "end": v(-59.76, -59.23) * mm});
            skLineSegment(sketch, "E2922", {"start": v(-59.76, -59.23) * mm, "end": v(-59.33, -59.23) * mm});
            skLineSegment(sketch, "E2923", {"start": v(-59.33, -59.23) * mm, "end": v(-59.3, -59.25) * mm});
            skLineSegment(sketch, "E2924", {"start": v(-59.3, -59.25) * mm, "end": v(-59.26, -59.27) * mm});
            skLineSegment(sketch, "E2925", {"start": v(-59.26, -59.27) * mm, "end": v(-59.04, -59.58) * mm});
            skLineSegment(sketch, "E2926", {"start": v(-59.04, -59.58) * mm, "end": v(-59.04, -59.69) * mm});
            skLineSegment(sketch, "E2927", {"start": v(-61.58, -62.23) * mm, "end": v(-61.58, -62.34) * mm});
            skLineSegment(sketch, "E2928", {"start": v(-61.58, -62.34) * mm, "end": v(-61.8, -62.65) * mm});
            skLineSegment(sketch, "E2929", {"start": v(-61.8, -62.65) * mm, "end": v(-61.83, -62.67) * mm});
            skLineSegment(sketch, "E2930", {"start": v(-61.83, -62.67) * mm, "end": v(-61.87, -62.7) * mm});
            skLineSegment(sketch, "E2931", {"start": v(-61.87, -62.7) * mm, "end": v(-62.3, -62.7) * mm});
            skLineSegment(sketch, "E2932", {"start": v(-62.3, -62.7) * mm, "end": v(-62.34, -62.67) * mm});
            skLineSegment(sketch, "E2933", {"start": v(-62.34, -62.67) * mm, "end": v(-62.38, -62.65) * mm});
            skLineSegment(sketch, "E2934", {"start": v(-62.38, -62.65) * mm, "end": v(-62.6, -62.33) * mm});
            skLineSegment(sketch, "E2935", {"start": v(-62.6, -62.33) * mm, "end": v(-62.6, -62.23) * mm});
            skLineSegment(sketch, "E2936", {"start": v(-62.6, -62.23) * mm, "end": v(-62.6, -62.12) * mm});
            skLineSegment(sketch, "E2937", {"start": v(-62.6, -62.12) * mm, "end": v(-62.38, -61.81) * mm});
            skLineSegment(sketch, "E2938", {"start": v(-62.38, -61.81) * mm, "end": v(-62.34, -61.79) * mm});
            skLineSegment(sketch, "E2939", {"start": v(-62.34, -61.79) * mm, "end": v(-62.3, -61.77) * mm});
            skLineSegment(sketch, "E2940", {"start": v(-62.3, -61.77) * mm, "end": v(-61.87, -61.77) * mm});
            skLineSegment(sketch, "E2941", {"start": v(-61.87, -61.77) * mm, "end": v(-61.83, -61.79) * mm});
            skLineSegment(sketch, "E2942", {"start": v(-61.83, -61.79) * mm, "end": v(-61.8, -61.81) * mm});
            skLineSegment(sketch, "E2943", {"start": v(-61.8, -61.81) * mm, "end": v(-61.58, -62.12) * mm});
            skLineSegment(sketch, "E2944", {"start": v(-61.58, -62.12) * mm, "end": v(-61.58, -62.23) * mm});
            skLineSegment(sketch, "E2945", {"start": v(-59.04, -62.23) * mm, "end": v(-59.04, -62.34) * mm});
            skLineSegment(sketch, "E2946", {"start": v(-59.04, -62.34) * mm, "end": v(-59.26, -62.65) * mm});
            skLineSegment(sketch, "E2947", {"start": v(-59.26, -62.65) * mm, "end": v(-59.3, -62.67) * mm});
            skLineSegment(sketch, "E2948", {"start": v(-59.3, -62.67) * mm, "end": v(-59.33, -62.7) * mm});
            skLineSegment(sketch, "E2949", {"start": v(-59.33, -62.7) * mm, "end": v(-59.76, -62.7) * mm});
            skLineSegment(sketch, "E2950", {"start": v(-59.76, -62.7) * mm, "end": v(-59.8, -62.67) * mm});
            skLineSegment(sketch, "E2951", {"start": v(-59.8, -62.67) * mm, "end": v(-59.84, -62.65) * mm});
            skLineSegment(sketch, "E2952", {"start": v(-59.84, -62.65) * mm, "end": v(-60.06, -62.33) * mm});
            skLineSegment(sketch, "E2953", {"start": v(-60.06, -62.33) * mm, "end": v(-60.06, -62.23) * mm});
            skLineSegment(sketch, "E2954", {"start": v(-60.06, -62.23) * mm, "end": v(-60.06, -62.12) * mm});
            skLineSegment(sketch, "E2955", {"start": v(-60.06, -62.12) * mm, "end": v(-59.84, -61.81) * mm});
            skLineSegment(sketch, "E2956", {"start": v(-59.84, -61.81) * mm, "end": v(-59.8, -61.79) * mm});
            skLineSegment(sketch, "E2957", {"start": v(-59.8, -61.79) * mm, "end": v(-59.76, -61.77) * mm});
            skLineSegment(sketch, "E2958", {"start": v(-59.76, -61.77) * mm, "end": v(-59.33, -61.77) * mm});
            skLineSegment(sketch, "E2959", {"start": v(-59.33, -61.77) * mm, "end": v(-59.3, -61.79) * mm});
            skLineSegment(sketch, "E2960", {"start": v(-59.3, -61.79) * mm, "end": v(-59.26, -61.81) * mm});
            skLineSegment(sketch, "E2961", {"start": v(-59.26, -61.81) * mm, "end": v(-59.04, -62.12) * mm});
            skLineSegment(sketch, "E2962", {"start": v(-59.04, -62.12) * mm, "end": v(-59.04, -62.23) * mm});
            skLineSegment(sketch, "E2963", {"start": v(51.3, 40.66) * mm, "end": v(51.3, 40.52) * mm});
            skLineSegment(sketch, "E2964", {"start": v(51.3, 40.52) * mm, "end": v(51.16, 40.1) * mm});
            skLineSegment(sketch, "E2965", {"start": v(51.16, 40.1) * mm, "end": v(50.84, 39.75) * mm});
            skLineSegment(sketch, "E2966", {"start": v(50.84, 39.75) * mm, "end": v(50.75, 39.7) * mm});
            skLineSegment(sketch, "E2967", {"start": v(50.75, 39.7) * mm, "end": v(50.67, 39.66) * mm});
            skLineSegment(sketch, "E2968", {"start": v(50.67, 39.66) * mm, "end": v(50.2, 39.56) * mm});
            skLineSegment(sketch, "E2969", {"start": v(50.2, 39.56) * mm, "end": v(49.74, 39.66) * mm});
            skLineSegment(sketch, "E2970", {"start": v(49.74, 39.66) * mm, "end": v(49.65, 39.7) * mm});
            skLineSegment(sketch, "E2971", {"start": v(49.65, 39.7) * mm, "end": v(49.57, 39.75) * mm});
            skLineSegment(sketch, "E2972", {"start": v(49.57, 39.75) * mm, "end": v(49.25, 40.1) * mm});
            skLineSegment(sketch, "E2973", {"start": v(49.25, 40.1) * mm, "end": v(49.1, 40.52) * mm});
            skLineSegment(sketch, "E2974", {"start": v(49.1, 40.52) * mm, "end": v(49.1, 40.66) * mm});
            skLineSegment(sketch, "E2975", {"start": v(49.1, 40.66) * mm, "end": v(49.1, 40.8) * mm});
            skLineSegment(sketch, "E2976", {"start": v(49.1, 40.8) * mm, "end": v(49.25, 41.2) * mm});
            skLineSegment(sketch, "E2977", {"start": v(49.25, 41.2) * mm, "end": v(49.57, 41.56) * mm});
            skLineSegment(sketch, "E2978", {"start": v(49.57, 41.56) * mm, "end": v(49.65, 41.6) * mm});
            skLineSegment(sketch, "E2979", {"start": v(49.65, 41.6) * mm, "end": v(49.74, 41.66) * mm});
            skLineSegment(sketch, "E2980", {"start": v(49.74, 41.66) * mm, "end": v(50.2, 41.76) * mm});
            skLineSegment(sketch, "E2981", {"start": v(50.2, 41.76) * mm, "end": v(50.67, 41.66) * mm});
            skLineSegment(sketch, "E2982", {"start": v(50.67, 41.66) * mm, "end": v(50.75, 41.6) * mm});
            skLineSegment(sketch, "E2983", {"start": v(50.75, 41.6) * mm, "end": v(50.84, 41.56) * mm});
            skLineSegment(sketch, "E2984", {"start": v(50.84, 41.56) * mm, "end": v(51.16, 41.2) * mm});
            skLineSegment(sketch, "E2985", {"start": v(51.16, 41.2) * mm, "end": v(51.3, 40.8) * mm});
            skLineSegment(sketch, "E2986", {"start": v(51.3, 40.8) * mm, "end": v(51.3, 40.66) * mm});
            skLineSegment(sketch, "E2987", {"start": v(51.3, 30.46) * mm, "end": v(51.3, 30.32) * mm});
            skLineSegment(sketch, "E2988", {"start": v(51.3, 30.32) * mm, "end": v(51.16, 29.91) * mm});
            skLineSegment(sketch, "E2989", {"start": v(51.16, 29.91) * mm, "end": v(50.84, 29.56) * mm});
            skLineSegment(sketch, "E2990", {"start": v(50.84, 29.56) * mm, "end": v(50.75, 29.5) * mm});
            skLineSegment(sketch, "E2991", {"start": v(50.75, 29.5) * mm, "end": v(50.67, 29.46) * mm});
            skLineSegment(sketch, "E2992", {"start": v(50.67, 29.46) * mm, "end": v(50.2, 29.36) * mm});
            skLineSegment(sketch, "E2993", {"start": v(50.2, 29.36) * mm, "end": v(49.74, 29.46) * mm});
            skLineSegment(sketch, "E2994", {"start": v(49.74, 29.46) * mm, "end": v(49.65, 29.5) * mm});
            skLineSegment(sketch, "E2995", {"start": v(49.65, 29.5) * mm, "end": v(49.57, 29.56) * mm});
            skLineSegment(sketch, "E2996", {"start": v(49.57, 29.56) * mm, "end": v(49.25, 29.91) * mm});
            skLineSegment(sketch, "E2997", {"start": v(49.25, 29.91) * mm, "end": v(49.1, 30.32) * mm});
            skLineSegment(sketch, "E2998", {"start": v(49.1, 30.32) * mm, "end": v(49.1, 30.46) * mm});
            skLineSegment(sketch, "E2999", {"start": v(49.1, 30.46) * mm, "end": v(49.1, 30.6) * mm});
            skLineSegment(sketch, "E3000", {"start": v(49.1, 30.6) * mm, "end": v(49.25, 31) * mm});
            skLineSegment(sketch, "E3001", {"start": v(49.25, 31) * mm, "end": v(49.57, 31.36) * mm});
            skLineSegment(sketch, "E3002", {"start": v(49.57, 31.36) * mm, "end": v(49.65, 31.41) * mm});
            skLineSegment(sketch, "E3003", {"start": v(49.65, 31.41) * mm, "end": v(49.74, 31.46) * mm});
            skLineSegment(sketch, "E3004", {"start": v(49.74, 31.46) * mm, "end": v(50.2, 31.56) * mm});
            skLineSegment(sketch, "E3005", {"start": v(50.2, 31.56) * mm, "end": v(50.67, 31.46) * mm});
            skLineSegment(sketch, "E3006", {"start": v(50.67, 31.46) * mm, "end": v(50.75, 31.41) * mm});
            skLineSegment(sketch, "E3007", {"start": v(50.75, 31.41) * mm, "end": v(50.84, 31.36) * mm});
            skLineSegment(sketch, "E3008", {"start": v(50.84, 31.36) * mm, "end": v(51.16, 31) * mm});
            skLineSegment(sketch, "E3009", {"start": v(51.16, 31) * mm, "end": v(51.3, 30.6) * mm});
            skLineSegment(sketch, "E3010", {"start": v(51.3, 30.6) * mm, "end": v(51.3, 30.46) * mm});
            skLineSegment(sketch, "E3011", {"start": v(46.44, 35.56) * mm, "end": v(46.44, 35.45) * mm});
            skLineSegment(sketch, "E3012", {"start": v(46.44, 35.45) * mm, "end": v(46.23, 35.15) * mm});
            skLineSegment(sketch, "E3013", {"start": v(46.23, 35.15) * mm, "end": v(46.19, 35.13) * mm});
            skLineSegment(sketch, "E3014", {"start": v(46.19, 35.13) * mm, "end": v(46.15, 35.1) * mm});
            skLineSegment(sketch, "E3015", {"start": v(46.15, 35.1) * mm, "end": v(45.73, 35.1) * mm});
            skLineSegment(sketch, "E3016", {"start": v(45.73, 35.1) * mm, "end": v(45.69, 35.13) * mm});
            skLineSegment(sketch, "E3017", {"start": v(45.69, 35.13) * mm, "end": v(45.65, 35.15) * mm});
            skLineSegment(sketch, "E3018", {"start": v(45.65, 35.15) * mm, "end": v(45.44, 35.46) * mm});
            skLineSegment(sketch, "E3019", {"start": v(45.44, 35.46) * mm, "end": v(45.44, 35.56) * mm});
            skLineSegment(sketch, "E3020", {"start": v(45.44, 35.56) * mm, "end": v(45.44, 35.67) * mm});
            skLineSegment(sketch, "E3021", {"start": v(45.44, 35.67) * mm, "end": v(45.65, 35.97) * mm});
            skLineSegment(sketch, "E3022", {"start": v(45.65, 35.97) * mm, "end": v(45.69, 36) * mm});
            skLineSegment(sketch, "E3023", {"start": v(45.69, 36) * mm, "end": v(45.73, 36.02) * mm});
            skLineSegment(sketch, "E3024", {"start": v(45.73, 36.02) * mm, "end": v(46.15, 36.02) * mm});
            skLineSegment(sketch, "E3025", {"start": v(46.15, 36.02) * mm, "end": v(46.19, 36) * mm});
            skLineSegment(sketch, "E3026", {"start": v(46.19, 36) * mm, "end": v(46.23, 35.97) * mm});
            skLineSegment(sketch, "E3027", {"start": v(46.23, 35.97) * mm, "end": v(46.44, 35.66) * mm});
            skLineSegment(sketch, "E3028", {"start": v(46.44, 35.66) * mm, "end": v(46.44, 35.56) * mm});
            skLineSegment(sketch, "E3029", {"start": v(46.44, 38.06) * mm, "end": v(46.44, 37.95) * mm});
            skLineSegment(sketch, "E3030", {"start": v(46.44, 37.95) * mm, "end": v(46.23, 37.65) * mm});
            skLineSegment(sketch, "E3031", {"start": v(46.23, 37.65) * mm, "end": v(46.19, 37.63) * mm});
            skLineSegment(sketch, "E3032", {"start": v(46.19, 37.63) * mm, "end": v(46.15, 37.6) * mm});
            skLineSegment(sketch, "E3033", {"start": v(46.15, 37.6) * mm, "end": v(45.73, 37.6) * mm});
            skLineSegment(sketch, "E3034", {"start": v(45.73, 37.6) * mm, "end": v(45.69, 37.63) * mm});
            skLineSegment(sketch, "E3035", {"start": v(45.69, 37.63) * mm, "end": v(45.65, 37.65) * mm});
            skLineSegment(sketch, "E3036", {"start": v(45.65, 37.65) * mm, "end": v(45.44, 37.96) * mm});
            skLineSegment(sketch, "E3037", {"start": v(45.44, 37.96) * mm, "end": v(45.44, 38.06) * mm});
            skLineSegment(sketch, "E3038", {"start": v(45.44, 38.06) * mm, "end": v(45.44, 38.17) * mm});
            skLineSegment(sketch, "E3039", {"start": v(45.44, 38.17) * mm, "end": v(45.65, 38.47) * mm});
            skLineSegment(sketch, "E3040", {"start": v(45.65, 38.47) * mm, "end": v(45.69, 38.5) * mm});
            skLineSegment(sketch, "E3041", {"start": v(45.69, 38.5) * mm, "end": v(45.73, 38.52) * mm});
            skLineSegment(sketch, "E3042", {"start": v(45.73, 38.52) * mm, "end": v(46.15, 38.52) * mm});
            skLineSegment(sketch, "E3043", {"start": v(46.15, 38.52) * mm, "end": v(46.19, 38.5) * mm});
            skLineSegment(sketch, "E3044", {"start": v(46.19, 38.5) * mm, "end": v(46.23, 38.47) * mm});
            skLineSegment(sketch, "E3045", {"start": v(46.23, 38.47) * mm, "end": v(46.44, 38.16) * mm});
            skLineSegment(sketch, "E3046", {"start": v(46.44, 38.16) * mm, "end": v(46.44, 38.06) * mm});
            skLineSegment(sketch, "E3047", {"start": v(-60.42, 43.76) * mm, "end": v(-60.42, 43.7) * mm});
            skLineSegment(sketch, "E3048", {"start": v(-60.42, 43.7) * mm, "end": v(-60.54, 43.48) * mm});
            skLineSegment(sketch, "E3049", {"start": v(-60.54, 43.48) * mm, "end": v(-60.75, 43.36) * mm});
            skLineSegment(sketch, "E3050", {"start": v(-60.75, 43.36) * mm, "end": v(-60.82, 43.36) * mm});
            skLineSegment(sketch, "E3051", {"start": v(-60.82, 43.36) * mm, "end": v(-60.9, 43.36) * mm});
            skLineSegment(sketch, "E3052", {"start": v(-60.9, 43.36) * mm, "end": v(-61.1, 43.48) * mm});
            skLineSegment(sketch, "E3053", {"start": v(-61.1, 43.48) * mm, "end": v(-61.22, 43.7) * mm});
            skLineSegment(sketch, "E3054", {"start": v(-61.22, 43.7) * mm, "end": v(-61.22, 43.76) * mm});
            skLineSegment(sketch, "E3055", {"start": v(-61.22, 43.76) * mm, "end": v(-61.22, 43.84) * mm});
            skLineSegment(sketch, "E3056", {"start": v(-61.22, 43.84) * mm, "end": v(-61.1, 44.05) * mm});
            skLineSegment(sketch, "E3057", {"start": v(-61.1, 44.05) * mm, "end": v(-60.9, 44.16) * mm});
            skLineSegment(sketch, "E3058", {"start": v(-60.9, 44.16) * mm, "end": v(-60.82, 44.16) * mm});
            skLineSegment(sketch, "E3059", {"start": v(-60.82, 44.16) * mm, "end": v(-60.75, 44.16) * mm});
            skLineSegment(sketch, "E3060", {"start": v(-60.75, 44.16) * mm, "end": v(-60.54, 44.05) * mm});
            skLineSegment(sketch, "E3061", {"start": v(-60.54, 44.05) * mm, "end": v(-60.42, 43.84) * mm});
            skLineSegment(sketch, "E3062", {"start": v(-60.42, 43.84) * mm, "end": v(-60.42, 43.76) * mm});
            skLineSegment(sketch, "E3063", {"start": v(-60.42, 41.76) * mm, "end": v(-60.42, 41.7) * mm});
            skLineSegment(sketch, "E3064", {"start": v(-60.42, 41.7) * mm, "end": v(-60.54, 41.48) * mm});
            skLineSegment(sketch, "E3065", {"start": v(-60.54, 41.48) * mm, "end": v(-60.75, 41.36) * mm});
            skLineSegment(sketch, "E3066", {"start": v(-60.75, 41.36) * mm, "end": v(-60.82, 41.36) * mm});
            skLineSegment(sketch, "E3067", {"start": v(-60.82, 41.36) * mm, "end": v(-60.9, 41.36) * mm});
            skLineSegment(sketch, "E3068", {"start": v(-60.9, 41.36) * mm, "end": v(-61.1, 41.48) * mm});
            skLineSegment(sketch, "E3069", {"start": v(-61.1, 41.48) * mm, "end": v(-61.22, 41.7) * mm});
            skLineSegment(sketch, "E3070", {"start": v(-61.22, 41.7) * mm, "end": v(-61.22, 41.76) * mm});
            skLineSegment(sketch, "E3071", {"start": v(-61.22, 41.76) * mm, "end": v(-61.22, 41.84) * mm});
            skLineSegment(sketch, "E3072", {"start": v(-61.22, 41.84) * mm, "end": v(-61.1, 42.05) * mm});
            skLineSegment(sketch, "E3073", {"start": v(-61.1, 42.05) * mm, "end": v(-60.9, 42.16) * mm});
            skLineSegment(sketch, "E3074", {"start": v(-60.9, 42.16) * mm, "end": v(-60.82, 42.16) * mm});
            skLineSegment(sketch, "E3075", {"start": v(-60.82, 42.16) * mm, "end": v(-60.75, 42.16) * mm});
            skLineSegment(sketch, "E3076", {"start": v(-60.75, 42.16) * mm, "end": v(-60.54, 42.05) * mm});
            skLineSegment(sketch, "E3077", {"start": v(-60.54, 42.05) * mm, "end": v(-60.42, 41.84) * mm});
            skLineSegment(sketch, "E3078", {"start": v(-60.42, 41.84) * mm, "end": v(-60.42, 41.76) * mm});
            skLineSegment(sketch, "E3079", {"start": v(-60.42, 52.8) * mm, "end": v(-60.42, 52.73) * mm});
            skLineSegment(sketch, "E3080", {"start": v(-60.42, 52.73) * mm, "end": v(-60.54, 52.52) * mm});
            skLineSegment(sketch, "E3081", {"start": v(-60.54, 52.52) * mm, "end": v(-60.75, 52.4) * mm});
            skLineSegment(sketch, "E3082", {"start": v(-60.75, 52.4) * mm, "end": v(-60.82, 52.4) * mm});
            skLineSegment(sketch, "E3083", {"start": v(-60.82, 52.4) * mm, "end": v(-60.9, 52.4) * mm});
            skLineSegment(sketch, "E3084", {"start": v(-60.9, 52.4) * mm, "end": v(-61.1, 52.52) * mm});
            skLineSegment(sketch, "E3085", {"start": v(-61.1, 52.52) * mm, "end": v(-61.22, 52.73) * mm});
            skLineSegment(sketch, "E3086", {"start": v(-61.22, 52.73) * mm, "end": v(-61.22, 52.8) * mm});
            skLineSegment(sketch, "E3087", {"start": v(-61.22, 52.8) * mm, "end": v(-61.22, 52.87) * mm});
            skLineSegment(sketch, "E3088", {"start": v(-61.22, 52.87) * mm, "end": v(-61.1, 53.08) * mm});
            skLineSegment(sketch, "E3089", {"start": v(-61.1, 53.08) * mm, "end": v(-60.9, 53.2) * mm});
            skLineSegment(sketch, "E3090", {"start": v(-60.9, 53.2) * mm, "end": v(-60.82, 53.2) * mm});
            skLineSegment(sketch, "E3091", {"start": v(-60.82, 53.2) * mm, "end": v(-60.75, 53.2) * mm});
            skLineSegment(sketch, "E3092", {"start": v(-60.75, 53.2) * mm, "end": v(-60.54, 53.08) * mm});
            skLineSegment(sketch, "E3093", {"start": v(-60.54, 53.08) * mm, "end": v(-60.42, 52.87) * mm});
            skLineSegment(sketch, "E3094", {"start": v(-60.42, 52.87) * mm, "end": v(-60.42, 52.8) * mm});
            skLineSegment(sketch, "E3095", {"start": v(-5.66, -52.07) * mm, "end": v(-5.66, -52.38) * mm});
            skLineSegment(sketch, "E3096", {"start": v(-5.66, -52.38) * mm, "end": v(-6, -53.32) * mm});
            skLineSegment(sketch, "E3097", {"start": v(-6, -53.32) * mm, "end": v(-6.72, -54.12) * mm});
            skLineSegment(sketch, "E3098", {"start": v(-6.72, -54.12) * mm, "end": v(-6.91, -54.24) * mm});
            skLineSegment(sketch, "E3099", {"start": v(-6.91, -54.24) * mm, "end": v(-7.1, -54.35) * mm});
            skLineSegment(sketch, "E3100", {"start": v(-7.1, -54.35) * mm, "end": v(-8.16, -54.57) * mm});
            skLineSegment(sketch, "E3101", {"start": v(-8.16, -54.57) * mm, "end": v(-9.22, -54.35) * mm});
            skLineSegment(sketch, "E3102", {"start": v(-9.22, -54.35) * mm, "end": v(-9.41, -54.24) * mm});
            skLineSegment(sketch, "E3103", {"start": v(-9.41, -54.24) * mm, "end": v(-9.6, -54.12) * mm});
            skLineSegment(sketch, "E3104", {"start": v(-9.6, -54.12) * mm, "end": v(-10.33, -53.32) * mm});
            skLineSegment(sketch, "E3105", {"start": v(-10.33, -53.32) * mm, "end": v(-10.66, -52.38) * mm});
            skLineSegment(sketch, "E3106", {"start": v(-10.66, -52.38) * mm, "end": v(-10.66, -52.07) * mm});
            skLineSegment(sketch, "E3107", {"start": v(-10.66, -52.07) * mm, "end": v(-10.66, -51.76) * mm});
            skLineSegment(sketch, "E3108", {"start": v(-10.66, -51.76) * mm, "end": v(-10.33, -50.82) * mm});
            skLineSegment(sketch, "E3109", {"start": v(-10.33, -50.82) * mm, "end": v(-9.6, -50.02) * mm});
            skLineSegment(sketch, "E3110", {"start": v(-9.6, -50.02) * mm, "end": v(-9.41, -49.9) * mm});
            skLineSegment(sketch, "E3111", {"start": v(-9.41, -49.9) * mm, "end": v(-9.22, -49.8) * mm});
            skLineSegment(sketch, "E3112", {"start": v(-9.22, -49.8) * mm, "end": v(-8.16, -49.57) * mm});
            skLineSegment(sketch, "E3113", {"start": v(-8.16, -49.57) * mm, "end": v(-7.1, -49.8) * mm});
            skLineSegment(sketch, "E3114", {"start": v(-7.1, -49.8) * mm, "end": v(-6.91, -49.9) * mm});
            skLineSegment(sketch, "E3115", {"start": v(-6.91, -49.9) * mm, "end": v(-6.72, -50.02) * mm});
            skLineSegment(sketch, "E3116", {"start": v(-6.72, -50.02) * mm, "end": v(-6, -50.82) * mm});
            skLineSegment(sketch, "E3117", {"start": v(-6, -50.82) * mm, "end": v(-5.66, -51.76) * mm});
            skLineSegment(sketch, "E3118", {"start": v(-5.66, -51.76) * mm, "end": v(-5.66, -52.07) * mm});
            skLineSegment(sketch, "E3119", {"start": v(-24.67, -52.07) * mm, "end": v(-24.67, -52.38) * mm});
            skLineSegment(sketch, "E3120", {"start": v(-24.67, -52.38) * mm, "end": v(-25, -53.32) * mm});
            skLineSegment(sketch, "E3121", {"start": v(-25, -53.32) * mm, "end": v(-25.72, -54.12) * mm});
            skLineSegment(sketch, "E3122", {"start": v(-25.72, -54.12) * mm, "end": v(-25.91, -54.24) * mm});
            skLineSegment(sketch, "E3123", {"start": v(-25.91, -54.24) * mm, "end": v(-26.1, -54.35) * mm});
            skLineSegment(sketch, "E3124", {"start": v(-26.1, -54.35) * mm, "end": v(-27.16, -54.57) * mm});
            skLineSegment(sketch, "E3125", {"start": v(-27.16, -54.57) * mm, "end": v(-28.22, -54.35) * mm});
            skLineSegment(sketch, "E3126", {"start": v(-28.22, -54.35) * mm, "end": v(-28.41, -54.24) * mm});
            skLineSegment(sketch, "E3127", {"start": v(-28.41, -54.24) * mm, "end": v(-28.6, -54.12) * mm});
            skLineSegment(sketch, "E3128", {"start": v(-28.6, -54.12) * mm, "end": v(-29.33, -53.32) * mm});
            skLineSegment(sketch, "E3129", {"start": v(-29.33, -53.32) * mm, "end": v(-29.66, -52.38) * mm});
            skLineSegment(sketch, "E3130", {"start": v(-29.66, -52.38) * mm, "end": v(-29.66, -52.07) * mm});
            skLineSegment(sketch, "E3131", {"start": v(-29.66, -52.07) * mm, "end": v(-29.66, -51.76) * mm});
            skLineSegment(sketch, "E3132", {"start": v(-29.66, -51.76) * mm, "end": v(-29.33, -50.82) * mm});
            skLineSegment(sketch, "E3133", {"start": v(-29.33, -50.82) * mm, "end": v(-28.6, -50.02) * mm});
            skLineSegment(sketch, "E3134", {"start": v(-28.6, -50.02) * mm, "end": v(-28.41, -49.9) * mm});
            skLineSegment(sketch, "E3135", {"start": v(-28.41, -49.9) * mm, "end": v(-28.22, -49.8) * mm});
            skLineSegment(sketch, "E3136", {"start": v(-28.22, -49.8) * mm, "end": v(-27.16, -49.57) * mm});
            skLineSegment(sketch, "E3137", {"start": v(-27.16, -49.57) * mm, "end": v(-26.1, -49.8) * mm});
            skLineSegment(sketch, "E3138", {"start": v(-26.1, -49.8) * mm, "end": v(-25.91, -49.9) * mm});
            skLineSegment(sketch, "E3139", {"start": v(-25.91, -49.9) * mm, "end": v(-25.72, -50.02) * mm});
            skLineSegment(sketch, "E3140", {"start": v(-25.72, -50.02) * mm, "end": v(-25, -50.82) * mm});
            skLineSegment(sketch, "E3141", {"start": v(-25, -50.82) * mm, "end": v(-24.67, -51.76) * mm});
            skLineSegment(sketch, "E3142", {"start": v(-24.67, -51.76) * mm, "end": v(-24.67, -52.07) * mm});
            skLineSegment(sketch, "E3143", {"start": v(51.3, 5.1) * mm, "end": v(51.3, 4.96) * mm});
            skLineSegment(sketch, "E3144", {"start": v(51.3, 4.96) * mm, "end": v(51.16, 4.55) * mm});
            skLineSegment(sketch, "E3145", {"start": v(51.16, 4.55) * mm, "end": v(50.84, 4.2) * mm});
            skLineSegment(sketch, "E3146", {"start": v(50.84, 4.2) * mm, "end": v(50.75, 4.15) * mm});
            skLineSegment(sketch, "E3147", {"start": v(50.75, 4.15) * mm, "end": v(50.67, 4.1) * mm});
            skLineSegment(sketch, "E3148", {"start": v(50.67, 4.1) * mm, "end": v(50.2, 4) * mm});
            skLineSegment(sketch, "E3149", {"start": v(50.2, 4) * mm, "end": v(49.74, 4.1) * mm});
            skLineSegment(sketch, "E3150", {"start": v(49.74, 4.1) * mm, "end": v(49.65, 4.15) * mm});
            skLineSegment(sketch, "E3151", {"start": v(49.65, 4.15) * mm, "end": v(49.57, 4.2) * mm});
            skLineSegment(sketch, "E3152", {"start": v(49.57, 4.2) * mm, "end": v(49.25, 4.55) * mm});
            skLineSegment(sketch, "E3153", {"start": v(49.25, 4.55) * mm, "end": v(49.1, 4.96) * mm});
            skLineSegment(sketch, "E3154", {"start": v(49.1, 4.96) * mm, "end": v(49.1, 5.1) * mm});
            skLineSegment(sketch, "E3155", {"start": v(49.1, 5.1) * mm, "end": v(49.1, 5.24) * mm});
            skLineSegment(sketch, "E3156", {"start": v(49.1, 5.24) * mm, "end": v(49.25, 5.65) * mm});
            skLineSegment(sketch, "E3157", {"start": v(49.25, 5.65) * mm, "end": v(49.57, 6) * mm});
            skLineSegment(sketch, "E3158", {"start": v(49.57, 6) * mm, "end": v(49.65, 6.05) * mm});
            skLineSegment(sketch, "E3159", {"start": v(49.65, 6.05) * mm, "end": v(49.74, 6.1) * mm});
            skLineSegment(sketch, "E3160", {"start": v(49.74, 6.1) * mm, "end": v(50.2, 6.2) * mm});
            skLineSegment(sketch, "E3161", {"start": v(50.2, 6.2) * mm, "end": v(50.67, 6.1) * mm});
            skLineSegment(sketch, "E3162", {"start": v(50.67, 6.1) * mm, "end": v(50.75, 6.05) * mm});
            skLineSegment(sketch, "E3163", {"start": v(50.75, 6.05) * mm, "end": v(50.84, 6) * mm});
            skLineSegment(sketch, "E3164", {"start": v(50.84, 6) * mm, "end": v(51.16, 5.65) * mm});
            skLineSegment(sketch, "E3165", {"start": v(51.16, 5.65) * mm, "end": v(51.3, 5.24) * mm});
            skLineSegment(sketch, "E3166", {"start": v(51.3, 5.24) * mm, "end": v(51.3, 5.1) * mm});
            skLineSegment(sketch, "E3167", {"start": v(51.3, -5.1) * mm, "end": v(51.3, -5.24) * mm});
            skLineSegment(sketch, "E3168", {"start": v(51.3, -5.24) * mm, "end": v(51.16, -5.65) * mm});
            skLineSegment(sketch, "E3169", {"start": v(51.16, -5.65) * mm, "end": v(50.84, -6) * mm});
            skLineSegment(sketch, "E3170", {"start": v(50.84, -6) * mm, "end": v(50.75, -6.05) * mm});
            skLineSegment(sketch, "E3171", {"start": v(50.75, -6.05) * mm, "end": v(50.67, -6.1) * mm});
            skLineSegment(sketch, "E3172", {"start": v(50.67, -6.1) * mm, "end": v(50.2, -6.2) * mm});
            skLineSegment(sketch, "E3173", {"start": v(50.2, -6.2) * mm, "end": v(49.74, -6.1) * mm});
            skLineSegment(sketch, "E3174", {"start": v(49.74, -6.1) * mm, "end": v(49.65, -6.05) * mm});
            skLineSegment(sketch, "E3175", {"start": v(49.65, -6.05) * mm, "end": v(49.57, -6) * mm});
            skLineSegment(sketch, "E3176", {"start": v(49.57, -6) * mm, "end": v(49.25, -5.65) * mm});
            skLineSegment(sketch, "E3177", {"start": v(49.25, -5.65) * mm, "end": v(49.1, -5.24) * mm});
            skLineSegment(sketch, "E3178", {"start": v(49.1, -5.24) * mm, "end": v(49.1, -5.1) * mm});
            skLineSegment(sketch, "E3179", {"start": v(49.1, -5.1) * mm, "end": v(49.1, -4.96) * mm});
            skLineSegment(sketch, "E3180", {"start": v(49.1, -4.96) * mm, "end": v(49.25, -4.55) * mm});
            skLineSegment(sketch, "E3181", {"start": v(49.25, -4.55) * mm, "end": v(49.57, -4.2) * mm});
            skLineSegment(sketch, "E3182", {"start": v(49.57, -4.2) * mm, "end": v(49.65, -4.15) * mm});
            skLineSegment(sketch, "E3183", {"start": v(49.65, -4.15) * mm, "end": v(49.74, -4.1) * mm});
            skLineSegment(sketch, "E3184", {"start": v(49.74, -4.1) * mm, "end": v(50.2, -4) * mm});
            skLineSegment(sketch, "E3185", {"start": v(50.2, -4) * mm, "end": v(50.67, -4.1) * mm});
            skLineSegment(sketch, "E3186", {"start": v(50.67, -4.1) * mm, "end": v(50.75, -4.15) * mm});
            skLineSegment(sketch, "E3187", {"start": v(50.75, -4.15) * mm, "end": v(50.84, -4.2) * mm});
            skLineSegment(sketch, "E3188", {"start": v(50.84, -4.2) * mm, "end": v(51.16, -4.55) * mm});
            skLineSegment(sketch, "E3189", {"start": v(51.16, -4.55) * mm, "end": v(51.3, -4.96) * mm});
            skLineSegment(sketch, "E3190", {"start": v(51.3, -4.96) * mm, "end": v(51.3, -5.1) * mm});
            skLineSegment(sketch, "E3191", {"start": v(46.44, 0) * mm, "end": v(46.44, -0.1) * mm});
            skLineSegment(sketch, "E3192", {"start": v(46.44, -0.1) * mm, "end": v(46.23, -0.41) * mm});
            skLineSegment(sketch, "E3193", {"start": v(46.23, -0.41) * mm, "end": v(46.19, -0.43) * mm});
            skLineSegment(sketch, "E3194", {"start": v(46.19, -0.43) * mm, "end": v(46.15, -0.45) * mm});
            skLineSegment(sketch, "E3195", {"start": v(46.15, -0.45) * mm, "end": v(45.73, -0.45) * mm});
            skLineSegment(sketch, "E3196", {"start": v(45.73, -0.45) * mm, "end": v(45.69, -0.43) * mm});
            skLineSegment(sketch, "E3197", {"start": v(45.69, -0.43) * mm, "end": v(45.65, -0.41) * mm});
            skLineSegment(sketch, "E3198", {"start": v(45.65, -0.41) * mm, "end": v(45.44, -0.1) * mm});
            skLineSegment(sketch, "E3199", {"start": v(45.44, -0.1) * mm, "end": v(45.44, 0) * mm});
            skLineSegment(sketch, "E3200", {"start": v(45.44, 0) * mm, "end": v(45.44, 0.1) * mm});
            skLineSegment(sketch, "E3201", {"start": v(45.44, 0.1) * mm, "end": v(45.65, 0.41) * mm});
            skLineSegment(sketch, "E3202", {"start": v(45.65, 0.41) * mm, "end": v(45.69, 0.43) * mm});
            skLineSegment(sketch, "E3203", {"start": v(45.69, 0.43) * mm, "end": v(45.73, 0.46) * mm});
            skLineSegment(sketch, "E3204", {"start": v(45.73, 0.46) * mm, "end": v(46.15, 0.46) * mm});
            skLineSegment(sketch, "E3205", {"start": v(46.15, 0.46) * mm, "end": v(46.19, 0.43) * mm});
            skLineSegment(sketch, "E3206", {"start": v(46.19, 0.43) * mm, "end": v(46.23, 0.41) * mm});
            skLineSegment(sketch, "E3207", {"start": v(46.23, 0.41) * mm, "end": v(46.44, 0.1) * mm});
            skLineSegment(sketch, "E3208", {"start": v(46.44, 0.1) * mm, "end": v(46.44, 0) * mm});
            skLineSegment(sketch, "E3209", {"start": v(46.44, 2.5) * mm, "end": v(46.44, 2.4) * mm});
            skLineSegment(sketch, "E3210", {"start": v(46.44, 2.4) * mm, "end": v(46.23, 2.09) * mm});
            skLineSegment(sketch, "E3211", {"start": v(46.23, 2.09) * mm, "end": v(46.19, 2.07) * mm});
            skLineSegment(sketch, "E3212", {"start": v(46.19, 2.07) * mm, "end": v(46.15, 2.04) * mm});
            skLineSegment(sketch, "E3213", {"start": v(46.15, 2.04) * mm, "end": v(45.73, 2.04) * mm});
            skLineSegment(sketch, "E3214", {"start": v(45.73, 2.04) * mm, "end": v(45.69, 2.07) * mm});
            skLineSegment(sketch, "E3215", {"start": v(45.69, 2.07) * mm, "end": v(45.65, 2.09) * mm});
            skLineSegment(sketch, "E3216", {"start": v(45.65, 2.09) * mm, "end": v(45.44, 2.4) * mm});
            skLineSegment(sketch, "E3217", {"start": v(45.44, 2.4) * mm, "end": v(45.44, 2.5) * mm});
            skLineSegment(sketch, "E3218", {"start": v(45.44, 2.5) * mm, "end": v(45.44, 2.6) * mm});
            skLineSegment(sketch, "E3219", {"start": v(45.44, 2.6) * mm, "end": v(45.65, 2.91) * mm});
            skLineSegment(sketch, "E3220", {"start": v(45.65, 2.91) * mm, "end": v(45.69, 2.93) * mm});
            skLineSegment(sketch, "E3221", {"start": v(45.69, 2.93) * mm, "end": v(45.73, 2.96) * mm});
            skLineSegment(sketch, "E3222", {"start": v(45.73, 2.96) * mm, "end": v(46.15, 2.96) * mm});
            skLineSegment(sketch, "E3223", {"start": v(46.15, 2.96) * mm, "end": v(46.19, 2.93) * mm});
            skLineSegment(sketch, "E3224", {"start": v(46.19, 2.93) * mm, "end": v(46.23, 2.91) * mm});
            skLineSegment(sketch, "E3225", {"start": v(46.23, 2.91) * mm, "end": v(46.44, 2.6) * mm});
            skLineSegment(sketch, "E3226", {"start": v(46.44, 2.6) * mm, "end": v(46.44, 2.5) * mm});
            skLineSegment(sketch, "E3227", {"start": v(-22.61, 13.9) * mm, "end": v(-22.61, 13.81) * mm});
            skLineSegment(sketch, "E3228", {"start": v(-22.61, 13.81) * mm, "end": v(-22.78, 13.58) * mm});
            skLineSegment(sketch, "E3229", {"start": v(-22.78, 13.58) * mm, "end": v(-22.8, 13.57) * mm});
            skLineSegment(sketch, "E3230", {"start": v(-22.8, 13.57) * mm, "end": v(-22.83, 13.55) * mm});
            skLineSegment(sketch, "E3231", {"start": v(-22.83, 13.55) * mm, "end": v(-23.16, 13.55) * mm});
            skLineSegment(sketch, "E3232", {"start": v(-23.16, 13.55) * mm, "end": v(-23.18, 13.57) * mm});
            skLineSegment(sketch, "E3233", {"start": v(-23.18, 13.57) * mm, "end": v(-23.21, 13.58) * mm});
            skLineSegment(sketch, "E3234", {"start": v(-23.21, 13.58) * mm, "end": v(-23.37, 13.82) * mm});
            skLineSegment(sketch, "E3235", {"start": v(-23.37, 13.82) * mm, "end": v(-23.37, 13.9) * mm});
            skLineSegment(sketch, "E3236", {"start": v(-23.37, 13.9) * mm, "end": v(-23.37, 13.98) * mm});
            skLineSegment(sketch, "E3237", {"start": v(-23.37, 13.98) * mm, "end": v(-23.21, 14.2) * mm});
            skLineSegment(sketch, "E3238", {"start": v(-23.21, 14.2) * mm, "end": v(-23.18, 14.23) * mm});
            skLineSegment(sketch, "E3239", {"start": v(-23.18, 14.23) * mm, "end": v(-23.16, 14.24) * mm});
            skLineSegment(sketch, "E3240", {"start": v(-23.16, 14.24) * mm, "end": v(-22.83, 14.24) * mm});
            skLineSegment(sketch, "E3241", {"start": v(-22.83, 14.24) * mm, "end": v(-22.8, 14.23) * mm});
            skLineSegment(sketch, "E3242", {"start": v(-22.8, 14.23) * mm, "end": v(-22.78, 14.2) * mm});
            skLineSegment(sketch, "E3243", {"start": v(-22.78, 14.2) * mm, "end": v(-22.61, 13.97) * mm});
            skLineSegment(sketch, "E3244", {"start": v(-22.61, 13.97) * mm, "end": v(-22.61, 13.9) * mm});
            skLineSegment(sketch, "E3245", {"start": v(-22.23, 12.44) * mm, "end": v(-22.23, 12.35) * mm});
            skLineSegment(sketch, "E3246", {"start": v(-22.23, 12.35) * mm, "end": v(-22.4, 12.12) * mm});
            skLineSegment(sketch, "E3247", {"start": v(-22.4, 12.12) * mm, "end": v(-22.42, 12.1) * mm});
            skLineSegment(sketch, "E3248", {"start": v(-22.42, 12.1) * mm, "end": v(-22.45, 12.09) * mm});
            skLineSegment(sketch, "E3249", {"start": v(-22.45, 12.09) * mm, "end": v(-22.78, 12.09) * mm});
            skLineSegment(sketch, "E3250", {"start": v(-22.78, 12.09) * mm, "end": v(-22.8, 12.1) * mm});
            skLineSegment(sketch, "E3251", {"start": v(-22.8, 12.1) * mm, "end": v(-22.83, 12.12) * mm});
            skLineSegment(sketch, "E3252", {"start": v(-22.83, 12.12) * mm, "end": v(-23, 12.36) * mm});
            skLineSegment(sketch, "E3253", {"start": v(-23, 12.36) * mm, "end": v(-23, 12.44) * mm});
            skLineSegment(sketch, "E3254", {"start": v(-23, 12.44) * mm, "end": v(-23, 12.52) * mm});
            skLineSegment(sketch, "E3255", {"start": v(-23, 12.52) * mm, "end": v(-22.83, 12.75) * mm});
            skLineSegment(sketch, "E3256", {"start": v(-22.83, 12.75) * mm, "end": v(-22.8, 12.76) * mm});
            skLineSegment(sketch, "E3257", {"start": v(-22.8, 12.76) * mm, "end": v(-22.78, 12.78) * mm});
            skLineSegment(sketch, "E3258", {"start": v(-22.78, 12.78) * mm, "end": v(-22.45, 12.78) * mm});
            skLineSegment(sketch, "E3259", {"start": v(-22.45, 12.78) * mm, "end": v(-22.42, 12.76) * mm});
            skLineSegment(sketch, "E3260", {"start": v(-22.42, 12.76) * mm, "end": v(-22.4, 12.75) * mm});
            skLineSegment(sketch, "E3261", {"start": v(-22.4, 12.75) * mm, "end": v(-22.23, 12.51) * mm});
            skLineSegment(sketch, "E3262", {"start": v(-22.23, 12.51) * mm, "end": v(-22.23, 12.44) * mm});
            skLineSegment(sketch, "E3263", {"start": v(5.07, 12.63) * mm, "end": v(5.07, 12.54) * mm});
            skLineSegment(sketch, "E3264", {"start": v(5.07, 12.54) * mm, "end": v(4.91, 12.31) * mm});
            skLineSegment(sketch, "E3265", {"start": v(4.91, 12.31) * mm, "end": v(4.88, 12.3) * mm});
            skLineSegment(sketch, "E3266", {"start": v(4.88, 12.3) * mm, "end": v(4.85, 12.28) * mm});
            skLineSegment(sketch, "E3267", {"start": v(4.85, 12.28) * mm, "end": v(4.53, 12.28) * mm});
            skLineSegment(sketch, "E3268", {"start": v(4.53, 12.28) * mm, "end": v(4.5, 12.3) * mm});
            skLineSegment(sketch, "E3269", {"start": v(4.5, 12.3) * mm, "end": v(4.47, 12.31) * mm});
            skLineSegment(sketch, "E3270", {"start": v(4.47, 12.31) * mm, "end": v(4.31, 12.55) * mm});
            skLineSegment(sketch, "E3271", {"start": v(4.31, 12.55) * mm, "end": v(4.31, 12.63) * mm});
            skLineSegment(sketch, "E3272", {"start": v(4.31, 12.63) * mm, "end": v(4.31, 12.7) * mm});
            skLineSegment(sketch, "E3273", {"start": v(4.31, 12.7) * mm, "end": v(4.47, 12.94) * mm});
            skLineSegment(sketch, "E3274", {"start": v(4.47, 12.94) * mm, "end": v(4.5, 12.96) * mm});
            skLineSegment(sketch, "E3275", {"start": v(4.5, 12.96) * mm, "end": v(4.53, 12.97) * mm});
            skLineSegment(sketch, "E3276", {"start": v(4.53, 12.97) * mm, "end": v(4.85, 12.97) * mm});
            skLineSegment(sketch, "E3277", {"start": v(4.85, 12.97) * mm, "end": v(4.88, 12.96) * mm});
            skLineSegment(sketch, "E3278", {"start": v(4.88, 12.96) * mm, "end": v(4.91, 12.94) * mm});
            skLineSegment(sketch, "E3279", {"start": v(4.91, 12.94) * mm, "end": v(5.07, 12.7) * mm});
            skLineSegment(sketch, "E3280", {"start": v(5.07, 12.7) * mm, "end": v(5.07, 12.63) * mm});
            skLineSegment(sketch, "E3281", {"start": v(0.68, 17.98) * mm, "end": v(0.68, 17.9) * mm});
            skLineSegment(sketch, "E3282", {"start": v(0.68, 17.9) * mm, "end": v(0.52, 17.67) * mm});
            skLineSegment(sketch, "E3283", {"start": v(0.52, 17.67) * mm, "end": v(0.49, 17.66) * mm});
            skLineSegment(sketch, "E3284", {"start": v(0.49, 17.66) * mm, "end": v(0.46, 17.64) * mm});
            skLineSegment(sketch, "E3285", {"start": v(0.46, 17.64) * mm, "end": v(0.14, 17.64) * mm});
            skLineSegment(sketch, "E3286", {"start": v(0.14, 17.64) * mm, "end": v(0.1, 17.66) * mm});
            skLineSegment(sketch, "E3287", {"start": v(0.1, 17.66) * mm, "end": v(0.08, 17.67) * mm});
            skLineSegment(sketch, "E3288", {"start": v(0.08, 17.67) * mm, "end": v(-0.08, 17.9) * mm});
            skLineSegment(sketch, "E3289", {"start": v(-0.08, 17.9) * mm, "end": v(-0.08, 17.98) * mm});
            skLineSegment(sketch, "E3290", {"start": v(-0.08, 17.98) * mm, "end": v(-0.08, 18.05) * mm});
            skLineSegment(sketch, "E3291", {"start": v(-0.08, 18.05) * mm, "end": v(0.03, 18.25) * mm});
            skLineSegment(sketch, "E3292", {"start": v(0.03, 18.25) * mm, "end": v(0.23, 18.37) * mm});
            skLineSegment(sketch, "E3293", {"start": v(0.23, 18.37) * mm, "end": v(0.3, 18.37) * mm});
            skLineSegment(sketch, "E3294", {"start": v(0.3, 18.37) * mm, "end": v(0.36, 18.37) * mm});
            skLineSegment(sketch, "E3295", {"start": v(0.36, 18.37) * mm, "end": v(0.57, 18.25) * mm});
            skLineSegment(sketch, "E3296", {"start": v(0.57, 18.25) * mm, "end": v(0.68, 18.05) * mm});
            skLineSegment(sketch, "E3297", {"start": v(0.68, 18.05) * mm, "end": v(0.68, 17.98) * mm});
            skLineSegment(sketch, "E3298", {"start": v(-1.4, 19.93) * mm, "end": v(-1.4, 19.85) * mm});
            skLineSegment(sketch, "E3299", {"start": v(-1.4, 19.85) * mm, "end": v(-1.57, 19.62) * mm});
            skLineSegment(sketch, "E3300", {"start": v(-1.57, 19.62) * mm, "end": v(-1.6, 19.6) * mm});
            skLineSegment(sketch, "E3301", {"start": v(-1.6, 19.6) * mm, "end": v(-1.63, 19.58) * mm});
            skLineSegment(sketch, "E3302", {"start": v(-1.63, 19.58) * mm, "end": v(-1.95, 19.58) * mm});
            skLineSegment(sketch, "E3303", {"start": v(-1.95, 19.58) * mm, "end": v(-1.98, 19.6) * mm});
            skLineSegment(sketch, "E3304", {"start": v(-1.98, 19.6) * mm, "end": v(-2, 19.62) * mm});
            skLineSegment(sketch, "E3305", {"start": v(-2, 19.62) * mm, "end": v(-2.17, 19.85) * mm});
            skLineSegment(sketch, "E3306", {"start": v(-2.17, 19.85) * mm, "end": v(-2.17, 19.93) * mm});
            skLineSegment(sketch, "E3307", {"start": v(-2.17, 19.93) * mm, "end": v(-2.17, 20.01) * mm});
            skLineSegment(sketch, "E3308", {"start": v(-2.17, 20.01) * mm, "end": v(-2, 20.24) * mm});
            skLineSegment(sketch, "E3309", {"start": v(-2, 20.24) * mm, "end": v(-1.98, 20.26) * mm});
            skLineSegment(sketch, "E3310", {"start": v(-1.98, 20.26) * mm, "end": v(-1.95, 20.28) * mm});
            skLineSegment(sketch, "E3311", {"start": v(-1.95, 20.28) * mm, "end": v(-1.63, 20.28) * mm});
            skLineSegment(sketch, "E3312", {"start": v(-1.63, 20.28) * mm, "end": v(-1.6, 20.26) * mm});
            skLineSegment(sketch, "E3313", {"start": v(-1.6, 20.26) * mm, "end": v(-1.57, 20.24) * mm});
            skLineSegment(sketch, "E3314", {"start": v(-1.57, 20.24) * mm, "end": v(-1.4, 20) * mm});
            skLineSegment(sketch, "E3315", {"start": v(-1.4, 20) * mm, "end": v(-1.4, 19.93) * mm});
            skLineSegment(sketch, "E3316", {"start": v(2.6, 21.77) * mm, "end": v(2.6, 21.69) * mm});
            skLineSegment(sketch, "E3317", {"start": v(2.6, 21.69) * mm, "end": v(2.43, 21.46) * mm});
            skLineSegment(sketch, "E3318", {"start": v(2.43, 21.46) * mm, "end": v(2.4, 21.44) * mm});
            skLineSegment(sketch, "E3319", {"start": v(2.4, 21.44) * mm, "end": v(2.38, 21.42) * mm});
            skLineSegment(sketch, "E3320", {"start": v(2.38, 21.42) * mm, "end": v(2.05, 21.42) * mm});
            skLineSegment(sketch, "E3321", {"start": v(2.05, 21.42) * mm, "end": v(2.03, 21.44) * mm});
            skLineSegment(sketch, "E3322", {"start": v(2.03, 21.44) * mm, "end": v(2, 21.46) * mm});
            skLineSegment(sketch, "E3323", {"start": v(2, 21.46) * mm, "end": v(1.84, 21.7) * mm});
            skLineSegment(sketch, "E3324", {"start": v(1.84, 21.7) * mm, "end": v(1.84, 21.77) * mm});
            skLineSegment(sketch, "E3325", {"start": v(1.84, 21.77) * mm, "end": v(1.84, 21.85) * mm});
            skLineSegment(sketch, "E3326", {"start": v(1.84, 21.85) * mm, "end": v(2, 22.08) * mm});
            skLineSegment(sketch, "E3327", {"start": v(2, 22.08) * mm, "end": v(2.03, 22.1) * mm});
            skLineSegment(sketch, "E3328", {"start": v(2.03, 22.1) * mm, "end": v(2.05, 22.12) * mm});
            skLineSegment(sketch, "E3329", {"start": v(2.05, 22.12) * mm, "end": v(2.38, 22.12) * mm});
            skLineSegment(sketch, "E3330", {"start": v(2.38, 22.12) * mm, "end": v(2.4, 22.1) * mm});
            skLineSegment(sketch, "E3331", {"start": v(2.4, 22.1) * mm, "end": v(2.43, 22.08) * mm});
            skLineSegment(sketch, "E3332", {"start": v(2.43, 22.08) * mm, "end": v(2.6, 21.85) * mm});
            skLineSegment(sketch, "E3333", {"start": v(2.6, 21.85) * mm, "end": v(2.6, 21.77) * mm});
            skLineSegment(sketch, "E3334", {"start": v(12.44, 12.88) * mm, "end": v(12.44, 12.8) * mm});
            skLineSegment(sketch, "E3335", {"start": v(12.44, 12.8) * mm, "end": v(12.28, 12.57) * mm});
            skLineSegment(sketch, "E3336", {"start": v(12.28, 12.57) * mm, "end": v(12.25, 12.55) * mm});
            skLineSegment(sketch, "E3337", {"start": v(12.25, 12.55) * mm, "end": v(12.22, 12.53) * mm});
            skLineSegment(sketch, "E3338", {"start": v(12.22, 12.53) * mm, "end": v(11.9, 12.53) * mm});
            skLineSegment(sketch, "E3339", {"start": v(11.9, 12.53) * mm, "end": v(11.87, 12.55) * mm});
            skLineSegment(sketch, "E3340", {"start": v(11.87, 12.55) * mm, "end": v(11.84, 12.57) * mm});
            skLineSegment(sketch, "E3341", {"start": v(11.84, 12.57) * mm, "end": v(11.68, 12.8) * mm});
            skLineSegment(sketch, "E3342", {"start": v(11.68, 12.8) * mm, "end": v(11.68, 12.88) * mm});
            skLineSegment(sketch, "E3343", {"start": v(11.68, 12.88) * mm, "end": v(11.68, 12.96) * mm});
            skLineSegment(sketch, "E3344", {"start": v(11.68, 12.96) * mm, "end": v(11.84, 13.2) * mm});
            skLineSegment(sketch, "E3345", {"start": v(11.84, 13.2) * mm, "end": v(11.87, 13.2) * mm});
            skLineSegment(sketch, "E3346", {"start": v(11.87, 13.2) * mm, "end": v(11.9, 13.23) * mm});
            skLineSegment(sketch, "E3347", {"start": v(11.9, 13.23) * mm, "end": v(12.22, 13.23) * mm});
            skLineSegment(sketch, "E3348", {"start": v(12.22, 13.23) * mm, "end": v(12.25, 13.2) * mm});
            skLineSegment(sketch, "E3349", {"start": v(12.25, 13.2) * mm, "end": v(12.28, 13.2) * mm});
            skLineSegment(sketch, "E3350", {"start": v(12.28, 13.2) * mm, "end": v(12.44, 12.96) * mm});
            skLineSegment(sketch, "E3351", {"start": v(12.44, 12.96) * mm, "end": v(12.44, 12.88) * mm});
            skLineSegment(sketch, "E3352", {"start": v(8.25, 22.79) * mm, "end": v(8.25, 22.7) * mm});
            skLineSegment(sketch, "E3353", {"start": v(8.25, 22.7) * mm, "end": v(8.09, 22.47) * mm});
            skLineSegment(sketch, "E3354", {"start": v(8.09, 22.47) * mm, "end": v(8.06, 22.46) * mm});
            skLineSegment(sketch, "E3355", {"start": v(8.06, 22.46) * mm, "end": v(8.03, 22.44) * mm});
            skLineSegment(sketch, "E3356", {"start": v(8.03, 22.44) * mm, "end": v(7.7, 22.44) * mm});
            skLineSegment(sketch, "E3357", {"start": v(7.7, 22.44) * mm, "end": v(7.68, 22.46) * mm});
            skLineSegment(sketch, "E3358", {"start": v(7.68, 22.46) * mm, "end": v(7.65, 22.47) * mm});
            skLineSegment(sketch, "E3359", {"start": v(7.65, 22.47) * mm, "end": v(7.49, 22.7) * mm});
            skLineSegment(sketch, "E3360", {"start": v(7.49, 22.7) * mm, "end": v(7.49, 22.79) * mm});
            skLineSegment(sketch, "E3361", {"start": v(7.49, 22.79) * mm, "end": v(7.49, 22.87) * mm});
            skLineSegment(sketch, "E3362", {"start": v(7.49, 22.87) * mm, "end": v(7.65, 23.1) * mm});
            skLineSegment(sketch, "E3363", {"start": v(7.65, 23.1) * mm, "end": v(7.68, 23.12) * mm});
            skLineSegment(sketch, "E3364", {"start": v(7.68, 23.12) * mm, "end": v(7.7, 23.13) * mm});
            skLineSegment(sketch, "E3365", {"start": v(7.7, 23.13) * mm, "end": v(8.03, 23.13) * mm});
            skLineSegment(sketch, "E3366", {"start": v(8.03, 23.13) * mm, "end": v(8.06, 23.12) * mm});
            skLineSegment(sketch, "E3367", {"start": v(8.06, 23.12) * mm, "end": v(8.09, 23.1) * mm});
            skLineSegment(sketch, "E3368", {"start": v(8.09, 23.1) * mm, "end": v(8.25, 22.86) * mm});
            skLineSegment(sketch, "E3369", {"start": v(8.25, 22.86) * mm, "end": v(8.25, 22.79) * mm});
            skLineSegment(sketch, "E3370", {"start": v(0.82, 23.3) * mm, "end": v(0.82, 23.21) * mm});
            skLineSegment(sketch, "E3371", {"start": v(0.82, 23.21) * mm, "end": v(0.66, 22.98) * mm});
            skLineSegment(sketch, "E3372", {"start": v(0.66, 22.98) * mm, "end": v(0.63, 22.96) * mm});
            skLineSegment(sketch, "E3373", {"start": v(0.63, 22.96) * mm, "end": v(0.6, 22.95) * mm});
            skLineSegment(sketch, "E3374", {"start": v(0.6, 22.95) * mm, "end": v(0.28, 22.95) * mm});
            skLineSegment(sketch, "E3375", {"start": v(0.28, 22.95) * mm, "end": v(0.25, 22.96) * mm});
            skLineSegment(sketch, "E3376", {"start": v(0.25, 22.96) * mm, "end": v(0.22, 22.98) * mm});
            skLineSegment(sketch, "E3377", {"start": v(0.22, 22.98) * mm, "end": v(0.06, 23.22) * mm});
            skLineSegment(sketch, "E3378", {"start": v(0.06, 23.22) * mm, "end": v(0.06, 23.3) * mm});
            skLineSegment(sketch, "E3379", {"start": v(0.06, 23.3) * mm, "end": v(0.06, 23.38) * mm});
            skLineSegment(sketch, "E3380", {"start": v(0.06, 23.38) * mm, "end": v(0.22, 23.6) * mm});
            skLineSegment(sketch, "E3381", {"start": v(0.22, 23.6) * mm, "end": v(0.25, 23.62) * mm});
            skLineSegment(sketch, "E3382", {"start": v(0.25, 23.62) * mm, "end": v(0.28, 23.64) * mm});
            skLineSegment(sketch, "E3383", {"start": v(0.28, 23.64) * mm, "end": v(0.6, 23.64) * mm});
            skLineSegment(sketch, "E3384", {"start": v(0.6, 23.64) * mm, "end": v(0.63, 23.62) * mm});
            skLineSegment(sketch, "E3385", {"start": v(0.63, 23.62) * mm, "end": v(0.66, 23.6) * mm});
            skLineSegment(sketch, "E3386", {"start": v(0.66, 23.6) * mm, "end": v(0.82, 23.37) * mm});
            skLineSegment(sketch, "E3387", {"start": v(0.82, 23.37) * mm, "end": v(0.82, 23.3) * mm});
            skLineSegment(sketch, "E3388", {"start": v(-3.25, 17.83) * mm, "end": v(-3.25, 17.75) * mm});
            skLineSegment(sketch, "E3389", {"start": v(-3.25, 17.75) * mm, "end": v(-3.4, 17.52) * mm});
            skLineSegment(sketch, "E3390", {"start": v(-3.4, 17.52) * mm, "end": v(-3.44, 17.5) * mm});
            skLineSegment(sketch, "E3391", {"start": v(-3.44, 17.5) * mm, "end": v(-3.47, 17.49) * mm});
            skLineSegment(sketch, "E3392", {"start": v(-3.47, 17.49) * mm, "end": v(-3.79, 17.49) * mm});
            skLineSegment(sketch, "E3393", {"start": v(-3.79, 17.49) * mm, "end": v(-3.82, 17.5) * mm});
            skLineSegment(sketch, "E3394", {"start": v(-3.82, 17.5) * mm, "end": v(-3.85, 17.52) * mm});
            skLineSegment(sketch, "E3395", {"start": v(-3.85, 17.52) * mm, "end": v(-4, 17.76) * mm});
            skLineSegment(sketch, "E3396", {"start": v(-4, 17.76) * mm, "end": v(-4, 17.83) * mm});
            skLineSegment(sketch, "E3397", {"start": v(-4, 17.83) * mm, "end": v(-4, 17.9) * mm});
            skLineSegment(sketch, "E3398", {"start": v(-4, 17.9) * mm, "end": v(-3.9, 18.1) * mm});
            skLineSegment(sketch, "E3399", {"start": v(-3.9, 18.1) * mm, "end": v(-3.7, 18.21) * mm});
            skLineSegment(sketch, "E3400", {"start": v(-3.7, 18.21) * mm, "end": v(-3.63, 18.21) * mm});
            skLineSegment(sketch, "E3401", {"start": v(-3.63, 18.21) * mm, "end": v(-3.56, 18.21) * mm});
            skLineSegment(sketch, "E3402", {"start": v(-3.56, 18.21) * mm, "end": v(-3.36, 18.1) * mm});
            skLineSegment(sketch, "E3403", {"start": v(-3.36, 18.1) * mm, "end": v(-3.25, 17.9) * mm});
            skLineSegment(sketch, "E3404", {"start": v(-3.25, 17.9) * mm, "end": v(-3.25, 17.83) * mm});
            skLineSegment(sketch, "E3405", {"start": v(-20.7, 16.18) * mm, "end": v(-20.7, 16.1) * mm});
            skLineSegment(sketch, "E3406", {"start": v(-20.7, 16.1) * mm, "end": v(-20.87, 15.87) * mm});
            skLineSegment(sketch, "E3407", {"start": v(-20.87, 15.87) * mm, "end": v(-20.9, 15.85) * mm});
            skLineSegment(sketch, "E3408", {"start": v(-20.9, 15.85) * mm, "end": v(-20.93, 15.84) * mm});
            skLineSegment(sketch, "E3409", {"start": v(-20.93, 15.84) * mm, "end": v(-21.25, 15.84) * mm});
            skLineSegment(sketch, "E3410", {"start": v(-21.25, 15.84) * mm, "end": v(-21.28, 15.85) * mm});
            skLineSegment(sketch, "E3411", {"start": v(-21.28, 15.85) * mm, "end": v(-21.31, 15.87) * mm});
            skLineSegment(sketch, "E3412", {"start": v(-21.31, 15.87) * mm, "end": v(-21.47, 16.1) * mm});
            skLineSegment(sketch, "E3413", {"start": v(-21.47, 16.1) * mm, "end": v(-21.47, 16.18) * mm});
            skLineSegment(sketch, "E3414", {"start": v(-21.47, 16.18) * mm, "end": v(-21.47, 16.26) * mm});
            skLineSegment(sketch, "E3415", {"start": v(-21.47, 16.26) * mm, "end": v(-21.31, 16.5) * mm});
            skLineSegment(sketch, "E3416", {"start": v(-21.31, 16.5) * mm, "end": v(-21.28, 16.51) * mm});
            skLineSegment(sketch, "E3417", {"start": v(-21.28, 16.51) * mm, "end": v(-21.25, 16.53) * mm});
            skLineSegment(sketch, "E3418", {"start": v(-21.25, 16.53) * mm, "end": v(-20.93, 16.53) * mm});
            skLineSegment(sketch, "E3419", {"start": v(-20.93, 16.53) * mm, "end": v(-20.9, 16.51) * mm});
            skLineSegment(sketch, "E3420", {"start": v(-20.9, 16.51) * mm, "end": v(-20.87, 16.5) * mm});
            skLineSegment(sketch, "E3421", {"start": v(-20.87, 16.5) * mm, "end": v(-20.7, 16.26) * mm});
            skLineSegment(sketch, "E3422", {"start": v(-20.7, 16.26) * mm, "end": v(-20.7, 16.18) * mm});
            skLineSegment(sketch, "E3423", {"start": v(-12.07, 14.66) * mm, "end": v(-12.07, 14.58) * mm});
            skLineSegment(sketch, "E3424", {"start": v(-12.07, 14.58) * mm, "end": v(-12.23, 14.35) * mm});
            skLineSegment(sketch, "E3425", {"start": v(-12.23, 14.35) * mm, "end": v(-12.26, 14.33) * mm});
            skLineSegment(sketch, "E3426", {"start": v(-12.26, 14.33) * mm, "end": v(-12.3, 14.31) * mm});
            skLineSegment(sketch, "E3427", {"start": v(-12.3, 14.31) * mm, "end": v(-12.62, 14.31) * mm});
            skLineSegment(sketch, "E3428", {"start": v(-12.62, 14.31) * mm, "end": v(-12.64, 14.33) * mm});
            skLineSegment(sketch, "E3429", {"start": v(-12.64, 14.33) * mm, "end": v(-12.67, 14.35) * mm});
            skLineSegment(sketch, "E3430", {"start": v(-12.67, 14.35) * mm, "end": v(-12.83, 14.58) * mm});
            skLineSegment(sketch, "E3431", {"start": v(-12.83, 14.58) * mm, "end": v(-12.83, 14.66) * mm});
            skLineSegment(sketch, "E3432", {"start": v(-12.83, 14.66) * mm, "end": v(-12.83, 14.74) * mm});
            skLineSegment(sketch, "E3433", {"start": v(-12.83, 14.74) * mm, "end": v(-12.67, 14.97) * mm});
            skLineSegment(sketch, "E3434", {"start": v(-12.67, 14.97) * mm, "end": v(-12.64, 14.99) * mm});
            skLineSegment(sketch, "E3435", {"start": v(-12.64, 14.99) * mm, "end": v(-12.62, 15) * mm});
            skLineSegment(sketch, "E3436", {"start": v(-12.62, 15) * mm, "end": v(-12.3, 15) * mm});
            skLineSegment(sketch, "E3437", {"start": v(-12.3, 15) * mm, "end": v(-12.26, 14.99) * mm});
            skLineSegment(sketch, "E3438", {"start": v(-12.26, 14.99) * mm, "end": v(-12.23, 14.97) * mm});
            skLineSegment(sketch, "E3439", {"start": v(-12.23, 14.97) * mm, "end": v(-12.07, 14.74) * mm});
            skLineSegment(sketch, "E3440", {"start": v(-12.07, 14.74) * mm, "end": v(-12.07, 14.66) * mm});
            skLineSegment(sketch, "E3441", {"start": v(-7.5, 17.13) * mm, "end": v(-7.5, 17.05) * mm});
            skLineSegment(sketch, "E3442", {"start": v(-7.5, 17.05) * mm, "end": v(-7.66, 16.82) * mm});
            skLineSegment(sketch, "E3443", {"start": v(-7.66, 16.82) * mm, "end": v(-7.69, 16.8) * mm});
            skLineSegment(sketch, "E3444", {"start": v(-7.69, 16.8) * mm, "end": v(-7.72, 16.79) * mm});
            skLineSegment(sketch, "E3445", {"start": v(-7.72, 16.79) * mm, "end": v(-8.04, 16.79) * mm});
            skLineSegment(sketch, "E3446", {"start": v(-8.04, 16.79) * mm, "end": v(-8.07, 16.8) * mm});
            skLineSegment(sketch, "E3447", {"start": v(-8.07, 16.8) * mm, "end": v(-8.1, 16.82) * mm});
            skLineSegment(sketch, "E3448", {"start": v(-8.1, 16.82) * mm, "end": v(-8.26, 17.06) * mm});
            skLineSegment(sketch, "E3449", {"start": v(-8.26, 17.06) * mm, "end": v(-8.26, 17.13) * mm});
            skLineSegment(sketch, "E3450", {"start": v(-8.26, 17.13) * mm, "end": v(-8.26, 17.22) * mm});
            skLineSegment(sketch, "E3451", {"start": v(-8.26, 17.22) * mm, "end": v(-8.1, 17.45) * mm});
            skLineSegment(sketch, "E3452", {"start": v(-8.1, 17.45) * mm, "end": v(-8.07, 17.46) * mm});
            skLineSegment(sketch, "E3453", {"start": v(-8.07, 17.46) * mm, "end": v(-8.04, 17.48) * mm});
            skLineSegment(sketch, "E3454", {"start": v(-8.04, 17.48) * mm, "end": v(-7.72, 17.48) * mm});
            skLineSegment(sketch, "E3455", {"start": v(-7.72, 17.48) * mm, "end": v(-7.69, 17.46) * mm});
            skLineSegment(sketch, "E3456", {"start": v(-7.69, 17.46) * mm, "end": v(-7.66, 17.45) * mm});
            skLineSegment(sketch, "E3457", {"start": v(-7.66, 17.45) * mm, "end": v(-7.5, 17.21) * mm});
            skLineSegment(sketch, "E3458", {"start": v(-7.5, 17.21) * mm, "end": v(-7.5, 17.13) * mm});
            skLineSegment(sketch, "E3459", {"start": v(-11.06, 18.98) * mm, "end": v(-11.06, 18.9) * mm});
            skLineSegment(sketch, "E3460", {"start": v(-11.06, 18.9) * mm, "end": v(-11.22, 18.66) * mm});
            skLineSegment(sketch, "E3461", {"start": v(-11.22, 18.66) * mm, "end": v(-11.25, 18.65) * mm});
            skLineSegment(sketch, "E3462", {"start": v(-11.25, 18.65) * mm, "end": v(-11.28, 18.63) * mm});
            skLineSegment(sketch, "E3463", {"start": v(-11.28, 18.63) * mm, "end": v(-11.6, 18.63) * mm});
            skLineSegment(sketch, "E3464", {"start": v(-11.6, 18.63) * mm, "end": v(-11.63, 18.65) * mm});
            skLineSegment(sketch, "E3465", {"start": v(-11.63, 18.65) * mm, "end": v(-11.66, 18.66) * mm});
            skLineSegment(sketch, "E3466", {"start": v(-11.66, 18.66) * mm, "end": v(-11.82, 18.9) * mm});
            skLineSegment(sketch, "E3467", {"start": v(-11.82, 18.9) * mm, "end": v(-11.82, 18.98) * mm});
            skLineSegment(sketch, "E3468", {"start": v(-11.82, 18.98) * mm, "end": v(-11.82, 19.04) * mm});
            skLineSegment(sketch, "E3469", {"start": v(-11.82, 19.04) * mm, "end": v(-11.7, 19.25) * mm});
            skLineSegment(sketch, "E3470", {"start": v(-11.7, 19.25) * mm, "end": v(-11.5, 19.36) * mm});
            skLineSegment(sketch, "E3471", {"start": v(-11.5, 19.36) * mm, "end": v(-11.44, 19.36) * mm});
            skLineSegment(sketch, "E3472", {"start": v(-11.44, 19.36) * mm, "end": v(-11.37, 19.36) * mm});
            skLineSegment(sketch, "E3473", {"start": v(-11.37, 19.36) * mm, "end": v(-11.17, 19.25) * mm});
            skLineSegment(sketch, "E3474", {"start": v(-11.17, 19.25) * mm, "end": v(-11.06, 19.04) * mm});
            skLineSegment(sketch, "E3475", {"start": v(-11.06, 19.04) * mm, "end": v(-11.06, 18.98) * mm});
            skLineSegment(sketch, "E3476", {"start": v(-6.3, 18.91) * mm, "end": v(-6.3, 18.83) * mm});
            skLineSegment(sketch, "E3477", {"start": v(-6.3, 18.83) * mm, "end": v(-6.46, 18.6) * mm});
            skLineSegment(sketch, "E3478", {"start": v(-6.46, 18.6) * mm, "end": v(-6.48, 18.58) * mm});
            skLineSegment(sketch, "E3479", {"start": v(-6.48, 18.58) * mm, "end": v(-6.51, 18.57) * mm});
            skLineSegment(sketch, "E3480", {"start": v(-6.51, 18.57) * mm, "end": v(-6.84, 18.57) * mm});
            skLineSegment(sketch, "E3481", {"start": v(-6.84, 18.57) * mm, "end": v(-6.86, 18.58) * mm});
            skLineSegment(sketch, "E3482", {"start": v(-6.86, 18.58) * mm, "end": v(-6.9, 18.6) * mm});
            skLineSegment(sketch, "E3483", {"start": v(-6.9, 18.6) * mm, "end": v(-7.06, 18.84) * mm});
            skLineSegment(sketch, "E3484", {"start": v(-7.06, 18.84) * mm, "end": v(-7.06, 18.91) * mm});
            skLineSegment(sketch, "E3485", {"start": v(-7.06, 18.91) * mm, "end": v(-7.06, 18.98) * mm});
            skLineSegment(sketch, "E3486", {"start": v(-7.06, 18.98) * mm, "end": v(-6.94, 19.18) * mm});
            skLineSegment(sketch, "E3487", {"start": v(-6.94, 19.18) * mm, "end": v(-6.74, 19.3) * mm});
            skLineSegment(sketch, "E3488", {"start": v(-6.74, 19.3) * mm, "end": v(-6.67, 19.3) * mm});
            skLineSegment(sketch, "E3489", {"start": v(-6.67, 19.3) * mm, "end": v(-6.6, 19.3) * mm});
            skLineSegment(sketch, "E3490", {"start": v(-6.6, 19.3) * mm, "end": v(-6.4, 19.18) * mm});
            skLineSegment(sketch, "E3491", {"start": v(-6.4, 19.18) * mm, "end": v(-6.3, 18.98) * mm});
            skLineSegment(sketch, "E3492", {"start": v(-6.3, 18.98) * mm, "end": v(-6.3, 18.91) * mm});
            skLineSegment(sketch, "E3493", {"start": v(12.95, 22.66) * mm, "end": v(12.95, 22.58) * mm});
            skLineSegment(sketch, "E3494", {"start": v(12.95, 22.58) * mm, "end": v(12.78, 22.35) * mm});
            skLineSegment(sketch, "E3495", {"start": v(12.78, 22.35) * mm, "end": v(12.76, 22.33) * mm});
            skLineSegment(sketch, "E3496", {"start": v(12.76, 22.33) * mm, "end": v(12.73, 22.31) * mm});
            skLineSegment(sketch, "E3497", {"start": v(12.73, 22.31) * mm, "end": v(12.4, 22.31) * mm});
            skLineSegment(sketch, "E3498", {"start": v(12.4, 22.31) * mm, "end": v(12.38, 22.33) * mm});
            skLineSegment(sketch, "E3499", {"start": v(12.38, 22.33) * mm, "end": v(12.35, 22.35) * mm});
            skLineSegment(sketch, "E3500", {"start": v(12.35, 22.35) * mm, "end": v(12.19, 22.58) * mm});
            skLineSegment(sketch, "E3501", {"start": v(12.19, 22.58) * mm, "end": v(12.19, 22.66) * mm});
            skLineSegment(sketch, "E3502", {"start": v(12.19, 22.66) * mm, "end": v(12.19, 22.73) * mm});
            skLineSegment(sketch, "E3503", {"start": v(12.19, 22.73) * mm, "end": v(12.3, 22.93) * mm});
            skLineSegment(sketch, "E3504", {"start": v(12.3, 22.93) * mm, "end": v(12.5, 23.04) * mm});
            skLineSegment(sketch, "E3505", {"start": v(12.5, 23.04) * mm, "end": v(12.57, 23.04) * mm});
            skLineSegment(sketch, "E3506", {"start": v(12.57, 23.04) * mm, "end": v(12.63, 23.04) * mm});
            skLineSegment(sketch, "E3507", {"start": v(12.63, 23.04) * mm, "end": v(12.83, 22.93) * mm});
            skLineSegment(sketch, "E3508", {"start": v(12.83, 22.93) * mm, "end": v(12.95, 22.73) * mm});
            skLineSegment(sketch, "E3509", {"start": v(12.95, 22.73) * mm, "end": v(12.95, 22.66) * mm});
            skLineSegment(sketch, "E3510", {"start": v(-8.83, 22.21) * mm, "end": v(-8.83, 22.13) * mm});
            skLineSegment(sketch, "E3511", {"start": v(-8.83, 22.13) * mm, "end": v(-9, 21.9) * mm});
            skLineSegment(sketch, "E3512", {"start": v(-9, 21.9) * mm, "end": v(-9.02, 21.88) * mm});
            skLineSegment(sketch, "E3513", {"start": v(-9.02, 21.88) * mm, "end": v(-9.05, 21.87) * mm});
            skLineSegment(sketch, "E3514", {"start": v(-9.05, 21.87) * mm, "end": v(-9.38, 21.87) * mm});
            skLineSegment(sketch, "E3515", {"start": v(-9.38, 21.87) * mm, "end": v(-9.4, 21.88) * mm});
            skLineSegment(sketch, "E3516", {"start": v(-9.4, 21.88) * mm, "end": v(-9.44, 21.9) * mm});
            skLineSegment(sketch, "E3517", {"start": v(-9.44, 21.9) * mm, "end": v(-9.6, 22.14) * mm});
            skLineSegment(sketch, "E3518", {"start": v(-9.6, 22.14) * mm, "end": v(-9.6, 22.21) * mm});
            skLineSegment(sketch, "E3519", {"start": v(-9.6, 22.21) * mm, "end": v(-9.6, 22.3) * mm});
            skLineSegment(sketch, "E3520", {"start": v(-9.6, 22.3) * mm, "end": v(-9.44, 22.53) * mm});
            skLineSegment(sketch, "E3521", {"start": v(-9.44, 22.53) * mm, "end": v(-9.4, 22.54) * mm});
            skLineSegment(sketch, "E3522", {"start": v(-9.4, 22.54) * mm, "end": v(-9.38, 22.56) * mm});
            skLineSegment(sketch, "E3523", {"start": v(-9.38, 22.56) * mm, "end": v(-9.05, 22.56) * mm});
            skLineSegment(sketch, "E3524", {"start": v(-9.05, 22.56) * mm, "end": v(-9.02, 22.54) * mm});
            skLineSegment(sketch, "E3525", {"start": v(-9.02, 22.54) * mm, "end": v(-9, 22.53) * mm});
            skLineSegment(sketch, "E3526", {"start": v(-9, 22.53) * mm, "end": v(-8.83, 22.3) * mm});
            skLineSegment(sketch, "E3527", {"start": v(-8.83, 22.3) * mm, "end": v(-8.83, 22.21) * mm});
            skLineSegment(sketch, "E3528", {"start": v(-12.39, 21.7) * mm, "end": v(-12.39, 21.62) * mm});
            skLineSegment(sketch, "E3529", {"start": v(-12.39, 21.62) * mm, "end": v(-12.55, 21.4) * mm});
            skLineSegment(sketch, "E3530", {"start": v(-12.55, 21.4) * mm, "end": v(-12.58, 21.38) * mm});
            skLineSegment(sketch, "E3531", {"start": v(-12.58, 21.38) * mm, "end": v(-12.61, 21.36) * mm});
            skLineSegment(sketch, "E3532", {"start": v(-12.61, 21.36) * mm, "end": v(-12.93, 21.36) * mm});
            skLineSegment(sketch, "E3533", {"start": v(-12.93, 21.36) * mm, "end": v(-12.96, 21.38) * mm});
            skLineSegment(sketch, "E3534", {"start": v(-12.96, 21.38) * mm, "end": v(-13, 21.4) * mm});
            skLineSegment(sketch, "E3535", {"start": v(-13, 21.4) * mm, "end": v(-13.15, 21.63) * mm});
            skLineSegment(sketch, "E3536", {"start": v(-13.15, 21.63) * mm, "end": v(-13.15, 21.7) * mm});
            skLineSegment(sketch, "E3537", {"start": v(-13.15, 21.7) * mm, "end": v(-13.15, 21.77) * mm});
            skLineSegment(sketch, "E3538", {"start": v(-13.15, 21.77) * mm, "end": v(-13.04, 21.98) * mm});
            skLineSegment(sketch, "E3539", {"start": v(-13.04, 21.98) * mm, "end": v(-12.84, 22.09) * mm});
            skLineSegment(sketch, "E3540", {"start": v(-12.84, 22.09) * mm, "end": v(-12.77, 22.09) * mm});
            skLineSegment(sketch, "E3541", {"start": v(-12.77, 22.09) * mm, "end": v(-12.7, 22.09) * mm});
            skLineSegment(sketch, "E3542", {"start": v(-12.7, 22.09) * mm, "end": v(-12.5, 21.98) * mm});
            skLineSegment(sketch, "E3543", {"start": v(-12.5, 21.98) * mm, "end": v(-12.39, 21.77) * mm});
            skLineSegment(sketch, "E3544", {"start": v(-12.39, 21.77) * mm, "end": v(-12.39, 21.7) * mm});
            skLineSegment(sketch, "E3545", {"start": v(-22.36, 21.7) * mm, "end": v(-22.36, 21.62) * mm});
            skLineSegment(sketch, "E3546", {"start": v(-22.36, 21.62) * mm, "end": v(-22.52, 21.4) * mm});
            skLineSegment(sketch, "E3547", {"start": v(-22.52, 21.4) * mm, "end": v(-22.55, 21.38) * mm});
            skLineSegment(sketch, "E3548", {"start": v(-22.55, 21.38) * mm, "end": v(-22.58, 21.36) * mm});
            skLineSegment(sketch, "E3549", {"start": v(-22.58, 21.36) * mm, "end": v(-22.9, 21.36) * mm});
            skLineSegment(sketch, "E3550", {"start": v(-22.9, 21.36) * mm, "end": v(-22.93, 21.38) * mm});
            skLineSegment(sketch, "E3551", {"start": v(-22.93, 21.38) * mm, "end": v(-22.96, 21.4) * mm});
            skLineSegment(sketch, "E3552", {"start": v(-22.96, 21.4) * mm, "end": v(-23.12, 21.63) * mm});
            skLineSegment(sketch, "E3553", {"start": v(-23.12, 21.63) * mm, "end": v(-23.12, 21.7) * mm});
            skLineSegment(sketch, "E3554", {"start": v(-23.12, 21.7) * mm, "end": v(-23.12, 21.79) * mm});
            skLineSegment(sketch, "E3555", {"start": v(-23.12, 21.79) * mm, "end": v(-22.96, 22.02) * mm});
            skLineSegment(sketch, "E3556", {"start": v(-22.96, 22.02) * mm, "end": v(-22.93, 22.04) * mm});
            skLineSegment(sketch, "E3557", {"start": v(-22.93, 22.04) * mm, "end": v(-22.9, 22.05) * mm});
            skLineSegment(sketch, "E3558", {"start": v(-22.9, 22.05) * mm, "end": v(-22.58, 22.05) * mm});
            skLineSegment(sketch, "E3559", {"start": v(-22.58, 22.05) * mm, "end": v(-22.55, 22.04) * mm});
            skLineSegment(sketch, "E3560", {"start": v(-22.55, 22.04) * mm, "end": v(-22.52, 22.02) * mm});
            skLineSegment(sketch, "E3561", {"start": v(-22.52, 22.02) * mm, "end": v(-22.36, 21.79) * mm});
            skLineSegment(sketch, "E3562", {"start": v(-22.36, 21.79) * mm, "end": v(-22.36, 21.7) * mm});
            skLineSegment(sketch, "E3563", {"start": v(-22.23, 19.67) * mm, "end": v(-22.23, 19.6) * mm});
            skLineSegment(sketch, "E3564", {"start": v(-22.23, 19.6) * mm, "end": v(-22.4, 19.36) * mm});
            skLineSegment(sketch, "E3565", {"start": v(-22.4, 19.36) * mm, "end": v(-22.42, 19.34) * mm});
            skLineSegment(sketch, "E3566", {"start": v(-22.42, 19.34) * mm, "end": v(-22.45, 19.33) * mm});
            skLineSegment(sketch, "E3567", {"start": v(-22.45, 19.33) * mm, "end": v(-22.78, 19.33) * mm});
            skLineSegment(sketch, "E3568", {"start": v(-22.78, 19.33) * mm, "end": v(-22.8, 19.34) * mm});
            skLineSegment(sketch, "E3569", {"start": v(-22.8, 19.34) * mm, "end": v(-22.83, 19.36) * mm});
            skLineSegment(sketch, "E3570", {"start": v(-22.83, 19.36) * mm, "end": v(-23, 19.6) * mm});
            skLineSegment(sketch, "E3571", {"start": v(-23, 19.6) * mm, "end": v(-23, 19.67) * mm});
            skLineSegment(sketch, "E3572", {"start": v(-23, 19.67) * mm, "end": v(-23, 19.76) * mm});
            skLineSegment(sketch, "E3573", {"start": v(-23, 19.76) * mm, "end": v(-22.83, 19.99) * mm});
            skLineSegment(sketch, "E3574", {"start": v(-22.83, 19.99) * mm, "end": v(-22.8, 20) * mm});
            skLineSegment(sketch, "E3575", {"start": v(-22.8, 20) * mm, "end": v(-22.78, 20.02) * mm});
            skLineSegment(sketch, "E3576", {"start": v(-22.78, 20.02) * mm, "end": v(-22.45, 20.02) * mm});
            skLineSegment(sketch, "E3577", {"start": v(-22.45, 20.02) * mm, "end": v(-22.42, 20) * mm});
            skLineSegment(sketch, "E3578", {"start": v(-22.42, 20) * mm, "end": v(-22.4, 19.99) * mm});
            skLineSegment(sketch, "E3579", {"start": v(-22.4, 19.99) * mm, "end": v(-22.23, 19.75) * mm});
            skLineSegment(sketch, "E3580", {"start": v(-22.23, 19.75) * mm, "end": v(-22.23, 19.67) * mm});
            skLineSegment(sketch, "E3581", {"start": v(-22.49, 23.42) * mm, "end": v(-22.49, 23.34) * mm});
            skLineSegment(sketch, "E3582", {"start": v(-22.49, 23.34) * mm, "end": v(-22.65, 23.1) * mm});
            skLineSegment(sketch, "E3583", {"start": v(-22.65, 23.1) * mm, "end": v(-22.68, 23.1) * mm});
            skLineSegment(sketch, "E3584", {"start": v(-22.68, 23.1) * mm, "end": v(-22.7, 23.07) * mm});
            skLineSegment(sketch, "E3585", {"start": v(-22.7, 23.07) * mm, "end": v(-23.03, 23.07) * mm});
            skLineSegment(sketch, "E3586", {"start": v(-23.03, 23.07) * mm, "end": v(-23.06, 23.1) * mm});
            skLineSegment(sketch, "E3587", {"start": v(-23.06, 23.1) * mm, "end": v(-23.09, 23.1) * mm});
            skLineSegment(sketch, "E3588", {"start": v(-23.09, 23.1) * mm, "end": v(-23.25, 23.34) * mm});
            skLineSegment(sketch, "E3589", {"start": v(-23.25, 23.34) * mm, "end": v(-23.25, 23.42) * mm});
            skLineSegment(sketch, "E3590", {"start": v(-23.25, 23.42) * mm, "end": v(-23.25, 23.49) * mm});
            skLineSegment(sketch, "E3591", {"start": v(-23.25, 23.49) * mm, "end": v(-23.14, 23.69) * mm});
            skLineSegment(sketch, "E3592", {"start": v(-23.14, 23.69) * mm, "end": v(-22.94, 23.8) * mm});
            skLineSegment(sketch, "E3593", {"start": v(-22.94, 23.8) * mm, "end": v(-22.87, 23.8) * mm});
            skLineSegment(sketch, "E3594", {"start": v(-22.87, 23.8) * mm, "end": v(-22.8, 23.8) * mm});
            skLineSegment(sketch, "E3595", {"start": v(-22.8, 23.8) * mm, "end": v(-22.6, 23.69) * mm});
            skLineSegment(sketch, "E3596", {"start": v(-22.6, 23.69) * mm, "end": v(-22.49, 23.49) * mm});
            skLineSegment(sketch, "E3597", {"start": v(-22.49, 23.49) * mm, "end": v(-22.49, 23.42) * mm});
            skLineSegment(sketch, "E3598", {"start": v(-52.56, 15.24) * mm, "end": v(-52.56, 15.12) * mm});
            skLineSegment(sketch, "E3599", {"start": v(-52.56, 15.12) * mm, "end": v(-52.7, 14.74) * mm});
            skLineSegment(sketch, "E3600", {"start": v(-52.7, 14.74) * mm, "end": v(-52.98, 14.42) * mm});
            skLineSegment(sketch, "E3601", {"start": v(-52.98, 14.42) * mm, "end": v(-53.06, 14.37) * mm});
            skLineSegment(sketch, "E3602", {"start": v(-53.06, 14.37) * mm, "end": v(-53.14, 14.33) * mm});
            skLineSegment(sketch, "E3603", {"start": v(-53.14, 14.33) * mm, "end": v(-53.56, 14.24) * mm});
            skLineSegment(sketch, "E3604", {"start": v(-53.56, 14.24) * mm, "end": v(-53.98, 14.33) * mm});
            skLineSegment(sketch, "E3605", {"start": v(-53.98, 14.33) * mm, "end": v(-54.06, 14.37) * mm});
            skLineSegment(sketch, "E3606", {"start": v(-54.06, 14.37) * mm, "end": v(-54.14, 14.42) * mm});
            skLineSegment(sketch, "E3607", {"start": v(-54.14, 14.42) * mm, "end": v(-54.42, 14.74) * mm});
            skLineSegment(sketch, "E3608", {"start": v(-54.42, 14.74) * mm, "end": v(-54.56, 15.12) * mm});
            skLineSegment(sketch, "E3609", {"start": v(-54.56, 15.12) * mm, "end": v(-54.56, 15.24) * mm});
            skLineSegment(sketch, "E3610", {"start": v(-54.56, 15.24) * mm, "end": v(-54.56, 15.37) * mm});
            skLineSegment(sketch, "E3611", {"start": v(-54.56, 15.37) * mm, "end": v(-54.42, 15.74) * mm});
            skLineSegment(sketch, "E3612", {"start": v(-54.42, 15.74) * mm, "end": v(-54.14, 16.06) * mm});
            skLineSegment(sketch, "E3613", {"start": v(-54.14, 16.06) * mm, "end": v(-54.06, 16.1) * mm});
            skLineSegment(sketch, "E3614", {"start": v(-54.06, 16.1) * mm, "end": v(-53.98, 16.15) * mm});
            skLineSegment(sketch, "E3615", {"start": v(-53.98, 16.15) * mm, "end": v(-53.56, 16.24) * mm});
            skLineSegment(sketch, "E3616", {"start": v(-53.56, 16.24) * mm, "end": v(-53.14, 16.15) * mm});
            skLineSegment(sketch, "E3617", {"start": v(-53.14, 16.15) * mm, "end": v(-53.06, 16.1) * mm});
            skLineSegment(sketch, "E3618", {"start": v(-53.06, 16.1) * mm, "end": v(-52.98, 16.06) * mm});
            skLineSegment(sketch, "E3619", {"start": v(-52.98, 16.06) * mm, "end": v(-52.7, 15.74) * mm});
            skLineSegment(sketch, "E3620", {"start": v(-52.7, 15.74) * mm, "end": v(-52.56, 15.37) * mm});
            skLineSegment(sketch, "E3621", {"start": v(-52.56, 15.37) * mm, "end": v(-52.56, 15.24) * mm});
            skLineSegment(sketch, "E3622", {"start": v(-52.56, 7.34) * mm, "end": v(-52.56, 7.22) * mm});
            skLineSegment(sketch, "E3623", {"start": v(-52.56, 7.22) * mm, "end": v(-52.7, 6.84) * mm});
            skLineSegment(sketch, "E3624", {"start": v(-52.7, 6.84) * mm, "end": v(-52.98, 6.52) * mm});
            skLineSegment(sketch, "E3625", {"start": v(-52.98, 6.52) * mm, "end": v(-53.06, 6.47) * mm});
            skLineSegment(sketch, "E3626", {"start": v(-53.06, 6.47) * mm, "end": v(-53.14, 6.43) * mm});
            skLineSegment(sketch, "E3627", {"start": v(-53.14, 6.43) * mm, "end": v(-53.56, 6.34) * mm});
            skLineSegment(sketch, "E3628", {"start": v(-53.56, 6.34) * mm, "end": v(-53.98, 6.43) * mm});
            skLineSegment(sketch, "E3629", {"start": v(-53.98, 6.43) * mm, "end": v(-54.06, 6.47) * mm});
            skLineSegment(sketch, "E3630", {"start": v(-54.06, 6.47) * mm, "end": v(-54.14, 6.52) * mm});
            skLineSegment(sketch, "E3631", {"start": v(-54.14, 6.52) * mm, "end": v(-54.42, 6.84) * mm});
            skLineSegment(sketch, "E3632", {"start": v(-54.42, 6.84) * mm, "end": v(-54.56, 7.22) * mm});
            skLineSegment(sketch, "E3633", {"start": v(-54.56, 7.22) * mm, "end": v(-54.56, 7.34) * mm});
            skLineSegment(sketch, "E3634", {"start": v(-54.56, 7.34) * mm, "end": v(-54.56, 7.46) * mm});
            skLineSegment(sketch, "E3635", {"start": v(-54.56, 7.46) * mm, "end": v(-54.42, 7.84) * mm});
            skLineSegment(sketch, "E3636", {"start": v(-54.42, 7.84) * mm, "end": v(-54.14, 8.16) * mm});
            skLineSegment(sketch, "E3637", {"start": v(-54.14, 8.16) * mm, "end": v(-54.06, 8.2) * mm});
            skLineSegment(sketch, "E3638", {"start": v(-54.06, 8.2) * mm, "end": v(-53.98, 8.25) * mm});
            skLineSegment(sketch, "E3639", {"start": v(-53.98, 8.25) * mm, "end": v(-53.56, 8.34) * mm});
            skLineSegment(sketch, "E3640", {"start": v(-53.56, 8.34) * mm, "end": v(-53.14, 8.25) * mm});
            skLineSegment(sketch, "E3641", {"start": v(-53.14, 8.25) * mm, "end": v(-53.06, 8.2) * mm});
            skLineSegment(sketch, "E3642", {"start": v(-53.06, 8.2) * mm, "end": v(-52.98, 8.16) * mm});
            skLineSegment(sketch, "E3643", {"start": v(-52.98, 8.16) * mm, "end": v(-52.7, 7.84) * mm});
            skLineSegment(sketch, "E3644", {"start": v(-52.7, 7.84) * mm, "end": v(-52.56, 7.46) * mm});
            skLineSegment(sketch, "E3645", {"start": v(-52.56, 7.46) * mm, "end": v(-52.56, 7.34) * mm});
            skLineSegment(sketch, "E3646", {"start": v(39.5, -40.64) * mm, "end": v(39.5, -40.76) * mm});
            skLineSegment(sketch, "E3647", {"start": v(39.5, -40.76) * mm, "end": v(39.4, -41.13) * mm});
            skLineSegment(sketch, "E3648", {"start": v(39.4, -41.13) * mm, "end": v(39.12, -41.52) * mm});
            skLineSegment(sketch, "E3649", {"start": v(39.12, -41.52) * mm, "end": v(38.73, -41.8) * mm});
            skLineSegment(sketch, "E3650", {"start": v(38.73, -41.8) * mm, "end": v(38.36, -41.89) * mm});
            skLineSegment(sketch, "E3651", {"start": v(38.36, -41.89) * mm, "end": v(38.24, -41.89) * mm});
            skLineSegment(sketch, "E3652", {"start": v(38.24, -41.89) * mm, "end": v(38.12, -41.89) * mm});
            skLineSegment(sketch, "E3653", {"start": v(38.12, -41.89) * mm, "end": v(37.75, -41.8) * mm});
            skLineSegment(sketch, "E3654", {"start": v(37.75, -41.8) * mm, "end": v(37.36, -41.52) * mm});
            skLineSegment(sketch, "E3655", {"start": v(37.36, -41.52) * mm, "end": v(37.09, -41.13) * mm});
            skLineSegment(sketch, "E3656", {"start": v(37.09, -41.13) * mm, "end": v(37, -40.76) * mm});
            skLineSegment(sketch, "E3657", {"start": v(37, -40.76) * mm, "end": v(37, -40.64) * mm});
            skLineSegment(sketch, "E3658", {"start": v(37, -40.64) * mm, "end": v(37, -40.48) * mm});
            skLineSegment(sketch, "E3659", {"start": v(37, -40.48) * mm, "end": v(37.16, -40.01) * mm});
            skLineSegment(sketch, "E3660", {"start": v(37.16, -40.01) * mm, "end": v(37.52, -39.61) * mm});
            skLineSegment(sketch, "E3661", {"start": v(37.52, -39.61) * mm, "end": v(37.62, -39.56) * mm});
            skLineSegment(sketch, "E3662", {"start": v(37.62, -39.56) * mm, "end": v(37.71, -39.5) * mm});
            skLineSegment(sketch, "E3663", {"start": v(37.71, -39.5) * mm, "end": v(38.24, -39.39) * mm});
            skLineSegment(sketch, "E3664", {"start": v(38.24, -39.39) * mm, "end": v(38.77, -39.5) * mm});
            skLineSegment(sketch, "E3665", {"start": v(38.77, -39.5) * mm, "end": v(38.87, -39.56) * mm});
            skLineSegment(sketch, "E3666", {"start": v(38.87, -39.56) * mm, "end": v(38.96, -39.61) * mm});
            skLineSegment(sketch, "E3667", {"start": v(38.96, -39.61) * mm, "end": v(39.32, -40.01) * mm});
            skLineSegment(sketch, "E3668", {"start": v(39.32, -40.01) * mm, "end": v(39.5, -40.48) * mm});
            skLineSegment(sketch, "E3669", {"start": v(39.5, -40.48) * mm, "end": v(39.5, -40.64) * mm});
            skLineSegment(sketch, "E3670", {"start": v(-36.7, -40.64) * mm, "end": v(-36.7, -40.8) * mm});
            skLineSegment(sketch, "E3671", {"start": v(-36.7, -40.8) * mm, "end": v(-36.88, -41.26) * mm});
            skLineSegment(sketch, "E3672", {"start": v(-36.88, -41.26) * mm, "end": v(-37.24, -41.67) * mm});
            skLineSegment(sketch, "E3673", {"start": v(-37.24, -41.67) * mm, "end": v(-37.33, -41.72) * mm});
            skLineSegment(sketch, "E3674", {"start": v(-37.33, -41.72) * mm, "end": v(-37.43, -41.78) * mm});
            skLineSegment(sketch, "E3675", {"start": v(-37.43, -41.78) * mm, "end": v(-37.96, -41.89) * mm});
            skLineSegment(sketch, "E3676", {"start": v(-37.96, -41.89) * mm, "end": v(-38.49, -41.78) * mm});
            skLineSegment(sketch, "E3677", {"start": v(-38.49, -41.78) * mm, "end": v(-38.58, -41.72) * mm});
            skLineSegment(sketch, "E3678", {"start": v(-38.58, -41.72) * mm, "end": v(-38.68, -41.67) * mm});
            skLineSegment(sketch, "E3679", {"start": v(-38.68, -41.67) * mm, "end": v(-39.04, -41.26) * mm});
            skLineSegment(sketch, "E3680", {"start": v(-39.04, -41.26) * mm, "end": v(-39.2, -40.8) * mm});
            skLineSegment(sketch, "E3681", {"start": v(-39.2, -40.8) * mm, "end": v(-39.2, -40.64) * mm});
            skLineSegment(sketch, "E3682", {"start": v(-39.2, -40.64) * mm, "end": v(-39.2, -40.48) * mm});
            skLineSegment(sketch, "E3683", {"start": v(-39.2, -40.48) * mm, "end": v(-39.04, -40.01) * mm});
            skLineSegment(sketch, "E3684", {"start": v(-39.04, -40.01) * mm, "end": v(-38.68, -39.61) * mm});
            skLineSegment(sketch, "E3685", {"start": v(-38.68, -39.61) * mm, "end": v(-38.58, -39.56) * mm});
            skLineSegment(sketch, "E3686", {"start": v(-38.58, -39.56) * mm, "end": v(-38.49, -39.5) * mm});
            skLineSegment(sketch, "E3687", {"start": v(-38.49, -39.5) * mm, "end": v(-37.96, -39.39) * mm});
            skLineSegment(sketch, "E3688", {"start": v(-37.96, -39.39) * mm, "end": v(-37.43, -39.5) * mm});
            skLineSegment(sketch, "E3689", {"start": v(-37.43, -39.5) * mm, "end": v(-37.33, -39.56) * mm});
            skLineSegment(sketch, "E3690", {"start": v(-37.33, -39.56) * mm, "end": v(-37.24, -39.61) * mm});
            skLineSegment(sketch, "E3691", {"start": v(-37.24, -39.61) * mm, "end": v(-36.88, -40.01) * mm});
            skLineSegment(sketch, "E3692", {"start": v(-36.88, -40.01) * mm, "end": v(-36.7, -40.48) * mm});
            skLineSegment(sketch, "E3693", {"start": v(-36.7, -40.48) * mm, "end": v(-36.7, -40.64) * mm});
            skLineSegment(sketch, "E3694", {"start": v(39.5, 35.56) * mm, "end": v(39.5, 35.44) * mm});
            skLineSegment(sketch, "E3695", {"start": v(39.5, 35.44) * mm, "end": v(39.4, 35.07) * mm});
            skLineSegment(sketch, "E3696", {"start": v(39.4, 35.07) * mm, "end": v(39.12, 34.68) * mm});
            skLineSegment(sketch, "E3697", {"start": v(39.12, 34.68) * mm, "end": v(38.73, 34.4) * mm});
            skLineSegment(sketch, "E3698", {"start": v(38.73, 34.4) * mm, "end": v(38.36, 34.31) * mm});
            skLineSegment(sketch, "E3699", {"start": v(38.36, 34.31) * mm, "end": v(38.24, 34.31) * mm});
            skLineSegment(sketch, "E3700", {"start": v(38.24, 34.31) * mm, "end": v(38.12, 34.31) * mm});
            skLineSegment(sketch, "E3701", {"start": v(38.12, 34.31) * mm, "end": v(37.75, 34.4) * mm});
            skLineSegment(sketch, "E3702", {"start": v(37.75, 34.4) * mm, "end": v(37.36, 34.68) * mm});
            skLineSegment(sketch, "E3703", {"start": v(37.36, 34.68) * mm, "end": v(37.09, 35.07) * mm});
            skLineSegment(sketch, "E3704", {"start": v(37.09, 35.07) * mm, "end": v(37, 35.44) * mm});
            skLineSegment(sketch, "E3705", {"start": v(37, 35.44) * mm, "end": v(37, 35.56) * mm});
            skLineSegment(sketch, "E3706", {"start": v(37, 35.56) * mm, "end": v(37, 35.72) * mm});
            skLineSegment(sketch, "E3707", {"start": v(37, 35.72) * mm, "end": v(37.16, 36.19) * mm});
            skLineSegment(sketch, "E3708", {"start": v(37.16, 36.19) * mm, "end": v(37.52, 36.59) * mm});
            skLineSegment(sketch, "E3709", {"start": v(37.52, 36.59) * mm, "end": v(37.62, 36.64) * mm});
            skLineSegment(sketch, "E3710", {"start": v(37.62, 36.64) * mm, "end": v(37.71, 36.7) * mm});
            skLineSegment(sketch, "E3711", {"start": v(37.71, 36.7) * mm, "end": v(38.24, 36.81) * mm});
            skLineSegment(sketch, "E3712", {"start": v(38.24, 36.81) * mm, "end": v(38.77, 36.7) * mm});
            skLineSegment(sketch, "E3713", {"start": v(38.77, 36.7) * mm, "end": v(38.87, 36.64) * mm});
            skLineSegment(sketch, "E3714", {"start": v(38.87, 36.64) * mm, "end": v(38.96, 36.59) * mm});
            skLineSegment(sketch, "E3715", {"start": v(38.96, 36.59) * mm, "end": v(39.32, 36.19) * mm});
            skLineSegment(sketch, "E3716", {"start": v(39.32, 36.19) * mm, "end": v(39.5, 35.72) * mm});
            skLineSegment(sketch, "E3717", {"start": v(39.5, 35.72) * mm, "end": v(39.5, 35.56) * mm});
            skLineSegment(sketch, "E3718", {"start": v(51.3, 23.26) * mm, "end": v(51.3, 23.12) * mm});
            skLineSegment(sketch, "E3719", {"start": v(51.3, 23.12) * mm, "end": v(51.16, 22.71) * mm});
            skLineSegment(sketch, "E3720", {"start": v(51.16, 22.71) * mm, "end": v(50.84, 22.36) * mm});
            skLineSegment(sketch, "E3721", {"start": v(50.84, 22.36) * mm, "end": v(50.75, 22.3) * mm});
            skLineSegment(sketch, "E3722", {"start": v(50.75, 22.3) * mm, "end": v(50.67, 22.26) * mm});
            skLineSegment(sketch, "E3723", {"start": v(50.67, 22.26) * mm, "end": v(50.2, 22.16) * mm});
            skLineSegment(sketch, "E3724", {"start": v(50.2, 22.16) * mm, "end": v(49.74, 22.26) * mm});
            skLineSegment(sketch, "E3725", {"start": v(49.74, 22.26) * mm, "end": v(49.65, 22.3) * mm});
            skLineSegment(sketch, "E3726", {"start": v(49.65, 22.3) * mm, "end": v(49.57, 22.36) * mm});
            skLineSegment(sketch, "E3727", {"start": v(49.57, 22.36) * mm, "end": v(49.25, 22.71) * mm});
            skLineSegment(sketch, "E3728", {"start": v(49.25, 22.71) * mm, "end": v(49.1, 23.12) * mm});
            skLineSegment(sketch, "E3729", {"start": v(49.1, 23.12) * mm, "end": v(49.1, 23.26) * mm});
            skLineSegment(sketch, "E3730", {"start": v(49.1, 23.26) * mm, "end": v(49.1, 23.4) * mm});
            skLineSegment(sketch, "E3731", {"start": v(49.1, 23.4) * mm, "end": v(49.25, 23.8) * mm});
            skLineSegment(sketch, "E3732", {"start": v(49.25, 23.8) * mm, "end": v(49.57, 24.16) * mm});
            skLineSegment(sketch, "E3733", {"start": v(49.57, 24.16) * mm, "end": v(49.65, 24.21) * mm});
            skLineSegment(sketch, "E3734", {"start": v(49.65, 24.21) * mm, "end": v(49.74, 24.26) * mm});
            skLineSegment(sketch, "E3735", {"start": v(49.74, 24.26) * mm, "end": v(50.2, 24.36) * mm});
            skLineSegment(sketch, "E3736", {"start": v(50.2, 24.36) * mm, "end": v(50.67, 24.26) * mm});
            skLineSegment(sketch, "E3737", {"start": v(50.67, 24.26) * mm, "end": v(50.75, 24.21) * mm});
            skLineSegment(sketch, "E3738", {"start": v(50.75, 24.21) * mm, "end": v(50.84, 24.16) * mm});
            skLineSegment(sketch, "E3739", {"start": v(50.84, 24.16) * mm, "end": v(51.16, 23.8) * mm});
            skLineSegment(sketch, "E3740", {"start": v(51.16, 23.8) * mm, "end": v(51.3, 23.4) * mm});
            skLineSegment(sketch, "E3741", {"start": v(51.3, 23.4) * mm, "end": v(51.3, 23.26) * mm});
            skLineSegment(sketch, "E3742", {"start": v(51.3, 13.06) * mm, "end": v(51.3, 12.92) * mm});
            skLineSegment(sketch, "E3743", {"start": v(51.3, 12.92) * mm, "end": v(51.16, 12.51) * mm});
            skLineSegment(sketch, "E3744", {"start": v(51.16, 12.51) * mm, "end": v(50.84, 12.16) * mm});
            skLineSegment(sketch, "E3745", {"start": v(50.84, 12.16) * mm, "end": v(50.75, 12.1) * mm});
            skLineSegment(sketch, "E3746", {"start": v(50.75, 12.1) * mm, "end": v(50.67, 12.06) * mm});
            skLineSegment(sketch, "E3747", {"start": v(50.67, 12.06) * mm, "end": v(50.2, 11.96) * mm});
            skLineSegment(sketch, "E3748", {"start": v(50.2, 11.96) * mm, "end": v(49.74, 12.06) * mm});
            skLineSegment(sketch, "E3749", {"start": v(49.74, 12.06) * mm, "end": v(49.65, 12.1) * mm});
            skLineSegment(sketch, "E3750", {"start": v(49.65, 12.1) * mm, "end": v(49.57, 12.16) * mm});
            skLineSegment(sketch, "E3751", {"start": v(49.57, 12.16) * mm, "end": v(49.25, 12.51) * mm});
            skLineSegment(sketch, "E3752", {"start": v(49.25, 12.51) * mm, "end": v(49.1, 12.92) * mm});
            skLineSegment(sketch, "E3753", {"start": v(49.1, 12.92) * mm, "end": v(49.1, 13.06) * mm});
            skLineSegment(sketch, "E3754", {"start": v(49.1, 13.06) * mm, "end": v(49.1, 13.2) * mm});
            skLineSegment(sketch, "E3755", {"start": v(49.1, 13.2) * mm, "end": v(49.25, 13.61) * mm});
            skLineSegment(sketch, "E3756", {"start": v(49.25, 13.61) * mm, "end": v(49.57, 13.96) * mm});
            skLineSegment(sketch, "E3757", {"start": v(49.57, 13.96) * mm, "end": v(49.65, 14.01) * mm});
            skLineSegment(sketch, "E3758", {"start": v(49.65, 14.01) * mm, "end": v(49.74, 14.06) * mm});
            skLineSegment(sketch, "E3759", {"start": v(49.74, 14.06) * mm, "end": v(50.2, 14.16) * mm});
            skLineSegment(sketch, "E3760", {"start": v(50.2, 14.16) * mm, "end": v(50.67, 14.06) * mm});
            skLineSegment(sketch, "E3761", {"start": v(50.67, 14.06) * mm, "end": v(50.75, 14.01) * mm});
            skLineSegment(sketch, "E3762", {"start": v(50.75, 14.01) * mm, "end": v(50.84, 13.96) * mm});
            skLineSegment(sketch, "E3763", {"start": v(50.84, 13.96) * mm, "end": v(51.16, 13.61) * mm});
            skLineSegment(sketch, "E3764", {"start": v(51.16, 13.61) * mm, "end": v(51.3, 13.2) * mm});
            skLineSegment(sketch, "E3765", {"start": v(51.3, 13.2) * mm, "end": v(51.3, 13.06) * mm});
            skLineSegment(sketch, "E3766", {"start": v(46.44, 18.16) * mm, "end": v(46.44, 18.05) * mm});
            skLineSegment(sketch, "E3767", {"start": v(46.44, 18.05) * mm, "end": v(46.23, 17.75) * mm});
            skLineSegment(sketch, "E3768", {"start": v(46.23, 17.75) * mm, "end": v(46.19, 17.73) * mm});
            skLineSegment(sketch, "E3769", {"start": v(46.19, 17.73) * mm, "end": v(46.15, 17.7) * mm});
            skLineSegment(sketch, "E3770", {"start": v(46.15, 17.7) * mm, "end": v(45.73, 17.7) * mm});
            skLineSegment(sketch, "E3771", {"start": v(45.73, 17.7) * mm, "end": v(45.69, 17.73) * mm});
            skLineSegment(sketch, "E3772", {"start": v(45.69, 17.73) * mm, "end": v(45.65, 17.75) * mm});
            skLineSegment(sketch, "E3773", {"start": v(45.65, 17.75) * mm, "end": v(45.44, 18.06) * mm});
            skLineSegment(sketch, "E3774", {"start": v(45.44, 18.06) * mm, "end": v(45.44, 18.16) * mm});
            skLineSegment(sketch, "E3775", {"start": v(45.44, 18.16) * mm, "end": v(45.44, 18.27) * mm});
            skLineSegment(sketch, "E3776", {"start": v(45.44, 18.27) * mm, "end": v(45.65, 18.57) * mm});
            skLineSegment(sketch, "E3777", {"start": v(45.65, 18.57) * mm, "end": v(45.69, 18.6) * mm});
            skLineSegment(sketch, "E3778", {"start": v(45.69, 18.6) * mm, "end": v(45.73, 18.62) * mm});
            skLineSegment(sketch, "E3779", {"start": v(45.73, 18.62) * mm, "end": v(46.15, 18.62) * mm});
            skLineSegment(sketch, "E3780", {"start": v(46.15, 18.62) * mm, "end": v(46.19, 18.6) * mm});
            skLineSegment(sketch, "E3781", {"start": v(46.19, 18.6) * mm, "end": v(46.23, 18.57) * mm});
            skLineSegment(sketch, "E3782", {"start": v(46.23, 18.57) * mm, "end": v(46.44, 18.26) * mm});
            skLineSegment(sketch, "E3783", {"start": v(46.44, 18.26) * mm, "end": v(46.44, 18.16) * mm});
            skLineSegment(sketch, "E3784", {"start": v(46.44, 20.66) * mm, "end": v(46.44, 20.55) * mm});
            skLineSegment(sketch, "E3785", {"start": v(46.44, 20.55) * mm, "end": v(46.23, 20.25) * mm});
            skLineSegment(sketch, "E3786", {"start": v(46.23, 20.25) * mm, "end": v(46.19, 20.23) * mm});
            skLineSegment(sketch, "E3787", {"start": v(46.19, 20.23) * mm, "end": v(46.15, 20.2) * mm});
            skLineSegment(sketch, "E3788", {"start": v(46.15, 20.2) * mm, "end": v(45.73, 20.2) * mm});
            skLineSegment(sketch, "E3789", {"start": v(45.73, 20.2) * mm, "end": v(45.69, 20.23) * mm});
            skLineSegment(sketch, "E3790", {"start": v(45.69, 20.23) * mm, "end": v(45.65, 20.25) * mm});
            skLineSegment(sketch, "E3791", {"start": v(45.65, 20.25) * mm, "end": v(45.44, 20.56) * mm});
            skLineSegment(sketch, "E3792", {"start": v(45.44, 20.56) * mm, "end": v(45.44, 20.66) * mm});
            skLineSegment(sketch, "E3793", {"start": v(45.44, 20.66) * mm, "end": v(45.44, 20.77) * mm});
            skLineSegment(sketch, "E3794", {"start": v(45.44, 20.77) * mm, "end": v(45.65, 21.07) * mm});
            skLineSegment(sketch, "E3795", {"start": v(45.65, 21.07) * mm, "end": v(45.69, 21.1) * mm});
            skLineSegment(sketch, "E3796", {"start": v(45.69, 21.1) * mm, "end": v(45.73, 21.12) * mm});
            skLineSegment(sketch, "E3797", {"start": v(45.73, 21.12) * mm, "end": v(46.15, 21.12) * mm});
            skLineSegment(sketch, "E3798", {"start": v(46.15, 21.12) * mm, "end": v(46.19, 21.1) * mm});
            skLineSegment(sketch, "E3799", {"start": v(46.19, 21.1) * mm, "end": v(46.23, 21.07) * mm});
            skLineSegment(sketch, "E3800", {"start": v(46.23, 21.07) * mm, "end": v(46.44, 20.76) * mm});
            skLineSegment(sketch, "E3801", {"start": v(46.44, 20.76) * mm, "end": v(46.44, 20.66) * mm});
            skLineSegment(sketch, "E3802", {"start": v(21.15, -2.25) * mm, "end": v(21.15, -2.34) * mm});
            skLineSegment(sketch, "E3803", {"start": v(21.15, -2.34) * mm, "end": v(20.98, -2.58) * mm});
            skLineSegment(sketch, "E3804", {"start": v(20.98, -2.58) * mm, "end": v(20.95, -2.6) * mm});
            skLineSegment(sketch, "E3805", {"start": v(20.95, -2.6) * mm, "end": v(20.92, -2.62) * mm});
            skLineSegment(sketch, "E3806", {"start": v(20.92, -2.62) * mm, "end": v(20.58, -2.62) * mm});
            skLineSegment(sketch, "E3807", {"start": v(20.58, -2.62) * mm, "end": v(20.55, -2.6) * mm});
            skLineSegment(sketch, "E3808", {"start": v(20.55, -2.6) * mm, "end": v(20.52, -2.58) * mm});
            skLineSegment(sketch, "E3809", {"start": v(20.52, -2.58) * mm, "end": v(20.35, -2.34) * mm});
            skLineSegment(sketch, "E3810", {"start": v(20.35, -2.34) * mm, "end": v(20.35, -2.25) * mm});
            skLineSegment(sketch, "E3811", {"start": v(20.35, -2.25) * mm, "end": v(20.35, -2.17) * mm});
            skLineSegment(sketch, "E3812", {"start": v(20.35, -2.17) * mm, "end": v(20.52, -1.93) * mm});
            skLineSegment(sketch, "E3813", {"start": v(20.52, -1.93) * mm, "end": v(20.55, -1.9) * mm});
            skLineSegment(sketch, "E3814", {"start": v(20.55, -1.9) * mm, "end": v(20.58, -1.89) * mm});
            skLineSegment(sketch, "E3815", {"start": v(20.58, -1.89) * mm, "end": v(20.92, -1.89) * mm});
            skLineSegment(sketch, "E3816", {"start": v(20.92, -1.89) * mm, "end": v(20.95, -1.9) * mm});
            skLineSegment(sketch, "E3817", {"start": v(20.95, -1.9) * mm, "end": v(20.98, -1.93) * mm});
            skLineSegment(sketch, "E3818", {"start": v(20.98, -1.93) * mm, "end": v(21.15, -2.17) * mm});
            skLineSegment(sketch, "E3819", {"start": v(21.15, -2.17) * mm, "end": v(21.15, -2.25) * mm});
            skLineSegment(sketch, "E3820", {"start": v(-24.6, 23.72) * mm, "end": v(-24.6, 23.61) * mm});
            skLineSegment(sketch, "E3821", {"start": v(-24.6, 23.61) * mm, "end": v(-24.81, 23.3) * mm});
            skLineSegment(sketch, "E3822", {"start": v(-24.81, 23.3) * mm, "end": v(-24.85, 23.28) * mm});
            skLineSegment(sketch, "E3823", {"start": v(-24.85, 23.28) * mm, "end": v(-24.9, 23.26) * mm});
            skLineSegment(sketch, "E3824", {"start": v(-24.9, 23.26) * mm, "end": v(-25.32, 23.26) * mm});
            skLineSegment(sketch, "E3825", {"start": v(-25.32, 23.26) * mm, "end": v(-25.36, 23.28) * mm});
            skLineSegment(sketch, "E3826", {"start": v(-25.36, 23.28) * mm, "end": v(-25.4, 23.3) * mm});
            skLineSegment(sketch, "E3827", {"start": v(-25.4, 23.3) * mm, "end": v(-25.61, 23.62) * mm});
            skLineSegment(sketch, "E3828", {"start": v(-25.61, 23.62) * mm, "end": v(-25.61, 23.72) * mm});
            skLineSegment(sketch, "E3829", {"start": v(-25.61, 23.72) * mm, "end": v(-25.61, 23.83) * mm});
            skLineSegment(sketch, "E3830", {"start": v(-25.61, 23.83) * mm, "end": v(-25.4, 24.14) * mm});
            skLineSegment(sketch, "E3831", {"start": v(-25.4, 24.14) * mm, "end": v(-25.36, 24.16) * mm});
            skLineSegment(sketch, "E3832", {"start": v(-25.36, 24.16) * mm, "end": v(-25.32, 24.19) * mm});
            skLineSegment(sketch, "E3833", {"start": v(-25.32, 24.19) * mm, "end": v(-24.9, 24.19) * mm});
            skLineSegment(sketch, "E3834", {"start": v(-24.9, 24.19) * mm, "end": v(-24.85, 24.16) * mm});
            skLineSegment(sketch, "E3835", {"start": v(-24.85, 24.16) * mm, "end": v(-24.81, 24.14) * mm});
            skLineSegment(sketch, "E3836", {"start": v(-24.81, 24.14) * mm, "end": v(-24.6, 23.83) * mm});
            skLineSegment(sketch, "E3837", {"start": v(-24.6, 23.83) * mm, "end": v(-24.6, 23.72) * mm});
            skLineSegment(sketch, "E3838", {"start": v(-24.45, 14.58) * mm, "end": v(-24.45, 14.47) * mm});
            skLineSegment(sketch, "E3839", {"start": v(-24.45, 14.47) * mm, "end": v(-24.66, 14.16) * mm});
            skLineSegment(sketch, "E3840", {"start": v(-24.66, 14.16) * mm, "end": v(-24.7, 14.14) * mm});
            skLineSegment(sketch, "E3841", {"start": v(-24.7, 14.14) * mm, "end": v(-24.74, 14.12) * mm});
            skLineSegment(sketch, "E3842", {"start": v(-24.74, 14.12) * mm, "end": v(-25.17, 14.12) * mm});
            skLineSegment(sketch, "E3843", {"start": v(-25.17, 14.12) * mm, "end": v(-25.2, 14.14) * mm});
            skLineSegment(sketch, "E3844", {"start": v(-25.2, 14.14) * mm, "end": v(-25.25, 14.16) * mm});
            skLineSegment(sketch, "E3845", {"start": v(-25.25, 14.16) * mm, "end": v(-25.46, 14.48) * mm});
            skLineSegment(sketch, "E3846", {"start": v(-25.46, 14.48) * mm, "end": v(-25.46, 14.58) * mm});
            skLineSegment(sketch, "E3847", {"start": v(-25.46, 14.58) * mm, "end": v(-25.46, 14.7) * mm});
            skLineSegment(sketch, "E3848", {"start": v(-25.46, 14.7) * mm, "end": v(-25.25, 15) * mm});
            skLineSegment(sketch, "E3849", {"start": v(-25.25, 15) * mm, "end": v(-25.2, 15.02) * mm});
            skLineSegment(sketch, "E3850", {"start": v(-25.2, 15.02) * mm, "end": v(-25.17, 15.04) * mm});
            skLineSegment(sketch, "E3851", {"start": v(-25.17, 15.04) * mm, "end": v(-24.74, 15.04) * mm});
            skLineSegment(sketch, "E3852", {"start": v(-24.74, 15.04) * mm, "end": v(-24.7, 15.02) * mm});
            skLineSegment(sketch, "E3853", {"start": v(-24.7, 15.02) * mm, "end": v(-24.66, 15) * mm});
            skLineSegment(sketch, "E3854", {"start": v(-24.66, 15) * mm, "end": v(-24.45, 14.68) * mm});
            skLineSegment(sketch, "E3855", {"start": v(-24.45, 14.68) * mm, "end": v(-24.45, 14.58) * mm});
            skLineSegment(sketch, "E3856", {"start": v(-24.5, 11.74) * mm, "end": v(-24.5, 11.63) * mm});
            skLineSegment(sketch, "E3857", {"start": v(-24.5, 11.63) * mm, "end": v(-24.71, 11.32) * mm});
            skLineSegment(sketch, "E3858", {"start": v(-24.71, 11.32) * mm, "end": v(-24.75, 11.3) * mm});
            skLineSegment(sketch, "E3859", {"start": v(-24.75, 11.3) * mm, "end": v(-24.8, 11.27) * mm});
            skLineSegment(sketch, "E3860", {"start": v(-24.8, 11.27) * mm, "end": v(-25.22, 11.27) * mm});
            skLineSegment(sketch, "E3861", {"start": v(-25.22, 11.27) * mm, "end": v(-25.26, 11.3) * mm});
            skLineSegment(sketch, "E3862", {"start": v(-25.26, 11.3) * mm, "end": v(-25.3, 11.32) * mm});
            skLineSegment(sketch, "E3863", {"start": v(-25.3, 11.32) * mm, "end": v(-25.51, 11.63) * mm});
            skLineSegment(sketch, "E3864", {"start": v(-25.51, 11.63) * mm, "end": v(-25.51, 11.74) * mm});
            skLineSegment(sketch, "E3865", {"start": v(-25.51, 11.74) * mm, "end": v(-25.51, 11.85) * mm});
            skLineSegment(sketch, "E3866", {"start": v(-25.51, 11.85) * mm, "end": v(-25.3, 12.15) * mm});
            skLineSegment(sketch, "E3867", {"start": v(-25.3, 12.15) * mm, "end": v(-25.26, 12.18) * mm});
            skLineSegment(sketch, "E3868", {"start": v(-25.26, 12.18) * mm, "end": v(-25.22, 12.2) * mm});
            skLineSegment(sketch, "E3869", {"start": v(-25.22, 12.2) * mm, "end": v(-24.8, 12.2) * mm});
            skLineSegment(sketch, "E3870", {"start": v(-24.8, 12.2) * mm, "end": v(-24.75, 12.18) * mm});
            skLineSegment(sketch, "E3871", {"start": v(-24.75, 12.18) * mm, "end": v(-24.71, 12.15) * mm});
            skLineSegment(sketch, "E3872", {"start": v(-24.71, 12.15) * mm, "end": v(-24.5, 11.84) * mm});
            skLineSegment(sketch, "E3873", {"start": v(-24.5, 11.84) * mm, "end": v(-24.5, 11.74) * mm});
            skLineSegment(sketch, "E3874", {"start": v(-33.76, 15.24) * mm, "end": v(-33.76, 14.97) * mm});
            skLineSegment(sketch, "E3875", {"start": v(-33.76, 14.97) * mm, "end": v(-33.9, 14.14) * mm});
            skLineSegment(sketch, "E3876", {"start": v(-33.9, 14.14) * mm, "end": v(-34.32, 13.14) * mm});
            skLineSegment(sketch, "E3877", {"start": v(-34.32, 13.14) * mm, "end": v(-34.98, 12.28) * mm});
            skLineSegment(sketch, "E3878", {"start": v(-34.98, 12.28) * mm, "end": v(-35.62, 11.74) * mm});
            skLineSegment(sketch, "E3879", {"start": v(-35.62, 11.74) * mm, "end": v(-35.86, 11.6) * mm});
            skLineSegment(sketch, "E3880", {"start": v(-35.86, 11.6) * mm, "end": v(-36.1, 11.47) * mm});
            skLineSegment(sketch, "E3881", {"start": v(-36.1, 11.47) * mm, "end": v(-36.88, 11.18) * mm});
            skLineSegment(sketch, "E3882", {"start": v(-36.88, 11.18) * mm, "end": v(-37.96, 11.04) * mm});
            skLineSegment(sketch, "E3883", {"start": v(-37.96, 11.04) * mm, "end": v(-39.04, 11.18) * mm});
            skLineSegment(sketch, "E3884", {"start": v(-39.04, 11.18) * mm, "end": v(-39.82, 11.47) * mm});
            skLineSegment(sketch, "E3885", {"start": v(-39.82, 11.47) * mm, "end": v(-40.06, 11.6) * mm});
            skLineSegment(sketch, "E3886", {"start": v(-40.06, 11.6) * mm, "end": v(-40.3, 11.74) * mm});
            skLineSegment(sketch, "E3887", {"start": v(-40.3, 11.74) * mm, "end": v(-40.94, 12.28) * mm});
            skLineSegment(sketch, "E3888", {"start": v(-40.94, 12.28) * mm, "end": v(-41.6, 13.14) * mm});
            skLineSegment(sketch, "E3889", {"start": v(-41.6, 13.14) * mm, "end": v(-42.01, 14.14) * mm});
            skLineSegment(sketch, "E3890", {"start": v(-42.01, 14.14) * mm, "end": v(-42.16, 14.97) * mm});
            skLineSegment(sketch, "E3891", {"start": v(-42.16, 14.97) * mm, "end": v(-42.16, 15.24) * mm});
            skLineSegment(sketch, "E3892", {"start": v(-42.16, 15.24) * mm, "end": v(-42.16, 15.51) * mm});
            skLineSegment(sketch, "E3893", {"start": v(-42.16, 15.51) * mm, "end": v(-42.01, 16.34) * mm});
            skLineSegment(sketch, "E3894", {"start": v(-42.01, 16.34) * mm, "end": v(-41.6, 17.34) * mm});
            skLineSegment(sketch, "E3895", {"start": v(-41.6, 17.34) * mm, "end": v(-40.94, 18.2) * mm});
            skLineSegment(sketch, "E3896", {"start": v(-40.94, 18.2) * mm, "end": v(-40.3, 18.74) * mm});
            skLineSegment(sketch, "E3897", {"start": v(-40.3, 18.74) * mm, "end": v(-40.06, 18.88) * mm});
            skLineSegment(sketch, "E3898", {"start": v(-40.06, 18.88) * mm, "end": v(-39.82, 19.02) * mm});
            skLineSegment(sketch, "E3899", {"start": v(-39.82, 19.02) * mm, "end": v(-39.04, 19.3) * mm});
            skLineSegment(sketch, "E3900", {"start": v(-39.04, 19.3) * mm, "end": v(-37.96, 19.44) * mm});
            skLineSegment(sketch, "E3901", {"start": v(-37.96, 19.44) * mm, "end": v(-36.88, 19.3) * mm});
            skLineSegment(sketch, "E3902", {"start": v(-36.88, 19.3) * mm, "end": v(-36.1, 19.02) * mm});
            skLineSegment(sketch, "E3903", {"start": v(-36.1, 19.02) * mm, "end": v(-35.86, 18.88) * mm});
            skLineSegment(sketch, "E3904", {"start": v(-35.86, 18.88) * mm, "end": v(-35.62, 18.74) * mm});
            skLineSegment(sketch, "E3905", {"start": v(-35.62, 18.74) * mm, "end": v(-34.98, 18.2) * mm});
            skLineSegment(sketch, "E3906", {"start": v(-34.98, 18.2) * mm, "end": v(-34.32, 17.34) * mm});
            skLineSegment(sketch, "E3907", {"start": v(-34.32, 17.34) * mm, "end": v(-33.9, 16.34) * mm});
            skLineSegment(sketch, "E3908", {"start": v(-33.9, 16.34) * mm, "end": v(-33.76, 15.51) * mm});
            skLineSegment(sketch, "E3909", {"start": v(-33.76, 15.51) * mm, "end": v(-33.76, 15.24) * mm});
            skLineSegment(sketch, "E3910", {"start": v(34.82, -20.32) * mm, "end": v(34.82, -20.6) * mm});
            skLineSegment(sketch, "E3911", {"start": v(34.82, -20.6) * mm, "end": v(34.67, -21.41) * mm});
            skLineSegment(sketch, "E3912", {"start": v(34.67, -21.41) * mm, "end": v(34.26, -22.42) * mm});
            skLineSegment(sketch, "E3913", {"start": v(34.26, -22.42) * mm, "end": v(33.6, -23.28) * mm});
            skLineSegment(sketch, "E3914", {"start": v(33.6, -23.28) * mm, "end": v(32.96, -23.82) * mm});
            skLineSegment(sketch, "E3915", {"start": v(32.96, -23.82) * mm, "end": v(32.72, -23.96) * mm});
            skLineSegment(sketch, "E3916", {"start": v(32.72, -23.96) * mm, "end": v(32.48, -24.1) * mm});
            skLineSegment(sketch, "E3917", {"start": v(32.48, -24.1) * mm, "end": v(31.7, -24.38) * mm});
            skLineSegment(sketch, "E3918", {"start": v(31.7, -24.38) * mm, "end": v(30.62, -24.52) * mm});
            skLineSegment(sketch, "E3919", {"start": v(30.62, -24.52) * mm, "end": v(29.54, -24.38) * mm});
            skLineSegment(sketch, "E3920", {"start": v(29.54, -24.38) * mm, "end": v(28.76, -24.1) * mm});
            skLineSegment(sketch, "E3921", {"start": v(28.76, -24.1) * mm, "end": v(28.52, -23.96) * mm});
            skLineSegment(sketch, "E3922", {"start": v(28.52, -23.96) * mm, "end": v(28.28, -23.82) * mm});
            skLineSegment(sketch, "E3923", {"start": v(28.28, -23.82) * mm, "end": v(27.64, -23.28) * mm});
            skLineSegment(sketch, "E3924", {"start": v(27.64, -23.28) * mm, "end": v(26.98, -22.42) * mm});
            skLineSegment(sketch, "E3925", {"start": v(26.98, -22.42) * mm, "end": v(26.56, -21.41) * mm});
            skLineSegment(sketch, "E3926", {"start": v(26.56, -21.41) * mm, "end": v(26.42, -20.6) * mm});
            skLineSegment(sketch, "E3927", {"start": v(26.42, -20.6) * mm, "end": v(26.42, -20.32) * mm});
            skLineSegment(sketch, "E3928", {"start": v(26.42, -20.32) * mm, "end": v(26.42, -20.05) * mm});
            skLineSegment(sketch, "E3929", {"start": v(26.42, -20.05) * mm, "end": v(26.56, -19.22) * mm});
            skLineSegment(sketch, "E3930", {"start": v(26.56, -19.22) * mm, "end": v(26.98, -18.22) * mm});
            skLineSegment(sketch, "E3931", {"start": v(26.98, -18.22) * mm, "end": v(27.64, -17.36) * mm});
            skLineSegment(sketch, "E3932", {"start": v(27.64, -17.36) * mm, "end": v(28.28, -16.82) * mm});
            skLineSegment(sketch, "E3933", {"start": v(28.28, -16.82) * mm, "end": v(28.52, -16.68) * mm});
            skLineSegment(sketch, "E3934", {"start": v(28.52, -16.68) * mm, "end": v(28.76, -16.54) * mm});
            skLineSegment(sketch, "E3935", {"start": v(28.76, -16.54) * mm, "end": v(29.54, -16.26) * mm});
            skLineSegment(sketch, "E3936", {"start": v(29.54, -16.26) * mm, "end": v(30.62, -16.12) * mm});
            skLineSegment(sketch, "E3937", {"start": v(30.62, -16.12) * mm, "end": v(31.7, -16.26) * mm});
            skLineSegment(sketch, "E3938", {"start": v(31.7, -16.26) * mm, "end": v(32.48, -16.54) * mm});
            skLineSegment(sketch, "E3939", {"start": v(32.48, -16.54) * mm, "end": v(32.72, -16.68) * mm});
            skLineSegment(sketch, "E3940", {"start": v(32.72, -16.68) * mm, "end": v(32.96, -16.82) * mm});
            skLineSegment(sketch, "E3941", {"start": v(32.96, -16.82) * mm, "end": v(33.6, -17.36) * mm});
            skLineSegment(sketch, "E3942", {"start": v(33.6, -17.36) * mm, "end": v(34.26, -18.22) * mm});
            skLineSegment(sketch, "E3943", {"start": v(34.26, -18.22) * mm, "end": v(34.67, -19.22) * mm});
            skLineSegment(sketch, "E3944", {"start": v(34.67, -19.22) * mm, "end": v(34.82, -20.05) * mm});
            skLineSegment(sketch, "E3945", {"start": v(34.82, -20.05) * mm, "end": v(34.82, -20.32) * mm});
            skLineSegment(sketch, "E3946", {"start": v(-13.44, -20.32) * mm, "end": v(-13.44, -20.6) * mm});
            skLineSegment(sketch, "E3947", {"start": v(-13.44, -20.6) * mm, "end": v(-13.59, -21.41) * mm});
            skLineSegment(sketch, "E3948", {"start": v(-13.59, -21.41) * mm, "end": v(-14, -22.42) * mm});
            skLineSegment(sketch, "E3949", {"start": v(-14, -22.42) * mm, "end": v(-14.66, -23.28) * mm});
            skLineSegment(sketch, "E3950", {"start": v(-14.66, -23.28) * mm, "end": v(-15.3, -23.82) * mm});
            skLineSegment(sketch, "E3951", {"start": v(-15.3, -23.82) * mm, "end": v(-15.54, -23.96) * mm});
            skLineSegment(sketch, "E3952", {"start": v(-15.54, -23.96) * mm, "end": v(-15.78, -24.1) * mm});
            skLineSegment(sketch, "E3953", {"start": v(-15.78, -24.1) * mm, "end": v(-16.56, -24.38) * mm});
            skLineSegment(sketch, "E3954", {"start": v(-16.56, -24.38) * mm, "end": v(-17.64, -24.52) * mm});
            skLineSegment(sketch, "E3955", {"start": v(-17.64, -24.52) * mm, "end": v(-18.72, -24.38) * mm});
            skLineSegment(sketch, "E3956", {"start": v(-18.72, -24.38) * mm, "end": v(-19.5, -24.1) * mm});
            skLineSegment(sketch, "E3957", {"start": v(-19.5, -24.1) * mm, "end": v(-19.74, -23.96) * mm});
            skLineSegment(sketch, "E3958", {"start": v(-19.74, -23.96) * mm, "end": v(-19.98, -23.82) * mm});
            skLineSegment(sketch, "E3959", {"start": v(-19.98, -23.82) * mm, "end": v(-20.62, -23.28) * mm});
            skLineSegment(sketch, "E3960", {"start": v(-20.62, -23.28) * mm, "end": v(-21.28, -22.42) * mm});
            skLineSegment(sketch, "E3961", {"start": v(-21.28, -22.42) * mm, "end": v(-21.7, -21.41) * mm});
            skLineSegment(sketch, "E3962", {"start": v(-21.7, -21.41) * mm, "end": v(-21.84, -20.6) * mm});
            skLineSegment(sketch, "E3963", {"start": v(-21.84, -20.6) * mm, "end": v(-21.84, -20.32) * mm});
            skLineSegment(sketch, "E3964", {"start": v(-21.84, -20.32) * mm, "end": v(-21.84, -20.05) * mm});
            skLineSegment(sketch, "E3965", {"start": v(-21.84, -20.05) * mm, "end": v(-21.7, -19.22) * mm});
            skLineSegment(sketch, "E3966", {"start": v(-21.7, -19.22) * mm, "end": v(-21.28, -18.22) * mm});
            skLineSegment(sketch, "E3967", {"start": v(-21.28, -18.22) * mm, "end": v(-20.62, -17.36) * mm});
            skLineSegment(sketch, "E3968", {"start": v(-20.62, -17.36) * mm, "end": v(-19.98, -16.82) * mm});
            skLineSegment(sketch, "E3969", {"start": v(-19.98, -16.82) * mm, "end": v(-19.74, -16.68) * mm});
            skLineSegment(sketch, "E3970", {"start": v(-19.74, -16.68) * mm, "end": v(-19.5, -16.54) * mm});
            skLineSegment(sketch, "E3971", {"start": v(-19.5, -16.54) * mm, "end": v(-18.72, -16.26) * mm});
            skLineSegment(sketch, "E3972", {"start": v(-18.72, -16.26) * mm, "end": v(-17.64, -16.12) * mm});
            skLineSegment(sketch, "E3973", {"start": v(-17.64, -16.12) * mm, "end": v(-16.56, -16.26) * mm});
            skLineSegment(sketch, "E3974", {"start": v(-16.56, -16.26) * mm, "end": v(-15.78, -16.54) * mm});
            skLineSegment(sketch, "E3975", {"start": v(-15.78, -16.54) * mm, "end": v(-15.54, -16.68) * mm});
            skLineSegment(sketch, "E3976", {"start": v(-15.54, -16.68) * mm, "end": v(-15.3, -16.82) * mm});
            skLineSegment(sketch, "E3977", {"start": v(-15.3, -16.82) * mm, "end": v(-14.66, -17.36) * mm});
            skLineSegment(sketch, "E3978", {"start": v(-14.66, -17.36) * mm, "end": v(-14, -18.22) * mm});
            skLineSegment(sketch, "E3979", {"start": v(-14, -18.22) * mm, "end": v(-13.59, -19.22) * mm});
            skLineSegment(sketch, "E3980", {"start": v(-13.59, -19.22) * mm, "end": v(-13.44, -20.05) * mm});
            skLineSegment(sketch, "E3981", {"start": v(-13.44, -20.05) * mm, "end": v(-13.44, -20.32) * mm});
            skLineSegment(sketch, "E3982", {"start": v(34.82, 48.26) * mm, "end": v(34.82, 47.99) * mm});
            skLineSegment(sketch, "E3983", {"start": v(34.82, 47.99) * mm, "end": v(34.67, 47.16) * mm});
            skLineSegment(sketch, "E3984", {"start": v(34.67, 47.16) * mm, "end": v(34.26, 46.16) * mm});
            skLineSegment(sketch, "E3985", {"start": v(34.26, 46.16) * mm, "end": v(33.6, 45.3) * mm});
            skLineSegment(sketch, "E3986", {"start": v(33.6, 45.3) * mm, "end": v(32.96, 44.76) * mm});
            skLineSegment(sketch, "E3987", {"start": v(32.96, 44.76) * mm, "end": v(32.72, 44.62) * mm});
            skLineSegment(sketch, "E3988", {"start": v(32.72, 44.62) * mm, "end": v(32.48, 44.49) * mm});
            skLineSegment(sketch, "E3989", {"start": v(32.48, 44.49) * mm, "end": v(31.7, 44.2) * mm});
            skLineSegment(sketch, "E3990", {"start": v(31.7, 44.2) * mm, "end": v(30.62, 44.06) * mm});
            skLineSegment(sketch, "E3991", {"start": v(30.62, 44.06) * mm, "end": v(29.54, 44.2) * mm});
            skLineSegment(sketch, "E3992", {"start": v(29.54, 44.2) * mm, "end": v(28.76, 44.49) * mm});
            skLineSegment(sketch, "E3993", {"start": v(28.76, 44.49) * mm, "end": v(28.52, 44.62) * mm});
            skLineSegment(sketch, "E3994", {"start": v(28.52, 44.62) * mm, "end": v(28.28, 44.76) * mm});
            skLineSegment(sketch, "E3995", {"start": v(28.28, 44.76) * mm, "end": v(27.64, 45.3) * mm});
            skLineSegment(sketch, "E3996", {"start": v(27.64, 45.3) * mm, "end": v(26.98, 46.16) * mm});
            skLineSegment(sketch, "E3997", {"start": v(26.98, 46.16) * mm, "end": v(26.56, 47.16) * mm});
            skLineSegment(sketch, "E3998", {"start": v(26.56, 47.16) * mm, "end": v(26.42, 47.99) * mm});
            skLineSegment(sketch, "E3999", {"start": v(26.42, 47.99) * mm, "end": v(26.42, 48.26) * mm});
            skLineSegment(sketch, "E4000", {"start": v(26.42, 48.26) * mm, "end": v(26.42, 48.53) * mm});
            skLineSegment(sketch, "E4001", {"start": v(26.42, 48.53) * mm, "end": v(26.56, 49.36) * mm});
            skLineSegment(sketch, "E4002", {"start": v(26.56, 49.36) * mm, "end": v(26.98, 50.36) * mm});
            skLineSegment(sketch, "E4003", {"start": v(26.98, 50.36) * mm, "end": v(27.64, 51.22) * mm});
            skLineSegment(sketch, "E4004", {"start": v(27.64, 51.22) * mm, "end": v(28.28, 51.76) * mm});
            skLineSegment(sketch, "E4005", {"start": v(28.28, 51.76) * mm, "end": v(28.52, 51.9) * mm});
            skLineSegment(sketch, "E4006", {"start": v(28.52, 51.9) * mm, "end": v(28.76, 52.03) * mm});
            skLineSegment(sketch, "E4007", {"start": v(28.76, 52.03) * mm, "end": v(29.54, 52.32) * mm});
            skLineSegment(sketch, "E4008", {"start": v(29.54, 52.32) * mm, "end": v(30.62, 52.46) * mm});
            skLineSegment(sketch, "E4009", {"start": v(30.62, 52.46) * mm, "end": v(31.7, 52.32) * mm});
            skLineSegment(sketch, "E4010", {"start": v(31.7, 52.32) * mm, "end": v(32.48, 52.03) * mm});
            skLineSegment(sketch, "E4011", {"start": v(32.48, 52.03) * mm, "end": v(32.72, 51.9) * mm});
            skLineSegment(sketch, "E4012", {"start": v(32.72, 51.9) * mm, "end": v(32.96, 51.76) * mm});
            skLineSegment(sketch, "E4013", {"start": v(32.96, 51.76) * mm, "end": v(33.6, 51.22) * mm});
            skLineSegment(sketch, "E4014", {"start": v(33.6, 51.22) * mm, "end": v(34.26, 50.36) * mm});
            skLineSegment(sketch, "E4015", {"start": v(34.26, 50.36) * mm, "end": v(34.67, 49.36) * mm});
            skLineSegment(sketch, "E4016", {"start": v(34.67, 49.36) * mm, "end": v(34.82, 48.53) * mm});
            skLineSegment(sketch, "E4017", {"start": v(34.82, 48.53) * mm, "end": v(34.82, 48.26) * mm});
            skLineSegment(sketch, "E4018", {"start": v(38.24, -40.64) * mm, "end": v(38.24, -41.73) * mm});
            skLineSegment(sketch, "E4019", {"start": v(38.24, 35.56) * mm, "end": v(38.24, 35.13) * mm});
            skLineSegment(sketch, "E4020", {"start": v(-37.96, -40.64) * mm, "end": v(-37.05, -41.55) * mm});
            skLineSegment(sketch, "E4021", {"start": v(30.62, 48.26) * mm, "end": v(30.62, 43.92) * mm});
            skLineSegment(sketch, "E4022", {"start": v(-37.96, 15.24) * mm, "end": v(-37.96, 11.35) * mm});
            skLineSegment(sketch, "E4023", {"start": v(30.62, -20.32) * mm, "end": v(29.4, -20.32) * mm});
            skLineSegment(sketch, "E4024", {"start": v(-17.64, -20.32) * mm, "end": v(-21.27, -20.32) * mm});
            skLineSegment(sketch, "E4025", {"start": v(-59.55, 13.97) * mm, "end": v(-59.55, -13.97) * mm});
            skLineSegment(sketch, "E4026", {"start": v(-42.4, -47.26) * mm, "end": v(-42.4, -46.2) * mm});
            skLineSegment(sketch, "E4027", {"start": v(-42.4, -46.2) * mm, "end": v(-43.04, -45.56) * mm});
            skLineSegment(sketch, "E4028", {"start": v(-42.4, -47.26) * mm, "end": v(-42.4, -49.46) * mm});
            skLineSegment(sketch, "E4029", {"start": v(-42.4, -49.46) * mm, "end": v(-42.2, -49.66) * mm});
            skLineSegment(sketch, "E4030", {"start": v(-31.23, 49.2) * mm, "end": v(-41.42, 49.2) * mm});
            skLineSegment(sketch, "E4031", {"start": v(-41.42, 49.2) * mm, "end": v(-52.7, 37.93) * mm});
            skLineSegment(sketch, "E4032", {"start": v(-52.7, 37.93) * mm, "end": v(-52.7, 30.02) * mm});
            skLineSegment(sketch, "E4033", {"start": v(12.06, 12.88) * mm, "end": v(15.38, 9.56) * mm});
            skLineSegment(sketch, "E4034", {"start": v(15.38, 9.56) * mm, "end": v(15.38, -55.48) * mm});
            skLineSegment(sketch, "E4035", {"start": v(15.38, -55.48) * mm, "end": v(15.23, -55.63) * mm});
            skLineSegment(sketch, "E4036", {"start": v(-27.17, -52.07) * mm, "end": v(-20.69, -58.55) * mm});
            skLineSegment(sketch, "E4037", {"start": v(-20.69, -58.55) * mm, "end": v(12.31, -58.55) * mm});
            skLineSegment(sketch, "E4038", {"start": v(12.31, -58.55) * mm, "end": v(15.23, -55.63) * mm});
            skLineSegment(sketch, "E4039", {"start": v(52.24, -59.36) * mm, "end": v(52.24, -59.2) * mm});
            skLineSegment(sketch, "E4040", {"start": v(52.24, -59.2) * mm, "end": v(48.65, -55.63) * mm});
            skLineSegment(sketch, "E4041", {"start": v(48.65, -55.63) * mm, "end": v(15.23, -55.63) * mm});
            skLineSegment(sketch, "E4042", {"start": v(-46.67, -56.56) * mm, "end": v(-46.47, -56.56) * mm});
            skLineSegment(sketch, "E4043", {"start": v(-46.47, -56.56) * mm, "end": v(-44.9, -58.12) * mm});
            skLineSegment(sketch, "E4044", {"start": v(-44.9, -58.12) * mm, "end": v(-33.22, -58.12) * mm});
            skLineSegment(sketch, "E4045", {"start": v(-33.22, -58.12) * mm, "end": v(-32.16, -57.07) * mm});
            skLineSegment(sketch, "E4046", {"start": v(-32.16, -57.07) * mm, "end": v(-27.17, -52.07) * mm});
            skLineSegment(sketch, "E4047", {"start": v(44.02, 8.86) * mm, "end": v(43.94, 8.95) * mm});
            skLineSegment(sketch, "E4048", {"start": v(43.94, 8.95) * mm, "end": v(43.94, 22.2) * mm});
            skLineSegment(sketch, "E4049", {"start": v(43.94, 22.2) * mm, "end": v(50.2, 28.46) * mm});
            skLineSegment(sketch, "E4050", {"start": v(50.2, 28.46) * mm, "end": v(50.2, 30.46) * mm});
            skLineSegment(sketch, "E4051", {"start": v(22.75, -1.32) * mm, "end": v(19.13, 2.29) * mm});
            skLineSegment(sketch, "E4052", {"start": v(19.13, 2.29) * mm, "end": v(15.23, 2.29) * mm});
            skLineSegment(sketch, "E4053", {"start": v(-46.4, -46.48) * mm, "end": v(-46.35, -46.43) * mm});
            skLineSegment(sketch, "E4054", {"start": v(-46.35, -45.86) * mm, "end": v(-46.35, -45.71) * mm});
            skLineSegment(sketch, "E4055", {"start": v(-46.35, -46.43) * mm, "end": v(-46.35, -45.86) * mm});
            skLineSegment(sketch, "E4056", {"start": v(-46.4, -46.2) * mm, "end": v(-46.4, -47.26) * mm});
            skLineSegment(sketch, "E4057", {"start": v(35.59, 17.3) * mm, "end": v(16.47, 17.3) * mm});
            skLineSegment(sketch, "E4058", {"start": v(16.47, 17.3) * mm, "end": v(12.06, 12.88) * mm});
            skLineSegment(sketch, "E4059", {"start": v(44.02, 8.86) * mm, "end": v(35.59, 17.3) * mm});
            skLineSegment(sketch, "E4060", {"start": v(50.2, 40.66) * mm, "end": v(48.54, 40.66) * mm});
            skLineSegment(sketch, "E4061", {"start": v(48.54, 40.66) * mm, "end": v(46.74, 38.86) * mm});
            skLineSegment(sketch, "E4062", {"start": v(46.74, 38.86) * mm, "end": v(45.94, 38.06) * mm});
            skLineSegment(sketch, "E4063", {"start": v(50.2, 58.44) * mm, "end": v(48.54, 58.44) * mm});
            skLineSegment(sketch, "E4064", {"start": v(48.54, 58.44) * mm, "end": v(45.94, 55.84) * mm});
            skLineSegment(sketch, "E4065", {"start": v(50.2, 48.24) * mm, "end": v(50.2, 58.44) * mm});
            skLineSegment(sketch, "E4066", {"start": v(50.2, 40.66) * mm, "end": v(50.2, 48.24) * mm});
            skLineSegment(sketch, "E4067", {"start": v(50.2, 32.46) * mm, "end": v(50.2, 40.66) * mm});
            skLineSegment(sketch, "E4068", {"start": v(50.2, 30.46) * mm, "end": v(50.2, 32.46) * mm});
            skLineSegment(sketch, "E4069", {"start": v(-48.5, -51.96) * mm, "end": v(-48.5, -49.37) * mm});
            skLineSegment(sketch, "E4070", {"start": v(-48.5, -49.37) * mm, "end": v(-46.4, -47.26) * mm});
            skLineSegment(sketch, "E4071", {"start": v(-48.5, -51.96) * mm, "end": v(-42.2, -51.96) * mm});
            skLineSegment(sketch, "E4072", {"start": v(-46.67, -56.56) * mm, "end": v(-46.67, -53.79) * mm});
            skLineSegment(sketch, "E4073", {"start": v(-46.67, -53.79) * mm, "end": v(-48.5, -51.96) * mm});
            skLineSegment(sketch, "E4074", {"start": v(7.28, -45.67) * mm, "end": v(7.28, 10.04) * mm});
            skLineSegment(sketch, "E4075", {"start": v(7.28, 10.04) * mm, "end": v(5.08, 12.24) * mm});
            skLineSegment(sketch, "E4076", {"start": v(45.94, 20.66) * mm, "end": v(44.88, 19.6) * mm});
            skLineSegment(sketch, "E4077", {"start": v(44.88, 19.6) * mm, "end": v(44.88, 17.63) * mm});
            skLineSegment(sketch, "E4078", {"start": v(44.88, 17.63) * mm, "end": v(49.45, 13.06) * mm});
            skLineSegment(sketch, "E4079", {"start": v(49.45, 13.06) * mm, "end": v(50.2, 13.06) * mm});
            skLineSegment(sketch, "E4080", {"start": v(50.2, 23.26) * mm, "end": v(48.54, 23.26) * mm});
            skLineSegment(sketch, "E4081", {"start": v(48.54, 23.26) * mm, "end": v(46.74, 21.46) * mm});
            skLineSegment(sketch, "E4082", {"start": v(46.74, 21.46) * mm, "end": v(45.94, 20.66) * mm});
            skLineSegment(sketch, "E4083", {"start": v(49.99, 13.06) * mm, "end": v(50.74, 13.06) * mm});
            skLineSegment(sketch, "E4084", {"start": v(49.07, 23.26) * mm, "end": v(50.74, 23.26) * mm});
            skLineSegment(sketch, "E4085", {"start": v(49.99, 13.06) * mm, "end": v(46.51, 9.59) * mm});
            skLineSegment(sketch, "E4086", {"start": v(46.51, 9.59) * mm, "end": v(46.51, 8.74) * mm});
            skLineSegment(sketch, "E4087", {"start": v(53.48, -34.29) * mm, "end": v(53.48, 10.32) * mm});
            skLineSegment(sketch, "E4088", {"start": v(53.48, 10.32) * mm, "end": v(53.5, 10.33) * mm});
            skLineSegment(sketch, "E4089", {"start": v(53.5, 10.33) * mm, "end": v(53.5, 11.06) * mm});
            skLineSegment(sketch, "E4090", {"start": v(53.5, 11.06) * mm, "end": v(51.49, 13.06) * mm});
            skLineSegment(sketch, "E4091", {"start": v(51.49, 13.06) * mm, "end": v(50.74, 13.06) * mm});
            skLineSegment(sketch, "E4092", {"start": v(7.28, -45.67) * mm, "end": v(8.38, -45.67) * mm});
            skLineSegment(sketch, "E4093", {"start": v(8.38, -45.67) * mm, "end": v(13.6, -40.44) * mm});
            skLineSegment(sketch, "E4094", {"start": v(13.6, -40.44) * mm, "end": v(13.6, -40.39) * mm});
            skLineSegment(sketch, "E4095", {"start": v(-17.41, 35.33) * mm, "end": v(-17.41, 58.2) * mm});
            skLineSegment(sketch, "E4096", {"start": v(-17.41, 58.2) * mm, "end": v(-17.64, 58.42) * mm});
            skLineSegment(sketch, "E4097", {"start": v(-17.7, 58.37) * mm, "end": v(-17.64, 58.42) * mm});
            skLineSegment(sketch, "E4098", {"start": v(-42.67, -56.56) * mm, "end": v(-42.67, -54.73) * mm});
            skLineSegment(sketch, "E4099", {"start": v(-42.67, -54.73) * mm, "end": v(-42.2, -54.26) * mm});
            skLineSegment(sketch, "E4100", {"start": v(-42.2, -54.26) * mm, "end": v(-39.93, -54.26) * mm});
            skLineSegment(sketch, "E4101", {"start": v(-39.93, -54.26) * mm, "end": v(-31.98, -46.3) * mm});
            skLineSegment(sketch, "E4102", {"start": v(-13.93, -46.3) * mm, "end": v(-13.25, -46.99) * mm});
            skLineSegment(sketch, "E4103", {"start": v(-31.98, -46.3) * mm, "end": v(-13.93, -46.3) * mm});
            skLineSegment(sketch, "E4104", {"start": v(4.7, 12.63) * mm, "end": v(7.28, 10.04) * mm});
            skLineSegment(sketch, "E4105", {"start": v(-23, 13.9) * mm, "end": v(-24.27, 13.9) * mm});
            skLineSegment(sketch, "E4106", {"start": v(-24.27, 13.9) * mm, "end": v(-24.96, 14.58) * mm});
            skLineSegment(sketch, "E4107", {"start": v(-25, 11.74) * mm, "end": v(-23.31, 11.74) * mm});
            skLineSegment(sketch, "E4108", {"start": v(-23.31, 11.74) * mm, "end": v(-22.61, 12.44) * mm});
            skLineSegment(sketch, "E4109", {"start": v(-43.78, 57.1) * mm, "end": v(-43.78, 52.48) * mm});
            skLineSegment(sketch, "E4110", {"start": v(12.57, 22.66) * mm, "end": v(33.04, 22.66) * mm});
            skLineSegment(sketch, "E4111", {"start": v(41.93, 25.4) * mm, "end": v(41.48, 25.4) * mm});
            skLineSegment(sketch, "E4112", {"start": v(41.48, 25.4) * mm, "end": v(38.73, 22.66) * mm});
            skLineSegment(sketch, "E4113", {"start": v(38.73, 22.66) * mm, "end": v(32.9, 22.66) * mm});
            skLineSegment(sketch, "E4114", {"start": v(-21.1, 16.18) * mm, "end": v(-21.1, 17) * mm});
            skLineSegment(sketch, "E4115", {"start": v(-21.1, 17) * mm, "end": v(-23.38, 19.28) * mm});
            skLineSegment(sketch, "E4116", {"start": v(-4.39, 18.15) * mm, "end": v(-4.39, 17.47) * mm});
            skLineSegment(sketch, "E4117", {"start": v(-5.8, 59.28) * mm, "end": v(-4.94, 58.42) * mm});
            skLineSegment(sketch, "E4118", {"start": v(-23.38, 19.28) * mm, "end": v(-23.38, 20.04) * mm});
            skLineSegment(sketch, "E4119", {"start": v(-23.38, 20.04) * mm, "end": v(-22.47, 20.94) * mm});
            skLineSegment(sketch, "E4120", {"start": v(-22.47, 20.94) * mm, "end": v(-22.37, 20.94) * mm});
            skLineSegment(sketch, "E4121", {"start": v(-22.37, 20.94) * mm, "end": v(-15.33, 13.9) * mm});
            skLineSegment(sketch, "E4122", {"start": v(-15.33, 13.9) * mm, "end": v(-12.09, 13.9) * mm});
            skLineSegment(sketch, "E4123", {"start": v(-12.09, 13.9) * mm, "end": v(-11.7, 14.3) * mm});
            skLineSegment(sketch, "E4124", {"start": v(-11.7, 14.3) * mm, "end": v(-11.7, 18.1) * mm});
            skLineSegment(sketch, "E4125", {"start": v(-11.7, 18.1) * mm, "end": v(-12.4, 18.82) * mm});
            skLineSegment(sketch, "E4126", {"start": v(-12.4, 18.82) * mm, "end": v(-12.4, 20.94) * mm});
            skLineSegment(sketch, "E4127", {"start": v(-12.4, 20.94) * mm, "end": v(-12, 21.34) * mm});
            skLineSegment(sketch, "E4128", {"start": v(-2.87, 19.34) * mm, "end": v(-16.54, 33) * mm});
            skLineSegment(sketch, "E4129", {"start": v(-12, 21.34) * mm, "end": v(-7.58, 21.34) * mm});
            skLineSegment(sketch, "E4130", {"start": v(-7.58, 21.34) * mm, "end": v(-4.39, 18.15) * mm});
            skLineSegment(sketch, "E4131", {"start": v(-11.5, 60.45) * mm, "end": v(-10.53, 59.47) * mm});
            skLineSegment(sketch, "E4132", {"start": v(-4.39, 17.47) * mm, "end": v(-4, 17.07) * mm});
            skLineSegment(sketch, "E4133", {"start": v(-15.6, 62.01) * mm, "end": v(-14.6, 62.01) * mm});
            skLineSegment(sketch, "E4134", {"start": v(-4, 17.07) * mm, "end": v(-3.26, 17.07) * mm});
            skLineSegment(sketch, "E4135", {"start": v(-14.05, 61.47) * mm, "end": v(-14.05, 61.04) * mm});
            skLineSegment(sketch, "E4136", {"start": v(-3.26, 17.07) * mm, "end": v(-2.87, 17.47) * mm});
            skLineSegment(sketch, "E4137", {"start": v(-2.87, 17.47) * mm, "end": v(-2.87, 19.34) * mm});
            skLineSegment(sketch, "E4138", {"start": v(-16.54, 33) * mm, "end": v(-16.54, 61.09) * mm});
            skLineSegment(sketch, "E4139", {"start": v(-16.54, 61.09) * mm, "end": v(-15.6, 62.01) * mm});
            skLineSegment(sketch, "E4140", {"start": v(-14.6, 62.01) * mm, "end": v(-14.05, 61.47) * mm});
            skLineSegment(sketch, "E4141", {"start": v(-14.05, 61.04) * mm, "end": v(-13.07, 62.01) * mm});
            skLineSegment(sketch, "E4142", {"start": v(-13.07, 62.01) * mm, "end": v(-12.05, 62.01) * mm});
            skLineSegment(sketch, "E4143", {"start": v(-12.05, 62.01) * mm, "end": v(-11.5, 61.47) * mm});
            skLineSegment(sketch, "E4144", {"start": v(-11.5, 61.47) * mm, "end": v(-11.5, 60.45) * mm});
            skLineSegment(sketch, "E4145", {"start": v(-10.53, 59.47) * mm, "end": v(-6, 59.47) * mm});
            skLineSegment(sketch, "E4146", {"start": v(-6, 59.47) * mm, "end": v(-5.8, 59.28) * mm});
            skLineSegment(sketch, "E4147", {"start": v(-59.55, -62.23) * mm, "end": v(-53.96, -56.64) * mm});
            skLineSegment(sketch, "E4148", {"start": v(-53.96, -56.64) * mm, "end": v(-53.96, -17.27) * mm});
            skLineSegment(sketch, "E4149", {"start": v(-15.82, 12.88) * mm, "end": v(-15.88, 12.88) * mm});
            skLineSegment(sketch, "E4150", {"start": v(-15.88, 12.88) * mm, "end": v(-45.78, -17.02) * mm});
            skLineSegment(sketch, "E4151", {"start": v(-45.78, -17.02) * mm, "end": v(-54.07, -17.02) * mm});
            skLineSegment(sketch, "E4152", {"start": v(-54.07, -17.02) * mm, "end": v(-58.24, -21.2) * mm});
            skLineSegment(sketch, "E4153", {"start": v(-58.69, -58.83) * mm, "end": v(-59.55, -59.69) * mm});
            skLineSegment(sketch, "E4154", {"start": v(-58.24, -21.2) * mm, "end": v(-58.24, -58.38) * mm});
            skLineSegment(sketch, "E4155", {"start": v(-58.24, -58.38) * mm, "end": v(-58.69, -58.83) * mm});
            skLineSegment(sketch, "E4156", {"start": v(12.79, 20.7) * mm, "end": v(10.85, 20.7) * mm});
            skLineSegment(sketch, "E4157", {"start": v(10.85, 20.7) * mm, "end": v(3.02, 12.88) * mm});
            skLineSegment(sketch, "E4158", {"start": v(3.02, 12.88) * mm, "end": v(-15.82, 12.88) * mm});
            skLineSegment(sketch, "E4159", {"start": v(-15.82, 12.88) * mm, "end": v(-22.04, 19.1) * mm});
            skLineSegment(sketch, "E4160", {"start": v(-22.04, 19.1) * mm, "end": v(-22.61, 19.67) * mm});
            skLineSegment(sketch, "E4161", {"start": v(-62.1, -16.51) * mm, "end": v(-61.04, -15.46) * mm});
            skLineSegment(sketch, "E4162", {"start": v(-61.04, -15.46) * mm, "end": v(-61.04, -8.67) * mm});
            skLineSegment(sketch, "E4163", {"start": v(-61.04, -8.67) * mm, "end": v(-62.1, -7.62) * mm});
            skLineSegment(sketch, "E4164", {"start": v(2.22, 57.87) * mm, "end": v(-2, 62.08) * mm});
            skLineSegment(sketch, "E4165", {"start": v(-2, 62.08) * mm, "end": v(-8.9, 62.08) * mm});
            skLineSegment(sketch, "E4166", {"start": v(-8.9, 62.08) * mm, "end": v(-9.16, 61.82) * mm});
            skLineSegment(sketch, "E4167", {"start": v(-9.16, 61.82) * mm, "end": v(-10.02, 60.96) * mm});
            skLineSegment(sketch, "E4168", {"start": v(2.22, 21.77) * mm, "end": v(2.22, 57.87) * mm});
            skLineSegment(sketch, "E4169", {"start": v(-51.93, -23.62) * mm, "end": v(-15.81, 12.5) * mm});
            skLineSegment(sketch, "E4170", {"start": v(-15.81, 12.5) * mm, "end": v(3.18, 12.5) * mm});
            skLineSegment(sketch, "E4171", {"start": v(3.18, 12.5) * mm, "end": v(11, 20.32) * mm});
            skLineSegment(sketch, "E4172", {"start": v(11, 20.32) * mm, "end": v(12.95, 20.32) * mm});
            skLineSegment(sketch, "E4173", {"start": v(12.95, 20.32) * mm, "end": v(13.17, 20.54) * mm});
            skLineSegment(sketch, "E4174", {"start": v(13.17, 20.54) * mm, "end": v(13.17, 20.86) * mm});
            skLineSegment(sketch, "E4175", {"start": v(13.17, 20.86) * mm, "end": v(12.95, 21.08) * mm});
            skLineSegment(sketch, "E4176", {"start": v(12.95, 21.08) * mm, "end": v(3.4, 21.08) * mm});
            skLineSegment(sketch, "E4177", {"start": v(0.87, 18.56) * mm, "end": v(0.3, 17.99) * mm});
            skLineSegment(sketch, "E4178", {"start": v(3.4, 21.08) * mm, "end": v(0.87, 18.56) * mm});
            skLineSegment(sketch, "E4179", {"start": v(0.3, 17.99) * mm, "end": v(1.26, 18.95) * mm});
            skLineSegment(sketch, "E4180", {"start": v(-4.59, 59.84) * mm, "end": v(-6.36, 59.84) * mm});
            skLineSegment(sketch, "E4181", {"start": v(1.26, 18.95) * mm, "end": v(1.26, 54) * mm});
            skLineSegment(sketch, "E4182", {"start": v(1.26, 54) * mm, "end": v(-4.59, 59.84) * mm});
            skLineSegment(sketch, "E4183", {"start": v(-6.36, 59.84) * mm, "end": v(-7.48, 60.96) * mm});
            skLineSegment(sketch, "E4184", {"start": v(-58.5, 14.06) * mm, "end": v(-58.5, -17.63) * mm});
            skLineSegment(sketch, "E4185", {"start": v(-59.05, -20.1) * mm, "end": v(-58.5, -20.65) * mm});
            skLineSegment(sketch, "E4186", {"start": v(-60.06, -20.1) * mm, "end": v(-59.05, -20.1) * mm});
            skLineSegment(sketch, "E4187", {"start": v(-58.5, -20.65) * mm, "end": v(-58.5, -23.08) * mm});
            skLineSegment(sketch, "E4188", {"start": v(-52.7, 19.86) * mm, "end": v(-58.5, 14.06) * mm});
            skLineSegment(sketch, "E4189", {"start": v(-60.6, -18.54) * mm, "end": v(-60.6, -19.56) * mm});
            skLineSegment(sketch, "E4190", {"start": v(-58.5, -23.08) * mm, "end": v(-58.69, -23.27) * mm});
            skLineSegment(sketch, "E4191", {"start": v(-58.69, -23.27) * mm, "end": v(-59.55, -24.13) * mm});
            skLineSegment(sketch, "E4192", {"start": v(-58.5, -17.63) * mm, "end": v(-59.7, -17.63) * mm});
            skLineSegment(sketch, "E4193", {"start": v(-59.7, -17.63) * mm, "end": v(-60.6, -18.54) * mm});
            skLineSegment(sketch, "E4194", {"start": v(-60.6, -19.56) * mm, "end": v(-60.06, -20.1) * mm});
            skLineSegment(sketch, "E4195", {"start": v(-52.7, 19.86) * mm, "end": v(-44.16, 19.86) * mm});
            skLineSegment(sketch, "E4196", {"start": v(-44.16, 19.86) * mm, "end": v(-31.66, 32.36) * mm});
            skLineSegment(sketch, "E4197", {"start": v(0.44, 23.3) * mm, "end": v(-0.96, 21.9) * mm});
            skLineSegment(sketch, "E4198", {"start": v(-0.96, 21.9) * mm, "end": v(-0.96, 19.53) * mm});
            skLineSegment(sketch, "E4199", {"start": v(-0.96, 19.53) * mm, "end": v(-1.39, 19.1) * mm});
            skLineSegment(sketch, "E4200", {"start": v(-16.22, 33.14) * mm, "end": v(-16.22, 59.84) * mm});
            skLineSegment(sketch, "E4201", {"start": v(-1.39, 19.1) * mm, "end": v(-2.18, 19.1) * mm});
            skLineSegment(sketch, "E4202", {"start": v(-2.18, 19.1) * mm, "end": v(-16.22, 33.14) * mm});
            skLineSegment(sketch, "E4203", {"start": v(-16.22, 59.84) * mm, "end": v(-15.1, 60.96) * mm});
            skLineSegment(sketch, "E4204", {"start": v(-60.86, -20.28) * mm, "end": v(-60.41, -20.73) * mm});
            skLineSegment(sketch, "E4205", {"start": v(-60.86, -18.44) * mm, "end": v(-60.86, -20.28) * mm});
            skLineSegment(sketch, "E4206", {"start": v(-52.7, 22.4) * mm, "end": v(-60.6, 14.49) * mm});
            skLineSegment(sketch, "E4207", {"start": v(-60.6, 14.49) * mm, "end": v(-60.6, -18.18) * mm});
            skLineSegment(sketch, "E4208", {"start": v(-60.6, -18.18) * mm, "end": v(-60.86, -18.44) * mm});
            skLineSegment(sketch, "E4209", {"start": v(-60.41, -20.73) * mm, "end": v(-59.55, -21.59) * mm});
            skLineSegment(sketch, "E4210", {"start": v(-1.79, 19.93) * mm, "end": v(-1.79, 54.4) * mm});
            skLineSegment(sketch, "E4211", {"start": v(-52.7, 22.4) * mm, "end": v(-43.93, 22.4) * mm});
            skLineSegment(sketch, "E4212", {"start": v(-43.93, 22.4) * mm, "end": v(-31.76, 34.57) * mm});
            skLineSegment(sketch, "E4213", {"start": v(-1.79, 54.4) * mm, "end": v(-4.69, 57.3) * mm});
            skLineSegment(sketch, "E4214", {"start": v(-4.69, 57.3) * mm, "end": v(-13.1, 57.3) * mm});
            skLineSegment(sketch, "E4215", {"start": v(-13.68, 57.88) * mm, "end": v(-13.68, 59.84) * mm});
            skLineSegment(sketch, "E4216", {"start": v(-13.1, 57.3) * mm, "end": v(-13.68, 57.88) * mm});
            skLineSegment(sketch, "E4217", {"start": v(-13.68, 59.84) * mm, "end": v(-12.56, 60.96) * mm});
            skLineSegment(sketch, "E4218", {"start": v(-3.63, 17.83) * mm, "end": v(-18.76, 32.96) * mm});
            skLineSegment(sketch, "E4219", {"start": v(-18.76, 32.96) * mm, "end": v(-18.76, 59.84) * mm});
            skLineSegment(sketch, "E4220", {"start": v(-18.76, 59.84) * mm, "end": v(-18.5, 60.1) * mm});
            skLineSegment(sketch, "E4221", {"start": v(-18.5, 60.1) * mm, "end": v(-17.64, 60.96) * mm});
            skLineSegment(sketch, "E4222", {"start": v(-12.45, 14.66) * mm, "end": v(-29.84, 32.05) * mm});
            skLineSegment(sketch, "E4223", {"start": v(-21.04, 61.82) * mm, "end": v(-20.18, 60.96) * mm});
            skLineSegment(sketch, "E4224", {"start": v(-29.84, 32.05) * mm, "end": v(-29.84, 60.48) * mm});
            skLineSegment(sketch, "E4225", {"start": v(-29.84, 60.48) * mm, "end": v(-27.93, 62.4) * mm});
            skLineSegment(sketch, "E4226", {"start": v(-27.93, 62.4) * mm, "end": v(-21.62, 62.4) * mm});
            skLineSegment(sketch, "E4227", {"start": v(-21.62, 62.4) * mm, "end": v(-21.04, 61.82) * mm});
            skLineSegment(sketch, "E4228", {"start": v(-12.77, 21.7) * mm, "end": v(-12.77, 22.52) * mm});
            skLineSegment(sketch, "E4229", {"start": v(-12.77, 22.52) * mm, "end": v(-28.92, 38.66) * mm});
            skLineSegment(sketch, "E4230", {"start": v(-28.92, 38.66) * mm, "end": v(-28.92, 59.49) * mm});
            skLineSegment(sketch, "E4231", {"start": v(-28.92, 59.49) * mm, "end": v(-28.87, 59.54) * mm});
            skLineSegment(sketch, "E4232", {"start": v(-28.87, 59.54) * mm, "end": v(-27.27, 59.54) * mm});
            skLineSegment(sketch, "E4233", {"start": v(-27.27, 59.54) * mm, "end": v(-26.38, 60.42) * mm});
            skLineSegment(sketch, "E4234", {"start": v(-26.38, 60.42) * mm, "end": v(-26.38, 61.5) * mm});
            skLineSegment(sketch, "E4235", {"start": v(-26.38, 61.5) * mm, "end": v(-25.8, 62.08) * mm});
            skLineSegment(sketch, "E4236", {"start": v(-25.8, 62.08) * mm, "end": v(-23.84, 62.08) * mm});
            skLineSegment(sketch, "E4237", {"start": v(-23.84, 62.08) * mm, "end": v(-23.58, 61.82) * mm});
            skLineSegment(sketch, "E4238", {"start": v(-23.58, 61.82) * mm, "end": v(-22.72, 60.96) * mm});
            skLineSegment(sketch, "E4239", {"start": v(-9.22, 22.22) * mm, "end": v(-26.38, 39.38) * mm});
            skLineSegment(sketch, "E4240", {"start": v(-26.38, 39.38) * mm, "end": v(-26.38, 59.84) * mm});
            skLineSegment(sketch, "E4241", {"start": v(-26.38, 59.84) * mm, "end": v(-25.26, 60.96) * mm});
            skLineSegment(sketch, "E4242", {"start": v(45.94, 0) * mm, "end": v(47, 1.05) * mm});
            skLineSegment(sketch, "E4243", {"start": v(47, 1.05) * mm, "end": v(47, 6.14) * mm});
            skLineSegment(sketch, "E4244", {"start": v(47, 6.14) * mm, "end": v(44.92, 8.2) * mm});
            skLineSegment(sketch, "E4245", {"start": v(44.92, 8.2) * mm, "end": v(44.92, 8.76) * mm});
            skLineSegment(sketch, "E4246", {"start": v(-8.17, -52.07) * mm, "end": v(7.08, -52.07) * mm});
            skLineSegment(sketch, "E4247", {"start": v(7.08, -52.07) * mm, "end": v(7.28, -51.87) * mm});
            skLineSegment(sketch, "E4248", {"start": v(55.26, -32) * mm, "end": v(55.26, 12.13) * mm});
            skLineSegment(sketch, "E4249", {"start": v(55.26, 12.13) * mm, "end": v(49.22, 18.16) * mm});
            skLineSegment(sketch, "E4250", {"start": v(49.22, 18.16) * mm, "end": v(46.47, 18.16) * mm});
            skLineSegment(sketch, "E4251", {"start": v(7.28, -48.49) * mm, "end": v(13.86, -41.91) * mm});
            skLineSegment(sketch, "E4252", {"start": v(7.28, -51.87) * mm, "end": v(7.28, -48.49) * mm});
            skLineSegment(sketch, "E4253", {"start": v(-13.25, -46.99) * mm, "end": v(-8.17, -52.07) * mm});
            skLineSegment(sketch, "E4254", {"start": v(42.83, 25.4) * mm, "end": v(42.83, 32.45) * mm});
            skLineSegment(sketch, "E4255", {"start": v(42.83, 32.45) * mm, "end": v(45.94, 35.56) * mm});
            skLineSegment(sketch, "E4256", {"start": v(-57.91, -62.17) * mm, "end": v(-57.92, -62.16) * mm});
            skLineSegment(sketch, "E4257", {"start": v(-57.92, -62.16) * mm, "end": v(-57.94, -62.16) * mm});
            skLineSegment(sketch, "E4258", {"start": v(-57.94, -62.16) * mm, "end": v(-57.96, -62.17) * mm});
            skLineSegment(sketch, "E4259", {"start": v(-57.96, -62.17) * mm, "end": v(-57.97, -62.18) * mm});
            skLineSegment(sketch, "E4260", {"start": v(-57.97, -62.18) * mm, "end": v(-57.98, -62.19) * mm});
            skLineSegment(sketch, "E4261", {"start": v(-57.98, -62.19) * mm, "end": v(-57.98, -62.21) * mm});
            skLineSegment(sketch, "E4262", {"start": v(-57.98, -62.21) * mm, "end": v(-57.98, -62.23) * mm});
            skLineSegment(sketch, "E4263", {"start": v(-57.98, -62.23) * mm, "end": v(-57.98, -62.26) * mm});
            skLineSegment(sketch, "E4264", {"start": v(-57.98, -62.26) * mm, "end": v(-57.97, -62.27) * mm});
            skLineSegment(sketch, "E4265", {"start": v(-57.97, -62.27) * mm, "end": v(-57.96, -62.28) * mm});
            skLineSegment(sketch, "E4266", {"start": v(-57.96, -62.28) * mm, "end": v(-57.94, -62.29) * mm});
            skLineSegment(sketch, "E4267", {"start": v(-57.94, -62.29) * mm, "end": v(-57.93, -62.29) * mm});
            skLineSegment(sketch, "E4268", {"start": v(-57.93, -62.29) * mm, "end": v(-57.91, -62.28) * mm});
            skLineSegment(sketch, "E4269", {"start": v(-57.91, -62.28) * mm, "end": v(-57.9, -62.27) * mm});
            skLineSegment(sketch, "E4270", {"start": v(-57.9, -62.27) * mm, "end": v(-57.9, -62.23) * mm});
            skLineSegment(sketch, "E4271", {"start": v(-57.9, -62.23) * mm, "end": v(-57.93, -62.23) * mm});
            skLineSegment(sketch, "E4272", {"start": v(-51.04, 57.59) * mm, "end": v(-50.28, 57.59) * mm});
            skLineSegment(sketch, "E4273", {"start": v(-28.15, 56.15) * mm, "end": v(-28.16, 56.16) * mm});
            skLineSegment(sketch, "E4274", {"start": v(-28.16, 56.16) * mm, "end": v(-28.18, 56.16) * mm});
            skLineSegment(sketch, "E4275", {"start": v(-28.18, 56.16) * mm, "end": v(-28.2, 56.15) * mm});
            skLineSegment(sketch, "E4276", {"start": v(-28.2, 56.15) * mm, "end": v(-28.21, 56.14) * mm});
            skLineSegment(sketch, "E4277", {"start": v(-28.21, 56.14) * mm, "end": v(-28.22, 56.12) * mm});
            skLineSegment(sketch, "E4278", {"start": v(-28.22, 56.12) * mm, "end": v(-28.22, 56.1) * mm});
            skLineSegment(sketch, "E4279", {"start": v(-28.22, 56.1) * mm, "end": v(-28.22, 56.08) * mm});
            skLineSegment(sketch, "E4280", {"start": v(-28.22, 56.08) * mm, "end": v(-28.22, 56.06) * mm});
            skLineSegment(sketch, "E4281", {"start": v(-28.22, 56.06) * mm, "end": v(-28.21, 56.04) * mm});
            skLineSegment(sketch, "E4282", {"start": v(-28.21, 56.04) * mm, "end": v(-28.2, 56.03) * mm});
            skLineSegment(sketch, "E4283", {"start": v(-28.2, 56.03) * mm, "end": v(-28.18, 56.03) * mm});
            skLineSegment(sketch, "E4284", {"start": v(-28.18, 56.03) * mm, "end": v(-28.17, 56.03) * mm});
            skLineSegment(sketch, "E4285", {"start": v(-28.17, 56.03) * mm, "end": v(-28.15, 56.03) * mm});
            skLineSegment(sketch, "E4286", {"start": v(-28.15, 56.03) * mm, "end": v(-28.15, 56.04) * mm});
            skLineSegment(sketch, "E4287", {"start": v(-28.15, 56.04) * mm, "end": v(-28.15, 56.08) * mm});
            skLineSegment(sketch, "E4288", {"start": v(-28.15, 56.08) * mm, "end": v(-28.17, 56.08) * mm});
            skLineSegment(sketch, "E4289", {"start": v(-28.1, 56.03) * mm, "end": v(-28.1, 56.15) * mm});
            skLineSegment(sketch, "E4290", {"start": v(-28.1, 56.15) * mm, "end": v(-28.02, 56.03) * mm});
            skLineSegment(sketch, "E4291", {"start": v(-28.02, 56.03) * mm, "end": v(-28.02, 56.15) * mm});
            skLineSegment(sketch, "E4292", {"start": v(-27.96, 56.03) * mm, "end": v(-27.96, 56.15) * mm});
            skLineSegment(sketch, "E4293", {"start": v(-27.96, 56.15) * mm, "end": v(-27.93, 56.15) * mm});
            skLineSegment(sketch, "E4294", {"start": v(-27.93, 56.15) * mm, "end": v(-27.91, 56.15) * mm});
            skLineSegment(sketch, "E4295", {"start": v(-27.91, 56.15) * mm, "end": v(-27.9, 56.14) * mm});
            skLineSegment(sketch, "E4296", {"start": v(-27.9, 56.14) * mm, "end": v(-27.9, 56.12) * mm});
            skLineSegment(sketch, "E4297", {"start": v(-27.9, 56.12) * mm, "end": v(-27.88, 56.1) * mm});
            skLineSegment(sketch, "E4298", {"start": v(-27.88, 56.1) * mm, "end": v(-27.88, 56.08) * mm});
            skLineSegment(sketch, "E4299", {"start": v(-27.88, 56.08) * mm, "end": v(-27.9, 56.06) * mm});
            skLineSegment(sketch, "E4300", {"start": v(-27.9, 56.06) * mm, "end": v(-27.9, 56.04) * mm});
            skLineSegment(sketch, "E4301", {"start": v(-27.9, 56.04) * mm, "end": v(-27.91, 56.03) * mm});
            skLineSegment(sketch, "E4302", {"start": v(-27.91, 56.03) * mm, "end": v(-27.93, 56.03) * mm});
            skLineSegment(sketch, "E4303", {"start": v(-27.93, 56.03) * mm, "end": v(-27.96, 56.03) * mm});
            skLineSegment(sketch, "E4304", {"start": v(-23.04, 56.74) * mm, "end": v(-22.94, 56.74) * mm});
            skLineSegment(sketch, "E4305", {"start": v(-22.99, 56.7) * mm, "end": v(-22.99, 56.79) * mm});
            skLineSegment(sketch, "E4306", {"start": v(-22.82, 56.82) * mm, "end": v(-22.88, 56.82) * mm});
            skLineSegment(sketch, "E4307", {"start": v(-22.88, 56.82) * mm, "end": v(-22.89, 56.76) * mm});
            skLineSegment(sketch, "E4308", {"start": v(-22.89, 56.76) * mm, "end": v(-22.88, 56.77) * mm});
            skLineSegment(sketch, "E4309", {"start": v(-22.88, 56.77) * mm, "end": v(-22.87, 56.77) * mm});
            skLineSegment(sketch, "E4310", {"start": v(-22.87, 56.77) * mm, "end": v(-22.84, 56.77) * mm});
            skLineSegment(sketch, "E4311", {"start": v(-22.84, 56.77) * mm, "end": v(-22.83, 56.77) * mm});
            skLineSegment(sketch, "E4312", {"start": v(-22.83, 56.77) * mm, "end": v(-22.82, 56.76) * mm});
            skLineSegment(sketch, "E4313", {"start": v(-22.82, 56.76) * mm, "end": v(-22.81, 56.75) * mm});
            skLineSegment(sketch, "E4314", {"start": v(-22.81, 56.75) * mm, "end": v(-22.81, 56.72) * mm});
            skLineSegment(sketch, "E4315", {"start": v(-22.81, 56.72) * mm, "end": v(-22.82, 56.7) * mm});
            skLineSegment(sketch, "E4316", {"start": v(-22.82, 56.7) * mm, "end": v(-22.83, 56.7) * mm});
            skLineSegment(sketch, "E4317", {"start": v(-22.83, 56.7) * mm, "end": v(-22.84, 56.7) * mm});
            skLineSegment(sketch, "E4318", {"start": v(-22.84, 56.7) * mm, "end": v(-22.87, 56.7) * mm});
            skLineSegment(sketch, "E4319", {"start": v(-22.87, 56.7) * mm, "end": v(-22.88, 56.7) * mm});
            skLineSegment(sketch, "E4320", {"start": v(-22.88, 56.7) * mm, "end": v(-22.89, 56.7) * mm});
            skLineSegment(sketch, "E4321", {"start": v(-22.78, 56.82) * mm, "end": v(-22.73, 56.7) * mm});
            skLineSegment(sketch, "E4322", {"start": v(-22.73, 56.7) * mm, "end": v(-22.7, 56.82) * mm});
            skLineSegment(sketch, "E4323", {"start": v(-17.81, 56.76) * mm, "end": v(-17.8, 56.75) * mm});
            skLineSegment(sketch, "E4324", {"start": v(-17.8, 56.75) * mm, "end": v(-17.79, 56.75) * mm});
            skLineSegment(sketch, "E4325", {"start": v(-17.79, 56.75) * mm, "end": v(-17.78, 56.74) * mm});
            skLineSegment(sketch, "E4326", {"start": v(-17.78, 56.74) * mm, "end": v(-17.78, 56.72) * mm});
            skLineSegment(sketch, "E4327", {"start": v(-17.78, 56.72) * mm, "end": v(-17.79, 56.7) * mm});
            skLineSegment(sketch, "E4328", {"start": v(-17.79, 56.7) * mm, "end": v(-17.8, 56.7) * mm});
            skLineSegment(sketch, "E4329", {"start": v(-17.8, 56.7) * mm, "end": v(-17.8, 56.7) * mm});
            skLineSegment(sketch, "E4330", {"start": v(-17.8, 56.7) * mm, "end": v(-17.85, 56.7) * mm});
            skLineSegment(sketch, "E4331", {"start": v(-17.85, 56.7) * mm, "end": v(-17.85, 56.82) * mm});
            skLineSegment(sketch, "E4332", {"start": v(-17.85, 56.82) * mm, "end": v(-17.81, 56.82) * mm});
            skLineSegment(sketch, "E4333", {"start": v(-17.81, 56.82) * mm, "end": v(-17.8, 56.82) * mm});
            skLineSegment(sketch, "E4334", {"start": v(-17.8, 56.82) * mm, "end": v(-17.8, 56.8) * mm});
            skLineSegment(sketch, "E4335", {"start": v(-17.8, 56.8) * mm, "end": v(-17.79, 56.8) * mm});
            skLineSegment(sketch, "E4336", {"start": v(-17.79, 56.8) * mm, "end": v(-17.79, 56.78) * mm});
            skLineSegment(sketch, "E4337", {"start": v(-17.79, 56.78) * mm, "end": v(-17.8, 56.77) * mm});
            skLineSegment(sketch, "E4338", {"start": v(-17.8, 56.77) * mm, "end": v(-17.8, 56.77) * mm});
            skLineSegment(sketch, "E4339", {"start": v(-17.8, 56.77) * mm, "end": v(-17.81, 56.76) * mm});
            skLineSegment(sketch, "E4340", {"start": v(-17.81, 56.76) * mm, "end": v(-17.85, 56.76) * mm});
            skLineSegment(sketch, "E4341", {"start": v(-17.73, 56.73) * mm, "end": v(-17.67, 56.73) * mm});
            skLineSegment(sketch, "E4342", {"start": v(-17.74, 56.7) * mm, "end": v(-17.7, 56.82) * mm});
            skLineSegment(sketch, "E4343", {"start": v(-17.7, 56.82) * mm, "end": v(-17.66, 56.7) * mm});
            skLineSegment(sketch, "E4344", {"start": v(-17.64, 56.82) * mm, "end": v(-17.56, 56.82) * mm});
            skLineSegment(sketch, "E4345", {"start": v(-17.6, 56.7) * mm, "end": v(-17.6, 56.82) * mm});
            skLineSegment(sketch, "E4346", {"start": v(-17.54, 56.82) * mm, "end": v(-17.46, 56.82) * mm});
            skLineSegment(sketch, "E4347", {"start": v(-17.5, 56.7) * mm, "end": v(-17.5, 56.82) * mm});
            skLineSegment(sketch, "E4348", {"start": v(-17.42, 56.74) * mm, "end": v(-17.33, 56.74) * mm});
            skLineSegment(sketch, "E4349", {"start": v(-17.37, 56.7) * mm, "end": v(-17.37, 56.79) * mm});
            skLineSegment(sketch, "E4350", {"start": v(-7.62, 56.76) * mm, "end": v(-7.6, 56.75) * mm});
            skLineSegment(sketch, "E4351", {"start": v(-7.6, 56.75) * mm, "end": v(-7.6, 56.75) * mm});
            skLineSegment(sketch, "E4352", {"start": v(-7.6, 56.75) * mm, "end": v(-7.58, 56.74) * mm});
            skLineSegment(sketch, "E4353", {"start": v(-7.58, 56.74) * mm, "end": v(-7.58, 56.72) * mm});
            skLineSegment(sketch, "E4354", {"start": v(-7.58, 56.72) * mm, "end": v(-7.6, 56.7) * mm});
            skLineSegment(sketch, "E4355", {"start": v(-7.6, 56.7) * mm, "end": v(-7.6, 56.7) * mm});
            skLineSegment(sketch, "E4356", {"start": v(-7.6, 56.7) * mm, "end": v(-7.61, 56.7) * mm});
            skLineSegment(sketch, "E4357", {"start": v(-7.61, 56.7) * mm, "end": v(-7.66, 56.7) * mm});
            skLineSegment(sketch, "E4358", {"start": v(-7.66, 56.7) * mm, "end": v(-7.66, 56.82) * mm});
            skLineSegment(sketch, "E4359", {"start": v(-7.66, 56.82) * mm, "end": v(-7.62, 56.82) * mm});
            skLineSegment(sketch, "E4360", {"start": v(-7.62, 56.82) * mm, "end": v(-7.6, 56.82) * mm});
            skLineSegment(sketch, "E4361", {"start": v(-7.6, 56.82) * mm, "end": v(-7.6, 56.8) * mm});
            skLineSegment(sketch, "E4362", {"start": v(-7.6, 56.8) * mm, "end": v(-7.6, 56.8) * mm});
            skLineSegment(sketch, "E4363", {"start": v(-7.6, 56.8) * mm, "end": v(-7.6, 56.78) * mm});
            skLineSegment(sketch, "E4364", {"start": v(-7.6, 56.78) * mm, "end": v(-7.6, 56.77) * mm});
            skLineSegment(sketch, "E4365", {"start": v(-7.6, 56.77) * mm, "end": v(-7.6, 56.77) * mm});
            skLineSegment(sketch, "E4366", {"start": v(-7.6, 56.77) * mm, "end": v(-7.62, 56.76) * mm});
            skLineSegment(sketch, "E4367", {"start": v(-7.62, 56.76) * mm, "end": v(-7.66, 56.76) * mm});
            skLineSegment(sketch, "E4368", {"start": v(-7.56, 56.68) * mm, "end": v(-7.47, 56.68) * mm});
            skLineSegment(sketch, "E4369", {"start": v(-7.37, 56.7) * mm, "end": v(-7.44, 56.7) * mm});
            skLineSegment(sketch, "E4370", {"start": v(-7.44, 56.7) * mm, "end": v(-7.44, 56.82) * mm});
            skLineSegment(sketch, "E4371", {"start": v(-7.33, 56.76) * mm, "end": v(-7.3, 56.76) * mm});
            skLineSegment(sketch, "E4372", {"start": v(-7.27, 56.7) * mm, "end": v(-7.33, 56.7) * mm});
            skLineSegment(sketch, "E4373", {"start": v(-7.33, 56.7) * mm, "end": v(-7.33, 56.82) * mm});
            skLineSegment(sketch, "E4374", {"start": v(-7.33, 56.82) * mm, "end": v(-7.27, 56.82) * mm});
            skLineSegment(sketch, "E4375", {"start": v(-7.22, 56.7) * mm, "end": v(-7.22, 56.82) * mm});
            skLineSegment(sketch, "E4376", {"start": v(-7.22, 56.82) * mm, "end": v(-7.19, 56.82) * mm});
            skLineSegment(sketch, "E4377", {"start": v(-7.19, 56.82) * mm, "end": v(-7.17, 56.82) * mm});
            skLineSegment(sketch, "E4378", {"start": v(-7.17, 56.82) * mm, "end": v(-7.16, 56.8) * mm});
            skLineSegment(sketch, "E4379", {"start": v(-7.16, 56.8) * mm, "end": v(-7.15, 56.79) * mm});
            skLineSegment(sketch, "E4380", {"start": v(-7.15, 56.79) * mm, "end": v(-7.15, 56.77) * mm});
            skLineSegment(sketch, "E4381", {"start": v(-7.15, 56.77) * mm, "end": v(-7.15, 56.75) * mm});
            skLineSegment(sketch, "E4382", {"start": v(-7.15, 56.75) * mm, "end": v(-7.15, 56.72) * mm});
            skLineSegment(sketch, "E4383", {"start": v(-7.15, 56.72) * mm, "end": v(-7.16, 56.71) * mm});
            skLineSegment(sketch, "E4384", {"start": v(-7.16, 56.71) * mm, "end": v(-7.17, 56.7) * mm});
            skLineSegment(sketch, "E4385", {"start": v(-7.17, 56.7) * mm, "end": v(-7.19, 56.7) * mm});
            skLineSegment(sketch, "E4386", {"start": v(-7.19, 56.7) * mm, "end": v(-7.22, 56.7) * mm});
            skLineSegment(sketch, "E4387", {"start": v(-5.1, 56.82) * mm, "end": v(-5.12, 56.82) * mm});
            skLineSegment(sketch, "E4388", {"start": v(-5.12, 56.82) * mm, "end": v(-5.13, 56.82) * mm});
            skLineSegment(sketch, "E4389", {"start": v(-5.13, 56.82) * mm, "end": v(-5.15, 56.82) * mm});
            skLineSegment(sketch, "E4390", {"start": v(-5.15, 56.82) * mm, "end": v(-5.16, 56.8) * mm});
            skLineSegment(sketch, "E4391", {"start": v(-5.16, 56.8) * mm, "end": v(-5.17, 56.79) * mm});
            skLineSegment(sketch, "E4392", {"start": v(-5.17, 56.79) * mm, "end": v(-5.17, 56.77) * mm});
            skLineSegment(sketch, "E4393", {"start": v(-5.17, 56.77) * mm, "end": v(-5.17, 56.75) * mm});
            skLineSegment(sketch, "E4394", {"start": v(-5.17, 56.75) * mm, "end": v(-5.17, 56.72) * mm});
            skLineSegment(sketch, "E4395", {"start": v(-5.17, 56.72) * mm, "end": v(-5.16, 56.71) * mm});
            skLineSegment(sketch, "E4396", {"start": v(-5.16, 56.71) * mm, "end": v(-5.15, 56.7) * mm});
            skLineSegment(sketch, "E4397", {"start": v(-5.15, 56.7) * mm, "end": v(-5.13, 56.7) * mm});
            skLineSegment(sketch, "E4398", {"start": v(-5.13, 56.7) * mm, "end": v(-5.12, 56.7) * mm});
            skLineSegment(sketch, "E4399", {"start": v(-5.12, 56.7) * mm, "end": v(-5.1, 56.7) * mm});
            skLineSegment(sketch, "E4400", {"start": v(-5.1, 56.7) * mm, "end": v(-5.1, 56.7) * mm});
            skLineSegment(sketch, "E4401", {"start": v(-5.1, 56.7) * mm, "end": v(-5.1, 56.75) * mm});
            skLineSegment(sketch, "E4402", {"start": v(-5.1, 56.75) * mm, "end": v(-5.12, 56.75) * mm});
            skLineSegment(sketch, "E4403", {"start": v(-5.07, 56.68) * mm, "end": v(-4.98, 56.68) * mm});
            skLineSegment(sketch, "E4404", {"start": v(-4.88, 56.7) * mm, "end": v(-4.94, 56.7) * mm});
            skLineSegment(sketch, "E4405", {"start": v(-4.94, 56.7) * mm, "end": v(-4.94, 56.82) * mm});
            skLineSegment(sketch, "E4406", {"start": v(-4.84, 56.76) * mm, "end": v(-4.8, 56.76) * mm});
            skLineSegment(sketch, "E4407", {"start": v(-4.78, 56.7) * mm, "end": v(-4.84, 56.7) * mm});
            skLineSegment(sketch, "E4408", {"start": v(-4.84, 56.7) * mm, "end": v(-4.84, 56.82) * mm});
            skLineSegment(sketch, "E4409", {"start": v(-4.84, 56.82) * mm, "end": v(-4.78, 56.82) * mm});
            skLineSegment(sketch, "E4410", {"start": v(-4.73, 56.7) * mm, "end": v(-4.73, 56.82) * mm});
            skLineSegment(sketch, "E4411", {"start": v(-4.73, 56.82) * mm, "end": v(-4.7, 56.82) * mm});
            skLineSegment(sketch, "E4412", {"start": v(-4.7, 56.82) * mm, "end": v(-4.68, 56.82) * mm});
            skLineSegment(sketch, "E4413", {"start": v(-4.68, 56.82) * mm, "end": v(-4.67, 56.8) * mm});
            skLineSegment(sketch, "E4414", {"start": v(-4.67, 56.8) * mm, "end": v(-4.66, 56.79) * mm});
            skLineSegment(sketch, "E4415", {"start": v(-4.66, 56.79) * mm, "end": v(-4.66, 56.77) * mm});
            skLineSegment(sketch, "E4416", {"start": v(-4.66, 56.77) * mm, "end": v(-4.66, 56.75) * mm});
            skLineSegment(sketch, "E4417", {"start": v(-4.66, 56.75) * mm, "end": v(-4.66, 56.72) * mm});
            skLineSegment(sketch, "E4418", {"start": v(-4.66, 56.72) * mm, "end": v(-4.67, 56.71) * mm});
            skLineSegment(sketch, "E4419", {"start": v(-4.67, 56.71) * mm, "end": v(-4.68, 56.7) * mm});
            skLineSegment(sketch, "E4420", {"start": v(-4.68, 56.7) * mm, "end": v(-4.7, 56.7) * mm});
            skLineSegment(sketch, "E4421", {"start": v(-4.7, 56.7) * mm, "end": v(-4.73, 56.7) * mm});
            skLineSegment(sketch, "E4422", {"start": v(-4.99, 62.52) * mm, "end": v(-5, 62.53) * mm});
            skLineSegment(sketch, "E4423", {"start": v(-5, 62.53) * mm, "end": v(-5.02, 62.53) * mm});
            skLineSegment(sketch, "E4424", {"start": v(-5.02, 62.53) * mm, "end": v(-5.03, 62.52) * mm});
            skLineSegment(sketch, "E4425", {"start": v(-5.03, 62.52) * mm, "end": v(-5.05, 62.51) * mm});
            skLineSegment(sketch, "E4426", {"start": v(-5.05, 62.51) * mm, "end": v(-5.05, 62.5) * mm});
            skLineSegment(sketch, "E4427", {"start": v(-5.05, 62.5) * mm, "end": v(-5.06, 62.48) * mm});
            skLineSegment(sketch, "E4428", {"start": v(-5.06, 62.48) * mm, "end": v(-5.06, 62.46) * mm});
            skLineSegment(sketch, "E4429", {"start": v(-5.06, 62.46) * mm, "end": v(-5.05, 62.43) * mm});
            skLineSegment(sketch, "E4430", {"start": v(-5.05, 62.43) * mm, "end": v(-5.05, 62.42) * mm});
            skLineSegment(sketch, "E4431", {"start": v(-5.05, 62.42) * mm, "end": v(-5.03, 62.4) * mm});
            skLineSegment(sketch, "E4432", {"start": v(-5.03, 62.4) * mm, "end": v(-5.02, 62.4) * mm});
            skLineSegment(sketch, "E4433", {"start": v(-5.02, 62.4) * mm, "end": v(-5, 62.4) * mm});
            skLineSegment(sketch, "E4434", {"start": v(-5, 62.4) * mm, "end": v(-4.99, 62.4) * mm});
            skLineSegment(sketch, "E4435", {"start": v(-4.99, 62.4) * mm, "end": v(-4.98, 62.42) * mm});
            skLineSegment(sketch, "E4436", {"start": v(-4.98, 62.42) * mm, "end": v(-4.98, 62.46) * mm});
            skLineSegment(sketch, "E4437", {"start": v(-4.98, 62.46) * mm, "end": v(-5, 62.46) * mm});
            skLineSegment(sketch, "E4438", {"start": v(-4.93, 62.4) * mm, "end": v(-4.93, 62.53) * mm});
            skLineSegment(sketch, "E4439", {"start": v(-4.93, 62.53) * mm, "end": v(-4.85, 62.4) * mm});
            skLineSegment(sketch, "E4440", {"start": v(-4.85, 62.4) * mm, "end": v(-4.85, 62.53) * mm});
            skLineSegment(sketch, "E4441", {"start": v(-4.8, 62.4) * mm, "end": v(-4.8, 62.53) * mm});
            skLineSegment(sketch, "E4442", {"start": v(-4.8, 62.53) * mm, "end": v(-4.76, 62.53) * mm});
            skLineSegment(sketch, "E4443", {"start": v(-4.76, 62.53) * mm, "end": v(-4.75, 62.52) * mm});
            skLineSegment(sketch, "E4444", {"start": v(-4.75, 62.52) * mm, "end": v(-4.73, 62.51) * mm});
            skLineSegment(sketch, "E4445", {"start": v(-4.73, 62.51) * mm, "end": v(-4.73, 62.5) * mm});
            skLineSegment(sketch, "E4446", {"start": v(-4.73, 62.5) * mm, "end": v(-4.72, 62.48) * mm});
            skLineSegment(sketch, "E4447", {"start": v(-4.72, 62.48) * mm, "end": v(-4.72, 62.46) * mm});
            skLineSegment(sketch, "E4448", {"start": v(-4.72, 62.46) * mm, "end": v(-4.73, 62.43) * mm});
            skLineSegment(sketch, "E4449", {"start": v(-4.73, 62.43) * mm, "end": v(-4.73, 62.42) * mm});
            skLineSegment(sketch, "E4450", {"start": v(-4.73, 62.42) * mm, "end": v(-4.75, 62.4) * mm});
            skLineSegment(sketch, "E4451", {"start": v(-4.75, 62.4) * mm, "end": v(-4.76, 62.4) * mm});
            skLineSegment(sketch, "E4452", {"start": v(-4.76, 62.4) * mm, "end": v(-4.8, 62.4) * mm});
            skLineSegment(sketch, "E4453", {"start": v(-7.73, 62.4) * mm, "end": v(-7.71, 62.4) * mm});
            skLineSegment(sketch, "E4454", {"start": v(-7.71, 62.4) * mm, "end": v(-7.68, 62.4) * mm});
            skLineSegment(sketch, "E4455", {"start": v(-7.68, 62.4) * mm, "end": v(-7.67, 62.4) * mm});
            skLineSegment(sketch, "E4456", {"start": v(-7.67, 62.4) * mm, "end": v(-7.67, 62.42) * mm});
            skLineSegment(sketch, "E4457", {"start": v(-7.67, 62.42) * mm, "end": v(-7.66, 62.43) * mm});
            skLineSegment(sketch, "E4458", {"start": v(-7.66, 62.43) * mm, "end": v(-7.66, 62.44) * mm});
            skLineSegment(sketch, "E4459", {"start": v(-7.66, 62.44) * mm, "end": v(-7.67, 62.45) * mm});
            skLineSegment(sketch, "E4460", {"start": v(-7.67, 62.45) * mm, "end": v(-7.67, 62.46) * mm});
            skLineSegment(sketch, "E4461", {"start": v(-7.67, 62.46) * mm, "end": v(-7.68, 62.46) * mm});
            skLineSegment(sketch, "E4462", {"start": v(-7.68, 62.46) * mm, "end": v(-7.7, 62.47) * mm});
            skLineSegment(sketch, "E4463", {"start": v(-7.7, 62.47) * mm, "end": v(-7.72, 62.48) * mm});
            skLineSegment(sketch, "E4464", {"start": v(-7.72, 62.48) * mm, "end": v(-7.73, 62.48) * mm});
            skLineSegment(sketch, "E4465", {"start": v(-7.73, 62.48) * mm, "end": v(-7.73, 62.5) * mm});
            skLineSegment(sketch, "E4466", {"start": v(-7.73, 62.5) * mm, "end": v(-7.73, 62.5) * mm});
            skLineSegment(sketch, "E4467", {"start": v(-7.73, 62.5) * mm, "end": v(-7.73, 62.52) * mm});
            skLineSegment(sketch, "E4468", {"start": v(-7.73, 62.52) * mm, "end": v(-7.72, 62.52) * mm});
            skLineSegment(sketch, "E4469", {"start": v(-7.72, 62.52) * mm, "end": v(-7.7, 62.53) * mm});
            skLineSegment(sketch, "E4470", {"start": v(-7.7, 62.53) * mm, "end": v(-7.68, 62.53) * mm});
            skLineSegment(sketch, "E4471", {"start": v(-7.68, 62.53) * mm, "end": v(-7.66, 62.52) * mm});
            skLineSegment(sketch, "E4472", {"start": v(-7.53, 62.42) * mm, "end": v(-7.54, 62.4) * mm});
            skLineSegment(sketch, "E4473", {"start": v(-7.54, 62.4) * mm, "end": v(-7.56, 62.4) * mm});
            skLineSegment(sketch, "E4474", {"start": v(-7.56, 62.4) * mm, "end": v(-7.57, 62.4) * mm});
            skLineSegment(sketch, "E4475", {"start": v(-7.57, 62.4) * mm, "end": v(-7.59, 62.4) * mm});
            skLineSegment(sketch, "E4476", {"start": v(-7.59, 62.4) * mm, "end": v(-7.6, 62.42) * mm});
            skLineSegment(sketch, "E4477", {"start": v(-7.6, 62.42) * mm, "end": v(-7.6, 62.43) * mm});
            skLineSegment(sketch, "E4478", {"start": v(-7.6, 62.43) * mm, "end": v(-7.61, 62.46) * mm});
            skLineSegment(sketch, "E4479", {"start": v(-7.61, 62.46) * mm, "end": v(-7.61, 62.48) * mm});
            skLineSegment(sketch, "E4480", {"start": v(-7.61, 62.48) * mm, "end": v(-7.6, 62.5) * mm});
            skLineSegment(sketch, "E4481", {"start": v(-7.6, 62.5) * mm, "end": v(-7.6, 62.51) * mm});
            skLineSegment(sketch, "E4482", {"start": v(-7.6, 62.51) * mm, "end": v(-7.59, 62.52) * mm});
            skLineSegment(sketch, "E4483", {"start": v(-7.59, 62.52) * mm, "end": v(-7.57, 62.53) * mm});
            skLineSegment(sketch, "E4484", {"start": v(-7.57, 62.53) * mm, "end": v(-7.56, 62.53) * mm});
            skLineSegment(sketch, "E4485", {"start": v(-7.56, 62.53) * mm, "end": v(-7.54, 62.52) * mm});
            skLineSegment(sketch, "E4486", {"start": v(-7.54, 62.52) * mm, "end": v(-7.53, 62.52) * mm});
            skLineSegment(sketch, "E4487", {"start": v(-7.42, 62.4) * mm, "end": v(-7.48, 62.4) * mm});
            skLineSegment(sketch, "E4488", {"start": v(-7.48, 62.4) * mm, "end": v(-7.48, 62.53) * mm});
            skLineSegment(sketch, "E4489", {"start": v(-10.2, 62.4) * mm, "end": v(-10.18, 62.4) * mm});
            skLineSegment(sketch, "E4490", {"start": v(-10.18, 62.4) * mm, "end": v(-10.15, 62.4) * mm});
            skLineSegment(sketch, "E4491", {"start": v(-10.15, 62.4) * mm, "end": v(-10.14, 62.4) * mm});
            skLineSegment(sketch, "E4492", {"start": v(-10.14, 62.4) * mm, "end": v(-10.13, 62.42) * mm});
            skLineSegment(sketch, "E4493", {"start": v(-10.13, 62.42) * mm, "end": v(-10.13, 62.43) * mm});
            skLineSegment(sketch, "E4494", {"start": v(-10.13, 62.43) * mm, "end": v(-10.13, 62.44) * mm});
            skLineSegment(sketch, "E4495", {"start": v(-10.13, 62.44) * mm, "end": v(-10.13, 62.45) * mm});
            skLineSegment(sketch, "E4496", {"start": v(-10.13, 62.45) * mm, "end": v(-10.14, 62.46) * mm});
            skLineSegment(sketch, "E4497", {"start": v(-10.14, 62.46) * mm, "end": v(-10.15, 62.46) * mm});
            skLineSegment(sketch, "E4498", {"start": v(-10.15, 62.46) * mm, "end": v(-10.17, 62.47) * mm});
            skLineSegment(sketch, "E4499", {"start": v(-10.17, 62.47) * mm, "end": v(-10.19, 62.48) * mm});
            skLineSegment(sketch, "E4500", {"start": v(-10.19, 62.48) * mm, "end": v(-10.2, 62.48) * mm});
            skLineSegment(sketch, "E4501", {"start": v(-10.2, 62.48) * mm, "end": v(-10.2, 62.5) * mm});
            skLineSegment(sketch, "E4502", {"start": v(-10.2, 62.5) * mm, "end": v(-10.2, 62.5) * mm});
            skLineSegment(sketch, "E4503", {"start": v(-10.2, 62.5) * mm, "end": v(-10.2, 62.52) * mm});
            skLineSegment(sketch, "E4504", {"start": v(-10.2, 62.52) * mm, "end": v(-10.19, 62.52) * mm});
            skLineSegment(sketch, "E4505", {"start": v(-10.19, 62.52) * mm, "end": v(-10.17, 62.53) * mm});
            skLineSegment(sketch, "E4506", {"start": v(-10.17, 62.53) * mm, "end": v(-10.14, 62.53) * mm});
            skLineSegment(sketch, "E4507", {"start": v(-10.14, 62.53) * mm, "end": v(-10.13, 62.52) * mm});
            skLineSegment(sketch, "E4508", {"start": v(-10.07, 62.4) * mm, "end": v(-10.07, 62.53) * mm});
            skLineSegment(sketch, "E4509", {"start": v(-10.07, 62.53) * mm, "end": v(-10.04, 62.53) * mm});
            skLineSegment(sketch, "E4510", {"start": v(-10.04, 62.53) * mm, "end": v(-10.03, 62.52) * mm});
            skLineSegment(sketch, "E4511", {"start": v(-10.03, 62.52) * mm, "end": v(-10.01, 62.51) * mm});
            skLineSegment(sketch, "E4512", {"start": v(-10.01, 62.51) * mm, "end": v(-10, 62.5) * mm});
            skLineSegment(sketch, "E4513", {"start": v(-10, 62.5) * mm, "end": v(-10, 62.48) * mm});
            skLineSegment(sketch, "E4514", {"start": v(-10, 62.48) * mm, "end": v(-10, 62.46) * mm});
            skLineSegment(sketch, "E4515", {"start": v(-10, 62.46) * mm, "end": v(-10, 62.43) * mm});
            skLineSegment(sketch, "E4516", {"start": v(-10, 62.43) * mm, "end": v(-10.01, 62.42) * mm});
            skLineSegment(sketch, "E4517", {"start": v(-10.01, 62.42) * mm, "end": v(-10.03, 62.4) * mm});
            skLineSegment(sketch, "E4518", {"start": v(-10.03, 62.4) * mm, "end": v(-10.04, 62.4) * mm});
            skLineSegment(sketch, "E4519", {"start": v(-10.04, 62.4) * mm, "end": v(-10.07, 62.4) * mm});
            skLineSegment(sketch, "E4520", {"start": v(-9.95, 62.44) * mm, "end": v(-9.9, 62.44) * mm});
            skLineSegment(sketch, "E4521", {"start": v(-9.96, 62.4) * mm, "end": v(-9.92, 62.53) * mm});
            skLineSegment(sketch, "E4522", {"start": v(-9.92, 62.53) * mm, "end": v(-9.88, 62.4) * mm});
            skLineSegment(sketch, "E4523", {"start": v(-12.58, 62.4) * mm, "end": v(-12.62, 62.46) * mm});
            skLineSegment(sketch, "E4524", {"start": v(-12.65, 62.4) * mm, "end": v(-12.65, 62.53) * mm});
            skLineSegment(sketch, "E4525", {"start": v(-12.65, 62.53) * mm, "end": v(-12.6, 62.53) * mm});
            skLineSegment(sketch, "E4526", {"start": v(-12.6, 62.53) * mm, "end": v(-12.6, 62.52) * mm});
            skLineSegment(sketch, "E4527", {"start": v(-12.6, 62.52) * mm, "end": v(-12.59, 62.52) * mm});
            skLineSegment(sketch, "E4528", {"start": v(-12.59, 62.52) * mm, "end": v(-12.58, 62.5) * mm});
            skLineSegment(sketch, "E4529", {"start": v(-12.58, 62.5) * mm, "end": v(-12.58, 62.49) * mm});
            skLineSegment(sketch, "E4530", {"start": v(-12.58, 62.49) * mm, "end": v(-12.59, 62.48) * mm});
            skLineSegment(sketch, "E4531", {"start": v(-12.59, 62.48) * mm, "end": v(-12.6, 62.47) * mm});
            skLineSegment(sketch, "E4532", {"start": v(-12.6, 62.47) * mm, "end": v(-12.6, 62.46) * mm});
            skLineSegment(sketch, "E4533", {"start": v(-12.6, 62.46) * mm, "end": v(-12.65, 62.46) * mm});
            skLineSegment(sketch, "E4534", {"start": v(-12.54, 62.53) * mm, "end": v(-12.45, 62.4) * mm});
            skLineSegment(sketch, "E4535", {"start": v(-12.45, 62.53) * mm, "end": v(-12.54, 62.4) * mm});
            skLineSegment(sketch, "E4536", {"start": v(-15.32, 62.53) * mm, "end": v(-15.25, 62.53) * mm});
            skLineSegment(sketch, "E4537", {"start": v(-15.29, 62.4) * mm, "end": v(-15.29, 62.53) * mm});
            skLineSegment(sketch, "E4538", {"start": v(-15.22, 62.53) * mm, "end": v(-15.14, 62.4) * mm});
            skLineSegment(sketch, "E4539", {"start": v(-15.14, 62.53) * mm, "end": v(-15.22, 62.4) * mm});
            skLineSegment(sketch, "E4540", {"start": v(-17.9, 62.47) * mm, "end": v(-17.94, 62.47) * mm});
            skLineSegment(sketch, "E4541", {"start": v(-17.94, 62.4) * mm, "end": v(-17.94, 62.53) * mm});
            skLineSegment(sketch, "E4542", {"start": v(-17.94, 62.53) * mm, "end": v(-17.88, 62.53) * mm});
            skLineSegment(sketch, "E4543", {"start": v(-17.83, 62.47) * mm, "end": v(-17.8, 62.47) * mm});
            skLineSegment(sketch, "E4544", {"start": v(-17.77, 62.4) * mm, "end": v(-17.83, 62.4) * mm});
            skLineSegment(sketch, "E4545", {"start": v(-17.83, 62.4) * mm, "end": v(-17.83, 62.53) * mm});
            skLineSegment(sketch, "E4546", {"start": v(-17.83, 62.53) * mm, "end": v(-17.77, 62.53) * mm});
            skLineSegment(sketch, "E4547", {"start": v(-17.74, 62.53) * mm, "end": v(-17.67, 62.53) * mm});
            skLineSegment(sketch, "E4548", {"start": v(-17.7, 62.4) * mm, "end": v(-17.7, 62.53) * mm});
            skLineSegment(sketch, "E4549", {"start": v(-17.65, 62.4) * mm, "end": v(-17.56, 62.4) * mm});
            skLineSegment(sketch, "E4550", {"start": v(-17.53, 62.4) * mm, "end": v(-17.53, 62.53) * mm});
            skLineSegment(sketch, "E4551", {"start": v(-17.46, 62.4) * mm, "end": v(-17.46, 62.53) * mm});
            skLineSegment(sketch, "E4552", {"start": v(-17.46, 62.53) * mm, "end": v(-17.4, 62.4) * mm});
            skLineSegment(sketch, "E4553", {"start": v(-17.4, 62.4) * mm, "end": v(-17.4, 62.53) * mm});
            skLineSegment(sketch, "E4554", {"start": v(-17.33, 62.45) * mm, "end": v(-17.24, 62.45) * mm});
            skLineSegment(sketch, "E4555", {"start": v(-17.29, 62.4) * mm, "end": v(-17.29, 62.5) * mm});
            skLineSegment(sketch, "E4556", {"start": v(-20.5, 62.4) * mm, "end": v(-20.48, 62.4) * mm});
            skLineSegment(sketch, "E4557", {"start": v(-20.48, 62.4) * mm, "end": v(-20.45, 62.4) * mm});
            skLineSegment(sketch, "E4558", {"start": v(-20.45, 62.4) * mm, "end": v(-20.44, 62.4) * mm});
            skLineSegment(sketch, "E4559", {"start": v(-20.44, 62.4) * mm, "end": v(-20.43, 62.42) * mm});
            skLineSegment(sketch, "E4560", {"start": v(-20.43, 62.42) * mm, "end": v(-20.42, 62.43) * mm});
            skLineSegment(sketch, "E4561", {"start": v(-20.42, 62.43) * mm, "end": v(-20.42, 62.44) * mm});
            skLineSegment(sketch, "E4562", {"start": v(-20.42, 62.44) * mm, "end": v(-20.43, 62.45) * mm});
            skLineSegment(sketch, "E4563", {"start": v(-20.43, 62.45) * mm, "end": v(-20.44, 62.46) * mm});
            skLineSegment(sketch, "E4564", {"start": v(-20.44, 62.46) * mm, "end": v(-20.45, 62.46) * mm});
            skLineSegment(sketch, "E4565", {"start": v(-20.45, 62.46) * mm, "end": v(-20.47, 62.47) * mm});
            skLineSegment(sketch, "E4566", {"start": v(-20.47, 62.47) * mm, "end": v(-20.49, 62.48) * mm});
            skLineSegment(sketch, "E4567", {"start": v(-20.49, 62.48) * mm, "end": v(-20.5, 62.48) * mm});
            skLineSegment(sketch, "E4568", {"start": v(-20.5, 62.48) * mm, "end": v(-20.5, 62.5) * mm});
            skLineSegment(sketch, "E4569", {"start": v(-20.5, 62.5) * mm, "end": v(-20.5, 62.5) * mm});
            skLineSegment(sketch, "E4570", {"start": v(-20.5, 62.5) * mm, "end": v(-20.5, 62.52) * mm});
            skLineSegment(sketch, "E4571", {"start": v(-20.5, 62.52) * mm, "end": v(-20.49, 62.52) * mm});
            skLineSegment(sketch, "E4572", {"start": v(-20.49, 62.52) * mm, "end": v(-20.47, 62.53) * mm});
            skLineSegment(sketch, "E4573", {"start": v(-20.47, 62.53) * mm, "end": v(-20.44, 62.53) * mm});
            skLineSegment(sketch, "E4574", {"start": v(-20.44, 62.53) * mm, "end": v(-20.42, 62.52) * mm});
            skLineSegment(sketch, "E4575", {"start": v(-20.3, 62.42) * mm, "end": v(-20.3, 62.4) * mm});
            skLineSegment(sketch, "E4576", {"start": v(-20.3, 62.4) * mm, "end": v(-20.32, 62.4) * mm});
            skLineSegment(sketch, "E4577", {"start": v(-20.32, 62.4) * mm, "end": v(-20.33, 62.4) * mm});
            skLineSegment(sketch, "E4578", {"start": v(-20.33, 62.4) * mm, "end": v(-20.35, 62.4) * mm});
            skLineSegment(sketch, "E4579", {"start": v(-20.35, 62.4) * mm, "end": v(-20.36, 62.42) * mm});
            skLineSegment(sketch, "E4580", {"start": v(-20.36, 62.42) * mm, "end": v(-20.37, 62.43) * mm});
            skLineSegment(sketch, "E4581", {"start": v(-20.37, 62.43) * mm, "end": v(-20.38, 62.46) * mm});
            skLineSegment(sketch, "E4582", {"start": v(-20.38, 62.46) * mm, "end": v(-20.38, 62.48) * mm});
            skLineSegment(sketch, "E4583", {"start": v(-20.38, 62.48) * mm, "end": v(-20.37, 62.5) * mm});
            skLineSegment(sketch, "E4584", {"start": v(-20.37, 62.5) * mm, "end": v(-20.36, 62.51) * mm});
            skLineSegment(sketch, "E4585", {"start": v(-20.36, 62.51) * mm, "end": v(-20.35, 62.52) * mm});
            skLineSegment(sketch, "E4586", {"start": v(-20.35, 62.52) * mm, "end": v(-20.33, 62.53) * mm});
            skLineSegment(sketch, "E4587", {"start": v(-20.33, 62.53) * mm, "end": v(-20.32, 62.53) * mm});
            skLineSegment(sketch, "E4588", {"start": v(-20.32, 62.53) * mm, "end": v(-20.3, 62.52) * mm});
            skLineSegment(sketch, "E4589", {"start": v(-20.3, 62.52) * mm, "end": v(-20.3, 62.52) * mm});
            skLineSegment(sketch, "E4590", {"start": v(-20.18, 62.4) * mm, "end": v(-20.24, 62.4) * mm});
            skLineSegment(sketch, "E4591", {"start": v(-20.24, 62.4) * mm, "end": v(-20.24, 62.53) * mm});
            skLineSegment(sketch, "E4592", {"start": v(-20.14, 62.4) * mm, "end": v(-20.14, 62.53) * mm});
            skLineSegment(sketch, "E4593", {"start": v(-20.07, 62.4) * mm, "end": v(-20.12, 62.48) * mm});
            skLineSegment(sketch, "E4594", {"start": v(-20.07, 62.53) * mm, "end": v(-20.14, 62.46) * mm});
            skLineSegment(sketch, "E4595", {"start": v(-22.85, 62.4) * mm, "end": v(-22.83, 62.4) * mm});
            skLineSegment(sketch, "E4596", {"start": v(-22.83, 62.4) * mm, "end": v(-22.8, 62.4) * mm});
            skLineSegment(sketch, "E4597", {"start": v(-22.8, 62.4) * mm, "end": v(-22.79, 62.4) * mm});
            skLineSegment(sketch, "E4598", {"start": v(-22.79, 62.4) * mm, "end": v(-22.78, 62.42) * mm});
            skLineSegment(sketch, "E4599", {"start": v(-22.78, 62.42) * mm, "end": v(-22.78, 62.43) * mm});
            skLineSegment(sketch, "E4600", {"start": v(-22.78, 62.43) * mm, "end": v(-22.78, 62.44) * mm});
            skLineSegment(sketch, "E4601", {"start": v(-22.78, 62.44) * mm, "end": v(-22.78, 62.45) * mm});
            skLineSegment(sketch, "E4602", {"start": v(-22.78, 62.45) * mm, "end": v(-22.79, 62.46) * mm});
            skLineSegment(sketch, "E4603", {"start": v(-22.79, 62.46) * mm, "end": v(-22.8, 62.46) * mm});
            skLineSegment(sketch, "E4604", {"start": v(-22.8, 62.46) * mm, "end": v(-22.83, 62.47) * mm});
            skLineSegment(sketch, "E4605", {"start": v(-22.83, 62.47) * mm, "end": v(-22.84, 62.48) * mm});
            skLineSegment(sketch, "E4606", {"start": v(-22.84, 62.48) * mm, "end": v(-22.84, 62.48) * mm});
            skLineSegment(sketch, "E4607", {"start": v(-22.84, 62.48) * mm, "end": v(-22.85, 62.5) * mm});
            skLineSegment(sketch, "E4608", {"start": v(-22.85, 62.5) * mm, "end": v(-22.85, 62.5) * mm});
            skLineSegment(sketch, "E4609", {"start": v(-22.85, 62.5) * mm, "end": v(-22.84, 62.52) * mm});
            skLineSegment(sketch, "E4610", {"start": v(-22.84, 62.52) * mm, "end": v(-22.84, 62.52) * mm});
            skLineSegment(sketch, "E4611", {"start": v(-22.84, 62.52) * mm, "end": v(-22.83, 62.53) * mm});
            skLineSegment(sketch, "E4612", {"start": v(-22.83, 62.53) * mm, "end": v(-22.8, 62.53) * mm});
            skLineSegment(sketch, "E4613", {"start": v(-22.8, 62.53) * mm, "end": v(-22.78, 62.52) * mm});
            skLineSegment(sketch, "E4614", {"start": v(-22.72, 62.4) * mm, "end": v(-22.72, 62.53) * mm});
            skLineSegment(sketch, "E4615", {"start": v(-22.72, 62.53) * mm, "end": v(-22.7, 62.53) * mm});
            skLineSegment(sketch, "E4616", {"start": v(-22.7, 62.53) * mm, "end": v(-22.67, 62.52) * mm});
            skLineSegment(sketch, "E4617", {"start": v(-22.67, 62.52) * mm, "end": v(-22.66, 62.51) * mm});
            skLineSegment(sketch, "E4618", {"start": v(-22.66, 62.51) * mm, "end": v(-22.66, 62.5) * mm});
            skLineSegment(sketch, "E4619", {"start": v(-22.66, 62.5) * mm, "end": v(-22.65, 62.48) * mm});
            skLineSegment(sketch, "E4620", {"start": v(-22.65, 62.48) * mm, "end": v(-22.65, 62.46) * mm});
            skLineSegment(sketch, "E4621", {"start": v(-22.65, 62.46) * mm, "end": v(-22.66, 62.43) * mm});
            skLineSegment(sketch, "E4622", {"start": v(-22.66, 62.43) * mm, "end": v(-22.66, 62.42) * mm});
            skLineSegment(sketch, "E4623", {"start": v(-22.66, 62.42) * mm, "end": v(-22.67, 62.4) * mm});
            skLineSegment(sketch, "E4624", {"start": v(-22.67, 62.4) * mm, "end": v(-22.7, 62.4) * mm});
            skLineSegment(sketch, "E4625", {"start": v(-22.7, 62.4) * mm, "end": v(-22.72, 62.4) * mm});
            skLineSegment(sketch, "E4626", {"start": v(-22.6, 62.4) * mm, "end": v(-22.6, 62.53) * mm});
            skLineSegment(sketch, "E4627", {"start": v(-25.5, 62.4) * mm, "end": v(-25.48, 62.4) * mm});
            skLineSegment(sketch, "E4628", {"start": v(-25.48, 62.4) * mm, "end": v(-25.45, 62.4) * mm});
            skLineSegment(sketch, "E4629", {"start": v(-25.45, 62.4) * mm, "end": v(-25.44, 62.4) * mm});
            skLineSegment(sketch, "E4630", {"start": v(-25.44, 62.4) * mm, "end": v(-25.44, 62.42) * mm});
            skLineSegment(sketch, "E4631", {"start": v(-25.44, 62.42) * mm, "end": v(-25.43, 62.43) * mm});
            skLineSegment(sketch, "E4632", {"start": v(-25.43, 62.43) * mm, "end": v(-25.43, 62.44) * mm});
            skLineSegment(sketch, "E4633", {"start": v(-25.43, 62.44) * mm, "end": v(-25.44, 62.45) * mm});
            skLineSegment(sketch, "E4634", {"start": v(-25.44, 62.45) * mm, "end": v(-25.44, 62.46) * mm});
            skLineSegment(sketch, "E4635", {"start": v(-25.44, 62.46) * mm, "end": v(-25.45, 62.46) * mm});
            skLineSegment(sketch, "E4636", {"start": v(-25.45, 62.46) * mm, "end": v(-25.48, 62.47) * mm});
            skLineSegment(sketch, "E4637", {"start": v(-25.48, 62.47) * mm, "end": v(-25.5, 62.48) * mm});
            skLineSegment(sketch, "E4638", {"start": v(-25.5, 62.48) * mm, "end": v(-25.5, 62.48) * mm});
            skLineSegment(sketch, "E4639", {"start": v(-25.5, 62.48) * mm, "end": v(-25.5, 62.5) * mm});
            skLineSegment(sketch, "E4640", {"start": v(-25.5, 62.5) * mm, "end": v(-25.5, 62.5) * mm});
            skLineSegment(sketch, "E4641", {"start": v(-25.5, 62.5) * mm, "end": v(-25.5, 62.52) * mm});
            skLineSegment(sketch, "E4642", {"start": v(-25.5, 62.52) * mm, "end": v(-25.5, 62.52) * mm});
            skLineSegment(sketch, "E4643", {"start": v(-25.5, 62.52) * mm, "end": v(-25.48, 62.53) * mm});
            skLineSegment(sketch, "E4644", {"start": v(-25.48, 62.53) * mm, "end": v(-25.45, 62.53) * mm});
            skLineSegment(sketch, "E4645", {"start": v(-25.45, 62.53) * mm, "end": v(-25.43, 62.52) * mm});
            skLineSegment(sketch, "E4646", {"start": v(-25.37, 62.4) * mm, "end": v(-25.37, 62.53) * mm});
            skLineSegment(sketch, "E4647", {"start": v(-25.37, 62.53) * mm, "end": v(-25.35, 62.53) * mm});
            skLineSegment(sketch, "E4648", {"start": v(-25.35, 62.53) * mm, "end": v(-25.33, 62.52) * mm});
            skLineSegment(sketch, "E4649", {"start": v(-25.33, 62.52) * mm, "end": v(-25.32, 62.51) * mm});
            skLineSegment(sketch, "E4650", {"start": v(-25.32, 62.51) * mm, "end": v(-25.3, 62.5) * mm});
            skLineSegment(sketch, "E4651", {"start": v(-25.3, 62.5) * mm, "end": v(-25.3, 62.48) * mm});
            skLineSegment(sketch, "E4652", {"start": v(-25.3, 62.48) * mm, "end": v(-25.3, 62.46) * mm});
            skLineSegment(sketch, "E4653", {"start": v(-25.3, 62.46) * mm, "end": v(-25.3, 62.43) * mm});
            skLineSegment(sketch, "E4654", {"start": v(-25.3, 62.43) * mm, "end": v(-25.32, 62.42) * mm});
            skLineSegment(sketch, "E4655", {"start": v(-25.32, 62.42) * mm, "end": v(-25.33, 62.4) * mm});
            skLineSegment(sketch, "E4656", {"start": v(-25.33, 62.4) * mm, "end": v(-25.35, 62.4) * mm});
            skLineSegment(sketch, "E4657", {"start": v(-25.35, 62.4) * mm, "end": v(-25.37, 62.4) * mm});
            skLineSegment(sketch, "E4658", {"start": v(-25.22, 62.53) * mm, "end": v(-25.2, 62.53) * mm});
            skLineSegment(sketch, "E4659", {"start": v(-25.2, 62.53) * mm, "end": v(-25.19, 62.52) * mm});
            skLineSegment(sketch, "E4660", {"start": v(-25.19, 62.52) * mm, "end": v(-25.18, 62.51) * mm});
            skLineSegment(sketch, "E4661", {"start": v(-25.18, 62.51) * mm, "end": v(-25.17, 62.49) * mm});
            skLineSegment(sketch, "E4662", {"start": v(-25.17, 62.49) * mm, "end": v(-25.17, 62.45) * mm});
            skLineSegment(sketch, "E4663", {"start": v(-25.17, 62.45) * mm, "end": v(-25.18, 62.42) * mm});
            skLineSegment(sketch, "E4664", {"start": v(-25.18, 62.42) * mm, "end": v(-25.19, 62.4) * mm});
            skLineSegment(sketch, "E4665", {"start": v(-25.19, 62.4) * mm, "end": v(-25.2, 62.4) * mm});
            skLineSegment(sketch, "E4666", {"start": v(-25.2, 62.4) * mm, "end": v(-25.22, 62.4) * mm});
            skLineSegment(sketch, "E4667", {"start": v(-25.22, 62.4) * mm, "end": v(-25.24, 62.4) * mm});
            skLineSegment(sketch, "E4668", {"start": v(-25.24, 62.4) * mm, "end": v(-25.25, 62.42) * mm});
            skLineSegment(sketch, "E4669", {"start": v(-25.25, 62.42) * mm, "end": v(-25.26, 62.45) * mm});
            skLineSegment(sketch, "E4670", {"start": v(-25.26, 62.45) * mm, "end": v(-25.26, 62.49) * mm});
            skLineSegment(sketch, "E4671", {"start": v(-25.26, 62.49) * mm, "end": v(-25.25, 62.51) * mm});
            skLineSegment(sketch, "E4672", {"start": v(-25.25, 62.51) * mm, "end": v(-25.24, 62.52) * mm});
            skLineSegment(sketch, "E4673", {"start": v(-25.24, 62.52) * mm, "end": v(-25.22, 62.53) * mm});
            skLineSegment(sketch, "E4674", {"start": v(-25.92, 11.6) * mm, "end": v(18.53, 11.6) * mm});
            skLineSegment(sketch, "E4675", {"start": v(18.53, 24.3) * mm, "end": v(18.53, 11.6) * mm});
            skLineSegment(sketch, "E4676", {"start": v(-23.42, 12.62) * mm, "end": v(-23.33, 12.62) * mm});
            skLineSegment(sketch, "E4677", {"start": v(-23.42, 14.14) * mm, "end": v(-23.33, 14.14) * mm});
            skLineSegment(sketch, "E4678", {"start": v(-23.38, 14.1) * mm, "end": v(-23.38, 14.2) * mm});
            skLineSegment(sketch, "E4679", {"start": v(-25.92, 11.6) * mm, "end": v(-25.92, 24.3) * mm});
            skLineSegment(sketch, "E4680", {"start": v(-23.64, 22.13) * mm, "end": v(-23.64, 20.57) * mm});
            skLineSegment(sketch, "E4681", {"start": v(-26.73, 20.57) * mm, "end": v(-26.73, 22.13) * mm});
            skLineSegment(sketch, "E4682", {"start": v(-26.73, 22.13) * mm, "end": v(-23.64, 22.13) * mm});
            skLineSegment(sketch, "E4683", {"start": v(-45.4, -48.29) * mm, "end": v(-43.4, -48.29) * mm});
            skLineSegment(sketch, "E4684", {"start": v(-43.4, -46.24) * mm, "end": v(-45.4, -46.24) * mm});
            skLineSegment(sketch, "E4685", {"start": v(-3.67, 62.23) * mm, "end": v(-29.07, 62.23) * mm});
            skLineSegment(sketch, "E4686", {"start": v(-26.53, 57.15) * mm, "end": v(-3.67, 57.15) * mm});
            skLineSegment(sketch, "E4687", {"start": v(-3.67, 62.23) * mm, "end": v(-3.67, 57.15) * mm});
            skLineSegment(sketch, "E4688", {"start": v(-29.07, 62.23) * mm, "end": v(-29.07, 59.69) * mm});
            skLineSegment(sketch, "E4689", {"start": v(-29.35, 58.42) * mm, "end": v(-29.35, 56.87) * mm});
            skLineSegment(sketch, "E4690", {"start": v(-29.07, 59.69) * mm, "end": v(-26.53, 59.69) * mm});
            skLineSegment(sketch, "E4691", {"start": v(-26.53, 59.69) * mm, "end": v(-26.53, 57.15) * mm});
            skLineSegment(sketch, "E4692", {"start": v(-29.35, 56.87) * mm, "end": v(-27.8, 56.87) * mm});
            skLineSegment(sketch, "E4693", {"start": v(43.74, 61.14) * mm, "end": v(58.14, 61.14) * mm});
            skLineSegment(sketch, "E4694", {"start": v(58.14, 61.14) * mm, "end": v(58.14, 45.54) * mm});
            skLineSegment(sketch, "E4695", {"start": v(58.14, 45.54) * mm, "end": v(43.74, 45.54) * mm});
            skLineSegment(sketch, "E4696", {"start": v(43.74, 45.54) * mm, "end": v(43.74, 61.14) * mm});
            skLineSegment(sketch, "E4697", {"start": v(-58.28, -63.5) * mm, "end": v(-58.28, -12.7) * mm});
            skLineSegment(sketch, "E4698", {"start": v(-63.36, -15.24) * mm, "end": v(-63.36, -63.5) * mm});
            skLineSegment(sketch, "E4699", {"start": v(-58.28, -63.5) * mm, "end": v(-63.36, -63.5) * mm});
            skLineSegment(sketch, "E4700", {"start": v(-58.28, -12.7) * mm, "end": v(-60.82, -12.7) * mm});
            skLineSegment(sketch, "E4701", {"start": v(-62.1, -12.42) * mm, "end": v(-63.64, -12.42) * mm});
            skLineSegment(sketch, "E4702", {"start": v(-60.82, -12.7) * mm, "end": v(-60.82, -15.24) * mm});
            skLineSegment(sketch, "E4703", {"start": v(-60.82, -15.24) * mm, "end": v(-63.36, -15.24) * mm});
            skLineSegment(sketch, "E4704", {"start": v(-63.64, -12.42) * mm, "end": v(-63.64, -13.97) * mm});
            skLineSegment(sketch, "E4705", {"start": v(43.74, 43.36) * mm, "end": v(58.14, 43.36) * mm});
            skLineSegment(sketch, "E4706", {"start": v(58.14, 43.36) * mm, "end": v(58.14, 27.76) * mm});
            skLineSegment(sketch, "E4707", {"start": v(58.14, 27.76) * mm, "end": v(43.74, 27.76) * mm});
            skLineSegment(sketch, "E4708", {"start": v(43.74, 27.76) * mm, "end": v(43.74, 43.36) * mm});
            skLineSegment(sketch, "E4709", {"start": v(-61.82, 42.77) * mm, "end": v(-59.82, 42.77) * mm});
            skLineSegment(sketch, "E4710", {"start": v(-59.82, 42.77) * mm, "end": v(-59.82, 40.77) * mm});
            skLineSegment(sketch, "E4711", {"start": v(-59.82, 40.77) * mm, "end": v(-61.82, 40.77) * mm});
            skLineSegment(sketch, "E4712", {"start": v(-61.82, 40.77) * mm, "end": v(-61.82, 42.77) * mm});
            skLineSegment(sketch, "E4713", {"start": v(-62.32, 43.76) * mm, "end": v(-62.32, 45.27) * mm});
            skLineSegment(sketch, "E4714", {"start": v(-62.32, 45.27) * mm, "end": v(-60.82, 45.27) * mm});
            skLineSegment(sketch, "E4715", {"start": v(-61.82, 53.8) * mm, "end": v(-59.82, 53.8) * mm});
            skLineSegment(sketch, "E4716", {"start": v(-59.82, 53.8) * mm, "end": v(-59.82, 51.8) * mm});
            skLineSegment(sketch, "E4717", {"start": v(-59.82, 51.8) * mm, "end": v(-61.82, 51.8) * mm});
            skLineSegment(sketch, "E4718", {"start": v(-61.82, 51.8) * mm, "end": v(-61.82, 53.8) * mm});
            skLineSegment(sketch, "E4719", {"start": v(-47.26, -48.55) * mm, "end": v(-47.26, -49.8) * mm});
            skLineSegment(sketch, "E4720", {"start": v(-43.5, -48.55) * mm, "end": v(-47.26, -48.55) * mm});
            skLineSegment(sketch, "E4721", {"start": v(-41.25, -55.37) * mm, "end": v(-47.26, -55.37) * mm});
            skLineSegment(sketch, "E4722", {"start": v(43.74, 7.8) * mm, "end": v(58.14, 7.8) * mm});
            skLineSegment(sketch, "E4723", {"start": v(58.14, 7.8) * mm, "end": v(58.14, -7.8) * mm});
            skLineSegment(sketch, "E4724", {"start": v(58.14, -7.8) * mm, "end": v(43.74, -7.8) * mm});
            skLineSegment(sketch, "E4725", {"start": v(43.74, -7.8) * mm, "end": v(43.74, 7.8) * mm});
            skLineSegment(sketch, "E4726", {"start": v(43.74, 25.96) * mm, "end": v(58.14, 25.96) * mm});
            skLineSegment(sketch, "E4727", {"start": v(58.14, 25.96) * mm, "end": v(58.14, 10.36) * mm});
            skLineSegment(sketch, "E4728", {"start": v(58.14, 10.36) * mm, "end": v(43.74, 10.36) * mm});
            skLineSegment(sketch, "E4729", {"start": v(43.74, 10.36) * mm, "end": v(43.74, 25.96) * mm});
            skLineSegment(sketch, "E4730", {"start": v(5.45, -51.37) * mm, "end": v(5.45, -46.17) * mm});
            skLineSegment(sketch, "E4731", {"start": v(9.1, -46.17) * mm, "end": v(9.1, -51.37) * mm});
            skLineSegment(sketch, "E4732", {"start": v(19.75, -1.25) * mm, "end": v(21.74, -1.25) * mm});
            skLineSegment(sketch, "E4733", {"start": v(21.74, -1.25) * mm, "end": v(21.74, -3.25) * mm});
            skLineSegment(sketch, "E4734", {"start": v(21.74, -3.25) * mm, "end": v(19.75, -3.25) * mm});
            skLineSegment(sketch, "E4735", {"start": v(19.75, -3.25) * mm, "end": v(19.75, -1.25) * mm});
            skLineSegment(sketch, "E4736", {"start": v(-23.56, 25.28) * mm, "end": v(-23.56, 23.72) * mm});
            skLineSegment(sketch, "E4737", {"start": v(-26.66, 23.72) * mm, "end": v(-26.66, 25.28) * mm});
            skLineSegment(sketch, "E4738", {"start": v(-26.66, 25.28) * mm, "end": v(-23.56, 25.28) * mm});
            skLineSegment(sketch, "E4739", {"start": v(-26.38, 22.45) * mm, "end": v(-23.84, 22.45) * mm});
            skLineSegment(sketch, "E4740", {"start": v(-23.4, 16.13) * mm, "end": v(-23.4, 14.58) * mm});
            skLineSegment(sketch, "E4741", {"start": v(-26.5, 14.58) * mm, "end": v(-26.5, 16.13) * mm});
            skLineSegment(sketch, "E4742", {"start": v(-26.5, 16.13) * mm, "end": v(-23.4, 16.13) * mm});
            skLineSegment(sketch, "E4743", {"start": v(-26.23, 13.3) * mm, "end": v(-23.68, 13.3) * mm});
            skLineSegment(sketch, "E4744", {"start": v(-23.46, 13.29) * mm, "end": v(-23.46, 11.74) * mm});
            skLineSegment(sketch, "E4745", {"start": v(-26.56, 11.74) * mm, "end": v(-26.56, 13.29) * mm});
            skLineSegment(sketch, "E4746", {"start": v(-26.56, 13.29) * mm, "end": v(-23.46, 13.29) * mm});
            skLineSegment(sketch, "E4747", {"start": v(-26.28, 10.46) * mm, "end": v(-23.74, 10.46) * mm});
            skLineSegment(sketch, "E4748", {"start": v(-56.2, -9.62) * mm, "end": v(-56.2, -8.86) * mm});
            skLineSegment(sketch, "E4749", {"start": v(-56.09, -1.65) * mm, "end": v(-56.09, -0.89) * mm});
            skLineSegment(sketch, "E4750", {"start": v(-55.7, -1.27) * mm, "end": v(-56.47, -1.27) * mm});
            skLineSegment(sketch, "E4751", {"start": v(-56.2, 6.89) * mm, "end": v(-56.2, 7.65) * mm});
            skLineSegment(sketch, "E4752", {"start": v(-56.09, 14.86) * mm, "end": v(-56.09, 15.62) * mm});
            skLineSegment(sketch, "E4753", {"start": v(-55.7, 15.24) * mm, "end": v(-56.47, 15.24) * mm});
            skLineSegment(sketch, "E4754", {"start": v(-63.36, 63.5) * mm, "end": v(63.64, 63.5) * mm});
            skLineSegment(sketch, "E4755", {"start": v(-63.36, 63.5) * mm, "end": v(-63.36, -63.5) * mm});
            skLineSegment(sketch, "E4756", {"start": v(-63.36, -63.5) * mm, "end": v(63.64, -63.5) * mm});
            skLineSegment(sketch, "E4757", {"start": v(63.64, 63.5) * mm, "end": v(63.64, -63.5) * mm});
            skSolve(sketch);
        }
        {
            var Q0;
            Q0=qCreatedBy(makeId("Top.planeOp"),FACE);
            var sketch = newSketch(context, id + "F1", { "sketchPlane" : qUnion([Q0])});
            skPoint(sketch, "E4758.0", {"position": v(-63.36, 63.5) * mm});
            skLineSegment(sketch, "E4758.1", {"start": v(-63.36, 63.5) * mm, "end": v(63.64, 63.5) * mm});
            skPoint(sketch, "E4758.2", {"position": v(63.64, 63.5) * mm});
            skLineSegment(sketch, "E4758.3", {"start": v(63.64, 63.5) * mm, "end": v(63.64, -63.5) * mm});
            skPoint(sketch, "E4758.4", {"position": v(63.64, -63.5) * mm});
            skLineSegment(sketch, "E4758.5", {"start": v(-63.36, -63.5) * mm, "end": v(63.64, -63.5) * mm});
            skLineSegment(sketch, "E4758.6", {"start": v(-63.36, 63.5) * mm, "end": v(-63.36, -63.5) * mm});
            skPoint(sketch, "E4758.7", {"position": v(-63.36, -63.5) * mm});
            skSolve(sketch);
        }
        {
            var Q0;
            Q0 = qSketchRegion(id + "F1", true);
            extrude(context, id + "F2", {"entities" : qUnion([Q0]), "depth" : 1.57 * mm, "offsetDistance" : 25.4 * mm});
        }
        {
            var Q0;
            Q0=makeQuery(id+"F2.opExtrude","CAP_FACE",FACE,{"disambiguationData":[OSD([sQuery(id+"F1.wireOp",EDGE,"E4758.1"),sQuery(id+"F1.wireOp",EDGE,"E4758.3"),sQuery(id+"F1.wireOp",EDGE,"E4758.5"),sQuery(id+"F1.wireOp",EDGE,"E4758.6")])],"isStart":false});
            var sketch = newSketch(context, id + "F3", { "sketchPlane" : qUnion([Q0])});
            skPoint(sketch, "E4759.0", {"position": v(-37.96, 15.24) * mm});
            skPoint(sketch, "E4759.1", {"position": v(-17.64, -20.32) * mm});
            skPoint(sketch, "E4759.2", {"position": v(30.62, -20.32) * mm});
            skPoint(sketch, "E4759.3", {"position": v(-8.17, -52.07) * mm});
            skPoint(sketch, "E4759.4", {"position": v(-27.17, -52.07) * mm});
            skPoint(sketch, "E4759.5", {"position": v(38.24, -40.64) * mm});
            skPoint(sketch, "E4759.6", {"position": v(-43.78, 57.1) * mm});
            skPoint(sketch, "E4759.7", {"position": v(30.62, 48.26) * mm});
            skPoint(sketch, "E4759.8", {"position": v(38.24, 35.56) * mm});
            skPoint(sketch, "E4759.9", {"position": v(-37.96, -40.64) * mm});
            skCircle(sketch, "E4760", {"center": v(-27.17, -52.07) * mm, "radius": 5.08 * mm});
            skCircle(sketch, "E4761", {"center": v(-8.17, -52.07) * mm, "radius": 5.08 * mm});
            skCircle(sketch, "E4762", {"center": v(-37.96, -40.64) * mm, "radius": 1.27 * mm});
            skCircle(sketch, "E4763", {"center": v(38.24, -40.64) * mm, "radius": 1.27 * mm});
            skCircle(sketch, "E4764", {"center": v(38.24, 35.56) * mm, "radius": 1.27 * mm});
            skCircle(sketch, "E4765", {"center": v(-17.64, -20.32) * mm, "radius": 5.08 * mm});
            skCircle(sketch, "E4766", {"center": v(30.62, -20.32) * mm, "radius": 5.08 * mm});
            skCircle(sketch, "E4767", {"center": v(-37.96, 15.24) * mm, "radius": 5.08 * mm});
            skSolve(sketch);
        }
        {
            var Q0;
            Q0 = qSketchRegion(id + "F3", true);
            extrude(context, id + "F4", {"entities" : qUnion([Q0]), "operationType" : NewBodyOperationType.REMOVE, "endBound" : BoundingType.THROUGH_ALL, "oppositeDirection" : true, "depth" : 25.4 * mm, "offsetDistance" : 25.4 * mm});
        }
    });
